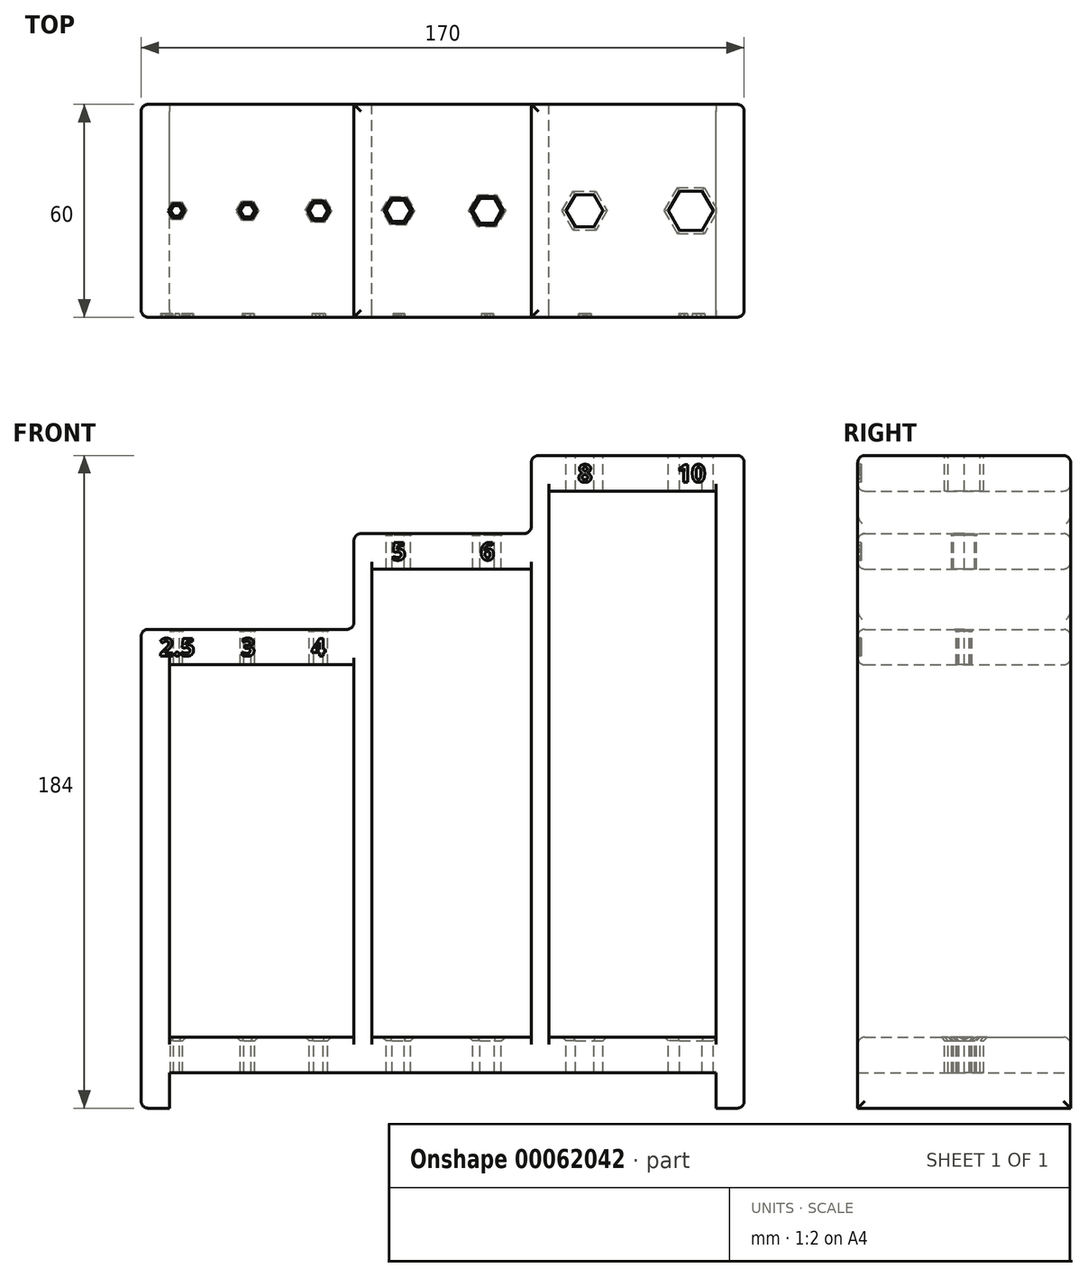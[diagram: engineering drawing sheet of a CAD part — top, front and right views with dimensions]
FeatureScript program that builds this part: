
annotation { "Feature Type Name" : "Feature", "Feature Type Description" : "" }
export const myFeature = defineFeature(function(context is Context, id is Id, definition is map)
    precondition{}
    {
        {
            var Q0;
            Q0=qCreatedBy(makeId("Front.planeOp"),FACE);
            var sketch = newSketch(context, id + "F0", { "sketchPlane" : qUnion([Q0])});
            skLineSegment(sketch, "E0", {"start": v(-75.14, -125) * mm, "end": v(-75.14, 10) * mm});
            skLineSegment(sketch, "E1", {"start": v(-15.14, 10) * mm, "end": v(-15.14, 37) * mm});
            skLineSegment(sketch, "E2", {"start": v(34.86, 37) * mm, "end": v(34.86, 59) * mm});
            skLineSegment(sketch, "E3", {"start": v(94.86, 59) * mm, "end": v(94.86, -125) * mm});
            skLineSegment(sketch, "E4", {"start": v(94.86, -125) * mm, "end": v(86.86, -125) * mm});
            skLineSegment(sketch, "E5", {"start": v(86.86, -125) * mm, "end": v(86.86, -105) * mm});
            skLineSegment(sketch, "E6", {"start": v(86.86, -105) * mm, "end": v(-67.14, -105) * mm});
            skLineSegment(sketch, "E7", {"start": v(-67.14, -105) * mm, "end": v(-67.14, -125) * mm});
            skLineSegment(sketch, "E8", {"start": v(-67.14, -125) * mm, "end": v(-75.14, -125) * mm});
            skLineSegment(sketch, "E9", {"start": v(-67.14, -115) * mm, "end": v(-67.14, 0) * mm});
            skLineSegment(sketch, "E10", {"start": v(-10.14, 0) * mm, "end": v(-10.14, 27) * mm});
            skLineSegment(sketch, "E11", {"start": v(39.86, 27) * mm, "end": v(39.86, 49) * mm});
            skLineSegment(sketch, "E12", {"start": v(86.86, 49) * mm, "end": v(86.86, -115) * mm});
            skLineSegment(sketch, "E13", {"start": v(86.86, -115) * mm, "end": v(-67.14, -115) * mm});
            skLineSegment(sketch, "E14", {"start": v(-15.14, 10) * mm, "end": v(-15.14, 0) * mm, "construction": true});
            skLineSegment(sketch, "E15", {"start": v(34.86, 37) * mm, "end": v(34.86, 27) * mm, "construction": true});
            skLineSegment(sketch, "E16", {"start": v(-67.14, -115) * mm, "end": v(-75.14, -115) * mm, "construction": true});
            skLineSegment(sketch, "E17", {"start": v(86.86, -115) * mm, "end": v(94.86, -115) * mm, "construction": true});
            skLineSegment(sketch, "E18.top", {"start": v(-15.14, -105) * mm, "end": v(-10.14, -105) * mm});
            skLineSegment(sketch, "E18.left", {"start": v(-15.14, 0) * mm, "end": v(-15.14, -105) * mm});
            skLineSegment(sketch, "E18.right", {"start": v(-10.14, 0) * mm, "end": v(-10.14, -105) * mm});
            skLineSegment(sketch, "E19.top", {"start": v(34.86, -105) * mm, "end": v(39.86, -105) * mm});
            skLineSegment(sketch, "E19.left", {"start": v(34.86, 27) * mm, "end": v(34.86, -105) * mm});
            skLineSegment(sketch, "E19.right", {"start": v(39.86, 27) * mm, "end": v(39.86, -105) * mm});
            skLineSegment(sketch, "E20", {"start": v(-75.14, 10) * mm, "end": v(-15.14, 10) * mm});
            skLineSegment(sketch, "E21", {"start": v(-67.14, 0) * mm, "end": v(-15.14, 0) * mm});
            skLineSegment(sketch, "E22", {"start": v(-15.14, 37) * mm, "end": v(34.86, 37) * mm});
            skLineSegment(sketch, "E23", {"start": v(-10.14, 27) * mm, "end": v(34.86, 27) * mm});
            skLineSegment(sketch, "E24", {"start": v(-15.14, 0) * mm, "end": v(-10.14, 0) * mm, "construction": true});
            skLineSegment(sketch, "E25", {"start": v(34.86, 27) * mm, "end": v(39.86, 27) * mm, "construction": true});
            skLineSegment(sketch, "E26", {"start": v(34.86, 59) * mm, "end": v(94.86, 59) * mm});
            skLineSegment(sketch, "E27", {"start": v(39.86, 49) * mm, "end": v(86.86, 49) * mm});
            skLineSegment(sketch, "E28", {"start": v(86.86, 49) * mm, "end": v(86.86, 59) * mm, "construction": true});
            skSolve(sketch);
        }
        {
            var Q0;
            Q0=makeQuery(id+"F0.imprint","IMPRINT",FACE,{"disambiguationData":[TD([[makeQuery(id+"F0.imprint","IMPRINT",EDGE,{"derivedFrom":sQuery(id+"F0.wireOp",EDGE,"E0")}),-1.0]])]});
            var Q1;
            {var subQ0=sQuery(id+"F0.wireOp",EDGE,"E6");Q1=makeQuery(id+"F0.imprint","IMPRINT",FACE,{"disambiguationData":[TD([[makeQuery(id+"F0.imprint","IMPRINT",EDGE,{"derivedFrom":subQ0}),1.0]])]});}
            var Q2;
            Q2=makeQuery(id+"F0.imprint","IMPRINT",FACE,{"disambiguationData":[TD([[makeQuery(id+"F0.imprint","IMPRINT",EDGE,{"derivedFrom":sQuery(id+"F0.wireOp",EDGE,"E18.bottom")}),-1.0]])]});
            var Q3;
            Q3=makeQuery(id+"F0.imprint","IMPRINT",FACE,{"disambiguationData":[TD([[makeQuery(id+"F0.imprint","IMPRINT",EDGE,{"derivedFrom":sQuery(id+"F0.wireOp",EDGE,"E19.bottom")}),-1.0]])]});
            extrude(context, id + "F1", {"entities" : qUnion([Q0, Q1, Q2, Q3]), "depth" : 30 * mm, "hasSecondDirection" : true, "secondDirectionOppositeDirection" : true, "secondDirectionDepth" : 30 * mm});
        }
        {
            var Q0;
            Q0=makeQuery(id+"F1.opExtrude","SWEPT_FACE",FACE,{"disambiguationData":[OSD([sQuery(id+"F0.wireOp",EDGE,"E26")])]});
            var sketch = newSketch(context, id + "F2", { "sketchPlane" : qUnion([Q0])});
            skPoint(sketch, "E29", {"position": v(-65.14, 0) * mm});
            skPoint(sketch, "E30", {"position": v(-45.14, 0) * mm});
            skPoint(sketch, "E31", {"position": v(-25.14, 0) * mm});
            skPoint(sketch, "E32", {"position": v(-2.64, 0) * mm});
            skPoint(sketch, "E33", {"position": v(22.36, 0) * mm});
            skPoint(sketch, "E34", {"position": v(49.86, 0) * mm});
            skPoint(sketch, "E35", {"position": v(79.86, 0) * mm});
            skCircle(sketch, "E36.cCircle", {"center": v(-65.14, 0) * mm, "radius": 1.5 * mm, "construction": true});
            skLineSegment(sketch, "E36.0", {"start": v(-64.27, -1.5) * mm, "end": v(-66, -1.5) * mm});
            skLineSegment(sketch, "E36.1", {"start": v(-66, -1.5) * mm, "end": v(-66.87, 0) * mm});
            skLineSegment(sketch, "E36.2", {"start": v(-66.87, 0) * mm, "end": v(-66, 1.5) * mm});
            skLineSegment(sketch, "E36.3", {"start": v(-66, 1.5) * mm, "end": v(-64.27, 1.5) * mm});
            skLineSegment(sketch, "E36.4", {"start": v(-64.27, 1.5) * mm, "end": v(-63.4, 0) * mm});
            skLineSegment(sketch, "E36.5", {"start": v(-63.4, 0) * mm, "end": v(-64.27, -1.5) * mm});
            skPoint(sketch, "E36.0.midPoint", {"position": v(-65.14, -1.5) * mm});
            skCircle(sketch, "E37.cCircle", {"center": v(-45.14, 0) * mm, "radius": 1.75 * mm, "construction": true});
            skLineSegment(sketch, "E37.0", {"start": v(-44.13, -1.75) * mm, "end": v(-46.15, -1.75) * mm});
            skLineSegment(sketch, "E37.1", {"start": v(-46.15, -1.75) * mm, "end": v(-47.16, 0) * mm});
            skLineSegment(sketch, "E37.2", {"start": v(-47.16, 0) * mm, "end": v(-46.15, 1.75) * mm});
            skLineSegment(sketch, "E37.3", {"start": v(-46.15, 1.75) * mm, "end": v(-44.13, 1.75) * mm});
            skLineSegment(sketch, "E37.4", {"start": v(-44.13, 1.75) * mm, "end": v(-43.12, 0) * mm});
            skLineSegment(sketch, "E37.5", {"start": v(-43.12, 0) * mm, "end": v(-44.13, -1.75) * mm});
            skPoint(sketch, "E37.0.midPoint", {"position": v(-45.14, -1.75) * mm});
            skCircle(sketch, "E38.cCircle", {"center": v(-25.14, 0) * mm, "radius": 2.25 * mm, "construction": true});
            skLineSegment(sketch, "E38.0", {"start": v(-23.84, -2.25) * mm, "end": v(-26.44, -2.25) * mm});
            skLineSegment(sketch, "E38.1", {"start": v(-26.44, -2.25) * mm, "end": v(-27.74, 0) * mm});
            skLineSegment(sketch, "E38.2", {"start": v(-27.74, 0) * mm, "end": v(-26.44, 2.25) * mm});
            skLineSegment(sketch, "E38.3", {"start": v(-26.44, 2.25) * mm, "end": v(-23.84, 2.25) * mm});
            skLineSegment(sketch, "E38.4", {"start": v(-23.84, 2.25) * mm, "end": v(-22.54, 0) * mm});
            skLineSegment(sketch, "E38.5", {"start": v(-22.54, 0) * mm, "end": v(-23.84, -2.25) * mm});
            skPoint(sketch, "E38.0.midPoint", {"position": v(-25.14, -2.25) * mm});
            skCircle(sketch, "E39.cCircle", {"center": v(-2.64, 0) * mm, "radius": 3 * mm, "construction": true});
            skLineSegment(sketch, "E39.0", {"start": v(-0.9, -3) * mm, "end": v(-4.37, -3) * mm});
            skLineSegment(sketch, "E39.1", {"start": v(-4.37, -3) * mm, "end": v(-6.1, 0) * mm});
            skLineSegment(sketch, "E39.2", {"start": v(-6.1, 0) * mm, "end": v(-4.37, 3) * mm});
            skLineSegment(sketch, "E39.3", {"start": v(-4.37, 3) * mm, "end": v(-0.9, 3) * mm});
            skLineSegment(sketch, "E39.4", {"start": v(-0.9, 3) * mm, "end": v(0.82, 0) * mm});
            skLineSegment(sketch, "E39.5", {"start": v(0.82, 0) * mm, "end": v(-0.9, -3) * mm});
            skPoint(sketch, "E39.0.midPoint", {"position": v(-2.64, -3) * mm});
            skCircle(sketch, "E40.cCircle", {"center": v(22.36, 0) * mm, "radius": 3.5 * mm, "construction": true});
            skLineSegment(sketch, "E40.0", {"start": v(24.38, -3.5) * mm, "end": v(20.34, -3.5) * mm});
            skLineSegment(sketch, "E40.1", {"start": v(20.34, -3.5) * mm, "end": v(18.32, 0) * mm});
            skLineSegment(sketch, "E40.2", {"start": v(18.32, 0) * mm, "end": v(20.34, 3.5) * mm});
            skLineSegment(sketch, "E40.3", {"start": v(20.34, 3.5) * mm, "end": v(24.38, 3.5) * mm});
            skLineSegment(sketch, "E40.4", {"start": v(24.38, 3.5) * mm, "end": v(26.4, 0) * mm});
            skLineSegment(sketch, "E40.5", {"start": v(26.4, 0) * mm, "end": v(24.38, -3.5) * mm});
            skPoint(sketch, "E40.0.midPoint", {"position": v(22.36, -3.5) * mm});
            skCircle(sketch, "E41.cCircle", {"center": v(49.86, 0) * mm, "radius": 4.5 * mm, "construction": true});
            skLineSegment(sketch, "E41.0", {"start": v(52.46, -4.5) * mm, "end": v(47.26, -4.5) * mm});
            skLineSegment(sketch, "E41.1", {"start": v(47.26, -4.5) * mm, "end": v(44.66, 0) * mm});
            skLineSegment(sketch, "E41.2", {"start": v(44.66, 0) * mm, "end": v(47.26, 4.5) * mm});
            skLineSegment(sketch, "E41.3", {"start": v(47.26, 4.5) * mm, "end": v(52.46, 4.5) * mm});
            skLineSegment(sketch, "E41.4", {"start": v(52.46, 4.5) * mm, "end": v(55.06, 0) * mm});
            skLineSegment(sketch, "E41.5", {"start": v(55.06, 0) * mm, "end": v(52.46, -4.5) * mm});
            skPoint(sketch, "E41.0.midPoint", {"position": v(49.86, -4.5) * mm});
            skCircle(sketch, "E42.cCircle", {"center": v(79.86, 0) * mm, "radius": 5.5 * mm, "construction": true});
            skLineSegment(sketch, "E42.0", {"start": v(83.04, -5.5) * mm, "end": v(76.68, -5.5) * mm});
            skLineSegment(sketch, "E42.1", {"start": v(76.68, -5.5) * mm, "end": v(73.5, 0) * mm});
            skLineSegment(sketch, "E42.2", {"start": v(73.5, 0) * mm, "end": v(76.68, 5.5) * mm});
            skLineSegment(sketch, "E42.3", {"start": v(76.68, 5.5) * mm, "end": v(83.04, 5.5) * mm});
            skLineSegment(sketch, "E42.4", {"start": v(83.04, 5.5) * mm, "end": v(86.21, 0) * mm});
            skLineSegment(sketch, "E42.5", {"start": v(86.21, 0) * mm, "end": v(83.04, -5.5) * mm});
            skPoint(sketch, "E42.0.midPoint", {"position": v(79.86, -5.5) * mm});
            skSolve(sketch);
        }
        {
            var Q0;
            Q0 = qSketchRegion(id + "F2", true);
            var Q1;
            Q1=makeQuery(id+"F1.opExtrude","SWEPT_FACE",FACE,{"disambiguationData":[OSD([sQuery(id+"F0.wireOp",EDGE,"E13")])]});
            extrude(context, id + "F3", {"entities" : qUnion([Q0]), "operationType" : NewBodyOperationType.REMOVE, "endBound" : BoundingType.UP_TO_SURFACE, "oppositeDirection" : true, "endBoundEntityFace" : qUnion([Q1]), "depth" : 25 * mm});
        }
        {
            var Q0;
            Q0=makeQuery(id+"F1.opExtrude","CAP_FACE",FACE,{"disambiguationData":[OSD([sQuery(id+"F0.wireOp",EDGE,"E0"),sQuery(id+"F0.wireOp",EDGE,"GeTEZKgD-VleB-Pjne-Csjp-ZGMRxHWfVuPL"),sQuery(id+"F0.wireOp",EDGE,"BGaEOWcr-Agjj-6xs9-L2Rh-NUqZqpChWdlD"),sQuery(id+"F0.wireOp",EDGE,"vs9bMPzk-kOSz-00Uc-mebz-TYH7VpvHUvR8"),sQuery(id+"F0.wireOp",EDGE,"E1"),sQuery(id+"F0.wireOp",EDGE,"rwazvfQN-wWWd-rmfp-GgQa-C1WE00IXPOYZ"),sQuery(id+"F0.wireOp",EDGE,"TIjLVdis-FRbo-cTZn-IHn7-8XoxnhnPgcRK"),sQuery(id+"F0.wireOp",EDGE,"E2"),sQuery(id+"F0.wireOp",EDGE,"HWJ4689Y-KtwG-vJfG-xgFW-nUAPGrujgrIx"),sQuery(id+"F0.wireOp",EDGE,"6eoJVVgg-XjGH-Rh0S-0Ck7-eEfTqSEG6dff"),sQuery(id+"F0.wireOp",EDGE,"E3"),sQuery(id+"F0.wireOp",EDGE,"E4"),sQuery(id+"F0.wireOp",EDGE,"E5"),sQuery(id+"F0.wireOp",EDGE,"E6"),sQuery(id+"F0.wireOp",EDGE,"E7"),sQuery(id+"F0.wireOp",EDGE,"E8"),sQuery(id+"F0.wireOp",EDGE,"E9"),sQuery(id+"F0.wireOp",EDGE,"dsDfZTNB-jOaL-EM2F-YRw7-LjKbeeutn0S7"),sQuery(id+"F0.wireOp",EDGE,"riOj0wsW-8ntY-M8XJ-Dudd-JfplwehwjU5x"),sQuery(id+"F0.wireOp",EDGE,"ikqcAXUb-zJlV-DiQM-P86k-rxCfW60V950E"),sQuery(id+"F0.wireOp",EDGE,"E10"),sQuery(id+"F0.wireOp",EDGE,"oe37zDZS-dTc5-Nd6g-8xnc-qUGsxS7KHp88"),sQuery(id+"F0.wireOp",EDGE,"aYTTs3A4-9fB0-4VRp-raIi-XGU3Sh0ihZd7"),sQuery(id+"F0.wireOp",EDGE,"E11"),sQuery(id+"F0.wireOp",EDGE,"6ZUmFo40-9iyz-N38K-DDh6-QmUHhMkESyf1"),sQuery(id+"F0.wireOp",EDGE,"4iT4Aycs-cVef-0BnO-rxrT-2gsYZ1b7QhIN"),sQuery(id+"F0.wireOp",EDGE,"E12"),sQuery(id+"F0.wireOp",EDGE,"E13")])],"isStart":false});
            var sketch = newSketch(context, id + "F4", { "sketchPlane" : qUnion([Q0])});
            skLineSegment(sketch, "E43", {"start": v(-65.14, 10) * mm, "end": v(-65.14, 0) * mm, "construction": true});
            skText(sketch, "E44", { "text": "2.5", "fontName": "OpenSans-Bold.ttf"});
            skPoint(sketch, "E45", {"position": v(-65.14, 5) * mm});
            skLineSegment(sketch, "E46", {"start": v(-45.14, 10) * mm, "end": v(-45.14, 0) * mm, "construction": true});
            skLineSegment(sketch, "E47", {"start": v(-25.14, 10) * mm, "end": v(-25.14, 0) * mm, "construction": true});
            skLineSegment(sketch, "E48", {"start": v(-2.64, 37) * mm, "end": v(-2.64, 27) * mm, "construction": true});
            skLineSegment(sketch, "E49", {"start": v(22.36, 37) * mm, "end": v(22.36, 27) * mm, "construction": true});
            skLineSegment(sketch, "E50", {"start": v(49.86, 59) * mm, "end": v(49.86, 49) * mm, "construction": true});
            skLineSegment(sketch, "E51", {"start": v(79.86, 59) * mm, "end": v(79.86, 49) * mm, "construction": true});
            skText(sketch, "E52", { "text": "3", "fontName": "OpenSans-Bold.ttf"});
            skPoint(sketch, "E53", {"position": v(-45.14, 5) * mm});
            skText(sketch, "E54", { "text": "4", "fontName": "OpenSans-Bold.ttf"});
            skPoint(sketch, "E55", {"position": v(-25.14, 5) * mm});
            skText(sketch, "E56", { "text": "5", "fontName": "OpenSans-Bold.ttf"});
            skPoint(sketch, "E57", {"position": v(-2.64, 32) * mm});
            skText(sketch, "E58", { "text": "6", "fontName": "OpenSans-Bold.ttf"});
            skPoint(sketch, "E59", {"position": v(22.36, 32) * mm});
            skText(sketch, "E60", { "text": "8", "fontName": "OpenSans-Bold.ttf"});
            skText(sketch, "E61", { "text": "10", "fontName": "OpenSans-Bold.ttf"});
            skPoint(sketch, "E62", {"position": v(49.86, 54) * mm});
            skPoint(sketch, "E63", {"position": v(79.86, 54) * mm});
            const initialGuessF4  = {"E44": [-0.06994, 0.0025, 1, 0, 0.005], "E52": [-0.04699, 0.0025, 1, 0, 0.005], "E54": [-0.02707, 0.0025, 1, 0, 0.005], "E56": [-0.00447, 0.0295, 1, 0, 0.005], "E58": [0.02049, 0.0295, 1, 0, 0.005], "E60": [0.048, 0.0515, 1, 0, 0.005], "E61": [0.07602, 0.0515, 1, 0, 0.005]};
            skSetInitialGuess(sketch, initialGuessF4);
            skSolve(sketch);
        }
        {
            var Q0;
            Q0 = qSketchRegion(id + "F4", true);
            extrude(context, id + "F5", {"entities" : qUnion([Q0]), "operationType" : NewBodyOperationType.REMOVE, "oppositeDirection" : true, "depth" : 1 * mm});
        }
        {
            var Q0;
            {var subQ0=sQuery(id+"F0.wireOp",EDGE,"E6");var subQ1=sQuery(id+"F0.wireOp",EDGE,"E18.top");var subQ2=makeQuery(id+"F1.opExtrude","SWEPT_FACE",FACE,{"disambiguationData":[OSD([subQ0]),TDD([makeQuery(id+"F0.imprint","IMPRINT",EDGE,{"disambiguationData":[TD([[makeQuery(id+"F0.imprint","INTERSECT",VERTEX,{"derivedFrom":[subQ0,sQuery(id+"F0.wireOp",EDGE,"E9")]}),1.0]])],"derivedFrom":subQ0})])]});var subQ4=makeQuery(id+"F1.opExtrude","SWEPT_FACE",FACE,{"disambiguationData":[OSD([subQ0]),TDD([makeQuery(id+"F0.imprint","IMPRINT",EDGE,{"disambiguationData":[TD([[makeQuery(id+"F0.imprint","INTERSECT",VERTEX,{"derivedFrom":[subQ0,subQ1,sQuery(id+"F0.wireOp",EDGE,"E18.right")]}),1.0]])],"derivedFrom":subQ0})])]});var subQ5=makeQuery(id+"F1.opExtrude","SWEPT_FACE",FACE,{"disambiguationData":[OSD([subQ0]),TDD([makeQuery(id+"F0.imprint","IMPRINT",EDGE,{"disambiguationData":[TD([[makeQuery(id+"F0.imprint","INTERSECT",VERTEX,{"derivedFrom":[subQ0,sQuery(id+"F0.wireOp",EDGE,"E12")]}),-1.0]])],"derivedFrom":subQ0})])]});Q0=qUnion([makeQuery(id+"F3.boolean.opBoolean","INTERSECT",EDGE,{"derivedFrom":[subQ5,makeQuery(id+"F3.opExtrude","SWEPT_FACE",FACE,{"disambiguationData":[OSD([sQuery(id+"F2.wireOp",EDGE,"E41.0")])]})]}),makeQuery(id+"F3.boolean.opBoolean","INTERSECT",EDGE,{"derivedFrom":[subQ5,makeQuery(id+"F3.opExtrude","SWEPT_FACE",FACE,{"disambiguationData":[OSD([sQuery(id+"F2.wireOp",EDGE,"E41.1")])]})]}),makeQuery(id+"F3.boolean.opBoolean","INTERSECT",EDGE,{"derivedFrom":[subQ5,makeQuery(id+"F3.opExtrude","SWEPT_FACE",FACE,{"disambiguationData":[OSD([sQuery(id+"F2.wireOp",EDGE,"E41.2")])]})]}),makeQuery(id+"F3.boolean.opBoolean","INTERSECT",EDGE,{"derivedFrom":[subQ5,makeQuery(id+"F3.opExtrude","SWEPT_FACE",FACE,{"disambiguationData":[OSD([sQuery(id+"F2.wireOp",EDGE,"E41.3")])]})]}),makeQuery(id+"F3.boolean.opBoolean","INTERSECT",EDGE,{"derivedFrom":[subQ5,makeQuery(id+"F3.opExtrude","SWEPT_FACE",FACE,{"disambiguationData":[OSD([sQuery(id+"F2.wireOp",EDGE,"E41.4")])]})]}),makeQuery(id+"F3.boolean.opBoolean","INTERSECT",EDGE,{"derivedFrom":[subQ5,makeQuery(id+"F3.opExtrude","SWEPT_FACE",FACE,{"disambiguationData":[OSD([sQuery(id+"F2.wireOp",EDGE,"E41.5")])]})]}),makeQuery(id+"F3.boolean.opBoolean","INTERSECT",EDGE,{"derivedFrom":[subQ5,makeQuery(id+"F3.opExtrude","SWEPT_FACE",FACE,{"disambiguationData":[OSD([sQuery(id+"F2.wireOp",EDGE,"E42.0")])]})]}),makeQuery(id+"F3.boolean.opBoolean","INTERSECT",EDGE,{"derivedFrom":[subQ5,makeQuery(id+"F3.opExtrude","SWEPT_FACE",FACE,{"disambiguationData":[OSD([sQuery(id+"F2.wireOp",EDGE,"E42.1")])]})]}),makeQuery(id+"F3.boolean.opBoolean","INTERSECT",EDGE,{"derivedFrom":[subQ5,makeQuery(id+"F3.opExtrude","SWEPT_FACE",FACE,{"disambiguationData":[OSD([sQuery(id+"F2.wireOp",EDGE,"E42.2")])]})]}),makeQuery(id+"F3.boolean.opBoolean","INTERSECT",EDGE,{"derivedFrom":[subQ5,makeQuery(id+"F3.opExtrude","SWEPT_FACE",FACE,{"disambiguationData":[OSD([sQuery(id+"F2.wireOp",EDGE,"E42.3")])]})]}),makeQuery(id+"F3.boolean.opBoolean","INTERSECT",EDGE,{"derivedFrom":[subQ5,makeQuery(id+"F3.opExtrude","SWEPT_FACE",FACE,{"disambiguationData":[OSD([sQuery(id+"F2.wireOp",EDGE,"E42.4")])]})]}),makeQuery(id+"F3.boolean.opBoolean","INTERSECT",EDGE,{"derivedFrom":[subQ5,makeQuery(id+"F3.opExtrude","SWEPT_FACE",FACE,{"disambiguationData":[OSD([sQuery(id+"F2.wireOp",EDGE,"E42.5")])]})]}),makeQuery(id+"F3.boolean.opBoolean","INTERSECT",EDGE,{"derivedFrom":[subQ4,makeQuery(id+"F3.opExtrude","SWEPT_FACE",FACE,{"disambiguationData":[OSD([sQuery(id+"F2.wireOp",EDGE,"E39.0")])]})]}),makeQuery(id+"F3.boolean.opBoolean","INTERSECT",EDGE,{"derivedFrom":[subQ4,makeQuery(id+"F3.opExtrude","SWEPT_FACE",FACE,{"disambiguationData":[OSD([sQuery(id+"F2.wireOp",EDGE,"E39.1")])]})]}),makeQuery(id+"F3.boolean.opBoolean","INTERSECT",EDGE,{"derivedFrom":[subQ4,makeQuery(id+"F3.opExtrude","SWEPT_FACE",FACE,{"disambiguationData":[OSD([sQuery(id+"F2.wireOp",EDGE,"E39.2")])]})]}),makeQuery(id+"F3.boolean.opBoolean","INTERSECT",EDGE,{"derivedFrom":[subQ4,makeQuery(id+"F3.opExtrude","SWEPT_FACE",FACE,{"disambiguationData":[OSD([sQuery(id+"F2.wireOp",EDGE,"E39.3")])]})]}),makeQuery(id+"F3.boolean.opBoolean","INTERSECT",EDGE,{"derivedFrom":[subQ4,makeQuery(id+"F3.opExtrude","SWEPT_FACE",FACE,{"disambiguationData":[OSD([sQuery(id+"F2.wireOp",EDGE,"E39.4")])]})]}),makeQuery(id+"F3.boolean.opBoolean","INTERSECT",EDGE,{"derivedFrom":[subQ4,makeQuery(id+"F3.opExtrude","SWEPT_FACE",FACE,{"disambiguationData":[OSD([sQuery(id+"F2.wireOp",EDGE,"E39.5")])]})]}),makeQuery(id+"F3.boolean.opBoolean","INTERSECT",EDGE,{"derivedFrom":[subQ4,makeQuery(id+"F3.opExtrude","SWEPT_FACE",FACE,{"disambiguationData":[OSD([sQuery(id+"F2.wireOp",EDGE,"E40.0")])]})]}),makeQuery(id+"F3.boolean.opBoolean","INTERSECT",EDGE,{"derivedFrom":[subQ4,makeQuery(id+"F3.opExtrude","SWEPT_FACE",FACE,{"disambiguationData":[OSD([sQuery(id+"F2.wireOp",EDGE,"E40.1")])]})]}),makeQuery(id+"F3.boolean.opBoolean","INTERSECT",EDGE,{"derivedFrom":[subQ4,makeQuery(id+"F3.opExtrude","SWEPT_FACE",FACE,{"disambiguationData":[OSD([sQuery(id+"F2.wireOp",EDGE,"E40.2")])]})]}),makeQuery(id+"F3.boolean.opBoolean","INTERSECT",EDGE,{"derivedFrom":[subQ4,makeQuery(id+"F3.opExtrude","SWEPT_FACE",FACE,{"disambiguationData":[OSD([sQuery(id+"F2.wireOp",EDGE,"E40.3")])]})]}),makeQuery(id+"F3.boolean.opBoolean","INTERSECT",EDGE,{"derivedFrom":[subQ4,makeQuery(id+"F3.opExtrude","SWEPT_FACE",FACE,{"disambiguationData":[OSD([sQuery(id+"F2.wireOp",EDGE,"E40.4")])]})]}),makeQuery(id+"F3.boolean.opBoolean","INTERSECT",EDGE,{"derivedFrom":[subQ4,makeQuery(id+"F3.opExtrude","SWEPT_FACE",FACE,{"disambiguationData":[OSD([sQuery(id+"F2.wireOp",EDGE,"E40.5")])]})]}),makeQuery(id+"F3.boolean.opBoolean","INTERSECT",EDGE,{"derivedFrom":[subQ2,makeQuery(id+"F3.opExtrude","SWEPT_FACE",FACE,{"disambiguationData":[OSD([sQuery(id+"F2.wireOp",EDGE,"E36.0")])]})]}),makeQuery(id+"F3.boolean.opBoolean","INTERSECT",EDGE,{"derivedFrom":[subQ2,makeQuery(id+"F3.opExtrude","SWEPT_FACE",FACE,{"disambiguationData":[OSD([sQuery(id+"F2.wireOp",EDGE,"E36.1")])]})]}),makeQuery(id+"F3.boolean.opBoolean","INTERSECT",EDGE,{"derivedFrom":[subQ2,makeQuery(id+"F3.opExtrude","SWEPT_FACE",FACE,{"disambiguationData":[OSD([sQuery(id+"F2.wireOp",EDGE,"E36.2")])]})]}),makeQuery(id+"F3.boolean.opBoolean","INTERSECT",EDGE,{"derivedFrom":[subQ2,makeQuery(id+"F3.opExtrude","SWEPT_FACE",FACE,{"disambiguationData":[OSD([sQuery(id+"F2.wireOp",EDGE,"E36.3")])]})]}),makeQuery(id+"F3.boolean.opBoolean","INTERSECT",EDGE,{"derivedFrom":[subQ2,makeQuery(id+"F3.opExtrude","SWEPT_FACE",FACE,{"disambiguationData":[OSD([sQuery(id+"F2.wireOp",EDGE,"E36.4")])]})]}),makeQuery(id+"F3.boolean.opBoolean","INTERSECT",EDGE,{"derivedFrom":[subQ2,makeQuery(id+"F3.opExtrude","SWEPT_FACE",FACE,{"disambiguationData":[OSD([sQuery(id+"F2.wireOp",EDGE,"E36.5")])]})]}),makeQuery(id+"F3.boolean.opBoolean","INTERSECT",EDGE,{"derivedFrom":[subQ2,makeQuery(id+"F3.opExtrude","SWEPT_FACE",FACE,{"disambiguationData":[OSD([sQuery(id+"F2.wireOp",EDGE,"E37.0")])]})]}),makeQuery(id+"F3.boolean.opBoolean","INTERSECT",EDGE,{"derivedFrom":[subQ2,makeQuery(id+"F3.opExtrude","SWEPT_FACE",FACE,{"disambiguationData":[OSD([sQuery(id+"F2.wireOp",EDGE,"E37.1")])]})]}),makeQuery(id+"F3.boolean.opBoolean","INTERSECT",EDGE,{"derivedFrom":[subQ2,makeQuery(id+"F3.opExtrude","SWEPT_FACE",FACE,{"disambiguationData":[OSD([sQuery(id+"F2.wireOp",EDGE,"E37.2")])]})]}),makeQuery(id+"F3.boolean.opBoolean","INTERSECT",EDGE,{"derivedFrom":[subQ2,makeQuery(id+"F3.opExtrude","SWEPT_FACE",FACE,{"disambiguationData":[OSD([sQuery(id+"F2.wireOp",EDGE,"E37.3")])]})]}),makeQuery(id+"F3.boolean.opBoolean","INTERSECT",EDGE,{"derivedFrom":[subQ2,makeQuery(id+"F3.opExtrude","SWEPT_FACE",FACE,{"disambiguationData":[OSD([sQuery(id+"F2.wireOp",EDGE,"E37.4")])]})]}),makeQuery(id+"F3.boolean.opBoolean","INTERSECT",EDGE,{"derivedFrom":[subQ2,makeQuery(id+"F3.opExtrude","SWEPT_FACE",FACE,{"disambiguationData":[OSD([sQuery(id+"F2.wireOp",EDGE,"E37.5")])]})]}),makeQuery(id+"F3.boolean.opBoolean","INTERSECT",EDGE,{"derivedFrom":[subQ2,makeQuery(id+"F3.opExtrude","SWEPT_FACE",FACE,{"disambiguationData":[OSD([sQuery(id+"F2.wireOp",EDGE,"E38.0")])]})]}),makeQuery(id+"F3.boolean.opBoolean","INTERSECT",EDGE,{"derivedFrom":[subQ2,makeQuery(id+"F3.opExtrude","SWEPT_FACE",FACE,{"disambiguationData":[OSD([sQuery(id+"F2.wireOp",EDGE,"E38.1")])]})]}),makeQuery(id+"F3.boolean.opBoolean","INTERSECT",EDGE,{"derivedFrom":[subQ2,makeQuery(id+"F3.opExtrude","SWEPT_FACE",FACE,{"disambiguationData":[OSD([sQuery(id+"F2.wireOp",EDGE,"E38.2")])]})]}),makeQuery(id+"F3.boolean.opBoolean","INTERSECT",EDGE,{"derivedFrom":[subQ2,makeQuery(id+"F3.opExtrude","SWEPT_FACE",FACE,{"disambiguationData":[OSD([sQuery(id+"F2.wireOp",EDGE,"E38.3")])]})]}),makeQuery(id+"F3.boolean.opBoolean","INTERSECT",EDGE,{"derivedFrom":[subQ2,makeQuery(id+"F3.opExtrude","SWEPT_FACE",FACE,{"disambiguationData":[OSD([sQuery(id+"F2.wireOp",EDGE,"E38.4")])]})]}),makeQuery(id+"F3.boolean.opBoolean","INTERSECT",EDGE,{"derivedFrom":[subQ2,makeQuery(id+"F3.opExtrude","SWEPT_FACE",FACE,{"disambiguationData":[OSD([sQuery(id+"F2.wireOp",EDGE,"E38.5")])]})]})]);}
            var Q1;
            {var subQ0=sQuery(id+"F0.wireOp",EDGE,"E6");var subQ1=sQuery(id+"F0.wireOp",EDGE,"E18.top");var subQ2=makeQuery(id+"F1.opExtrude","SWEPT_FACE",FACE,{"disambiguationData":[OSD([subQ0]),TDD([makeQuery(id+"F0.imprint","IMPRINT",EDGE,{"disambiguationData":[TD([[makeQuery(id+"F0.imprint","INTERSECT",VERTEX,{"derivedFrom":[subQ0,sQuery(id+"F0.wireOp",EDGE,"E9")]}),1.0]])],"derivedFrom":subQ0})])]});var subQ4=makeQuery(id+"F1.opExtrude","SWEPT_FACE",FACE,{"disambiguationData":[OSD([subQ0]),TDD([makeQuery(id+"F0.imprint","IMPRINT",EDGE,{"disambiguationData":[TD([[makeQuery(id+"F0.imprint","INTERSECT",VERTEX,{"derivedFrom":[subQ0,subQ1,sQuery(id+"F0.wireOp",EDGE,"E18.right")]}),1.0]])],"derivedFrom":subQ0})])]});var subQ5=makeQuery(id+"F1.opExtrude","SWEPT_FACE",FACE,{"disambiguationData":[OSD([subQ0]),TDD([makeQuery(id+"F0.imprint","IMPRINT",EDGE,{"disambiguationData":[TD([[makeQuery(id+"F0.imprint","INTERSECT",VERTEX,{"derivedFrom":[subQ0,sQuery(id+"F0.wireOp",EDGE,"E12")]}),-1.0]])],"derivedFrom":subQ0})])]});Q1=qUnion([makeQuery(id+"F3.boolean.opBoolean","INTERSECT",EDGE,{"derivedFrom":[subQ5,makeQuery(id+"F3.opExtrude","SWEPT_FACE",FACE,{"disambiguationData":[OSD([sQuery(id+"F2.wireOp",EDGE,"E41.0")])]})]}),makeQuery(id+"F3.boolean.opBoolean","INTERSECT",EDGE,{"derivedFrom":[subQ5,makeQuery(id+"F3.opExtrude","SWEPT_FACE",FACE,{"disambiguationData":[OSD([sQuery(id+"F2.wireOp",EDGE,"E41.1")])]})]}),makeQuery(id+"F3.boolean.opBoolean","INTERSECT",EDGE,{"derivedFrom":[subQ5,makeQuery(id+"F3.opExtrude","SWEPT_FACE",FACE,{"disambiguationData":[OSD([sQuery(id+"F2.wireOp",EDGE,"E41.2")])]})]}),makeQuery(id+"F3.boolean.opBoolean","INTERSECT",EDGE,{"derivedFrom":[subQ5,makeQuery(id+"F3.opExtrude","SWEPT_FACE",FACE,{"disambiguationData":[OSD([sQuery(id+"F2.wireOp",EDGE,"E41.3")])]})]}),makeQuery(id+"F3.boolean.opBoolean","INTERSECT",EDGE,{"derivedFrom":[subQ5,makeQuery(id+"F3.opExtrude","SWEPT_FACE",FACE,{"disambiguationData":[OSD([sQuery(id+"F2.wireOp",EDGE,"E41.4")])]})]}),makeQuery(id+"F3.boolean.opBoolean","INTERSECT",EDGE,{"derivedFrom":[subQ5,makeQuery(id+"F3.opExtrude","SWEPT_FACE",FACE,{"disambiguationData":[OSD([sQuery(id+"F2.wireOp",EDGE,"E41.5")])]})]}),makeQuery(id+"F3.boolean.opBoolean","INTERSECT",EDGE,{"derivedFrom":[subQ5,makeQuery(id+"F3.opExtrude","SWEPT_FACE",FACE,{"disambiguationData":[OSD([sQuery(id+"F2.wireOp",EDGE,"E42.0")])]})]}),makeQuery(id+"F3.boolean.opBoolean","INTERSECT",EDGE,{"derivedFrom":[subQ5,makeQuery(id+"F3.opExtrude","SWEPT_FACE",FACE,{"disambiguationData":[OSD([sQuery(id+"F2.wireOp",EDGE,"E42.1")])]})]}),makeQuery(id+"F3.boolean.opBoolean","INTERSECT",EDGE,{"derivedFrom":[subQ5,makeQuery(id+"F3.opExtrude","SWEPT_FACE",FACE,{"disambiguationData":[OSD([sQuery(id+"F2.wireOp",EDGE,"E42.2")])]})]}),makeQuery(id+"F3.boolean.opBoolean","INTERSECT",EDGE,{"derivedFrom":[subQ5,makeQuery(id+"F3.opExtrude","SWEPT_FACE",FACE,{"disambiguationData":[OSD([sQuery(id+"F2.wireOp",EDGE,"E42.3")])]})]}),makeQuery(id+"F3.boolean.opBoolean","INTERSECT",EDGE,{"derivedFrom":[subQ5,makeQuery(id+"F3.opExtrude","SWEPT_FACE",FACE,{"disambiguationData":[OSD([sQuery(id+"F2.wireOp",EDGE,"E42.4")])]})]}),makeQuery(id+"F3.boolean.opBoolean","INTERSECT",EDGE,{"derivedFrom":[subQ5,makeQuery(id+"F3.opExtrude","SWEPT_FACE",FACE,{"disambiguationData":[OSD([sQuery(id+"F2.wireOp",EDGE,"E42.5")])]})]}),makeQuery(id+"F3.boolean.opBoolean","INTERSECT",EDGE,{"derivedFrom":[subQ4,makeQuery(id+"F3.opExtrude","SWEPT_FACE",FACE,{"disambiguationData":[OSD([sQuery(id+"F2.wireOp",EDGE,"E39.0")])]})]}),makeQuery(id+"F3.boolean.opBoolean","INTERSECT",EDGE,{"derivedFrom":[subQ4,makeQuery(id+"F3.opExtrude","SWEPT_FACE",FACE,{"disambiguationData":[OSD([sQuery(id+"F2.wireOp",EDGE,"E39.1")])]})]}),makeQuery(id+"F3.boolean.opBoolean","INTERSECT",EDGE,{"derivedFrom":[subQ4,makeQuery(id+"F3.opExtrude","SWEPT_FACE",FACE,{"disambiguationData":[OSD([sQuery(id+"F2.wireOp",EDGE,"E39.2")])]})]}),makeQuery(id+"F3.boolean.opBoolean","INTERSECT",EDGE,{"derivedFrom":[subQ4,makeQuery(id+"F3.opExtrude","SWEPT_FACE",FACE,{"disambiguationData":[OSD([sQuery(id+"F2.wireOp",EDGE,"E39.3")])]})]}),makeQuery(id+"F3.boolean.opBoolean","INTERSECT",EDGE,{"derivedFrom":[subQ4,makeQuery(id+"F3.opExtrude","SWEPT_FACE",FACE,{"disambiguationData":[OSD([sQuery(id+"F2.wireOp",EDGE,"E39.4")])]})]}),makeQuery(id+"F3.boolean.opBoolean","INTERSECT",EDGE,{"derivedFrom":[subQ4,makeQuery(id+"F3.opExtrude","SWEPT_FACE",FACE,{"disambiguationData":[OSD([sQuery(id+"F2.wireOp",EDGE,"E39.5")])]})]}),makeQuery(id+"F3.boolean.opBoolean","INTERSECT",EDGE,{"derivedFrom":[subQ4,makeQuery(id+"F3.opExtrude","SWEPT_FACE",FACE,{"disambiguationData":[OSD([sQuery(id+"F2.wireOp",EDGE,"E40.0")])]})]}),makeQuery(id+"F3.boolean.opBoolean","INTERSECT",EDGE,{"derivedFrom":[subQ4,makeQuery(id+"F3.opExtrude","SWEPT_FACE",FACE,{"disambiguationData":[OSD([sQuery(id+"F2.wireOp",EDGE,"E40.1")])]})]}),makeQuery(id+"F3.boolean.opBoolean","INTERSECT",EDGE,{"derivedFrom":[subQ4,makeQuery(id+"F3.opExtrude","SWEPT_FACE",FACE,{"disambiguationData":[OSD([sQuery(id+"F2.wireOp",EDGE,"E40.2")])]})]}),makeQuery(id+"F3.boolean.opBoolean","INTERSECT",EDGE,{"derivedFrom":[subQ4,makeQuery(id+"F3.opExtrude","SWEPT_FACE",FACE,{"disambiguationData":[OSD([sQuery(id+"F2.wireOp",EDGE,"E40.3")])]})]}),makeQuery(id+"F3.boolean.opBoolean","INTERSECT",EDGE,{"derivedFrom":[subQ4,makeQuery(id+"F3.opExtrude","SWEPT_FACE",FACE,{"disambiguationData":[OSD([sQuery(id+"F2.wireOp",EDGE,"E40.4")])]})]}),makeQuery(id+"F3.boolean.opBoolean","INTERSECT",EDGE,{"derivedFrom":[subQ4,makeQuery(id+"F3.opExtrude","SWEPT_FACE",FACE,{"disambiguationData":[OSD([sQuery(id+"F2.wireOp",EDGE,"E40.5")])]})]}),makeQuery(id+"F3.boolean.opBoolean","INTERSECT",EDGE,{"derivedFrom":[subQ2,makeQuery(id+"F3.opExtrude","SWEPT_FACE",FACE,{"disambiguationData":[OSD([sQuery(id+"F2.wireOp",EDGE,"E36.0")])]})]}),makeQuery(id+"F3.boolean.opBoolean","INTERSECT",EDGE,{"derivedFrom":[subQ2,makeQuery(id+"F3.opExtrude","SWEPT_FACE",FACE,{"disambiguationData":[OSD([sQuery(id+"F2.wireOp",EDGE,"E36.1")])]})]}),makeQuery(id+"F3.boolean.opBoolean","INTERSECT",EDGE,{"derivedFrom":[subQ2,makeQuery(id+"F3.opExtrude","SWEPT_FACE",FACE,{"disambiguationData":[OSD([sQuery(id+"F2.wireOp",EDGE,"E36.2")])]})]}),makeQuery(id+"F3.boolean.opBoolean","INTERSECT",EDGE,{"derivedFrom":[subQ2,makeQuery(id+"F3.opExtrude","SWEPT_FACE",FACE,{"disambiguationData":[OSD([sQuery(id+"F2.wireOp",EDGE,"E36.3")])]})]}),makeQuery(id+"F3.boolean.opBoolean","INTERSECT",EDGE,{"derivedFrom":[subQ2,makeQuery(id+"F3.opExtrude","SWEPT_FACE",FACE,{"disambiguationData":[OSD([sQuery(id+"F2.wireOp",EDGE,"E36.4")])]})]}),makeQuery(id+"F3.boolean.opBoolean","INTERSECT",EDGE,{"derivedFrom":[subQ2,makeQuery(id+"F3.opExtrude","SWEPT_FACE",FACE,{"disambiguationData":[OSD([sQuery(id+"F2.wireOp",EDGE,"E36.5")])]})]}),makeQuery(id+"F3.boolean.opBoolean","INTERSECT",EDGE,{"derivedFrom":[subQ2,makeQuery(id+"F3.opExtrude","SWEPT_FACE",FACE,{"disambiguationData":[OSD([sQuery(id+"F2.wireOp",EDGE,"E37.0")])]})]}),makeQuery(id+"F3.boolean.opBoolean","INTERSECT",EDGE,{"derivedFrom":[subQ2,makeQuery(id+"F3.opExtrude","SWEPT_FACE",FACE,{"disambiguationData":[OSD([sQuery(id+"F2.wireOp",EDGE,"E37.1")])]})]}),makeQuery(id+"F3.boolean.opBoolean","INTERSECT",EDGE,{"derivedFrom":[subQ2,makeQuery(id+"F3.opExtrude","SWEPT_FACE",FACE,{"disambiguationData":[OSD([sQuery(id+"F2.wireOp",EDGE,"E37.2")])]})]}),makeQuery(id+"F3.boolean.opBoolean","INTERSECT",EDGE,{"derivedFrom":[subQ2,makeQuery(id+"F3.opExtrude","SWEPT_FACE",FACE,{"disambiguationData":[OSD([sQuery(id+"F2.wireOp",EDGE,"E37.3")])]})]}),makeQuery(id+"F3.boolean.opBoolean","INTERSECT",EDGE,{"derivedFrom":[subQ2,makeQuery(id+"F3.opExtrude","SWEPT_FACE",FACE,{"disambiguationData":[OSD([sQuery(id+"F2.wireOp",EDGE,"E37.4")])]})]}),makeQuery(id+"F3.boolean.opBoolean","INTERSECT",EDGE,{"derivedFrom":[subQ2,makeQuery(id+"F3.opExtrude","SWEPT_FACE",FACE,{"disambiguationData":[OSD([sQuery(id+"F2.wireOp",EDGE,"E37.5")])]})]}),makeQuery(id+"F3.boolean.opBoolean","INTERSECT",EDGE,{"derivedFrom":[subQ2,makeQuery(id+"F3.opExtrude","SWEPT_FACE",FACE,{"disambiguationData":[OSD([sQuery(id+"F2.wireOp",EDGE,"E38.0")])]})]}),makeQuery(id+"F3.boolean.opBoolean","INTERSECT",EDGE,{"derivedFrom":[subQ2,makeQuery(id+"F3.opExtrude","SWEPT_FACE",FACE,{"disambiguationData":[OSD([sQuery(id+"F2.wireOp",EDGE,"E38.1")])]})]}),makeQuery(id+"F3.boolean.opBoolean","INTERSECT",EDGE,{"derivedFrom":[subQ2,makeQuery(id+"F3.opExtrude","SWEPT_FACE",FACE,{"disambiguationData":[OSD([sQuery(id+"F2.wireOp",EDGE,"E38.2")])]})]}),makeQuery(id+"F3.boolean.opBoolean","INTERSECT",EDGE,{"derivedFrom":[subQ2,makeQuery(id+"F3.opExtrude","SWEPT_FACE",FACE,{"disambiguationData":[OSD([sQuery(id+"F2.wireOp",EDGE,"E38.3")])]})]}),makeQuery(id+"F3.boolean.opBoolean","INTERSECT",EDGE,{"derivedFrom":[subQ2,makeQuery(id+"F3.opExtrude","SWEPT_FACE",FACE,{"disambiguationData":[OSD([sQuery(id+"F2.wireOp",EDGE,"E38.4")])]})]}),makeQuery(id+"F3.boolean.opBoolean","INTERSECT",EDGE,{"derivedFrom":[subQ2,makeQuery(id+"F3.opExtrude","SWEPT_FACE",FACE,{"disambiguationData":[OSD([sQuery(id+"F2.wireOp",EDGE,"E38.5")])]})]})]);}
            var Q2;
            {var subQ0=sQuery(id+"F0.wireOp",EDGE,"E6");var subQ1=sQuery(id+"F0.wireOp",EDGE,"E18.top");var subQ2=makeQuery(id+"F1.opExtrude","SWEPT_FACE",FACE,{"disambiguationData":[OSD([subQ0]),TDD([makeQuery(id+"F0.imprint","IMPRINT",EDGE,{"disambiguationData":[TD([[makeQuery(id+"F0.imprint","INTERSECT",VERTEX,{"derivedFrom":[subQ0,sQuery(id+"F0.wireOp",EDGE,"E9")]}),1.0]])],"derivedFrom":subQ0})])]});var subQ4=makeQuery(id+"F1.opExtrude","SWEPT_FACE",FACE,{"disambiguationData":[OSD([subQ0]),TDD([makeQuery(id+"F0.imprint","IMPRINT",EDGE,{"disambiguationData":[TD([[makeQuery(id+"F0.imprint","INTERSECT",VERTEX,{"derivedFrom":[subQ0,subQ1,sQuery(id+"F0.wireOp",EDGE,"E18.right")]}),1.0]])],"derivedFrom":subQ0})])]});var subQ5=makeQuery(id+"F1.opExtrude","SWEPT_FACE",FACE,{"disambiguationData":[OSD([subQ0]),TDD([makeQuery(id+"F0.imprint","IMPRINT",EDGE,{"disambiguationData":[TD([[makeQuery(id+"F0.imprint","INTERSECT",VERTEX,{"derivedFrom":[subQ0,sQuery(id+"F0.wireOp",EDGE,"E12")]}),-1.0]])],"derivedFrom":subQ0})])]});Q2=qUnion([makeQuery(id+"F3.boolean.opBoolean","INTERSECT",EDGE,{"derivedFrom":[subQ5,makeQuery(id+"F3.opExtrude","SWEPT_FACE",FACE,{"disambiguationData":[OSD([sQuery(id+"F2.wireOp",EDGE,"E41.0")])]})]}),makeQuery(id+"F3.boolean.opBoolean","INTERSECT",EDGE,{"derivedFrom":[subQ5,makeQuery(id+"F3.opExtrude","SWEPT_FACE",FACE,{"disambiguationData":[OSD([sQuery(id+"F2.wireOp",EDGE,"E41.1")])]})]}),makeQuery(id+"F3.boolean.opBoolean","INTERSECT",EDGE,{"derivedFrom":[subQ5,makeQuery(id+"F3.opExtrude","SWEPT_FACE",FACE,{"disambiguationData":[OSD([sQuery(id+"F2.wireOp",EDGE,"E41.2")])]})]}),makeQuery(id+"F3.boolean.opBoolean","INTERSECT",EDGE,{"derivedFrom":[subQ5,makeQuery(id+"F3.opExtrude","SWEPT_FACE",FACE,{"disambiguationData":[OSD([sQuery(id+"F2.wireOp",EDGE,"E41.3")])]})]}),makeQuery(id+"F3.boolean.opBoolean","INTERSECT",EDGE,{"derivedFrom":[subQ5,makeQuery(id+"F3.opExtrude","SWEPT_FACE",FACE,{"disambiguationData":[OSD([sQuery(id+"F2.wireOp",EDGE,"E41.4")])]})]}),makeQuery(id+"F3.boolean.opBoolean","INTERSECT",EDGE,{"derivedFrom":[subQ5,makeQuery(id+"F3.opExtrude","SWEPT_FACE",FACE,{"disambiguationData":[OSD([sQuery(id+"F2.wireOp",EDGE,"E41.5")])]})]}),makeQuery(id+"F3.boolean.opBoolean","INTERSECT",EDGE,{"derivedFrom":[subQ5,makeQuery(id+"F3.opExtrude","SWEPT_FACE",FACE,{"disambiguationData":[OSD([sQuery(id+"F2.wireOp",EDGE,"E42.0")])]})]}),makeQuery(id+"F3.boolean.opBoolean","INTERSECT",EDGE,{"derivedFrom":[subQ5,makeQuery(id+"F3.opExtrude","SWEPT_FACE",FACE,{"disambiguationData":[OSD([sQuery(id+"F2.wireOp",EDGE,"E42.1")])]})]}),makeQuery(id+"F3.boolean.opBoolean","INTERSECT",EDGE,{"derivedFrom":[subQ5,makeQuery(id+"F3.opExtrude","SWEPT_FACE",FACE,{"disambiguationData":[OSD([sQuery(id+"F2.wireOp",EDGE,"E42.2")])]})]}),makeQuery(id+"F3.boolean.opBoolean","INTERSECT",EDGE,{"derivedFrom":[subQ5,makeQuery(id+"F3.opExtrude","SWEPT_FACE",FACE,{"disambiguationData":[OSD([sQuery(id+"F2.wireOp",EDGE,"E42.3")])]})]}),makeQuery(id+"F3.boolean.opBoolean","INTERSECT",EDGE,{"derivedFrom":[subQ5,makeQuery(id+"F3.opExtrude","SWEPT_FACE",FACE,{"disambiguationData":[OSD([sQuery(id+"F2.wireOp",EDGE,"E42.4")])]})]}),makeQuery(id+"F3.boolean.opBoolean","INTERSECT",EDGE,{"derivedFrom":[subQ5,makeQuery(id+"F3.opExtrude","SWEPT_FACE",FACE,{"disambiguationData":[OSD([sQuery(id+"F2.wireOp",EDGE,"E42.5")])]})]}),makeQuery(id+"F3.boolean.opBoolean","INTERSECT",EDGE,{"derivedFrom":[subQ4,makeQuery(id+"F3.opExtrude","SWEPT_FACE",FACE,{"disambiguationData":[OSD([sQuery(id+"F2.wireOp",EDGE,"E39.0")])]})]}),makeQuery(id+"F3.boolean.opBoolean","INTERSECT",EDGE,{"derivedFrom":[subQ4,makeQuery(id+"F3.opExtrude","SWEPT_FACE",FACE,{"disambiguationData":[OSD([sQuery(id+"F2.wireOp",EDGE,"E39.1")])]})]}),makeQuery(id+"F3.boolean.opBoolean","INTERSECT",EDGE,{"derivedFrom":[subQ4,makeQuery(id+"F3.opExtrude","SWEPT_FACE",FACE,{"disambiguationData":[OSD([sQuery(id+"F2.wireOp",EDGE,"E39.2")])]})]}),makeQuery(id+"F3.boolean.opBoolean","INTERSECT",EDGE,{"derivedFrom":[subQ4,makeQuery(id+"F3.opExtrude","SWEPT_FACE",FACE,{"disambiguationData":[OSD([sQuery(id+"F2.wireOp",EDGE,"E39.3")])]})]}),makeQuery(id+"F3.boolean.opBoolean","INTERSECT",EDGE,{"derivedFrom":[subQ4,makeQuery(id+"F3.opExtrude","SWEPT_FACE",FACE,{"disambiguationData":[OSD([sQuery(id+"F2.wireOp",EDGE,"E39.4")])]})]}),makeQuery(id+"F3.boolean.opBoolean","INTERSECT",EDGE,{"derivedFrom":[subQ4,makeQuery(id+"F3.opExtrude","SWEPT_FACE",FACE,{"disambiguationData":[OSD([sQuery(id+"F2.wireOp",EDGE,"E39.5")])]})]}),makeQuery(id+"F3.boolean.opBoolean","INTERSECT",EDGE,{"derivedFrom":[subQ4,makeQuery(id+"F3.opExtrude","SWEPT_FACE",FACE,{"disambiguationData":[OSD([sQuery(id+"F2.wireOp",EDGE,"E40.0")])]})]}),makeQuery(id+"F3.boolean.opBoolean","INTERSECT",EDGE,{"derivedFrom":[subQ4,makeQuery(id+"F3.opExtrude","SWEPT_FACE",FACE,{"disambiguationData":[OSD([sQuery(id+"F2.wireOp",EDGE,"E40.1")])]})]}),makeQuery(id+"F3.boolean.opBoolean","INTERSECT",EDGE,{"derivedFrom":[subQ4,makeQuery(id+"F3.opExtrude","SWEPT_FACE",FACE,{"disambiguationData":[OSD([sQuery(id+"F2.wireOp",EDGE,"E40.2")])]})]}),makeQuery(id+"F3.boolean.opBoolean","INTERSECT",EDGE,{"derivedFrom":[subQ4,makeQuery(id+"F3.opExtrude","SWEPT_FACE",FACE,{"disambiguationData":[OSD([sQuery(id+"F2.wireOp",EDGE,"E40.3")])]})]}),makeQuery(id+"F3.boolean.opBoolean","INTERSECT",EDGE,{"derivedFrom":[subQ4,makeQuery(id+"F3.opExtrude","SWEPT_FACE",FACE,{"disambiguationData":[OSD([sQuery(id+"F2.wireOp",EDGE,"E40.4")])]})]}),makeQuery(id+"F3.boolean.opBoolean","INTERSECT",EDGE,{"derivedFrom":[subQ4,makeQuery(id+"F3.opExtrude","SWEPT_FACE",FACE,{"disambiguationData":[OSD([sQuery(id+"F2.wireOp",EDGE,"E40.5")])]})]}),makeQuery(id+"F3.boolean.opBoolean","INTERSECT",EDGE,{"derivedFrom":[subQ2,makeQuery(id+"F3.opExtrude","SWEPT_FACE",FACE,{"disambiguationData":[OSD([sQuery(id+"F2.wireOp",EDGE,"E36.0")])]})]}),makeQuery(id+"F3.boolean.opBoolean","INTERSECT",EDGE,{"derivedFrom":[subQ2,makeQuery(id+"F3.opExtrude","SWEPT_FACE",FACE,{"disambiguationData":[OSD([sQuery(id+"F2.wireOp",EDGE,"E36.1")])]})]}),makeQuery(id+"F3.boolean.opBoolean","INTERSECT",EDGE,{"derivedFrom":[subQ2,makeQuery(id+"F3.opExtrude","SWEPT_FACE",FACE,{"disambiguationData":[OSD([sQuery(id+"F2.wireOp",EDGE,"E36.2")])]})]}),makeQuery(id+"F3.boolean.opBoolean","INTERSECT",EDGE,{"derivedFrom":[subQ2,makeQuery(id+"F3.opExtrude","SWEPT_FACE",FACE,{"disambiguationData":[OSD([sQuery(id+"F2.wireOp",EDGE,"E36.3")])]})]}),makeQuery(id+"F3.boolean.opBoolean","INTERSECT",EDGE,{"derivedFrom":[subQ2,makeQuery(id+"F3.opExtrude","SWEPT_FACE",FACE,{"disambiguationData":[OSD([sQuery(id+"F2.wireOp",EDGE,"E36.4")])]})]}),makeQuery(id+"F3.boolean.opBoolean","INTERSECT",EDGE,{"derivedFrom":[subQ2,makeQuery(id+"F3.opExtrude","SWEPT_FACE",FACE,{"disambiguationData":[OSD([sQuery(id+"F2.wireOp",EDGE,"E36.5")])]})]}),makeQuery(id+"F3.boolean.opBoolean","INTERSECT",EDGE,{"derivedFrom":[subQ2,makeQuery(id+"F3.opExtrude","SWEPT_FACE",FACE,{"disambiguationData":[OSD([sQuery(id+"F2.wireOp",EDGE,"E37.0")])]})]}),makeQuery(id+"F3.boolean.opBoolean","INTERSECT",EDGE,{"derivedFrom":[subQ2,makeQuery(id+"F3.opExtrude","SWEPT_FACE",FACE,{"disambiguationData":[OSD([sQuery(id+"F2.wireOp",EDGE,"E37.1")])]})]}),makeQuery(id+"F3.boolean.opBoolean","INTERSECT",EDGE,{"derivedFrom":[subQ2,makeQuery(id+"F3.opExtrude","SWEPT_FACE",FACE,{"disambiguationData":[OSD([sQuery(id+"F2.wireOp",EDGE,"E37.2")])]})]}),makeQuery(id+"F3.boolean.opBoolean","INTERSECT",EDGE,{"derivedFrom":[subQ2,makeQuery(id+"F3.opExtrude","SWEPT_FACE",FACE,{"disambiguationData":[OSD([sQuery(id+"F2.wireOp",EDGE,"E37.3")])]})]}),makeQuery(id+"F3.boolean.opBoolean","INTERSECT",EDGE,{"derivedFrom":[subQ2,makeQuery(id+"F3.opExtrude","SWEPT_FACE",FACE,{"disambiguationData":[OSD([sQuery(id+"F2.wireOp",EDGE,"E37.4")])]})]}),makeQuery(id+"F3.boolean.opBoolean","INTERSECT",EDGE,{"derivedFrom":[subQ2,makeQuery(id+"F3.opExtrude","SWEPT_FACE",FACE,{"disambiguationData":[OSD([sQuery(id+"F2.wireOp",EDGE,"E37.5")])]})]}),makeQuery(id+"F3.boolean.opBoolean","INTERSECT",EDGE,{"derivedFrom":[subQ2,makeQuery(id+"F3.opExtrude","SWEPT_FACE",FACE,{"disambiguationData":[OSD([sQuery(id+"F2.wireOp",EDGE,"E38.0")])]})]}),makeQuery(id+"F3.boolean.opBoolean","INTERSECT",EDGE,{"derivedFrom":[subQ2,makeQuery(id+"F3.opExtrude","SWEPT_FACE",FACE,{"disambiguationData":[OSD([sQuery(id+"F2.wireOp",EDGE,"E38.1")])]})]}),makeQuery(id+"F3.boolean.opBoolean","INTERSECT",EDGE,{"derivedFrom":[subQ2,makeQuery(id+"F3.opExtrude","SWEPT_FACE",FACE,{"disambiguationData":[OSD([sQuery(id+"F2.wireOp",EDGE,"E38.2")])]})]}),makeQuery(id+"F3.boolean.opBoolean","INTERSECT",EDGE,{"derivedFrom":[subQ2,makeQuery(id+"F3.opExtrude","SWEPT_FACE",FACE,{"disambiguationData":[OSD([sQuery(id+"F2.wireOp",EDGE,"E38.3")])]})]}),makeQuery(id+"F3.boolean.opBoolean","INTERSECT",EDGE,{"derivedFrom":[subQ2,makeQuery(id+"F3.opExtrude","SWEPT_FACE",FACE,{"disambiguationData":[OSD([sQuery(id+"F2.wireOp",EDGE,"E38.4")])]})]}),makeQuery(id+"F3.boolean.opBoolean","INTERSECT",EDGE,{"derivedFrom":[subQ2,makeQuery(id+"F3.opExtrude","SWEPT_FACE",FACE,{"disambiguationData":[OSD([sQuery(id+"F2.wireOp",EDGE,"E38.5")])]})]})]);}
            var Q3;
            {var subQ0=sQuery(id+"F0.wireOp",EDGE,"E6");var subQ1=sQuery(id+"F0.wireOp",EDGE,"E18.top");var subQ2=makeQuery(id+"F1.opExtrude","SWEPT_FACE",FACE,{"disambiguationData":[OSD([subQ0]),TDD([makeQuery(id+"F0.imprint","IMPRINT",EDGE,{"disambiguationData":[TD([[makeQuery(id+"F0.imprint","INTERSECT",VERTEX,{"derivedFrom":[subQ0,sQuery(id+"F0.wireOp",EDGE,"E9")]}),1.0]])],"derivedFrom":subQ0})])]});var subQ4=makeQuery(id+"F1.opExtrude","SWEPT_FACE",FACE,{"disambiguationData":[OSD([subQ0]),TDD([makeQuery(id+"F0.imprint","IMPRINT",EDGE,{"disambiguationData":[TD([[makeQuery(id+"F0.imprint","INTERSECT",VERTEX,{"derivedFrom":[subQ0,subQ1,sQuery(id+"F0.wireOp",EDGE,"E18.right")]}),1.0]])],"derivedFrom":subQ0})])]});var subQ5=makeQuery(id+"F1.opExtrude","SWEPT_FACE",FACE,{"disambiguationData":[OSD([subQ0]),TDD([makeQuery(id+"F0.imprint","IMPRINT",EDGE,{"disambiguationData":[TD([[makeQuery(id+"F0.imprint","INTERSECT",VERTEX,{"derivedFrom":[subQ0,sQuery(id+"F0.wireOp",EDGE,"E12")]}),-1.0]])],"derivedFrom":subQ0})])]});Q3=qUnion([makeQuery(id+"F3.boolean.opBoolean","INTERSECT",EDGE,{"derivedFrom":[subQ5,makeQuery(id+"F3.opExtrude","SWEPT_FACE",FACE,{"disambiguationData":[OSD([sQuery(id+"F2.wireOp",EDGE,"E41.0")])]})]}),makeQuery(id+"F3.boolean.opBoolean","INTERSECT",EDGE,{"derivedFrom":[subQ5,makeQuery(id+"F3.opExtrude","SWEPT_FACE",FACE,{"disambiguationData":[OSD([sQuery(id+"F2.wireOp",EDGE,"E41.1")])]})]}),makeQuery(id+"F3.boolean.opBoolean","INTERSECT",EDGE,{"derivedFrom":[subQ5,makeQuery(id+"F3.opExtrude","SWEPT_FACE",FACE,{"disambiguationData":[OSD([sQuery(id+"F2.wireOp",EDGE,"E41.2")])]})]}),makeQuery(id+"F3.boolean.opBoolean","INTERSECT",EDGE,{"derivedFrom":[subQ5,makeQuery(id+"F3.opExtrude","SWEPT_FACE",FACE,{"disambiguationData":[OSD([sQuery(id+"F2.wireOp",EDGE,"E41.3")])]})]}),makeQuery(id+"F3.boolean.opBoolean","INTERSECT",EDGE,{"derivedFrom":[subQ5,makeQuery(id+"F3.opExtrude","SWEPT_FACE",FACE,{"disambiguationData":[OSD([sQuery(id+"F2.wireOp",EDGE,"E41.4")])]})]}),makeQuery(id+"F3.boolean.opBoolean","INTERSECT",EDGE,{"derivedFrom":[subQ5,makeQuery(id+"F3.opExtrude","SWEPT_FACE",FACE,{"disambiguationData":[OSD([sQuery(id+"F2.wireOp",EDGE,"E41.5")])]})]}),makeQuery(id+"F3.boolean.opBoolean","INTERSECT",EDGE,{"derivedFrom":[subQ5,makeQuery(id+"F3.opExtrude","SWEPT_FACE",FACE,{"disambiguationData":[OSD([sQuery(id+"F2.wireOp",EDGE,"E42.0")])]})]}),makeQuery(id+"F3.boolean.opBoolean","INTERSECT",EDGE,{"derivedFrom":[subQ5,makeQuery(id+"F3.opExtrude","SWEPT_FACE",FACE,{"disambiguationData":[OSD([sQuery(id+"F2.wireOp",EDGE,"E42.1")])]})]}),makeQuery(id+"F3.boolean.opBoolean","INTERSECT",EDGE,{"derivedFrom":[subQ5,makeQuery(id+"F3.opExtrude","SWEPT_FACE",FACE,{"disambiguationData":[OSD([sQuery(id+"F2.wireOp",EDGE,"E42.2")])]})]}),makeQuery(id+"F3.boolean.opBoolean","INTERSECT",EDGE,{"derivedFrom":[subQ5,makeQuery(id+"F3.opExtrude","SWEPT_FACE",FACE,{"disambiguationData":[OSD([sQuery(id+"F2.wireOp",EDGE,"E42.3")])]})]}),makeQuery(id+"F3.boolean.opBoolean","INTERSECT",EDGE,{"derivedFrom":[subQ5,makeQuery(id+"F3.opExtrude","SWEPT_FACE",FACE,{"disambiguationData":[OSD([sQuery(id+"F2.wireOp",EDGE,"E42.4")])]})]}),makeQuery(id+"F3.boolean.opBoolean","INTERSECT",EDGE,{"derivedFrom":[subQ5,makeQuery(id+"F3.opExtrude","SWEPT_FACE",FACE,{"disambiguationData":[OSD([sQuery(id+"F2.wireOp",EDGE,"E42.5")])]})]}),makeQuery(id+"F3.boolean.opBoolean","INTERSECT",EDGE,{"derivedFrom":[subQ4,makeQuery(id+"F3.opExtrude","SWEPT_FACE",FACE,{"disambiguationData":[OSD([sQuery(id+"F2.wireOp",EDGE,"E39.0")])]})]}),makeQuery(id+"F3.boolean.opBoolean","INTERSECT",EDGE,{"derivedFrom":[subQ4,makeQuery(id+"F3.opExtrude","SWEPT_FACE",FACE,{"disambiguationData":[OSD([sQuery(id+"F2.wireOp",EDGE,"E39.1")])]})]}),makeQuery(id+"F3.boolean.opBoolean","INTERSECT",EDGE,{"derivedFrom":[subQ4,makeQuery(id+"F3.opExtrude","SWEPT_FACE",FACE,{"disambiguationData":[OSD([sQuery(id+"F2.wireOp",EDGE,"E39.2")])]})]}),makeQuery(id+"F3.boolean.opBoolean","INTERSECT",EDGE,{"derivedFrom":[subQ4,makeQuery(id+"F3.opExtrude","SWEPT_FACE",FACE,{"disambiguationData":[OSD([sQuery(id+"F2.wireOp",EDGE,"E39.3")])]})]}),makeQuery(id+"F3.boolean.opBoolean","INTERSECT",EDGE,{"derivedFrom":[subQ4,makeQuery(id+"F3.opExtrude","SWEPT_FACE",FACE,{"disambiguationData":[OSD([sQuery(id+"F2.wireOp",EDGE,"E39.4")])]})]}),makeQuery(id+"F3.boolean.opBoolean","INTERSECT",EDGE,{"derivedFrom":[subQ4,makeQuery(id+"F3.opExtrude","SWEPT_FACE",FACE,{"disambiguationData":[OSD([sQuery(id+"F2.wireOp",EDGE,"E39.5")])]})]}),makeQuery(id+"F3.boolean.opBoolean","INTERSECT",EDGE,{"derivedFrom":[subQ4,makeQuery(id+"F3.opExtrude","SWEPT_FACE",FACE,{"disambiguationData":[OSD([sQuery(id+"F2.wireOp",EDGE,"E40.0")])]})]}),makeQuery(id+"F3.boolean.opBoolean","INTERSECT",EDGE,{"derivedFrom":[subQ4,makeQuery(id+"F3.opExtrude","SWEPT_FACE",FACE,{"disambiguationData":[OSD([sQuery(id+"F2.wireOp",EDGE,"E40.1")])]})]}),makeQuery(id+"F3.boolean.opBoolean","INTERSECT",EDGE,{"derivedFrom":[subQ4,makeQuery(id+"F3.opExtrude","SWEPT_FACE",FACE,{"disambiguationData":[OSD([sQuery(id+"F2.wireOp",EDGE,"E40.2")])]})]}),makeQuery(id+"F3.boolean.opBoolean","INTERSECT",EDGE,{"derivedFrom":[subQ4,makeQuery(id+"F3.opExtrude","SWEPT_FACE",FACE,{"disambiguationData":[OSD([sQuery(id+"F2.wireOp",EDGE,"E40.3")])]})]}),makeQuery(id+"F3.boolean.opBoolean","INTERSECT",EDGE,{"derivedFrom":[subQ4,makeQuery(id+"F3.opExtrude","SWEPT_FACE",FACE,{"disambiguationData":[OSD([sQuery(id+"F2.wireOp",EDGE,"E40.4")])]})]}),makeQuery(id+"F3.boolean.opBoolean","INTERSECT",EDGE,{"derivedFrom":[subQ4,makeQuery(id+"F3.opExtrude","SWEPT_FACE",FACE,{"disambiguationData":[OSD([sQuery(id+"F2.wireOp",EDGE,"E40.5")])]})]}),makeQuery(id+"F3.boolean.opBoolean","INTERSECT",EDGE,{"derivedFrom":[subQ2,makeQuery(id+"F3.opExtrude","SWEPT_FACE",FACE,{"disambiguationData":[OSD([sQuery(id+"F2.wireOp",EDGE,"E36.0")])]})]}),makeQuery(id+"F3.boolean.opBoolean","INTERSECT",EDGE,{"derivedFrom":[subQ2,makeQuery(id+"F3.opExtrude","SWEPT_FACE",FACE,{"disambiguationData":[OSD([sQuery(id+"F2.wireOp",EDGE,"E36.1")])]})]}),makeQuery(id+"F3.boolean.opBoolean","INTERSECT",EDGE,{"derivedFrom":[subQ2,makeQuery(id+"F3.opExtrude","SWEPT_FACE",FACE,{"disambiguationData":[OSD([sQuery(id+"F2.wireOp",EDGE,"E36.2")])]})]}),makeQuery(id+"F3.boolean.opBoolean","INTERSECT",EDGE,{"derivedFrom":[subQ2,makeQuery(id+"F3.opExtrude","SWEPT_FACE",FACE,{"disambiguationData":[OSD([sQuery(id+"F2.wireOp",EDGE,"E36.3")])]})]}),makeQuery(id+"F3.boolean.opBoolean","INTERSECT",EDGE,{"derivedFrom":[subQ2,makeQuery(id+"F3.opExtrude","SWEPT_FACE",FACE,{"disambiguationData":[OSD([sQuery(id+"F2.wireOp",EDGE,"E36.4")])]})]}),makeQuery(id+"F3.boolean.opBoolean","INTERSECT",EDGE,{"derivedFrom":[subQ2,makeQuery(id+"F3.opExtrude","SWEPT_FACE",FACE,{"disambiguationData":[OSD([sQuery(id+"F2.wireOp",EDGE,"E36.5")])]})]}),makeQuery(id+"F3.boolean.opBoolean","INTERSECT",EDGE,{"derivedFrom":[subQ2,makeQuery(id+"F3.opExtrude","SWEPT_FACE",FACE,{"disambiguationData":[OSD([sQuery(id+"F2.wireOp",EDGE,"E37.0")])]})]}),makeQuery(id+"F3.boolean.opBoolean","INTERSECT",EDGE,{"derivedFrom":[subQ2,makeQuery(id+"F3.opExtrude","SWEPT_FACE",FACE,{"disambiguationData":[OSD([sQuery(id+"F2.wireOp",EDGE,"E37.1")])]})]}),makeQuery(id+"F3.boolean.opBoolean","INTERSECT",EDGE,{"derivedFrom":[subQ2,makeQuery(id+"F3.opExtrude","SWEPT_FACE",FACE,{"disambiguationData":[OSD([sQuery(id+"F2.wireOp",EDGE,"E37.2")])]})]}),makeQuery(id+"F3.boolean.opBoolean","INTERSECT",EDGE,{"derivedFrom":[subQ2,makeQuery(id+"F3.opExtrude","SWEPT_FACE",FACE,{"disambiguationData":[OSD([sQuery(id+"F2.wireOp",EDGE,"E37.3")])]})]}),makeQuery(id+"F3.boolean.opBoolean","INTERSECT",EDGE,{"derivedFrom":[subQ2,makeQuery(id+"F3.opExtrude","SWEPT_FACE",FACE,{"disambiguationData":[OSD([sQuery(id+"F2.wireOp",EDGE,"E37.4")])]})]}),makeQuery(id+"F3.boolean.opBoolean","INTERSECT",EDGE,{"derivedFrom":[subQ2,makeQuery(id+"F3.opExtrude","SWEPT_FACE",FACE,{"disambiguationData":[OSD([sQuery(id+"F2.wireOp",EDGE,"E37.5")])]})]}),makeQuery(id+"F3.boolean.opBoolean","INTERSECT",EDGE,{"derivedFrom":[subQ2,makeQuery(id+"F3.opExtrude","SWEPT_FACE",FACE,{"disambiguationData":[OSD([sQuery(id+"F2.wireOp",EDGE,"E38.0")])]})]}),makeQuery(id+"F3.boolean.opBoolean","INTERSECT",EDGE,{"derivedFrom":[subQ2,makeQuery(id+"F3.opExtrude","SWEPT_FACE",FACE,{"disambiguationData":[OSD([sQuery(id+"F2.wireOp",EDGE,"E38.1")])]})]}),makeQuery(id+"F3.boolean.opBoolean","INTERSECT",EDGE,{"derivedFrom":[subQ2,makeQuery(id+"F3.opExtrude","SWEPT_FACE",FACE,{"disambiguationData":[OSD([sQuery(id+"F2.wireOp",EDGE,"E38.2")])]})]}),makeQuery(id+"F3.boolean.opBoolean","INTERSECT",EDGE,{"derivedFrom":[subQ2,makeQuery(id+"F3.opExtrude","SWEPT_FACE",FACE,{"disambiguationData":[OSD([sQuery(id+"F2.wireOp",EDGE,"E38.3")])]})]}),makeQuery(id+"F3.boolean.opBoolean","INTERSECT",EDGE,{"derivedFrom":[subQ2,makeQuery(id+"F3.opExtrude","SWEPT_FACE",FACE,{"disambiguationData":[OSD([sQuery(id+"F2.wireOp",EDGE,"E38.4")])]})]}),makeQuery(id+"F3.boolean.opBoolean","INTERSECT",EDGE,{"derivedFrom":[subQ2,makeQuery(id+"F3.opExtrude","SWEPT_FACE",FACE,{"disambiguationData":[OSD([sQuery(id+"F2.wireOp",EDGE,"E38.5")])]})]})]);}
            var Q4;
            {var subQ0=sQuery(id+"F0.wireOp",EDGE,"E6");var subQ1=sQuery(id+"F0.wireOp",EDGE,"E18.top");var subQ2=makeQuery(id+"F1.opExtrude","SWEPT_FACE",FACE,{"disambiguationData":[OSD([subQ0]),TDD([makeQuery(id+"F0.imprint","IMPRINT",EDGE,{"disambiguationData":[TD([[makeQuery(id+"F0.imprint","INTERSECT",VERTEX,{"derivedFrom":[subQ0,sQuery(id+"F0.wireOp",EDGE,"E9")]}),1.0]])],"derivedFrom":subQ0})])]});var subQ4=makeQuery(id+"F1.opExtrude","SWEPT_FACE",FACE,{"disambiguationData":[OSD([subQ0]),TDD([makeQuery(id+"F0.imprint","IMPRINT",EDGE,{"disambiguationData":[TD([[makeQuery(id+"F0.imprint","INTERSECT",VERTEX,{"derivedFrom":[subQ0,subQ1,sQuery(id+"F0.wireOp",EDGE,"E18.right")]}),1.0]])],"derivedFrom":subQ0})])]});var subQ5=makeQuery(id+"F1.opExtrude","SWEPT_FACE",FACE,{"disambiguationData":[OSD([subQ0]),TDD([makeQuery(id+"F0.imprint","IMPRINT",EDGE,{"disambiguationData":[TD([[makeQuery(id+"F0.imprint","INTERSECT",VERTEX,{"derivedFrom":[subQ0,sQuery(id+"F0.wireOp",EDGE,"E12")]}),-1.0]])],"derivedFrom":subQ0})])]});Q4=qUnion([makeQuery(id+"F3.boolean.opBoolean","INTERSECT",EDGE,{"derivedFrom":[subQ5,makeQuery(id+"F3.opExtrude","SWEPT_FACE",FACE,{"disambiguationData":[OSD([sQuery(id+"F2.wireOp",EDGE,"E41.0")])]})]}),makeQuery(id+"F3.boolean.opBoolean","INTERSECT",EDGE,{"derivedFrom":[subQ5,makeQuery(id+"F3.opExtrude","SWEPT_FACE",FACE,{"disambiguationData":[OSD([sQuery(id+"F2.wireOp",EDGE,"E41.1")])]})]}),makeQuery(id+"F3.boolean.opBoolean","INTERSECT",EDGE,{"derivedFrom":[subQ5,makeQuery(id+"F3.opExtrude","SWEPT_FACE",FACE,{"disambiguationData":[OSD([sQuery(id+"F2.wireOp",EDGE,"E41.2")])]})]}),makeQuery(id+"F3.boolean.opBoolean","INTERSECT",EDGE,{"derivedFrom":[subQ5,makeQuery(id+"F3.opExtrude","SWEPT_FACE",FACE,{"disambiguationData":[OSD([sQuery(id+"F2.wireOp",EDGE,"E41.3")])]})]}),makeQuery(id+"F3.boolean.opBoolean","INTERSECT",EDGE,{"derivedFrom":[subQ5,makeQuery(id+"F3.opExtrude","SWEPT_FACE",FACE,{"disambiguationData":[OSD([sQuery(id+"F2.wireOp",EDGE,"E41.4")])]})]}),makeQuery(id+"F3.boolean.opBoolean","INTERSECT",EDGE,{"derivedFrom":[subQ5,makeQuery(id+"F3.opExtrude","SWEPT_FACE",FACE,{"disambiguationData":[OSD([sQuery(id+"F2.wireOp",EDGE,"E41.5")])]})]}),makeQuery(id+"F3.boolean.opBoolean","INTERSECT",EDGE,{"derivedFrom":[subQ5,makeQuery(id+"F3.opExtrude","SWEPT_FACE",FACE,{"disambiguationData":[OSD([sQuery(id+"F2.wireOp",EDGE,"E42.0")])]})]}),makeQuery(id+"F3.boolean.opBoolean","INTERSECT",EDGE,{"derivedFrom":[subQ5,makeQuery(id+"F3.opExtrude","SWEPT_FACE",FACE,{"disambiguationData":[OSD([sQuery(id+"F2.wireOp",EDGE,"E42.1")])]})]}),makeQuery(id+"F3.boolean.opBoolean","INTERSECT",EDGE,{"derivedFrom":[subQ5,makeQuery(id+"F3.opExtrude","SWEPT_FACE",FACE,{"disambiguationData":[OSD([sQuery(id+"F2.wireOp",EDGE,"E42.2")])]})]}),makeQuery(id+"F3.boolean.opBoolean","INTERSECT",EDGE,{"derivedFrom":[subQ5,makeQuery(id+"F3.opExtrude","SWEPT_FACE",FACE,{"disambiguationData":[OSD([sQuery(id+"F2.wireOp",EDGE,"E42.3")])]})]}),makeQuery(id+"F3.boolean.opBoolean","INTERSECT",EDGE,{"derivedFrom":[subQ5,makeQuery(id+"F3.opExtrude","SWEPT_FACE",FACE,{"disambiguationData":[OSD([sQuery(id+"F2.wireOp",EDGE,"E42.4")])]})]}),makeQuery(id+"F3.boolean.opBoolean","INTERSECT",EDGE,{"derivedFrom":[subQ5,makeQuery(id+"F3.opExtrude","SWEPT_FACE",FACE,{"disambiguationData":[OSD([sQuery(id+"F2.wireOp",EDGE,"E42.5")])]})]}),makeQuery(id+"F3.boolean.opBoolean","INTERSECT",EDGE,{"derivedFrom":[subQ4,makeQuery(id+"F3.opExtrude","SWEPT_FACE",FACE,{"disambiguationData":[OSD([sQuery(id+"F2.wireOp",EDGE,"E39.0")])]})]}),makeQuery(id+"F3.boolean.opBoolean","INTERSECT",EDGE,{"derivedFrom":[subQ4,makeQuery(id+"F3.opExtrude","SWEPT_FACE",FACE,{"disambiguationData":[OSD([sQuery(id+"F2.wireOp",EDGE,"E39.1")])]})]}),makeQuery(id+"F3.boolean.opBoolean","INTERSECT",EDGE,{"derivedFrom":[subQ4,makeQuery(id+"F3.opExtrude","SWEPT_FACE",FACE,{"disambiguationData":[OSD([sQuery(id+"F2.wireOp",EDGE,"E39.2")])]})]}),makeQuery(id+"F3.boolean.opBoolean","INTERSECT",EDGE,{"derivedFrom":[subQ4,makeQuery(id+"F3.opExtrude","SWEPT_FACE",FACE,{"disambiguationData":[OSD([sQuery(id+"F2.wireOp",EDGE,"E39.3")])]})]}),makeQuery(id+"F3.boolean.opBoolean","INTERSECT",EDGE,{"derivedFrom":[subQ4,makeQuery(id+"F3.opExtrude","SWEPT_FACE",FACE,{"disambiguationData":[OSD([sQuery(id+"F2.wireOp",EDGE,"E39.4")])]})]}),makeQuery(id+"F3.boolean.opBoolean","INTERSECT",EDGE,{"derivedFrom":[subQ4,makeQuery(id+"F3.opExtrude","SWEPT_FACE",FACE,{"disambiguationData":[OSD([sQuery(id+"F2.wireOp",EDGE,"E39.5")])]})]}),makeQuery(id+"F3.boolean.opBoolean","INTERSECT",EDGE,{"derivedFrom":[subQ4,makeQuery(id+"F3.opExtrude","SWEPT_FACE",FACE,{"disambiguationData":[OSD([sQuery(id+"F2.wireOp",EDGE,"E40.0")])]})]}),makeQuery(id+"F3.boolean.opBoolean","INTERSECT",EDGE,{"derivedFrom":[subQ4,makeQuery(id+"F3.opExtrude","SWEPT_FACE",FACE,{"disambiguationData":[OSD([sQuery(id+"F2.wireOp",EDGE,"E40.1")])]})]}),makeQuery(id+"F3.boolean.opBoolean","INTERSECT",EDGE,{"derivedFrom":[subQ4,makeQuery(id+"F3.opExtrude","SWEPT_FACE",FACE,{"disambiguationData":[OSD([sQuery(id+"F2.wireOp",EDGE,"E40.2")])]})]}),makeQuery(id+"F3.boolean.opBoolean","INTERSECT",EDGE,{"derivedFrom":[subQ4,makeQuery(id+"F3.opExtrude","SWEPT_FACE",FACE,{"disambiguationData":[OSD([sQuery(id+"F2.wireOp",EDGE,"E40.3")])]})]}),makeQuery(id+"F3.boolean.opBoolean","INTERSECT",EDGE,{"derivedFrom":[subQ4,makeQuery(id+"F3.opExtrude","SWEPT_FACE",FACE,{"disambiguationData":[OSD([sQuery(id+"F2.wireOp",EDGE,"E40.4")])]})]}),makeQuery(id+"F3.boolean.opBoolean","INTERSECT",EDGE,{"derivedFrom":[subQ4,makeQuery(id+"F3.opExtrude","SWEPT_FACE",FACE,{"disambiguationData":[OSD([sQuery(id+"F2.wireOp",EDGE,"E40.5")])]})]}),makeQuery(id+"F3.boolean.opBoolean","INTERSECT",EDGE,{"derivedFrom":[subQ2,makeQuery(id+"F3.opExtrude","SWEPT_FACE",FACE,{"disambiguationData":[OSD([sQuery(id+"F2.wireOp",EDGE,"E36.0")])]})]}),makeQuery(id+"F3.boolean.opBoolean","INTERSECT",EDGE,{"derivedFrom":[subQ2,makeQuery(id+"F3.opExtrude","SWEPT_FACE",FACE,{"disambiguationData":[OSD([sQuery(id+"F2.wireOp",EDGE,"E36.1")])]})]}),makeQuery(id+"F3.boolean.opBoolean","INTERSECT",EDGE,{"derivedFrom":[subQ2,makeQuery(id+"F3.opExtrude","SWEPT_FACE",FACE,{"disambiguationData":[OSD([sQuery(id+"F2.wireOp",EDGE,"E36.2")])]})]}),makeQuery(id+"F3.boolean.opBoolean","INTERSECT",EDGE,{"derivedFrom":[subQ2,makeQuery(id+"F3.opExtrude","SWEPT_FACE",FACE,{"disambiguationData":[OSD([sQuery(id+"F2.wireOp",EDGE,"E36.3")])]})]}),makeQuery(id+"F3.boolean.opBoolean","INTERSECT",EDGE,{"derivedFrom":[subQ2,makeQuery(id+"F3.opExtrude","SWEPT_FACE",FACE,{"disambiguationData":[OSD([sQuery(id+"F2.wireOp",EDGE,"E36.4")])]})]}),makeQuery(id+"F3.boolean.opBoolean","INTERSECT",EDGE,{"derivedFrom":[subQ2,makeQuery(id+"F3.opExtrude","SWEPT_FACE",FACE,{"disambiguationData":[OSD([sQuery(id+"F2.wireOp",EDGE,"E36.5")])]})]}),makeQuery(id+"F3.boolean.opBoolean","INTERSECT",EDGE,{"derivedFrom":[subQ2,makeQuery(id+"F3.opExtrude","SWEPT_FACE",FACE,{"disambiguationData":[OSD([sQuery(id+"F2.wireOp",EDGE,"E37.0")])]})]}),makeQuery(id+"F3.boolean.opBoolean","INTERSECT",EDGE,{"derivedFrom":[subQ2,makeQuery(id+"F3.opExtrude","SWEPT_FACE",FACE,{"disambiguationData":[OSD([sQuery(id+"F2.wireOp",EDGE,"E37.1")])]})]}),makeQuery(id+"F3.boolean.opBoolean","INTERSECT",EDGE,{"derivedFrom":[subQ2,makeQuery(id+"F3.opExtrude","SWEPT_FACE",FACE,{"disambiguationData":[OSD([sQuery(id+"F2.wireOp",EDGE,"E37.2")])]})]}),makeQuery(id+"F3.boolean.opBoolean","INTERSECT",EDGE,{"derivedFrom":[subQ2,makeQuery(id+"F3.opExtrude","SWEPT_FACE",FACE,{"disambiguationData":[OSD([sQuery(id+"F2.wireOp",EDGE,"E37.3")])]})]}),makeQuery(id+"F3.boolean.opBoolean","INTERSECT",EDGE,{"derivedFrom":[subQ2,makeQuery(id+"F3.opExtrude","SWEPT_FACE",FACE,{"disambiguationData":[OSD([sQuery(id+"F2.wireOp",EDGE,"E37.4")])]})]}),makeQuery(id+"F3.boolean.opBoolean","INTERSECT",EDGE,{"derivedFrom":[subQ2,makeQuery(id+"F3.opExtrude","SWEPT_FACE",FACE,{"disambiguationData":[OSD([sQuery(id+"F2.wireOp",EDGE,"E37.5")])]})]}),makeQuery(id+"F3.boolean.opBoolean","INTERSECT",EDGE,{"derivedFrom":[subQ2,makeQuery(id+"F3.opExtrude","SWEPT_FACE",FACE,{"disambiguationData":[OSD([sQuery(id+"F2.wireOp",EDGE,"E38.0")])]})]}),makeQuery(id+"F3.boolean.opBoolean","INTERSECT",EDGE,{"derivedFrom":[subQ2,makeQuery(id+"F3.opExtrude","SWEPT_FACE",FACE,{"disambiguationData":[OSD([sQuery(id+"F2.wireOp",EDGE,"E38.1")])]})]}),makeQuery(id+"F3.boolean.opBoolean","INTERSECT",EDGE,{"derivedFrom":[subQ2,makeQuery(id+"F3.opExtrude","SWEPT_FACE",FACE,{"disambiguationData":[OSD([sQuery(id+"F2.wireOp",EDGE,"E38.2")])]})]}),makeQuery(id+"F3.boolean.opBoolean","INTERSECT",EDGE,{"derivedFrom":[subQ2,makeQuery(id+"F3.opExtrude","SWEPT_FACE",FACE,{"disambiguationData":[OSD([sQuery(id+"F2.wireOp",EDGE,"E38.3")])]})]}),makeQuery(id+"F3.boolean.opBoolean","INTERSECT",EDGE,{"derivedFrom":[subQ2,makeQuery(id+"F3.opExtrude","SWEPT_FACE",FACE,{"disambiguationData":[OSD([sQuery(id+"F2.wireOp",EDGE,"E38.4")])]})]}),makeQuery(id+"F3.boolean.opBoolean","INTERSECT",EDGE,{"derivedFrom":[subQ2,makeQuery(id+"F3.opExtrude","SWEPT_FACE",FACE,{"disambiguationData":[OSD([sQuery(id+"F2.wireOp",EDGE,"E38.5")])]})]})]);}
            var Q5;
            {var subQ0=sQuery(id+"F0.wireOp",EDGE,"E6");var subQ1=sQuery(id+"F0.wireOp",EDGE,"E18.top");var subQ2=makeQuery(id+"F1.opExtrude","SWEPT_FACE",FACE,{"disambiguationData":[OSD([subQ0]),TDD([makeQuery(id+"F0.imprint","IMPRINT",EDGE,{"disambiguationData":[TD([[makeQuery(id+"F0.imprint","INTERSECT",VERTEX,{"derivedFrom":[subQ0,sQuery(id+"F0.wireOp",EDGE,"E9")]}),1.0]])],"derivedFrom":subQ0})])]});var subQ4=makeQuery(id+"F1.opExtrude","SWEPT_FACE",FACE,{"disambiguationData":[OSD([subQ0]),TDD([makeQuery(id+"F0.imprint","IMPRINT",EDGE,{"disambiguationData":[TD([[makeQuery(id+"F0.imprint","INTERSECT",VERTEX,{"derivedFrom":[subQ0,subQ1,sQuery(id+"F0.wireOp",EDGE,"E18.right")]}),1.0]])],"derivedFrom":subQ0})])]});var subQ5=makeQuery(id+"F1.opExtrude","SWEPT_FACE",FACE,{"disambiguationData":[OSD([subQ0]),TDD([makeQuery(id+"F0.imprint","IMPRINT",EDGE,{"disambiguationData":[TD([[makeQuery(id+"F0.imprint","INTERSECT",VERTEX,{"derivedFrom":[subQ0,sQuery(id+"F0.wireOp",EDGE,"E12")]}),-1.0]])],"derivedFrom":subQ0})])]});Q5=qUnion([makeQuery(id+"F3.boolean.opBoolean","INTERSECT",EDGE,{"derivedFrom":[subQ5,makeQuery(id+"F3.opExtrude","SWEPT_FACE",FACE,{"disambiguationData":[OSD([sQuery(id+"F2.wireOp",EDGE,"E41.0")])]})]}),makeQuery(id+"F3.boolean.opBoolean","INTERSECT",EDGE,{"derivedFrom":[subQ5,makeQuery(id+"F3.opExtrude","SWEPT_FACE",FACE,{"disambiguationData":[OSD([sQuery(id+"F2.wireOp",EDGE,"E41.1")])]})]}),makeQuery(id+"F3.boolean.opBoolean","INTERSECT",EDGE,{"derivedFrom":[subQ5,makeQuery(id+"F3.opExtrude","SWEPT_FACE",FACE,{"disambiguationData":[OSD([sQuery(id+"F2.wireOp",EDGE,"E41.2")])]})]}),makeQuery(id+"F3.boolean.opBoolean","INTERSECT",EDGE,{"derivedFrom":[subQ5,makeQuery(id+"F3.opExtrude","SWEPT_FACE",FACE,{"disambiguationData":[OSD([sQuery(id+"F2.wireOp",EDGE,"E41.3")])]})]}),makeQuery(id+"F3.boolean.opBoolean","INTERSECT",EDGE,{"derivedFrom":[subQ5,makeQuery(id+"F3.opExtrude","SWEPT_FACE",FACE,{"disambiguationData":[OSD([sQuery(id+"F2.wireOp",EDGE,"E41.4")])]})]}),makeQuery(id+"F3.boolean.opBoolean","INTERSECT",EDGE,{"derivedFrom":[subQ5,makeQuery(id+"F3.opExtrude","SWEPT_FACE",FACE,{"disambiguationData":[OSD([sQuery(id+"F2.wireOp",EDGE,"E41.5")])]})]}),makeQuery(id+"F3.boolean.opBoolean","INTERSECT",EDGE,{"derivedFrom":[subQ5,makeQuery(id+"F3.opExtrude","SWEPT_FACE",FACE,{"disambiguationData":[OSD([sQuery(id+"F2.wireOp",EDGE,"E42.0")])]})]}),makeQuery(id+"F3.boolean.opBoolean","INTERSECT",EDGE,{"derivedFrom":[subQ5,makeQuery(id+"F3.opExtrude","SWEPT_FACE",FACE,{"disambiguationData":[OSD([sQuery(id+"F2.wireOp",EDGE,"E42.1")])]})]}),makeQuery(id+"F3.boolean.opBoolean","INTERSECT",EDGE,{"derivedFrom":[subQ5,makeQuery(id+"F3.opExtrude","SWEPT_FACE",FACE,{"disambiguationData":[OSD([sQuery(id+"F2.wireOp",EDGE,"E42.2")])]})]}),makeQuery(id+"F3.boolean.opBoolean","INTERSECT",EDGE,{"derivedFrom":[subQ5,makeQuery(id+"F3.opExtrude","SWEPT_FACE",FACE,{"disambiguationData":[OSD([sQuery(id+"F2.wireOp",EDGE,"E42.3")])]})]}),makeQuery(id+"F3.boolean.opBoolean","INTERSECT",EDGE,{"derivedFrom":[subQ5,makeQuery(id+"F3.opExtrude","SWEPT_FACE",FACE,{"disambiguationData":[OSD([sQuery(id+"F2.wireOp",EDGE,"E42.4")])]})]}),makeQuery(id+"F3.boolean.opBoolean","INTERSECT",EDGE,{"derivedFrom":[subQ5,makeQuery(id+"F3.opExtrude","SWEPT_FACE",FACE,{"disambiguationData":[OSD([sQuery(id+"F2.wireOp",EDGE,"E42.5")])]})]}),makeQuery(id+"F3.boolean.opBoolean","INTERSECT",EDGE,{"derivedFrom":[subQ4,makeQuery(id+"F3.opExtrude","SWEPT_FACE",FACE,{"disambiguationData":[OSD([sQuery(id+"F2.wireOp",EDGE,"E39.0")])]})]}),makeQuery(id+"F3.boolean.opBoolean","INTERSECT",EDGE,{"derivedFrom":[subQ4,makeQuery(id+"F3.opExtrude","SWEPT_FACE",FACE,{"disambiguationData":[OSD([sQuery(id+"F2.wireOp",EDGE,"E39.1")])]})]}),makeQuery(id+"F3.boolean.opBoolean","INTERSECT",EDGE,{"derivedFrom":[subQ4,makeQuery(id+"F3.opExtrude","SWEPT_FACE",FACE,{"disambiguationData":[OSD([sQuery(id+"F2.wireOp",EDGE,"E39.2")])]})]}),makeQuery(id+"F3.boolean.opBoolean","INTERSECT",EDGE,{"derivedFrom":[subQ4,makeQuery(id+"F3.opExtrude","SWEPT_FACE",FACE,{"disambiguationData":[OSD([sQuery(id+"F2.wireOp",EDGE,"E39.3")])]})]}),makeQuery(id+"F3.boolean.opBoolean","INTERSECT",EDGE,{"derivedFrom":[subQ4,makeQuery(id+"F3.opExtrude","SWEPT_FACE",FACE,{"disambiguationData":[OSD([sQuery(id+"F2.wireOp",EDGE,"E39.4")])]})]}),makeQuery(id+"F3.boolean.opBoolean","INTERSECT",EDGE,{"derivedFrom":[subQ4,makeQuery(id+"F3.opExtrude","SWEPT_FACE",FACE,{"disambiguationData":[OSD([sQuery(id+"F2.wireOp",EDGE,"E39.5")])]})]}),makeQuery(id+"F3.boolean.opBoolean","INTERSECT",EDGE,{"derivedFrom":[subQ4,makeQuery(id+"F3.opExtrude","SWEPT_FACE",FACE,{"disambiguationData":[OSD([sQuery(id+"F2.wireOp",EDGE,"E40.0")])]})]}),makeQuery(id+"F3.boolean.opBoolean","INTERSECT",EDGE,{"derivedFrom":[subQ4,makeQuery(id+"F3.opExtrude","SWEPT_FACE",FACE,{"disambiguationData":[OSD([sQuery(id+"F2.wireOp",EDGE,"E40.1")])]})]}),makeQuery(id+"F3.boolean.opBoolean","INTERSECT",EDGE,{"derivedFrom":[subQ4,makeQuery(id+"F3.opExtrude","SWEPT_FACE",FACE,{"disambiguationData":[OSD([sQuery(id+"F2.wireOp",EDGE,"E40.2")])]})]}),makeQuery(id+"F3.boolean.opBoolean","INTERSECT",EDGE,{"derivedFrom":[subQ4,makeQuery(id+"F3.opExtrude","SWEPT_FACE",FACE,{"disambiguationData":[OSD([sQuery(id+"F2.wireOp",EDGE,"E40.3")])]})]}),makeQuery(id+"F3.boolean.opBoolean","INTERSECT",EDGE,{"derivedFrom":[subQ4,makeQuery(id+"F3.opExtrude","SWEPT_FACE",FACE,{"disambiguationData":[OSD([sQuery(id+"F2.wireOp",EDGE,"E40.4")])]})]}),makeQuery(id+"F3.boolean.opBoolean","INTERSECT",EDGE,{"derivedFrom":[subQ4,makeQuery(id+"F3.opExtrude","SWEPT_FACE",FACE,{"disambiguationData":[OSD([sQuery(id+"F2.wireOp",EDGE,"E40.5")])]})]}),makeQuery(id+"F3.boolean.opBoolean","INTERSECT",EDGE,{"derivedFrom":[subQ2,makeQuery(id+"F3.opExtrude","SWEPT_FACE",FACE,{"disambiguationData":[OSD([sQuery(id+"F2.wireOp",EDGE,"E36.0")])]})]}),makeQuery(id+"F3.boolean.opBoolean","INTERSECT",EDGE,{"derivedFrom":[subQ2,makeQuery(id+"F3.opExtrude","SWEPT_FACE",FACE,{"disambiguationData":[OSD([sQuery(id+"F2.wireOp",EDGE,"E36.1")])]})]}),makeQuery(id+"F3.boolean.opBoolean","INTERSECT",EDGE,{"derivedFrom":[subQ2,makeQuery(id+"F3.opExtrude","SWEPT_FACE",FACE,{"disambiguationData":[OSD([sQuery(id+"F2.wireOp",EDGE,"E36.2")])]})]}),makeQuery(id+"F3.boolean.opBoolean","INTERSECT",EDGE,{"derivedFrom":[subQ2,makeQuery(id+"F3.opExtrude","SWEPT_FACE",FACE,{"disambiguationData":[OSD([sQuery(id+"F2.wireOp",EDGE,"E36.3")])]})]}),makeQuery(id+"F3.boolean.opBoolean","INTERSECT",EDGE,{"derivedFrom":[subQ2,makeQuery(id+"F3.opExtrude","SWEPT_FACE",FACE,{"disambiguationData":[OSD([sQuery(id+"F2.wireOp",EDGE,"E36.4")])]})]}),makeQuery(id+"F3.boolean.opBoolean","INTERSECT",EDGE,{"derivedFrom":[subQ2,makeQuery(id+"F3.opExtrude","SWEPT_FACE",FACE,{"disambiguationData":[OSD([sQuery(id+"F2.wireOp",EDGE,"E36.5")])]})]}),makeQuery(id+"F3.boolean.opBoolean","INTERSECT",EDGE,{"derivedFrom":[subQ2,makeQuery(id+"F3.opExtrude","SWEPT_FACE",FACE,{"disambiguationData":[OSD([sQuery(id+"F2.wireOp",EDGE,"E37.0")])]})]}),makeQuery(id+"F3.boolean.opBoolean","INTERSECT",EDGE,{"derivedFrom":[subQ2,makeQuery(id+"F3.opExtrude","SWEPT_FACE",FACE,{"disambiguationData":[OSD([sQuery(id+"F2.wireOp",EDGE,"E37.1")])]})]}),makeQuery(id+"F3.boolean.opBoolean","INTERSECT",EDGE,{"derivedFrom":[subQ2,makeQuery(id+"F3.opExtrude","SWEPT_FACE",FACE,{"disambiguationData":[OSD([sQuery(id+"F2.wireOp",EDGE,"E37.2")])]})]}),makeQuery(id+"F3.boolean.opBoolean","INTERSECT",EDGE,{"derivedFrom":[subQ2,makeQuery(id+"F3.opExtrude","SWEPT_FACE",FACE,{"disambiguationData":[OSD([sQuery(id+"F2.wireOp",EDGE,"E37.3")])]})]}),makeQuery(id+"F3.boolean.opBoolean","INTERSECT",EDGE,{"derivedFrom":[subQ2,makeQuery(id+"F3.opExtrude","SWEPT_FACE",FACE,{"disambiguationData":[OSD([sQuery(id+"F2.wireOp",EDGE,"E37.4")])]})]}),makeQuery(id+"F3.boolean.opBoolean","INTERSECT",EDGE,{"derivedFrom":[subQ2,makeQuery(id+"F3.opExtrude","SWEPT_FACE",FACE,{"disambiguationData":[OSD([sQuery(id+"F2.wireOp",EDGE,"E37.5")])]})]}),makeQuery(id+"F3.boolean.opBoolean","INTERSECT",EDGE,{"derivedFrom":[subQ2,makeQuery(id+"F3.opExtrude","SWEPT_FACE",FACE,{"disambiguationData":[OSD([sQuery(id+"F2.wireOp",EDGE,"E38.0")])]})]}),makeQuery(id+"F3.boolean.opBoolean","INTERSECT",EDGE,{"derivedFrom":[subQ2,makeQuery(id+"F3.opExtrude","SWEPT_FACE",FACE,{"disambiguationData":[OSD([sQuery(id+"F2.wireOp",EDGE,"E38.1")])]})]}),makeQuery(id+"F3.boolean.opBoolean","INTERSECT",EDGE,{"derivedFrom":[subQ2,makeQuery(id+"F3.opExtrude","SWEPT_FACE",FACE,{"disambiguationData":[OSD([sQuery(id+"F2.wireOp",EDGE,"E38.2")])]})]}),makeQuery(id+"F3.boolean.opBoolean","INTERSECT",EDGE,{"derivedFrom":[subQ2,makeQuery(id+"F3.opExtrude","SWEPT_FACE",FACE,{"disambiguationData":[OSD([sQuery(id+"F2.wireOp",EDGE,"E38.3")])]})]}),makeQuery(id+"F3.boolean.opBoolean","INTERSECT",EDGE,{"derivedFrom":[subQ2,makeQuery(id+"F3.opExtrude","SWEPT_FACE",FACE,{"disambiguationData":[OSD([sQuery(id+"F2.wireOp",EDGE,"E38.4")])]})]}),makeQuery(id+"F3.boolean.opBoolean","INTERSECT",EDGE,{"derivedFrom":[subQ2,makeQuery(id+"F3.opExtrude","SWEPT_FACE",FACE,{"disambiguationData":[OSD([sQuery(id+"F2.wireOp",EDGE,"E38.5")])]})]})]);}
            var Q6;
            {var subQ0=sQuery(id+"F0.wireOp",EDGE,"E6");var subQ1=sQuery(id+"F0.wireOp",EDGE,"E18.top");var subQ2=makeQuery(id+"F1.opExtrude","SWEPT_FACE",FACE,{"disambiguationData":[OSD([subQ0]),TDD([makeQuery(id+"F0.imprint","IMPRINT",EDGE,{"disambiguationData":[TD([[makeQuery(id+"F0.imprint","INTERSECT",VERTEX,{"derivedFrom":[subQ0,sQuery(id+"F0.wireOp",EDGE,"E9")]}),1.0]])],"derivedFrom":subQ0})])]});var subQ4=makeQuery(id+"F1.opExtrude","SWEPT_FACE",FACE,{"disambiguationData":[OSD([subQ0]),TDD([makeQuery(id+"F0.imprint","IMPRINT",EDGE,{"disambiguationData":[TD([[makeQuery(id+"F0.imprint","INTERSECT",VERTEX,{"derivedFrom":[subQ0,subQ1,sQuery(id+"F0.wireOp",EDGE,"E18.right")]}),1.0]])],"derivedFrom":subQ0})])]});var subQ5=makeQuery(id+"F1.opExtrude","SWEPT_FACE",FACE,{"disambiguationData":[OSD([subQ0]),TDD([makeQuery(id+"F0.imprint","IMPRINT",EDGE,{"disambiguationData":[TD([[makeQuery(id+"F0.imprint","INTERSECT",VERTEX,{"derivedFrom":[subQ0,sQuery(id+"F0.wireOp",EDGE,"E12")]}),-1.0]])],"derivedFrom":subQ0})])]});Q6=qUnion([makeQuery(id+"F3.boolean.opBoolean","INTERSECT",EDGE,{"derivedFrom":[subQ5,makeQuery(id+"F3.opExtrude","SWEPT_FACE",FACE,{"disambiguationData":[OSD([sQuery(id+"F2.wireOp",EDGE,"E41.0")])]})]}),makeQuery(id+"F3.boolean.opBoolean","INTERSECT",EDGE,{"derivedFrom":[subQ5,makeQuery(id+"F3.opExtrude","SWEPT_FACE",FACE,{"disambiguationData":[OSD([sQuery(id+"F2.wireOp",EDGE,"E41.1")])]})]}),makeQuery(id+"F3.boolean.opBoolean","INTERSECT",EDGE,{"derivedFrom":[subQ5,makeQuery(id+"F3.opExtrude","SWEPT_FACE",FACE,{"disambiguationData":[OSD([sQuery(id+"F2.wireOp",EDGE,"E41.2")])]})]}),makeQuery(id+"F3.boolean.opBoolean","INTERSECT",EDGE,{"derivedFrom":[subQ5,makeQuery(id+"F3.opExtrude","SWEPT_FACE",FACE,{"disambiguationData":[OSD([sQuery(id+"F2.wireOp",EDGE,"E41.3")])]})]}),makeQuery(id+"F3.boolean.opBoolean","INTERSECT",EDGE,{"derivedFrom":[subQ5,makeQuery(id+"F3.opExtrude","SWEPT_FACE",FACE,{"disambiguationData":[OSD([sQuery(id+"F2.wireOp",EDGE,"E41.4")])]})]}),makeQuery(id+"F3.boolean.opBoolean","INTERSECT",EDGE,{"derivedFrom":[subQ5,makeQuery(id+"F3.opExtrude","SWEPT_FACE",FACE,{"disambiguationData":[OSD([sQuery(id+"F2.wireOp",EDGE,"E41.5")])]})]}),makeQuery(id+"F3.boolean.opBoolean","INTERSECT",EDGE,{"derivedFrom":[subQ5,makeQuery(id+"F3.opExtrude","SWEPT_FACE",FACE,{"disambiguationData":[OSD([sQuery(id+"F2.wireOp",EDGE,"E42.0")])]})]}),makeQuery(id+"F3.boolean.opBoolean","INTERSECT",EDGE,{"derivedFrom":[subQ5,makeQuery(id+"F3.opExtrude","SWEPT_FACE",FACE,{"disambiguationData":[OSD([sQuery(id+"F2.wireOp",EDGE,"E42.1")])]})]}),makeQuery(id+"F3.boolean.opBoolean","INTERSECT",EDGE,{"derivedFrom":[subQ5,makeQuery(id+"F3.opExtrude","SWEPT_FACE",FACE,{"disambiguationData":[OSD([sQuery(id+"F2.wireOp",EDGE,"E42.2")])]})]}),makeQuery(id+"F3.boolean.opBoolean","INTERSECT",EDGE,{"derivedFrom":[subQ5,makeQuery(id+"F3.opExtrude","SWEPT_FACE",FACE,{"disambiguationData":[OSD([sQuery(id+"F2.wireOp",EDGE,"E42.3")])]})]}),makeQuery(id+"F3.boolean.opBoolean","INTERSECT",EDGE,{"derivedFrom":[subQ5,makeQuery(id+"F3.opExtrude","SWEPT_FACE",FACE,{"disambiguationData":[OSD([sQuery(id+"F2.wireOp",EDGE,"E42.4")])]})]}),makeQuery(id+"F3.boolean.opBoolean","INTERSECT",EDGE,{"derivedFrom":[subQ5,makeQuery(id+"F3.opExtrude","SWEPT_FACE",FACE,{"disambiguationData":[OSD([sQuery(id+"F2.wireOp",EDGE,"E42.5")])]})]}),makeQuery(id+"F3.boolean.opBoolean","INTERSECT",EDGE,{"derivedFrom":[subQ4,makeQuery(id+"F3.opExtrude","SWEPT_FACE",FACE,{"disambiguationData":[OSD([sQuery(id+"F2.wireOp",EDGE,"E39.0")])]})]}),makeQuery(id+"F3.boolean.opBoolean","INTERSECT",EDGE,{"derivedFrom":[subQ4,makeQuery(id+"F3.opExtrude","SWEPT_FACE",FACE,{"disambiguationData":[OSD([sQuery(id+"F2.wireOp",EDGE,"E39.1")])]})]}),makeQuery(id+"F3.boolean.opBoolean","INTERSECT",EDGE,{"derivedFrom":[subQ4,makeQuery(id+"F3.opExtrude","SWEPT_FACE",FACE,{"disambiguationData":[OSD([sQuery(id+"F2.wireOp",EDGE,"E39.2")])]})]}),makeQuery(id+"F3.boolean.opBoolean","INTERSECT",EDGE,{"derivedFrom":[subQ4,makeQuery(id+"F3.opExtrude","SWEPT_FACE",FACE,{"disambiguationData":[OSD([sQuery(id+"F2.wireOp",EDGE,"E39.3")])]})]}),makeQuery(id+"F3.boolean.opBoolean","INTERSECT",EDGE,{"derivedFrom":[subQ4,makeQuery(id+"F3.opExtrude","SWEPT_FACE",FACE,{"disambiguationData":[OSD([sQuery(id+"F2.wireOp",EDGE,"E39.4")])]})]}),makeQuery(id+"F3.boolean.opBoolean","INTERSECT",EDGE,{"derivedFrom":[subQ4,makeQuery(id+"F3.opExtrude","SWEPT_FACE",FACE,{"disambiguationData":[OSD([sQuery(id+"F2.wireOp",EDGE,"E39.5")])]})]}),makeQuery(id+"F3.boolean.opBoolean","INTERSECT",EDGE,{"derivedFrom":[subQ4,makeQuery(id+"F3.opExtrude","SWEPT_FACE",FACE,{"disambiguationData":[OSD([sQuery(id+"F2.wireOp",EDGE,"E40.0")])]})]}),makeQuery(id+"F3.boolean.opBoolean","INTERSECT",EDGE,{"derivedFrom":[subQ4,makeQuery(id+"F3.opExtrude","SWEPT_FACE",FACE,{"disambiguationData":[OSD([sQuery(id+"F2.wireOp",EDGE,"E40.1")])]})]}),makeQuery(id+"F3.boolean.opBoolean","INTERSECT",EDGE,{"derivedFrom":[subQ4,makeQuery(id+"F3.opExtrude","SWEPT_FACE",FACE,{"disambiguationData":[OSD([sQuery(id+"F2.wireOp",EDGE,"E40.2")])]})]}),makeQuery(id+"F3.boolean.opBoolean","INTERSECT",EDGE,{"derivedFrom":[subQ4,makeQuery(id+"F3.opExtrude","SWEPT_FACE",FACE,{"disambiguationData":[OSD([sQuery(id+"F2.wireOp",EDGE,"E40.3")])]})]}),makeQuery(id+"F3.boolean.opBoolean","INTERSECT",EDGE,{"derivedFrom":[subQ4,makeQuery(id+"F3.opExtrude","SWEPT_FACE",FACE,{"disambiguationData":[OSD([sQuery(id+"F2.wireOp",EDGE,"E40.4")])]})]}),makeQuery(id+"F3.boolean.opBoolean","INTERSECT",EDGE,{"derivedFrom":[subQ4,makeQuery(id+"F3.opExtrude","SWEPT_FACE",FACE,{"disambiguationData":[OSD([sQuery(id+"F2.wireOp",EDGE,"E40.5")])]})]}),makeQuery(id+"F3.boolean.opBoolean","INTERSECT",EDGE,{"derivedFrom":[subQ2,makeQuery(id+"F3.opExtrude","SWEPT_FACE",FACE,{"disambiguationData":[OSD([sQuery(id+"F2.wireOp",EDGE,"E36.0")])]})]}),makeQuery(id+"F3.boolean.opBoolean","INTERSECT",EDGE,{"derivedFrom":[subQ2,makeQuery(id+"F3.opExtrude","SWEPT_FACE",FACE,{"disambiguationData":[OSD([sQuery(id+"F2.wireOp",EDGE,"E36.1")])]})]}),makeQuery(id+"F3.boolean.opBoolean","INTERSECT",EDGE,{"derivedFrom":[subQ2,makeQuery(id+"F3.opExtrude","SWEPT_FACE",FACE,{"disambiguationData":[OSD([sQuery(id+"F2.wireOp",EDGE,"E36.2")])]})]}),makeQuery(id+"F3.boolean.opBoolean","INTERSECT",EDGE,{"derivedFrom":[subQ2,makeQuery(id+"F3.opExtrude","SWEPT_FACE",FACE,{"disambiguationData":[OSD([sQuery(id+"F2.wireOp",EDGE,"E36.3")])]})]}),makeQuery(id+"F3.boolean.opBoolean","INTERSECT",EDGE,{"derivedFrom":[subQ2,makeQuery(id+"F3.opExtrude","SWEPT_FACE",FACE,{"disambiguationData":[OSD([sQuery(id+"F2.wireOp",EDGE,"E36.4")])]})]}),makeQuery(id+"F3.boolean.opBoolean","INTERSECT",EDGE,{"derivedFrom":[subQ2,makeQuery(id+"F3.opExtrude","SWEPT_FACE",FACE,{"disambiguationData":[OSD([sQuery(id+"F2.wireOp",EDGE,"E36.5")])]})]}),makeQuery(id+"F3.boolean.opBoolean","INTERSECT",EDGE,{"derivedFrom":[subQ2,makeQuery(id+"F3.opExtrude","SWEPT_FACE",FACE,{"disambiguationData":[OSD([sQuery(id+"F2.wireOp",EDGE,"E37.0")])]})]}),makeQuery(id+"F3.boolean.opBoolean","INTERSECT",EDGE,{"derivedFrom":[subQ2,makeQuery(id+"F3.opExtrude","SWEPT_FACE",FACE,{"disambiguationData":[OSD([sQuery(id+"F2.wireOp",EDGE,"E37.1")])]})]}),makeQuery(id+"F3.boolean.opBoolean","INTERSECT",EDGE,{"derivedFrom":[subQ2,makeQuery(id+"F3.opExtrude","SWEPT_FACE",FACE,{"disambiguationData":[OSD([sQuery(id+"F2.wireOp",EDGE,"E37.2")])]})]}),makeQuery(id+"F3.boolean.opBoolean","INTERSECT",EDGE,{"derivedFrom":[subQ2,makeQuery(id+"F3.opExtrude","SWEPT_FACE",FACE,{"disambiguationData":[OSD([sQuery(id+"F2.wireOp",EDGE,"E37.3")])]})]}),makeQuery(id+"F3.boolean.opBoolean","INTERSECT",EDGE,{"derivedFrom":[subQ2,makeQuery(id+"F3.opExtrude","SWEPT_FACE",FACE,{"disambiguationData":[OSD([sQuery(id+"F2.wireOp",EDGE,"E37.4")])]})]}),makeQuery(id+"F3.boolean.opBoolean","INTERSECT",EDGE,{"derivedFrom":[subQ2,makeQuery(id+"F3.opExtrude","SWEPT_FACE",FACE,{"disambiguationData":[OSD([sQuery(id+"F2.wireOp",EDGE,"E37.5")])]})]}),makeQuery(id+"F3.boolean.opBoolean","INTERSECT",EDGE,{"derivedFrom":[subQ2,makeQuery(id+"F3.opExtrude","SWEPT_FACE",FACE,{"disambiguationData":[OSD([sQuery(id+"F2.wireOp",EDGE,"E38.0")])]})]}),makeQuery(id+"F3.boolean.opBoolean","INTERSECT",EDGE,{"derivedFrom":[subQ2,makeQuery(id+"F3.opExtrude","SWEPT_FACE",FACE,{"disambiguationData":[OSD([sQuery(id+"F2.wireOp",EDGE,"E38.1")])]})]}),makeQuery(id+"F3.boolean.opBoolean","INTERSECT",EDGE,{"derivedFrom":[subQ2,makeQuery(id+"F3.opExtrude","SWEPT_FACE",FACE,{"disambiguationData":[OSD([sQuery(id+"F2.wireOp",EDGE,"E38.2")])]})]}),makeQuery(id+"F3.boolean.opBoolean","INTERSECT",EDGE,{"derivedFrom":[subQ2,makeQuery(id+"F3.opExtrude","SWEPT_FACE",FACE,{"disambiguationData":[OSD([sQuery(id+"F2.wireOp",EDGE,"E38.3")])]})]}),makeQuery(id+"F3.boolean.opBoolean","INTERSECT",EDGE,{"derivedFrom":[subQ2,makeQuery(id+"F3.opExtrude","SWEPT_FACE",FACE,{"disambiguationData":[OSD([sQuery(id+"F2.wireOp",EDGE,"E38.4")])]})]}),makeQuery(id+"F3.boolean.opBoolean","INTERSECT",EDGE,{"derivedFrom":[subQ2,makeQuery(id+"F3.opExtrude","SWEPT_FACE",FACE,{"disambiguationData":[OSD([sQuery(id+"F2.wireOp",EDGE,"E38.5")])]})]})]);}
            var Q7;
            {var subQ0=sQuery(id+"F0.wireOp",EDGE,"E6");var subQ1=sQuery(id+"F0.wireOp",EDGE,"E18.top");var subQ2=makeQuery(id+"F1.opExtrude","SWEPT_FACE",FACE,{"disambiguationData":[OSD([subQ0]),TDD([makeQuery(id+"F0.imprint","IMPRINT",EDGE,{"disambiguationData":[TD([[makeQuery(id+"F0.imprint","INTERSECT",VERTEX,{"derivedFrom":[subQ0,sQuery(id+"F0.wireOp",EDGE,"E9")]}),1.0]])],"derivedFrom":subQ0})])]});var subQ4=makeQuery(id+"F1.opExtrude","SWEPT_FACE",FACE,{"disambiguationData":[OSD([subQ0]),TDD([makeQuery(id+"F0.imprint","IMPRINT",EDGE,{"disambiguationData":[TD([[makeQuery(id+"F0.imprint","INTERSECT",VERTEX,{"derivedFrom":[subQ0,subQ1,sQuery(id+"F0.wireOp",EDGE,"E18.right")]}),1.0]])],"derivedFrom":subQ0})])]});var subQ5=makeQuery(id+"F1.opExtrude","SWEPT_FACE",FACE,{"disambiguationData":[OSD([subQ0]),TDD([makeQuery(id+"F0.imprint","IMPRINT",EDGE,{"disambiguationData":[TD([[makeQuery(id+"F0.imprint","INTERSECT",VERTEX,{"derivedFrom":[subQ0,sQuery(id+"F0.wireOp",EDGE,"E12")]}),-1.0]])],"derivedFrom":subQ0})])]});Q7=qUnion([makeQuery(id+"F3.boolean.opBoolean","INTERSECT",EDGE,{"derivedFrom":[subQ5,makeQuery(id+"F3.opExtrude","SWEPT_FACE",FACE,{"disambiguationData":[OSD([sQuery(id+"F2.wireOp",EDGE,"E41.0")])]})]}),makeQuery(id+"F3.boolean.opBoolean","INTERSECT",EDGE,{"derivedFrom":[subQ5,makeQuery(id+"F3.opExtrude","SWEPT_FACE",FACE,{"disambiguationData":[OSD([sQuery(id+"F2.wireOp",EDGE,"E41.1")])]})]}),makeQuery(id+"F3.boolean.opBoolean","INTERSECT",EDGE,{"derivedFrom":[subQ5,makeQuery(id+"F3.opExtrude","SWEPT_FACE",FACE,{"disambiguationData":[OSD([sQuery(id+"F2.wireOp",EDGE,"E41.2")])]})]}),makeQuery(id+"F3.boolean.opBoolean","INTERSECT",EDGE,{"derivedFrom":[subQ5,makeQuery(id+"F3.opExtrude","SWEPT_FACE",FACE,{"disambiguationData":[OSD([sQuery(id+"F2.wireOp",EDGE,"E41.3")])]})]}),makeQuery(id+"F3.boolean.opBoolean","INTERSECT",EDGE,{"derivedFrom":[subQ5,makeQuery(id+"F3.opExtrude","SWEPT_FACE",FACE,{"disambiguationData":[OSD([sQuery(id+"F2.wireOp",EDGE,"E41.4")])]})]}),makeQuery(id+"F3.boolean.opBoolean","INTERSECT",EDGE,{"derivedFrom":[subQ5,makeQuery(id+"F3.opExtrude","SWEPT_FACE",FACE,{"disambiguationData":[OSD([sQuery(id+"F2.wireOp",EDGE,"E41.5")])]})]}),makeQuery(id+"F3.boolean.opBoolean","INTERSECT",EDGE,{"derivedFrom":[subQ5,makeQuery(id+"F3.opExtrude","SWEPT_FACE",FACE,{"disambiguationData":[OSD([sQuery(id+"F2.wireOp",EDGE,"E42.0")])]})]}),makeQuery(id+"F3.boolean.opBoolean","INTERSECT",EDGE,{"derivedFrom":[subQ5,makeQuery(id+"F3.opExtrude","SWEPT_FACE",FACE,{"disambiguationData":[OSD([sQuery(id+"F2.wireOp",EDGE,"E42.1")])]})]}),makeQuery(id+"F3.boolean.opBoolean","INTERSECT",EDGE,{"derivedFrom":[subQ5,makeQuery(id+"F3.opExtrude","SWEPT_FACE",FACE,{"disambiguationData":[OSD([sQuery(id+"F2.wireOp",EDGE,"E42.2")])]})]}),makeQuery(id+"F3.boolean.opBoolean","INTERSECT",EDGE,{"derivedFrom":[subQ5,makeQuery(id+"F3.opExtrude","SWEPT_FACE",FACE,{"disambiguationData":[OSD([sQuery(id+"F2.wireOp",EDGE,"E42.3")])]})]}),makeQuery(id+"F3.boolean.opBoolean","INTERSECT",EDGE,{"derivedFrom":[subQ5,makeQuery(id+"F3.opExtrude","SWEPT_FACE",FACE,{"disambiguationData":[OSD([sQuery(id+"F2.wireOp",EDGE,"E42.4")])]})]}),makeQuery(id+"F3.boolean.opBoolean","INTERSECT",EDGE,{"derivedFrom":[subQ5,makeQuery(id+"F3.opExtrude","SWEPT_FACE",FACE,{"disambiguationData":[OSD([sQuery(id+"F2.wireOp",EDGE,"E42.5")])]})]}),makeQuery(id+"F3.boolean.opBoolean","INTERSECT",EDGE,{"derivedFrom":[subQ4,makeQuery(id+"F3.opExtrude","SWEPT_FACE",FACE,{"disambiguationData":[OSD([sQuery(id+"F2.wireOp",EDGE,"E39.0")])]})]}),makeQuery(id+"F3.boolean.opBoolean","INTERSECT",EDGE,{"derivedFrom":[subQ4,makeQuery(id+"F3.opExtrude","SWEPT_FACE",FACE,{"disambiguationData":[OSD([sQuery(id+"F2.wireOp",EDGE,"E39.1")])]})]}),makeQuery(id+"F3.boolean.opBoolean","INTERSECT",EDGE,{"derivedFrom":[subQ4,makeQuery(id+"F3.opExtrude","SWEPT_FACE",FACE,{"disambiguationData":[OSD([sQuery(id+"F2.wireOp",EDGE,"E39.2")])]})]}),makeQuery(id+"F3.boolean.opBoolean","INTERSECT",EDGE,{"derivedFrom":[subQ4,makeQuery(id+"F3.opExtrude","SWEPT_FACE",FACE,{"disambiguationData":[OSD([sQuery(id+"F2.wireOp",EDGE,"E39.3")])]})]}),makeQuery(id+"F3.boolean.opBoolean","INTERSECT",EDGE,{"derivedFrom":[subQ4,makeQuery(id+"F3.opExtrude","SWEPT_FACE",FACE,{"disambiguationData":[OSD([sQuery(id+"F2.wireOp",EDGE,"E39.4")])]})]}),makeQuery(id+"F3.boolean.opBoolean","INTERSECT",EDGE,{"derivedFrom":[subQ4,makeQuery(id+"F3.opExtrude","SWEPT_FACE",FACE,{"disambiguationData":[OSD([sQuery(id+"F2.wireOp",EDGE,"E39.5")])]})]}),makeQuery(id+"F3.boolean.opBoolean","INTERSECT",EDGE,{"derivedFrom":[subQ4,makeQuery(id+"F3.opExtrude","SWEPT_FACE",FACE,{"disambiguationData":[OSD([sQuery(id+"F2.wireOp",EDGE,"E40.0")])]})]}),makeQuery(id+"F3.boolean.opBoolean","INTERSECT",EDGE,{"derivedFrom":[subQ4,makeQuery(id+"F3.opExtrude","SWEPT_FACE",FACE,{"disambiguationData":[OSD([sQuery(id+"F2.wireOp",EDGE,"E40.1")])]})]}),makeQuery(id+"F3.boolean.opBoolean","INTERSECT",EDGE,{"derivedFrom":[subQ4,makeQuery(id+"F3.opExtrude","SWEPT_FACE",FACE,{"disambiguationData":[OSD([sQuery(id+"F2.wireOp",EDGE,"E40.2")])]})]}),makeQuery(id+"F3.boolean.opBoolean","INTERSECT",EDGE,{"derivedFrom":[subQ4,makeQuery(id+"F3.opExtrude","SWEPT_FACE",FACE,{"disambiguationData":[OSD([sQuery(id+"F2.wireOp",EDGE,"E40.3")])]})]}),makeQuery(id+"F3.boolean.opBoolean","INTERSECT",EDGE,{"derivedFrom":[subQ4,makeQuery(id+"F3.opExtrude","SWEPT_FACE",FACE,{"disambiguationData":[OSD([sQuery(id+"F2.wireOp",EDGE,"E40.4")])]})]}),makeQuery(id+"F3.boolean.opBoolean","INTERSECT",EDGE,{"derivedFrom":[subQ4,makeQuery(id+"F3.opExtrude","SWEPT_FACE",FACE,{"disambiguationData":[OSD([sQuery(id+"F2.wireOp",EDGE,"E40.5")])]})]}),makeQuery(id+"F3.boolean.opBoolean","INTERSECT",EDGE,{"derivedFrom":[subQ2,makeQuery(id+"F3.opExtrude","SWEPT_FACE",FACE,{"disambiguationData":[OSD([sQuery(id+"F2.wireOp",EDGE,"E36.0")])]})]}),makeQuery(id+"F3.boolean.opBoolean","INTERSECT",EDGE,{"derivedFrom":[subQ2,makeQuery(id+"F3.opExtrude","SWEPT_FACE",FACE,{"disambiguationData":[OSD([sQuery(id+"F2.wireOp",EDGE,"E36.1")])]})]}),makeQuery(id+"F3.boolean.opBoolean","INTERSECT",EDGE,{"derivedFrom":[subQ2,makeQuery(id+"F3.opExtrude","SWEPT_FACE",FACE,{"disambiguationData":[OSD([sQuery(id+"F2.wireOp",EDGE,"E36.2")])]})]}),makeQuery(id+"F3.boolean.opBoolean","INTERSECT",EDGE,{"derivedFrom":[subQ2,makeQuery(id+"F3.opExtrude","SWEPT_FACE",FACE,{"disambiguationData":[OSD([sQuery(id+"F2.wireOp",EDGE,"E36.3")])]})]}),makeQuery(id+"F3.boolean.opBoolean","INTERSECT",EDGE,{"derivedFrom":[subQ2,makeQuery(id+"F3.opExtrude","SWEPT_FACE",FACE,{"disambiguationData":[OSD([sQuery(id+"F2.wireOp",EDGE,"E36.4")])]})]}),makeQuery(id+"F3.boolean.opBoolean","INTERSECT",EDGE,{"derivedFrom":[subQ2,makeQuery(id+"F3.opExtrude","SWEPT_FACE",FACE,{"disambiguationData":[OSD([sQuery(id+"F2.wireOp",EDGE,"E36.5")])]})]}),makeQuery(id+"F3.boolean.opBoolean","INTERSECT",EDGE,{"derivedFrom":[subQ2,makeQuery(id+"F3.opExtrude","SWEPT_FACE",FACE,{"disambiguationData":[OSD([sQuery(id+"F2.wireOp",EDGE,"E37.0")])]})]}),makeQuery(id+"F3.boolean.opBoolean","INTERSECT",EDGE,{"derivedFrom":[subQ2,makeQuery(id+"F3.opExtrude","SWEPT_FACE",FACE,{"disambiguationData":[OSD([sQuery(id+"F2.wireOp",EDGE,"E37.1")])]})]}),makeQuery(id+"F3.boolean.opBoolean","INTERSECT",EDGE,{"derivedFrom":[subQ2,makeQuery(id+"F3.opExtrude","SWEPT_FACE",FACE,{"disambiguationData":[OSD([sQuery(id+"F2.wireOp",EDGE,"E37.2")])]})]}),makeQuery(id+"F3.boolean.opBoolean","INTERSECT",EDGE,{"derivedFrom":[subQ2,makeQuery(id+"F3.opExtrude","SWEPT_FACE",FACE,{"disambiguationData":[OSD([sQuery(id+"F2.wireOp",EDGE,"E37.3")])]})]}),makeQuery(id+"F3.boolean.opBoolean","INTERSECT",EDGE,{"derivedFrom":[subQ2,makeQuery(id+"F3.opExtrude","SWEPT_FACE",FACE,{"disambiguationData":[OSD([sQuery(id+"F2.wireOp",EDGE,"E37.4")])]})]}),makeQuery(id+"F3.boolean.opBoolean","INTERSECT",EDGE,{"derivedFrom":[subQ2,makeQuery(id+"F3.opExtrude","SWEPT_FACE",FACE,{"disambiguationData":[OSD([sQuery(id+"F2.wireOp",EDGE,"E37.5")])]})]}),makeQuery(id+"F3.boolean.opBoolean","INTERSECT",EDGE,{"derivedFrom":[subQ2,makeQuery(id+"F3.opExtrude","SWEPT_FACE",FACE,{"disambiguationData":[OSD([sQuery(id+"F2.wireOp",EDGE,"E38.0")])]})]}),makeQuery(id+"F3.boolean.opBoolean","INTERSECT",EDGE,{"derivedFrom":[subQ2,makeQuery(id+"F3.opExtrude","SWEPT_FACE",FACE,{"disambiguationData":[OSD([sQuery(id+"F2.wireOp",EDGE,"E38.1")])]})]}),makeQuery(id+"F3.boolean.opBoolean","INTERSECT",EDGE,{"derivedFrom":[subQ2,makeQuery(id+"F3.opExtrude","SWEPT_FACE",FACE,{"disambiguationData":[OSD([sQuery(id+"F2.wireOp",EDGE,"E38.2")])]})]}),makeQuery(id+"F3.boolean.opBoolean","INTERSECT",EDGE,{"derivedFrom":[subQ2,makeQuery(id+"F3.opExtrude","SWEPT_FACE",FACE,{"disambiguationData":[OSD([sQuery(id+"F2.wireOp",EDGE,"E38.3")])]})]}),makeQuery(id+"F3.boolean.opBoolean","INTERSECT",EDGE,{"derivedFrom":[subQ2,makeQuery(id+"F3.opExtrude","SWEPT_FACE",FACE,{"disambiguationData":[OSD([sQuery(id+"F2.wireOp",EDGE,"E38.4")])]})]}),makeQuery(id+"F3.boolean.opBoolean","INTERSECT",EDGE,{"derivedFrom":[subQ2,makeQuery(id+"F3.opExtrude","SWEPT_FACE",FACE,{"disambiguationData":[OSD([sQuery(id+"F2.wireOp",EDGE,"E38.5")])]})]})]);}
            var Q8;
            {var subQ0=sQuery(id+"F0.wireOp",EDGE,"E6");var subQ1=sQuery(id+"F0.wireOp",EDGE,"E18.top");var subQ2=makeQuery(id+"F1.opExtrude","SWEPT_FACE",FACE,{"disambiguationData":[OSD([subQ0]),TDD([makeQuery(id+"F0.imprint","IMPRINT",EDGE,{"disambiguationData":[TD([[makeQuery(id+"F0.imprint","INTERSECT",VERTEX,{"derivedFrom":[subQ0,sQuery(id+"F0.wireOp",EDGE,"E9")]}),1.0]])],"derivedFrom":subQ0})])]});var subQ4=makeQuery(id+"F1.opExtrude","SWEPT_FACE",FACE,{"disambiguationData":[OSD([subQ0]),TDD([makeQuery(id+"F0.imprint","IMPRINT",EDGE,{"disambiguationData":[TD([[makeQuery(id+"F0.imprint","INTERSECT",VERTEX,{"derivedFrom":[subQ0,subQ1,sQuery(id+"F0.wireOp",EDGE,"E18.right")]}),1.0]])],"derivedFrom":subQ0})])]});var subQ5=makeQuery(id+"F1.opExtrude","SWEPT_FACE",FACE,{"disambiguationData":[OSD([subQ0]),TDD([makeQuery(id+"F0.imprint","IMPRINT",EDGE,{"disambiguationData":[TD([[makeQuery(id+"F0.imprint","INTERSECT",VERTEX,{"derivedFrom":[subQ0,sQuery(id+"F0.wireOp",EDGE,"E12")]}),-1.0]])],"derivedFrom":subQ0})])]});Q8=qUnion([makeQuery(id+"F3.boolean.opBoolean","INTERSECT",EDGE,{"derivedFrom":[subQ5,makeQuery(id+"F3.opExtrude","SWEPT_FACE",FACE,{"disambiguationData":[OSD([sQuery(id+"F2.wireOp",EDGE,"E41.0")])]})]}),makeQuery(id+"F3.boolean.opBoolean","INTERSECT",EDGE,{"derivedFrom":[subQ5,makeQuery(id+"F3.opExtrude","SWEPT_FACE",FACE,{"disambiguationData":[OSD([sQuery(id+"F2.wireOp",EDGE,"E41.1")])]})]}),makeQuery(id+"F3.boolean.opBoolean","INTERSECT",EDGE,{"derivedFrom":[subQ5,makeQuery(id+"F3.opExtrude","SWEPT_FACE",FACE,{"disambiguationData":[OSD([sQuery(id+"F2.wireOp",EDGE,"E41.2")])]})]}),makeQuery(id+"F3.boolean.opBoolean","INTERSECT",EDGE,{"derivedFrom":[subQ5,makeQuery(id+"F3.opExtrude","SWEPT_FACE",FACE,{"disambiguationData":[OSD([sQuery(id+"F2.wireOp",EDGE,"E41.3")])]})]}),makeQuery(id+"F3.boolean.opBoolean","INTERSECT",EDGE,{"derivedFrom":[subQ5,makeQuery(id+"F3.opExtrude","SWEPT_FACE",FACE,{"disambiguationData":[OSD([sQuery(id+"F2.wireOp",EDGE,"E41.4")])]})]}),makeQuery(id+"F3.boolean.opBoolean","INTERSECT",EDGE,{"derivedFrom":[subQ5,makeQuery(id+"F3.opExtrude","SWEPT_FACE",FACE,{"disambiguationData":[OSD([sQuery(id+"F2.wireOp",EDGE,"E41.5")])]})]}),makeQuery(id+"F3.boolean.opBoolean","INTERSECT",EDGE,{"derivedFrom":[subQ5,makeQuery(id+"F3.opExtrude","SWEPT_FACE",FACE,{"disambiguationData":[OSD([sQuery(id+"F2.wireOp",EDGE,"E42.0")])]})]}),makeQuery(id+"F3.boolean.opBoolean","INTERSECT",EDGE,{"derivedFrom":[subQ5,makeQuery(id+"F3.opExtrude","SWEPT_FACE",FACE,{"disambiguationData":[OSD([sQuery(id+"F2.wireOp",EDGE,"E42.1")])]})]}),makeQuery(id+"F3.boolean.opBoolean","INTERSECT",EDGE,{"derivedFrom":[subQ5,makeQuery(id+"F3.opExtrude","SWEPT_FACE",FACE,{"disambiguationData":[OSD([sQuery(id+"F2.wireOp",EDGE,"E42.2")])]})]}),makeQuery(id+"F3.boolean.opBoolean","INTERSECT",EDGE,{"derivedFrom":[subQ5,makeQuery(id+"F3.opExtrude","SWEPT_FACE",FACE,{"disambiguationData":[OSD([sQuery(id+"F2.wireOp",EDGE,"E42.3")])]})]}),makeQuery(id+"F3.boolean.opBoolean","INTERSECT",EDGE,{"derivedFrom":[subQ5,makeQuery(id+"F3.opExtrude","SWEPT_FACE",FACE,{"disambiguationData":[OSD([sQuery(id+"F2.wireOp",EDGE,"E42.4")])]})]}),makeQuery(id+"F3.boolean.opBoolean","INTERSECT",EDGE,{"derivedFrom":[subQ5,makeQuery(id+"F3.opExtrude","SWEPT_FACE",FACE,{"disambiguationData":[OSD([sQuery(id+"F2.wireOp",EDGE,"E42.5")])]})]}),makeQuery(id+"F3.boolean.opBoolean","INTERSECT",EDGE,{"derivedFrom":[subQ4,makeQuery(id+"F3.opExtrude","SWEPT_FACE",FACE,{"disambiguationData":[OSD([sQuery(id+"F2.wireOp",EDGE,"E39.0")])]})]}),makeQuery(id+"F3.boolean.opBoolean","INTERSECT",EDGE,{"derivedFrom":[subQ4,makeQuery(id+"F3.opExtrude","SWEPT_FACE",FACE,{"disambiguationData":[OSD([sQuery(id+"F2.wireOp",EDGE,"E39.1")])]})]}),makeQuery(id+"F3.boolean.opBoolean","INTERSECT",EDGE,{"derivedFrom":[subQ4,makeQuery(id+"F3.opExtrude","SWEPT_FACE",FACE,{"disambiguationData":[OSD([sQuery(id+"F2.wireOp",EDGE,"E39.2")])]})]}),makeQuery(id+"F3.boolean.opBoolean","INTERSECT",EDGE,{"derivedFrom":[subQ4,makeQuery(id+"F3.opExtrude","SWEPT_FACE",FACE,{"disambiguationData":[OSD([sQuery(id+"F2.wireOp",EDGE,"E39.3")])]})]}),makeQuery(id+"F3.boolean.opBoolean","INTERSECT",EDGE,{"derivedFrom":[subQ4,makeQuery(id+"F3.opExtrude","SWEPT_FACE",FACE,{"disambiguationData":[OSD([sQuery(id+"F2.wireOp",EDGE,"E39.4")])]})]}),makeQuery(id+"F3.boolean.opBoolean","INTERSECT",EDGE,{"derivedFrom":[subQ4,makeQuery(id+"F3.opExtrude","SWEPT_FACE",FACE,{"disambiguationData":[OSD([sQuery(id+"F2.wireOp",EDGE,"E39.5")])]})]}),makeQuery(id+"F3.boolean.opBoolean","INTERSECT",EDGE,{"derivedFrom":[subQ4,makeQuery(id+"F3.opExtrude","SWEPT_FACE",FACE,{"disambiguationData":[OSD([sQuery(id+"F2.wireOp",EDGE,"E40.0")])]})]}),makeQuery(id+"F3.boolean.opBoolean","INTERSECT",EDGE,{"derivedFrom":[subQ4,makeQuery(id+"F3.opExtrude","SWEPT_FACE",FACE,{"disambiguationData":[OSD([sQuery(id+"F2.wireOp",EDGE,"E40.1")])]})]}),makeQuery(id+"F3.boolean.opBoolean","INTERSECT",EDGE,{"derivedFrom":[subQ4,makeQuery(id+"F3.opExtrude","SWEPT_FACE",FACE,{"disambiguationData":[OSD([sQuery(id+"F2.wireOp",EDGE,"E40.2")])]})]}),makeQuery(id+"F3.boolean.opBoolean","INTERSECT",EDGE,{"derivedFrom":[subQ4,makeQuery(id+"F3.opExtrude","SWEPT_FACE",FACE,{"disambiguationData":[OSD([sQuery(id+"F2.wireOp",EDGE,"E40.3")])]})]}),makeQuery(id+"F3.boolean.opBoolean","INTERSECT",EDGE,{"derivedFrom":[subQ4,makeQuery(id+"F3.opExtrude","SWEPT_FACE",FACE,{"disambiguationData":[OSD([sQuery(id+"F2.wireOp",EDGE,"E40.4")])]})]}),makeQuery(id+"F3.boolean.opBoolean","INTERSECT",EDGE,{"derivedFrom":[subQ4,makeQuery(id+"F3.opExtrude","SWEPT_FACE",FACE,{"disambiguationData":[OSD([sQuery(id+"F2.wireOp",EDGE,"E40.5")])]})]}),makeQuery(id+"F3.boolean.opBoolean","INTERSECT",EDGE,{"derivedFrom":[subQ2,makeQuery(id+"F3.opExtrude","SWEPT_FACE",FACE,{"disambiguationData":[OSD([sQuery(id+"F2.wireOp",EDGE,"E36.0")])]})]}),makeQuery(id+"F3.boolean.opBoolean","INTERSECT",EDGE,{"derivedFrom":[subQ2,makeQuery(id+"F3.opExtrude","SWEPT_FACE",FACE,{"disambiguationData":[OSD([sQuery(id+"F2.wireOp",EDGE,"E36.1")])]})]}),makeQuery(id+"F3.boolean.opBoolean","INTERSECT",EDGE,{"derivedFrom":[subQ2,makeQuery(id+"F3.opExtrude","SWEPT_FACE",FACE,{"disambiguationData":[OSD([sQuery(id+"F2.wireOp",EDGE,"E36.2")])]})]}),makeQuery(id+"F3.boolean.opBoolean","INTERSECT",EDGE,{"derivedFrom":[subQ2,makeQuery(id+"F3.opExtrude","SWEPT_FACE",FACE,{"disambiguationData":[OSD([sQuery(id+"F2.wireOp",EDGE,"E36.3")])]})]}),makeQuery(id+"F3.boolean.opBoolean","INTERSECT",EDGE,{"derivedFrom":[subQ2,makeQuery(id+"F3.opExtrude","SWEPT_FACE",FACE,{"disambiguationData":[OSD([sQuery(id+"F2.wireOp",EDGE,"E36.4")])]})]}),makeQuery(id+"F3.boolean.opBoolean","INTERSECT",EDGE,{"derivedFrom":[subQ2,makeQuery(id+"F3.opExtrude","SWEPT_FACE",FACE,{"disambiguationData":[OSD([sQuery(id+"F2.wireOp",EDGE,"E36.5")])]})]}),makeQuery(id+"F3.boolean.opBoolean","INTERSECT",EDGE,{"derivedFrom":[subQ2,makeQuery(id+"F3.opExtrude","SWEPT_FACE",FACE,{"disambiguationData":[OSD([sQuery(id+"F2.wireOp",EDGE,"E37.0")])]})]}),makeQuery(id+"F3.boolean.opBoolean","INTERSECT",EDGE,{"derivedFrom":[subQ2,makeQuery(id+"F3.opExtrude","SWEPT_FACE",FACE,{"disambiguationData":[OSD([sQuery(id+"F2.wireOp",EDGE,"E37.1")])]})]}),makeQuery(id+"F3.boolean.opBoolean","INTERSECT",EDGE,{"derivedFrom":[subQ2,makeQuery(id+"F3.opExtrude","SWEPT_FACE",FACE,{"disambiguationData":[OSD([sQuery(id+"F2.wireOp",EDGE,"E37.2")])]})]}),makeQuery(id+"F3.boolean.opBoolean","INTERSECT",EDGE,{"derivedFrom":[subQ2,makeQuery(id+"F3.opExtrude","SWEPT_FACE",FACE,{"disambiguationData":[OSD([sQuery(id+"F2.wireOp",EDGE,"E37.3")])]})]}),makeQuery(id+"F3.boolean.opBoolean","INTERSECT",EDGE,{"derivedFrom":[subQ2,makeQuery(id+"F3.opExtrude","SWEPT_FACE",FACE,{"disambiguationData":[OSD([sQuery(id+"F2.wireOp",EDGE,"E37.4")])]})]}),makeQuery(id+"F3.boolean.opBoolean","INTERSECT",EDGE,{"derivedFrom":[subQ2,makeQuery(id+"F3.opExtrude","SWEPT_FACE",FACE,{"disambiguationData":[OSD([sQuery(id+"F2.wireOp",EDGE,"E37.5")])]})]}),makeQuery(id+"F3.boolean.opBoolean","INTERSECT",EDGE,{"derivedFrom":[subQ2,makeQuery(id+"F3.opExtrude","SWEPT_FACE",FACE,{"disambiguationData":[OSD([sQuery(id+"F2.wireOp",EDGE,"E38.0")])]})]}),makeQuery(id+"F3.boolean.opBoolean","INTERSECT",EDGE,{"derivedFrom":[subQ2,makeQuery(id+"F3.opExtrude","SWEPT_FACE",FACE,{"disambiguationData":[OSD([sQuery(id+"F2.wireOp",EDGE,"E38.1")])]})]}),makeQuery(id+"F3.boolean.opBoolean","INTERSECT",EDGE,{"derivedFrom":[subQ2,makeQuery(id+"F3.opExtrude","SWEPT_FACE",FACE,{"disambiguationData":[OSD([sQuery(id+"F2.wireOp",EDGE,"E38.2")])]})]}),makeQuery(id+"F3.boolean.opBoolean","INTERSECT",EDGE,{"derivedFrom":[subQ2,makeQuery(id+"F3.opExtrude","SWEPT_FACE",FACE,{"disambiguationData":[OSD([sQuery(id+"F2.wireOp",EDGE,"E38.3")])]})]}),makeQuery(id+"F3.boolean.opBoolean","INTERSECT",EDGE,{"derivedFrom":[subQ2,makeQuery(id+"F3.opExtrude","SWEPT_FACE",FACE,{"disambiguationData":[OSD([sQuery(id+"F2.wireOp",EDGE,"E38.4")])]})]}),makeQuery(id+"F3.boolean.opBoolean","INTERSECT",EDGE,{"derivedFrom":[subQ2,makeQuery(id+"F3.opExtrude","SWEPT_FACE",FACE,{"disambiguationData":[OSD([sQuery(id+"F2.wireOp",EDGE,"E38.5")])]})]})]);}
            var Q9;
            {var subQ0=sQuery(id+"F0.wireOp",EDGE,"E6");var subQ1=sQuery(id+"F0.wireOp",EDGE,"E18.top");var subQ2=makeQuery(id+"F1.opExtrude","SWEPT_FACE",FACE,{"disambiguationData":[OSD([subQ0]),TDD([makeQuery(id+"F0.imprint","IMPRINT",EDGE,{"disambiguationData":[TD([[makeQuery(id+"F0.imprint","INTERSECT",VERTEX,{"derivedFrom":[subQ0,sQuery(id+"F0.wireOp",EDGE,"E9")]}),1.0]])],"derivedFrom":subQ0})])]});var subQ4=makeQuery(id+"F1.opExtrude","SWEPT_FACE",FACE,{"disambiguationData":[OSD([subQ0]),TDD([makeQuery(id+"F0.imprint","IMPRINT",EDGE,{"disambiguationData":[TD([[makeQuery(id+"F0.imprint","INTERSECT",VERTEX,{"derivedFrom":[subQ0,subQ1,sQuery(id+"F0.wireOp",EDGE,"E18.right")]}),1.0]])],"derivedFrom":subQ0})])]});var subQ5=makeQuery(id+"F1.opExtrude","SWEPT_FACE",FACE,{"disambiguationData":[OSD([subQ0]),TDD([makeQuery(id+"F0.imprint","IMPRINT",EDGE,{"disambiguationData":[TD([[makeQuery(id+"F0.imprint","INTERSECT",VERTEX,{"derivedFrom":[subQ0,sQuery(id+"F0.wireOp",EDGE,"E12")]}),-1.0]])],"derivedFrom":subQ0})])]});Q9=qUnion([makeQuery(id+"F3.boolean.opBoolean","INTERSECT",EDGE,{"derivedFrom":[subQ5,makeQuery(id+"F3.opExtrude","SWEPT_FACE",FACE,{"disambiguationData":[OSD([sQuery(id+"F2.wireOp",EDGE,"E41.0")])]})]}),makeQuery(id+"F3.boolean.opBoolean","INTERSECT",EDGE,{"derivedFrom":[subQ5,makeQuery(id+"F3.opExtrude","SWEPT_FACE",FACE,{"disambiguationData":[OSD([sQuery(id+"F2.wireOp",EDGE,"E41.1")])]})]}),makeQuery(id+"F3.boolean.opBoolean","INTERSECT",EDGE,{"derivedFrom":[subQ5,makeQuery(id+"F3.opExtrude","SWEPT_FACE",FACE,{"disambiguationData":[OSD([sQuery(id+"F2.wireOp",EDGE,"E41.2")])]})]}),makeQuery(id+"F3.boolean.opBoolean","INTERSECT",EDGE,{"derivedFrom":[subQ5,makeQuery(id+"F3.opExtrude","SWEPT_FACE",FACE,{"disambiguationData":[OSD([sQuery(id+"F2.wireOp",EDGE,"E41.3")])]})]}),makeQuery(id+"F3.boolean.opBoolean","INTERSECT",EDGE,{"derivedFrom":[subQ5,makeQuery(id+"F3.opExtrude","SWEPT_FACE",FACE,{"disambiguationData":[OSD([sQuery(id+"F2.wireOp",EDGE,"E41.4")])]})]}),makeQuery(id+"F3.boolean.opBoolean","INTERSECT",EDGE,{"derivedFrom":[subQ5,makeQuery(id+"F3.opExtrude","SWEPT_FACE",FACE,{"disambiguationData":[OSD([sQuery(id+"F2.wireOp",EDGE,"E41.5")])]})]}),makeQuery(id+"F3.boolean.opBoolean","INTERSECT",EDGE,{"derivedFrom":[subQ5,makeQuery(id+"F3.opExtrude","SWEPT_FACE",FACE,{"disambiguationData":[OSD([sQuery(id+"F2.wireOp",EDGE,"E42.0")])]})]}),makeQuery(id+"F3.boolean.opBoolean","INTERSECT",EDGE,{"derivedFrom":[subQ5,makeQuery(id+"F3.opExtrude","SWEPT_FACE",FACE,{"disambiguationData":[OSD([sQuery(id+"F2.wireOp",EDGE,"E42.1")])]})]}),makeQuery(id+"F3.boolean.opBoolean","INTERSECT",EDGE,{"derivedFrom":[subQ5,makeQuery(id+"F3.opExtrude","SWEPT_FACE",FACE,{"disambiguationData":[OSD([sQuery(id+"F2.wireOp",EDGE,"E42.2")])]})]}),makeQuery(id+"F3.boolean.opBoolean","INTERSECT",EDGE,{"derivedFrom":[subQ5,makeQuery(id+"F3.opExtrude","SWEPT_FACE",FACE,{"disambiguationData":[OSD([sQuery(id+"F2.wireOp",EDGE,"E42.3")])]})]}),makeQuery(id+"F3.boolean.opBoolean","INTERSECT",EDGE,{"derivedFrom":[subQ5,makeQuery(id+"F3.opExtrude","SWEPT_FACE",FACE,{"disambiguationData":[OSD([sQuery(id+"F2.wireOp",EDGE,"E42.4")])]})]}),makeQuery(id+"F3.boolean.opBoolean","INTERSECT",EDGE,{"derivedFrom":[subQ5,makeQuery(id+"F3.opExtrude","SWEPT_FACE",FACE,{"disambiguationData":[OSD([sQuery(id+"F2.wireOp",EDGE,"E42.5")])]})]}),makeQuery(id+"F3.boolean.opBoolean","INTERSECT",EDGE,{"derivedFrom":[subQ4,makeQuery(id+"F3.opExtrude","SWEPT_FACE",FACE,{"disambiguationData":[OSD([sQuery(id+"F2.wireOp",EDGE,"E39.0")])]})]}),makeQuery(id+"F3.boolean.opBoolean","INTERSECT",EDGE,{"derivedFrom":[subQ4,makeQuery(id+"F3.opExtrude","SWEPT_FACE",FACE,{"disambiguationData":[OSD([sQuery(id+"F2.wireOp",EDGE,"E39.1")])]})]}),makeQuery(id+"F3.boolean.opBoolean","INTERSECT",EDGE,{"derivedFrom":[subQ4,makeQuery(id+"F3.opExtrude","SWEPT_FACE",FACE,{"disambiguationData":[OSD([sQuery(id+"F2.wireOp",EDGE,"E39.2")])]})]}),makeQuery(id+"F3.boolean.opBoolean","INTERSECT",EDGE,{"derivedFrom":[subQ4,makeQuery(id+"F3.opExtrude","SWEPT_FACE",FACE,{"disambiguationData":[OSD([sQuery(id+"F2.wireOp",EDGE,"E39.3")])]})]}),makeQuery(id+"F3.boolean.opBoolean","INTERSECT",EDGE,{"derivedFrom":[subQ4,makeQuery(id+"F3.opExtrude","SWEPT_FACE",FACE,{"disambiguationData":[OSD([sQuery(id+"F2.wireOp",EDGE,"E39.4")])]})]}),makeQuery(id+"F3.boolean.opBoolean","INTERSECT",EDGE,{"derivedFrom":[subQ4,makeQuery(id+"F3.opExtrude","SWEPT_FACE",FACE,{"disambiguationData":[OSD([sQuery(id+"F2.wireOp",EDGE,"E39.5")])]})]}),makeQuery(id+"F3.boolean.opBoolean","INTERSECT",EDGE,{"derivedFrom":[subQ4,makeQuery(id+"F3.opExtrude","SWEPT_FACE",FACE,{"disambiguationData":[OSD([sQuery(id+"F2.wireOp",EDGE,"E40.0")])]})]}),makeQuery(id+"F3.boolean.opBoolean","INTERSECT",EDGE,{"derivedFrom":[subQ4,makeQuery(id+"F3.opExtrude","SWEPT_FACE",FACE,{"disambiguationData":[OSD([sQuery(id+"F2.wireOp",EDGE,"E40.1")])]})]}),makeQuery(id+"F3.boolean.opBoolean","INTERSECT",EDGE,{"derivedFrom":[subQ4,makeQuery(id+"F3.opExtrude","SWEPT_FACE",FACE,{"disambiguationData":[OSD([sQuery(id+"F2.wireOp",EDGE,"E40.2")])]})]}),makeQuery(id+"F3.boolean.opBoolean","INTERSECT",EDGE,{"derivedFrom":[subQ4,makeQuery(id+"F3.opExtrude","SWEPT_FACE",FACE,{"disambiguationData":[OSD([sQuery(id+"F2.wireOp",EDGE,"E40.3")])]})]}),makeQuery(id+"F3.boolean.opBoolean","INTERSECT",EDGE,{"derivedFrom":[subQ4,makeQuery(id+"F3.opExtrude","SWEPT_FACE",FACE,{"disambiguationData":[OSD([sQuery(id+"F2.wireOp",EDGE,"E40.4")])]})]}),makeQuery(id+"F3.boolean.opBoolean","INTERSECT",EDGE,{"derivedFrom":[subQ4,makeQuery(id+"F3.opExtrude","SWEPT_FACE",FACE,{"disambiguationData":[OSD([sQuery(id+"F2.wireOp",EDGE,"E40.5")])]})]}),makeQuery(id+"F3.boolean.opBoolean","INTERSECT",EDGE,{"derivedFrom":[subQ2,makeQuery(id+"F3.opExtrude","SWEPT_FACE",FACE,{"disambiguationData":[OSD([sQuery(id+"F2.wireOp",EDGE,"E36.0")])]})]}),makeQuery(id+"F3.boolean.opBoolean","INTERSECT",EDGE,{"derivedFrom":[subQ2,makeQuery(id+"F3.opExtrude","SWEPT_FACE",FACE,{"disambiguationData":[OSD([sQuery(id+"F2.wireOp",EDGE,"E36.1")])]})]}),makeQuery(id+"F3.boolean.opBoolean","INTERSECT",EDGE,{"derivedFrom":[subQ2,makeQuery(id+"F3.opExtrude","SWEPT_FACE",FACE,{"disambiguationData":[OSD([sQuery(id+"F2.wireOp",EDGE,"E36.2")])]})]}),makeQuery(id+"F3.boolean.opBoolean","INTERSECT",EDGE,{"derivedFrom":[subQ2,makeQuery(id+"F3.opExtrude","SWEPT_FACE",FACE,{"disambiguationData":[OSD([sQuery(id+"F2.wireOp",EDGE,"E36.3")])]})]}),makeQuery(id+"F3.boolean.opBoolean","INTERSECT",EDGE,{"derivedFrom":[subQ2,makeQuery(id+"F3.opExtrude","SWEPT_FACE",FACE,{"disambiguationData":[OSD([sQuery(id+"F2.wireOp",EDGE,"E36.4")])]})]}),makeQuery(id+"F3.boolean.opBoolean","INTERSECT",EDGE,{"derivedFrom":[subQ2,makeQuery(id+"F3.opExtrude","SWEPT_FACE",FACE,{"disambiguationData":[OSD([sQuery(id+"F2.wireOp",EDGE,"E36.5")])]})]}),makeQuery(id+"F3.boolean.opBoolean","INTERSECT",EDGE,{"derivedFrom":[subQ2,makeQuery(id+"F3.opExtrude","SWEPT_FACE",FACE,{"disambiguationData":[OSD([sQuery(id+"F2.wireOp",EDGE,"E37.0")])]})]}),makeQuery(id+"F3.boolean.opBoolean","INTERSECT",EDGE,{"derivedFrom":[subQ2,makeQuery(id+"F3.opExtrude","SWEPT_FACE",FACE,{"disambiguationData":[OSD([sQuery(id+"F2.wireOp",EDGE,"E37.1")])]})]}),makeQuery(id+"F3.boolean.opBoolean","INTERSECT",EDGE,{"derivedFrom":[subQ2,makeQuery(id+"F3.opExtrude","SWEPT_FACE",FACE,{"disambiguationData":[OSD([sQuery(id+"F2.wireOp",EDGE,"E37.2")])]})]}),makeQuery(id+"F3.boolean.opBoolean","INTERSECT",EDGE,{"derivedFrom":[subQ2,makeQuery(id+"F3.opExtrude","SWEPT_FACE",FACE,{"disambiguationData":[OSD([sQuery(id+"F2.wireOp",EDGE,"E37.3")])]})]}),makeQuery(id+"F3.boolean.opBoolean","INTERSECT",EDGE,{"derivedFrom":[subQ2,makeQuery(id+"F3.opExtrude","SWEPT_FACE",FACE,{"disambiguationData":[OSD([sQuery(id+"F2.wireOp",EDGE,"E37.4")])]})]}),makeQuery(id+"F3.boolean.opBoolean","INTERSECT",EDGE,{"derivedFrom":[subQ2,makeQuery(id+"F3.opExtrude","SWEPT_FACE",FACE,{"disambiguationData":[OSD([sQuery(id+"F2.wireOp",EDGE,"E37.5")])]})]}),makeQuery(id+"F3.boolean.opBoolean","INTERSECT",EDGE,{"derivedFrom":[subQ2,makeQuery(id+"F3.opExtrude","SWEPT_FACE",FACE,{"disambiguationData":[OSD([sQuery(id+"F2.wireOp",EDGE,"E38.0")])]})]}),makeQuery(id+"F3.boolean.opBoolean","INTERSECT",EDGE,{"derivedFrom":[subQ2,makeQuery(id+"F3.opExtrude","SWEPT_FACE",FACE,{"disambiguationData":[OSD([sQuery(id+"F2.wireOp",EDGE,"E38.1")])]})]}),makeQuery(id+"F3.boolean.opBoolean","INTERSECT",EDGE,{"derivedFrom":[subQ2,makeQuery(id+"F3.opExtrude","SWEPT_FACE",FACE,{"disambiguationData":[OSD([sQuery(id+"F2.wireOp",EDGE,"E38.2")])]})]}),makeQuery(id+"F3.boolean.opBoolean","INTERSECT",EDGE,{"derivedFrom":[subQ2,makeQuery(id+"F3.opExtrude","SWEPT_FACE",FACE,{"disambiguationData":[OSD([sQuery(id+"F2.wireOp",EDGE,"E38.3")])]})]}),makeQuery(id+"F3.boolean.opBoolean","INTERSECT",EDGE,{"derivedFrom":[subQ2,makeQuery(id+"F3.opExtrude","SWEPT_FACE",FACE,{"disambiguationData":[OSD([sQuery(id+"F2.wireOp",EDGE,"E38.4")])]})]}),makeQuery(id+"F3.boolean.opBoolean","INTERSECT",EDGE,{"derivedFrom":[subQ2,makeQuery(id+"F3.opExtrude","SWEPT_FACE",FACE,{"disambiguationData":[OSD([sQuery(id+"F2.wireOp",EDGE,"E38.5")])]})]})]);}
            var Q10;
            {var subQ0=sQuery(id+"F0.wireOp",EDGE,"E6");var subQ1=sQuery(id+"F0.wireOp",EDGE,"E18.top");var subQ2=makeQuery(id+"F1.opExtrude","SWEPT_FACE",FACE,{"disambiguationData":[OSD([subQ0]),TDD([makeQuery(id+"F0.imprint","IMPRINT",EDGE,{"disambiguationData":[TD([[makeQuery(id+"F0.imprint","INTERSECT",VERTEX,{"derivedFrom":[subQ0,sQuery(id+"F0.wireOp",EDGE,"E9")]}),1.0]])],"derivedFrom":subQ0})])]});var subQ4=makeQuery(id+"F1.opExtrude","SWEPT_FACE",FACE,{"disambiguationData":[OSD([subQ0]),TDD([makeQuery(id+"F0.imprint","IMPRINT",EDGE,{"disambiguationData":[TD([[makeQuery(id+"F0.imprint","INTERSECT",VERTEX,{"derivedFrom":[subQ0,subQ1,sQuery(id+"F0.wireOp",EDGE,"E18.right")]}),1.0]])],"derivedFrom":subQ0})])]});var subQ5=makeQuery(id+"F1.opExtrude","SWEPT_FACE",FACE,{"disambiguationData":[OSD([subQ0]),TDD([makeQuery(id+"F0.imprint","IMPRINT",EDGE,{"disambiguationData":[TD([[makeQuery(id+"F0.imprint","INTERSECT",VERTEX,{"derivedFrom":[subQ0,sQuery(id+"F0.wireOp",EDGE,"E12")]}),-1.0]])],"derivedFrom":subQ0})])]});Q10=qUnion([makeQuery(id+"F3.boolean.opBoolean","INTERSECT",EDGE,{"derivedFrom":[subQ5,makeQuery(id+"F3.opExtrude","SWEPT_FACE",FACE,{"disambiguationData":[OSD([sQuery(id+"F2.wireOp",EDGE,"E41.0")])]})]}),makeQuery(id+"F3.boolean.opBoolean","INTERSECT",EDGE,{"derivedFrom":[subQ5,makeQuery(id+"F3.opExtrude","SWEPT_FACE",FACE,{"disambiguationData":[OSD([sQuery(id+"F2.wireOp",EDGE,"E41.1")])]})]}),makeQuery(id+"F3.boolean.opBoolean","INTERSECT",EDGE,{"derivedFrom":[subQ5,makeQuery(id+"F3.opExtrude","SWEPT_FACE",FACE,{"disambiguationData":[OSD([sQuery(id+"F2.wireOp",EDGE,"E41.2")])]})]}),makeQuery(id+"F3.boolean.opBoolean","INTERSECT",EDGE,{"derivedFrom":[subQ5,makeQuery(id+"F3.opExtrude","SWEPT_FACE",FACE,{"disambiguationData":[OSD([sQuery(id+"F2.wireOp",EDGE,"E41.3")])]})]}),makeQuery(id+"F3.boolean.opBoolean","INTERSECT",EDGE,{"derivedFrom":[subQ5,makeQuery(id+"F3.opExtrude","SWEPT_FACE",FACE,{"disambiguationData":[OSD([sQuery(id+"F2.wireOp",EDGE,"E41.4")])]})]}),makeQuery(id+"F3.boolean.opBoolean","INTERSECT",EDGE,{"derivedFrom":[subQ5,makeQuery(id+"F3.opExtrude","SWEPT_FACE",FACE,{"disambiguationData":[OSD([sQuery(id+"F2.wireOp",EDGE,"E41.5")])]})]}),makeQuery(id+"F3.boolean.opBoolean","INTERSECT",EDGE,{"derivedFrom":[subQ5,makeQuery(id+"F3.opExtrude","SWEPT_FACE",FACE,{"disambiguationData":[OSD([sQuery(id+"F2.wireOp",EDGE,"E42.0")])]})]}),makeQuery(id+"F3.boolean.opBoolean","INTERSECT",EDGE,{"derivedFrom":[subQ5,makeQuery(id+"F3.opExtrude","SWEPT_FACE",FACE,{"disambiguationData":[OSD([sQuery(id+"F2.wireOp",EDGE,"E42.1")])]})]}),makeQuery(id+"F3.boolean.opBoolean","INTERSECT",EDGE,{"derivedFrom":[subQ5,makeQuery(id+"F3.opExtrude","SWEPT_FACE",FACE,{"disambiguationData":[OSD([sQuery(id+"F2.wireOp",EDGE,"E42.2")])]})]}),makeQuery(id+"F3.boolean.opBoolean","INTERSECT",EDGE,{"derivedFrom":[subQ5,makeQuery(id+"F3.opExtrude","SWEPT_FACE",FACE,{"disambiguationData":[OSD([sQuery(id+"F2.wireOp",EDGE,"E42.3")])]})]}),makeQuery(id+"F3.boolean.opBoolean","INTERSECT",EDGE,{"derivedFrom":[subQ5,makeQuery(id+"F3.opExtrude","SWEPT_FACE",FACE,{"disambiguationData":[OSD([sQuery(id+"F2.wireOp",EDGE,"E42.4")])]})]}),makeQuery(id+"F3.boolean.opBoolean","INTERSECT",EDGE,{"derivedFrom":[subQ5,makeQuery(id+"F3.opExtrude","SWEPT_FACE",FACE,{"disambiguationData":[OSD([sQuery(id+"F2.wireOp",EDGE,"E42.5")])]})]}),makeQuery(id+"F3.boolean.opBoolean","INTERSECT",EDGE,{"derivedFrom":[subQ4,makeQuery(id+"F3.opExtrude","SWEPT_FACE",FACE,{"disambiguationData":[OSD([sQuery(id+"F2.wireOp",EDGE,"E39.0")])]})]}),makeQuery(id+"F3.boolean.opBoolean","INTERSECT",EDGE,{"derivedFrom":[subQ4,makeQuery(id+"F3.opExtrude","SWEPT_FACE",FACE,{"disambiguationData":[OSD([sQuery(id+"F2.wireOp",EDGE,"E39.1")])]})]}),makeQuery(id+"F3.boolean.opBoolean","INTERSECT",EDGE,{"derivedFrom":[subQ4,makeQuery(id+"F3.opExtrude","SWEPT_FACE",FACE,{"disambiguationData":[OSD([sQuery(id+"F2.wireOp",EDGE,"E39.2")])]})]}),makeQuery(id+"F3.boolean.opBoolean","INTERSECT",EDGE,{"derivedFrom":[subQ4,makeQuery(id+"F3.opExtrude","SWEPT_FACE",FACE,{"disambiguationData":[OSD([sQuery(id+"F2.wireOp",EDGE,"E39.3")])]})]}),makeQuery(id+"F3.boolean.opBoolean","INTERSECT",EDGE,{"derivedFrom":[subQ4,makeQuery(id+"F3.opExtrude","SWEPT_FACE",FACE,{"disambiguationData":[OSD([sQuery(id+"F2.wireOp",EDGE,"E39.4")])]})]}),makeQuery(id+"F3.boolean.opBoolean","INTERSECT",EDGE,{"derivedFrom":[subQ4,makeQuery(id+"F3.opExtrude","SWEPT_FACE",FACE,{"disambiguationData":[OSD([sQuery(id+"F2.wireOp",EDGE,"E39.5")])]})]}),makeQuery(id+"F3.boolean.opBoolean","INTERSECT",EDGE,{"derivedFrom":[subQ4,makeQuery(id+"F3.opExtrude","SWEPT_FACE",FACE,{"disambiguationData":[OSD([sQuery(id+"F2.wireOp",EDGE,"E40.0")])]})]}),makeQuery(id+"F3.boolean.opBoolean","INTERSECT",EDGE,{"derivedFrom":[subQ4,makeQuery(id+"F3.opExtrude","SWEPT_FACE",FACE,{"disambiguationData":[OSD([sQuery(id+"F2.wireOp",EDGE,"E40.1")])]})]}),makeQuery(id+"F3.boolean.opBoolean","INTERSECT",EDGE,{"derivedFrom":[subQ4,makeQuery(id+"F3.opExtrude","SWEPT_FACE",FACE,{"disambiguationData":[OSD([sQuery(id+"F2.wireOp",EDGE,"E40.2")])]})]}),makeQuery(id+"F3.boolean.opBoolean","INTERSECT",EDGE,{"derivedFrom":[subQ4,makeQuery(id+"F3.opExtrude","SWEPT_FACE",FACE,{"disambiguationData":[OSD([sQuery(id+"F2.wireOp",EDGE,"E40.3")])]})]}),makeQuery(id+"F3.boolean.opBoolean","INTERSECT",EDGE,{"derivedFrom":[subQ4,makeQuery(id+"F3.opExtrude","SWEPT_FACE",FACE,{"disambiguationData":[OSD([sQuery(id+"F2.wireOp",EDGE,"E40.4")])]})]}),makeQuery(id+"F3.boolean.opBoolean","INTERSECT",EDGE,{"derivedFrom":[subQ4,makeQuery(id+"F3.opExtrude","SWEPT_FACE",FACE,{"disambiguationData":[OSD([sQuery(id+"F2.wireOp",EDGE,"E40.5")])]})]}),makeQuery(id+"F3.boolean.opBoolean","INTERSECT",EDGE,{"derivedFrom":[subQ2,makeQuery(id+"F3.opExtrude","SWEPT_FACE",FACE,{"disambiguationData":[OSD([sQuery(id+"F2.wireOp",EDGE,"E36.0")])]})]}),makeQuery(id+"F3.boolean.opBoolean","INTERSECT",EDGE,{"derivedFrom":[subQ2,makeQuery(id+"F3.opExtrude","SWEPT_FACE",FACE,{"disambiguationData":[OSD([sQuery(id+"F2.wireOp",EDGE,"E36.1")])]})]}),makeQuery(id+"F3.boolean.opBoolean","INTERSECT",EDGE,{"derivedFrom":[subQ2,makeQuery(id+"F3.opExtrude","SWEPT_FACE",FACE,{"disambiguationData":[OSD([sQuery(id+"F2.wireOp",EDGE,"E36.2")])]})]}),makeQuery(id+"F3.boolean.opBoolean","INTERSECT",EDGE,{"derivedFrom":[subQ2,makeQuery(id+"F3.opExtrude","SWEPT_FACE",FACE,{"disambiguationData":[OSD([sQuery(id+"F2.wireOp",EDGE,"E36.3")])]})]}),makeQuery(id+"F3.boolean.opBoolean","INTERSECT",EDGE,{"derivedFrom":[subQ2,makeQuery(id+"F3.opExtrude","SWEPT_FACE",FACE,{"disambiguationData":[OSD([sQuery(id+"F2.wireOp",EDGE,"E36.4")])]})]}),makeQuery(id+"F3.boolean.opBoolean","INTERSECT",EDGE,{"derivedFrom":[subQ2,makeQuery(id+"F3.opExtrude","SWEPT_FACE",FACE,{"disambiguationData":[OSD([sQuery(id+"F2.wireOp",EDGE,"E36.5")])]})]}),makeQuery(id+"F3.boolean.opBoolean","INTERSECT",EDGE,{"derivedFrom":[subQ2,makeQuery(id+"F3.opExtrude","SWEPT_FACE",FACE,{"disambiguationData":[OSD([sQuery(id+"F2.wireOp",EDGE,"E37.0")])]})]}),makeQuery(id+"F3.boolean.opBoolean","INTERSECT",EDGE,{"derivedFrom":[subQ2,makeQuery(id+"F3.opExtrude","SWEPT_FACE",FACE,{"disambiguationData":[OSD([sQuery(id+"F2.wireOp",EDGE,"E37.1")])]})]}),makeQuery(id+"F3.boolean.opBoolean","INTERSECT",EDGE,{"derivedFrom":[subQ2,makeQuery(id+"F3.opExtrude","SWEPT_FACE",FACE,{"disambiguationData":[OSD([sQuery(id+"F2.wireOp",EDGE,"E37.2")])]})]}),makeQuery(id+"F3.boolean.opBoolean","INTERSECT",EDGE,{"derivedFrom":[subQ2,makeQuery(id+"F3.opExtrude","SWEPT_FACE",FACE,{"disambiguationData":[OSD([sQuery(id+"F2.wireOp",EDGE,"E37.3")])]})]}),makeQuery(id+"F3.boolean.opBoolean","INTERSECT",EDGE,{"derivedFrom":[subQ2,makeQuery(id+"F3.opExtrude","SWEPT_FACE",FACE,{"disambiguationData":[OSD([sQuery(id+"F2.wireOp",EDGE,"E37.4")])]})]}),makeQuery(id+"F3.boolean.opBoolean","INTERSECT",EDGE,{"derivedFrom":[subQ2,makeQuery(id+"F3.opExtrude","SWEPT_FACE",FACE,{"disambiguationData":[OSD([sQuery(id+"F2.wireOp",EDGE,"E37.5")])]})]}),makeQuery(id+"F3.boolean.opBoolean","INTERSECT",EDGE,{"derivedFrom":[subQ2,makeQuery(id+"F3.opExtrude","SWEPT_FACE",FACE,{"disambiguationData":[OSD([sQuery(id+"F2.wireOp",EDGE,"E38.0")])]})]}),makeQuery(id+"F3.boolean.opBoolean","INTERSECT",EDGE,{"derivedFrom":[subQ2,makeQuery(id+"F3.opExtrude","SWEPT_FACE",FACE,{"disambiguationData":[OSD([sQuery(id+"F2.wireOp",EDGE,"E38.1")])]})]}),makeQuery(id+"F3.boolean.opBoolean","INTERSECT",EDGE,{"derivedFrom":[subQ2,makeQuery(id+"F3.opExtrude","SWEPT_FACE",FACE,{"disambiguationData":[OSD([sQuery(id+"F2.wireOp",EDGE,"E38.2")])]})]}),makeQuery(id+"F3.boolean.opBoolean","INTERSECT",EDGE,{"derivedFrom":[subQ2,makeQuery(id+"F3.opExtrude","SWEPT_FACE",FACE,{"disambiguationData":[OSD([sQuery(id+"F2.wireOp",EDGE,"E38.3")])]})]}),makeQuery(id+"F3.boolean.opBoolean","INTERSECT",EDGE,{"derivedFrom":[subQ2,makeQuery(id+"F3.opExtrude","SWEPT_FACE",FACE,{"disambiguationData":[OSD([sQuery(id+"F2.wireOp",EDGE,"E38.4")])]})]}),makeQuery(id+"F3.boolean.opBoolean","INTERSECT",EDGE,{"derivedFrom":[subQ2,makeQuery(id+"F3.opExtrude","SWEPT_FACE",FACE,{"disambiguationData":[OSD([sQuery(id+"F2.wireOp",EDGE,"E38.5")])]})]})]);}
            var Q11;
            {var subQ0=sQuery(id+"F0.wireOp",EDGE,"E6");var subQ1=sQuery(id+"F0.wireOp",EDGE,"E18.top");var subQ2=makeQuery(id+"F1.opExtrude","SWEPT_FACE",FACE,{"disambiguationData":[OSD([subQ0]),TDD([makeQuery(id+"F0.imprint","IMPRINT",EDGE,{"disambiguationData":[TD([[makeQuery(id+"F0.imprint","INTERSECT",VERTEX,{"derivedFrom":[subQ0,sQuery(id+"F0.wireOp",EDGE,"E9")]}),1.0]])],"derivedFrom":subQ0})])]});var subQ4=makeQuery(id+"F1.opExtrude","SWEPT_FACE",FACE,{"disambiguationData":[OSD([subQ0]),TDD([makeQuery(id+"F0.imprint","IMPRINT",EDGE,{"disambiguationData":[TD([[makeQuery(id+"F0.imprint","INTERSECT",VERTEX,{"derivedFrom":[subQ0,subQ1,sQuery(id+"F0.wireOp",EDGE,"E18.right")]}),1.0]])],"derivedFrom":subQ0})])]});var subQ5=makeQuery(id+"F1.opExtrude","SWEPT_FACE",FACE,{"disambiguationData":[OSD([subQ0]),TDD([makeQuery(id+"F0.imprint","IMPRINT",EDGE,{"disambiguationData":[TD([[makeQuery(id+"F0.imprint","INTERSECT",VERTEX,{"derivedFrom":[subQ0,sQuery(id+"F0.wireOp",EDGE,"E12")]}),-1.0]])],"derivedFrom":subQ0})])]});Q11=qUnion([makeQuery(id+"F3.boolean.opBoolean","INTERSECT",EDGE,{"derivedFrom":[subQ5,makeQuery(id+"F3.opExtrude","SWEPT_FACE",FACE,{"disambiguationData":[OSD([sQuery(id+"F2.wireOp",EDGE,"E41.0")])]})]}),makeQuery(id+"F3.boolean.opBoolean","INTERSECT",EDGE,{"derivedFrom":[subQ5,makeQuery(id+"F3.opExtrude","SWEPT_FACE",FACE,{"disambiguationData":[OSD([sQuery(id+"F2.wireOp",EDGE,"E41.1")])]})]}),makeQuery(id+"F3.boolean.opBoolean","INTERSECT",EDGE,{"derivedFrom":[subQ5,makeQuery(id+"F3.opExtrude","SWEPT_FACE",FACE,{"disambiguationData":[OSD([sQuery(id+"F2.wireOp",EDGE,"E41.2")])]})]}),makeQuery(id+"F3.boolean.opBoolean","INTERSECT",EDGE,{"derivedFrom":[subQ5,makeQuery(id+"F3.opExtrude","SWEPT_FACE",FACE,{"disambiguationData":[OSD([sQuery(id+"F2.wireOp",EDGE,"E41.3")])]})]}),makeQuery(id+"F3.boolean.opBoolean","INTERSECT",EDGE,{"derivedFrom":[subQ5,makeQuery(id+"F3.opExtrude","SWEPT_FACE",FACE,{"disambiguationData":[OSD([sQuery(id+"F2.wireOp",EDGE,"E41.4")])]})]}),makeQuery(id+"F3.boolean.opBoolean","INTERSECT",EDGE,{"derivedFrom":[subQ5,makeQuery(id+"F3.opExtrude","SWEPT_FACE",FACE,{"disambiguationData":[OSD([sQuery(id+"F2.wireOp",EDGE,"E41.5")])]})]}),makeQuery(id+"F3.boolean.opBoolean","INTERSECT",EDGE,{"derivedFrom":[subQ5,makeQuery(id+"F3.opExtrude","SWEPT_FACE",FACE,{"disambiguationData":[OSD([sQuery(id+"F2.wireOp",EDGE,"E42.0")])]})]}),makeQuery(id+"F3.boolean.opBoolean","INTERSECT",EDGE,{"derivedFrom":[subQ5,makeQuery(id+"F3.opExtrude","SWEPT_FACE",FACE,{"disambiguationData":[OSD([sQuery(id+"F2.wireOp",EDGE,"E42.1")])]})]}),makeQuery(id+"F3.boolean.opBoolean","INTERSECT",EDGE,{"derivedFrom":[subQ5,makeQuery(id+"F3.opExtrude","SWEPT_FACE",FACE,{"disambiguationData":[OSD([sQuery(id+"F2.wireOp",EDGE,"E42.2")])]})]}),makeQuery(id+"F3.boolean.opBoolean","INTERSECT",EDGE,{"derivedFrom":[subQ5,makeQuery(id+"F3.opExtrude","SWEPT_FACE",FACE,{"disambiguationData":[OSD([sQuery(id+"F2.wireOp",EDGE,"E42.3")])]})]}),makeQuery(id+"F3.boolean.opBoolean","INTERSECT",EDGE,{"derivedFrom":[subQ5,makeQuery(id+"F3.opExtrude","SWEPT_FACE",FACE,{"disambiguationData":[OSD([sQuery(id+"F2.wireOp",EDGE,"E42.4")])]})]}),makeQuery(id+"F3.boolean.opBoolean","INTERSECT",EDGE,{"derivedFrom":[subQ5,makeQuery(id+"F3.opExtrude","SWEPT_FACE",FACE,{"disambiguationData":[OSD([sQuery(id+"F2.wireOp",EDGE,"E42.5")])]})]}),makeQuery(id+"F3.boolean.opBoolean","INTERSECT",EDGE,{"derivedFrom":[subQ4,makeQuery(id+"F3.opExtrude","SWEPT_FACE",FACE,{"disambiguationData":[OSD([sQuery(id+"F2.wireOp",EDGE,"E39.0")])]})]}),makeQuery(id+"F3.boolean.opBoolean","INTERSECT",EDGE,{"derivedFrom":[subQ4,makeQuery(id+"F3.opExtrude","SWEPT_FACE",FACE,{"disambiguationData":[OSD([sQuery(id+"F2.wireOp",EDGE,"E39.1")])]})]}),makeQuery(id+"F3.boolean.opBoolean","INTERSECT",EDGE,{"derivedFrom":[subQ4,makeQuery(id+"F3.opExtrude","SWEPT_FACE",FACE,{"disambiguationData":[OSD([sQuery(id+"F2.wireOp",EDGE,"E39.2")])]})]}),makeQuery(id+"F3.boolean.opBoolean","INTERSECT",EDGE,{"derivedFrom":[subQ4,makeQuery(id+"F3.opExtrude","SWEPT_FACE",FACE,{"disambiguationData":[OSD([sQuery(id+"F2.wireOp",EDGE,"E39.3")])]})]}),makeQuery(id+"F3.boolean.opBoolean","INTERSECT",EDGE,{"derivedFrom":[subQ4,makeQuery(id+"F3.opExtrude","SWEPT_FACE",FACE,{"disambiguationData":[OSD([sQuery(id+"F2.wireOp",EDGE,"E39.4")])]})]}),makeQuery(id+"F3.boolean.opBoolean","INTERSECT",EDGE,{"derivedFrom":[subQ4,makeQuery(id+"F3.opExtrude","SWEPT_FACE",FACE,{"disambiguationData":[OSD([sQuery(id+"F2.wireOp",EDGE,"E39.5")])]})]}),makeQuery(id+"F3.boolean.opBoolean","INTERSECT",EDGE,{"derivedFrom":[subQ4,makeQuery(id+"F3.opExtrude","SWEPT_FACE",FACE,{"disambiguationData":[OSD([sQuery(id+"F2.wireOp",EDGE,"E40.0")])]})]}),makeQuery(id+"F3.boolean.opBoolean","INTERSECT",EDGE,{"derivedFrom":[subQ4,makeQuery(id+"F3.opExtrude","SWEPT_FACE",FACE,{"disambiguationData":[OSD([sQuery(id+"F2.wireOp",EDGE,"E40.1")])]})]}),makeQuery(id+"F3.boolean.opBoolean","INTERSECT",EDGE,{"derivedFrom":[subQ4,makeQuery(id+"F3.opExtrude","SWEPT_FACE",FACE,{"disambiguationData":[OSD([sQuery(id+"F2.wireOp",EDGE,"E40.2")])]})]}),makeQuery(id+"F3.boolean.opBoolean","INTERSECT",EDGE,{"derivedFrom":[subQ4,makeQuery(id+"F3.opExtrude","SWEPT_FACE",FACE,{"disambiguationData":[OSD([sQuery(id+"F2.wireOp",EDGE,"E40.3")])]})]}),makeQuery(id+"F3.boolean.opBoolean","INTERSECT",EDGE,{"derivedFrom":[subQ4,makeQuery(id+"F3.opExtrude","SWEPT_FACE",FACE,{"disambiguationData":[OSD([sQuery(id+"F2.wireOp",EDGE,"E40.4")])]})]}),makeQuery(id+"F3.boolean.opBoolean","INTERSECT",EDGE,{"derivedFrom":[subQ4,makeQuery(id+"F3.opExtrude","SWEPT_FACE",FACE,{"disambiguationData":[OSD([sQuery(id+"F2.wireOp",EDGE,"E40.5")])]})]}),makeQuery(id+"F3.boolean.opBoolean","INTERSECT",EDGE,{"derivedFrom":[subQ2,makeQuery(id+"F3.opExtrude","SWEPT_FACE",FACE,{"disambiguationData":[OSD([sQuery(id+"F2.wireOp",EDGE,"E36.0")])]})]}),makeQuery(id+"F3.boolean.opBoolean","INTERSECT",EDGE,{"derivedFrom":[subQ2,makeQuery(id+"F3.opExtrude","SWEPT_FACE",FACE,{"disambiguationData":[OSD([sQuery(id+"F2.wireOp",EDGE,"E36.1")])]})]}),makeQuery(id+"F3.boolean.opBoolean","INTERSECT",EDGE,{"derivedFrom":[subQ2,makeQuery(id+"F3.opExtrude","SWEPT_FACE",FACE,{"disambiguationData":[OSD([sQuery(id+"F2.wireOp",EDGE,"E36.2")])]})]}),makeQuery(id+"F3.boolean.opBoolean","INTERSECT",EDGE,{"derivedFrom":[subQ2,makeQuery(id+"F3.opExtrude","SWEPT_FACE",FACE,{"disambiguationData":[OSD([sQuery(id+"F2.wireOp",EDGE,"E36.3")])]})]}),makeQuery(id+"F3.boolean.opBoolean","INTERSECT",EDGE,{"derivedFrom":[subQ2,makeQuery(id+"F3.opExtrude","SWEPT_FACE",FACE,{"disambiguationData":[OSD([sQuery(id+"F2.wireOp",EDGE,"E36.4")])]})]}),makeQuery(id+"F3.boolean.opBoolean","INTERSECT",EDGE,{"derivedFrom":[subQ2,makeQuery(id+"F3.opExtrude","SWEPT_FACE",FACE,{"disambiguationData":[OSD([sQuery(id+"F2.wireOp",EDGE,"E36.5")])]})]}),makeQuery(id+"F3.boolean.opBoolean","INTERSECT",EDGE,{"derivedFrom":[subQ2,makeQuery(id+"F3.opExtrude","SWEPT_FACE",FACE,{"disambiguationData":[OSD([sQuery(id+"F2.wireOp",EDGE,"E37.0")])]})]}),makeQuery(id+"F3.boolean.opBoolean","INTERSECT",EDGE,{"derivedFrom":[subQ2,makeQuery(id+"F3.opExtrude","SWEPT_FACE",FACE,{"disambiguationData":[OSD([sQuery(id+"F2.wireOp",EDGE,"E37.1")])]})]}),makeQuery(id+"F3.boolean.opBoolean","INTERSECT",EDGE,{"derivedFrom":[subQ2,makeQuery(id+"F3.opExtrude","SWEPT_FACE",FACE,{"disambiguationData":[OSD([sQuery(id+"F2.wireOp",EDGE,"E37.2")])]})]}),makeQuery(id+"F3.boolean.opBoolean","INTERSECT",EDGE,{"derivedFrom":[subQ2,makeQuery(id+"F3.opExtrude","SWEPT_FACE",FACE,{"disambiguationData":[OSD([sQuery(id+"F2.wireOp",EDGE,"E37.3")])]})]}),makeQuery(id+"F3.boolean.opBoolean","INTERSECT",EDGE,{"derivedFrom":[subQ2,makeQuery(id+"F3.opExtrude","SWEPT_FACE",FACE,{"disambiguationData":[OSD([sQuery(id+"F2.wireOp",EDGE,"E37.4")])]})]}),makeQuery(id+"F3.boolean.opBoolean","INTERSECT",EDGE,{"derivedFrom":[subQ2,makeQuery(id+"F3.opExtrude","SWEPT_FACE",FACE,{"disambiguationData":[OSD([sQuery(id+"F2.wireOp",EDGE,"E37.5")])]})]}),makeQuery(id+"F3.boolean.opBoolean","INTERSECT",EDGE,{"derivedFrom":[subQ2,makeQuery(id+"F3.opExtrude","SWEPT_FACE",FACE,{"disambiguationData":[OSD([sQuery(id+"F2.wireOp",EDGE,"E38.0")])]})]}),makeQuery(id+"F3.boolean.opBoolean","INTERSECT",EDGE,{"derivedFrom":[subQ2,makeQuery(id+"F3.opExtrude","SWEPT_FACE",FACE,{"disambiguationData":[OSD([sQuery(id+"F2.wireOp",EDGE,"E38.1")])]})]}),makeQuery(id+"F3.boolean.opBoolean","INTERSECT",EDGE,{"derivedFrom":[subQ2,makeQuery(id+"F3.opExtrude","SWEPT_FACE",FACE,{"disambiguationData":[OSD([sQuery(id+"F2.wireOp",EDGE,"E38.2")])]})]}),makeQuery(id+"F3.boolean.opBoolean","INTERSECT",EDGE,{"derivedFrom":[subQ2,makeQuery(id+"F3.opExtrude","SWEPT_FACE",FACE,{"disambiguationData":[OSD([sQuery(id+"F2.wireOp",EDGE,"E38.3")])]})]}),makeQuery(id+"F3.boolean.opBoolean","INTERSECT",EDGE,{"derivedFrom":[subQ2,makeQuery(id+"F3.opExtrude","SWEPT_FACE",FACE,{"disambiguationData":[OSD([sQuery(id+"F2.wireOp",EDGE,"E38.4")])]})]}),makeQuery(id+"F3.boolean.opBoolean","INTERSECT",EDGE,{"derivedFrom":[subQ2,makeQuery(id+"F3.opExtrude","SWEPT_FACE",FACE,{"disambiguationData":[OSD([sQuery(id+"F2.wireOp",EDGE,"E38.5")])]})]})]);}
            var Q12;
            {var subQ0=sQuery(id+"F0.wireOp",EDGE,"E6");var subQ1=sQuery(id+"F0.wireOp",EDGE,"E18.top");var subQ2=makeQuery(id+"F1.opExtrude","SWEPT_FACE",FACE,{"disambiguationData":[OSD([subQ0]),TDD([makeQuery(id+"F0.imprint","IMPRINT",EDGE,{"disambiguationData":[TD([[makeQuery(id+"F0.imprint","INTERSECT",VERTEX,{"derivedFrom":[subQ0,sQuery(id+"F0.wireOp",EDGE,"E9")]}),1.0]])],"derivedFrom":subQ0})])]});var subQ4=makeQuery(id+"F1.opExtrude","SWEPT_FACE",FACE,{"disambiguationData":[OSD([subQ0]),TDD([makeQuery(id+"F0.imprint","IMPRINT",EDGE,{"disambiguationData":[TD([[makeQuery(id+"F0.imprint","INTERSECT",VERTEX,{"derivedFrom":[subQ0,subQ1,sQuery(id+"F0.wireOp",EDGE,"E18.right")]}),1.0]])],"derivedFrom":subQ0})])]});var subQ5=makeQuery(id+"F1.opExtrude","SWEPT_FACE",FACE,{"disambiguationData":[OSD([subQ0]),TDD([makeQuery(id+"F0.imprint","IMPRINT",EDGE,{"disambiguationData":[TD([[makeQuery(id+"F0.imprint","INTERSECT",VERTEX,{"derivedFrom":[subQ0,sQuery(id+"F0.wireOp",EDGE,"E12")]}),-1.0]])],"derivedFrom":subQ0})])]});Q12=qUnion([makeQuery(id+"F3.boolean.opBoolean","INTERSECT",EDGE,{"derivedFrom":[subQ5,makeQuery(id+"F3.opExtrude","SWEPT_FACE",FACE,{"disambiguationData":[OSD([sQuery(id+"F2.wireOp",EDGE,"E41.0")])]})]}),makeQuery(id+"F3.boolean.opBoolean","INTERSECT",EDGE,{"derivedFrom":[subQ5,makeQuery(id+"F3.opExtrude","SWEPT_FACE",FACE,{"disambiguationData":[OSD([sQuery(id+"F2.wireOp",EDGE,"E41.1")])]})]}),makeQuery(id+"F3.boolean.opBoolean","INTERSECT",EDGE,{"derivedFrom":[subQ5,makeQuery(id+"F3.opExtrude","SWEPT_FACE",FACE,{"disambiguationData":[OSD([sQuery(id+"F2.wireOp",EDGE,"E41.2")])]})]}),makeQuery(id+"F3.boolean.opBoolean","INTERSECT",EDGE,{"derivedFrom":[subQ5,makeQuery(id+"F3.opExtrude","SWEPT_FACE",FACE,{"disambiguationData":[OSD([sQuery(id+"F2.wireOp",EDGE,"E41.3")])]})]}),makeQuery(id+"F3.boolean.opBoolean","INTERSECT",EDGE,{"derivedFrom":[subQ5,makeQuery(id+"F3.opExtrude","SWEPT_FACE",FACE,{"disambiguationData":[OSD([sQuery(id+"F2.wireOp",EDGE,"E41.4")])]})]}),makeQuery(id+"F3.boolean.opBoolean","INTERSECT",EDGE,{"derivedFrom":[subQ5,makeQuery(id+"F3.opExtrude","SWEPT_FACE",FACE,{"disambiguationData":[OSD([sQuery(id+"F2.wireOp",EDGE,"E41.5")])]})]}),makeQuery(id+"F3.boolean.opBoolean","INTERSECT",EDGE,{"derivedFrom":[subQ5,makeQuery(id+"F3.opExtrude","SWEPT_FACE",FACE,{"disambiguationData":[OSD([sQuery(id+"F2.wireOp",EDGE,"E42.0")])]})]}),makeQuery(id+"F3.boolean.opBoolean","INTERSECT",EDGE,{"derivedFrom":[subQ5,makeQuery(id+"F3.opExtrude","SWEPT_FACE",FACE,{"disambiguationData":[OSD([sQuery(id+"F2.wireOp",EDGE,"E42.1")])]})]}),makeQuery(id+"F3.boolean.opBoolean","INTERSECT",EDGE,{"derivedFrom":[subQ5,makeQuery(id+"F3.opExtrude","SWEPT_FACE",FACE,{"disambiguationData":[OSD([sQuery(id+"F2.wireOp",EDGE,"E42.2")])]})]}),makeQuery(id+"F3.boolean.opBoolean","INTERSECT",EDGE,{"derivedFrom":[subQ5,makeQuery(id+"F3.opExtrude","SWEPT_FACE",FACE,{"disambiguationData":[OSD([sQuery(id+"F2.wireOp",EDGE,"E42.3")])]})]}),makeQuery(id+"F3.boolean.opBoolean","INTERSECT",EDGE,{"derivedFrom":[subQ5,makeQuery(id+"F3.opExtrude","SWEPT_FACE",FACE,{"disambiguationData":[OSD([sQuery(id+"F2.wireOp",EDGE,"E42.4")])]})]}),makeQuery(id+"F3.boolean.opBoolean","INTERSECT",EDGE,{"derivedFrom":[subQ5,makeQuery(id+"F3.opExtrude","SWEPT_FACE",FACE,{"disambiguationData":[OSD([sQuery(id+"F2.wireOp",EDGE,"E42.5")])]})]}),makeQuery(id+"F3.boolean.opBoolean","INTERSECT",EDGE,{"derivedFrom":[subQ4,makeQuery(id+"F3.opExtrude","SWEPT_FACE",FACE,{"disambiguationData":[OSD([sQuery(id+"F2.wireOp",EDGE,"E39.0")])]})]}),makeQuery(id+"F3.boolean.opBoolean","INTERSECT",EDGE,{"derivedFrom":[subQ4,makeQuery(id+"F3.opExtrude","SWEPT_FACE",FACE,{"disambiguationData":[OSD([sQuery(id+"F2.wireOp",EDGE,"E39.1")])]})]}),makeQuery(id+"F3.boolean.opBoolean","INTERSECT",EDGE,{"derivedFrom":[subQ4,makeQuery(id+"F3.opExtrude","SWEPT_FACE",FACE,{"disambiguationData":[OSD([sQuery(id+"F2.wireOp",EDGE,"E39.2")])]})]}),makeQuery(id+"F3.boolean.opBoolean","INTERSECT",EDGE,{"derivedFrom":[subQ4,makeQuery(id+"F3.opExtrude","SWEPT_FACE",FACE,{"disambiguationData":[OSD([sQuery(id+"F2.wireOp",EDGE,"E39.3")])]})]}),makeQuery(id+"F3.boolean.opBoolean","INTERSECT",EDGE,{"derivedFrom":[subQ4,makeQuery(id+"F3.opExtrude","SWEPT_FACE",FACE,{"disambiguationData":[OSD([sQuery(id+"F2.wireOp",EDGE,"E39.4")])]})]}),makeQuery(id+"F3.boolean.opBoolean","INTERSECT",EDGE,{"derivedFrom":[subQ4,makeQuery(id+"F3.opExtrude","SWEPT_FACE",FACE,{"disambiguationData":[OSD([sQuery(id+"F2.wireOp",EDGE,"E39.5")])]})]}),makeQuery(id+"F3.boolean.opBoolean","INTERSECT",EDGE,{"derivedFrom":[subQ4,makeQuery(id+"F3.opExtrude","SWEPT_FACE",FACE,{"disambiguationData":[OSD([sQuery(id+"F2.wireOp",EDGE,"E40.0")])]})]}),makeQuery(id+"F3.boolean.opBoolean","INTERSECT",EDGE,{"derivedFrom":[subQ4,makeQuery(id+"F3.opExtrude","SWEPT_FACE",FACE,{"disambiguationData":[OSD([sQuery(id+"F2.wireOp",EDGE,"E40.1")])]})]}),makeQuery(id+"F3.boolean.opBoolean","INTERSECT",EDGE,{"derivedFrom":[subQ4,makeQuery(id+"F3.opExtrude","SWEPT_FACE",FACE,{"disambiguationData":[OSD([sQuery(id+"F2.wireOp",EDGE,"E40.2")])]})]}),makeQuery(id+"F3.boolean.opBoolean","INTERSECT",EDGE,{"derivedFrom":[subQ4,makeQuery(id+"F3.opExtrude","SWEPT_FACE",FACE,{"disambiguationData":[OSD([sQuery(id+"F2.wireOp",EDGE,"E40.3")])]})]}),makeQuery(id+"F3.boolean.opBoolean","INTERSECT",EDGE,{"derivedFrom":[subQ4,makeQuery(id+"F3.opExtrude","SWEPT_FACE",FACE,{"disambiguationData":[OSD([sQuery(id+"F2.wireOp",EDGE,"E40.4")])]})]}),makeQuery(id+"F3.boolean.opBoolean","INTERSECT",EDGE,{"derivedFrom":[subQ4,makeQuery(id+"F3.opExtrude","SWEPT_FACE",FACE,{"disambiguationData":[OSD([sQuery(id+"F2.wireOp",EDGE,"E40.5")])]})]}),makeQuery(id+"F3.boolean.opBoolean","INTERSECT",EDGE,{"derivedFrom":[subQ2,makeQuery(id+"F3.opExtrude","SWEPT_FACE",FACE,{"disambiguationData":[OSD([sQuery(id+"F2.wireOp",EDGE,"E36.0")])]})]}),makeQuery(id+"F3.boolean.opBoolean","INTERSECT",EDGE,{"derivedFrom":[subQ2,makeQuery(id+"F3.opExtrude","SWEPT_FACE",FACE,{"disambiguationData":[OSD([sQuery(id+"F2.wireOp",EDGE,"E36.1")])]})]}),makeQuery(id+"F3.boolean.opBoolean","INTERSECT",EDGE,{"derivedFrom":[subQ2,makeQuery(id+"F3.opExtrude","SWEPT_FACE",FACE,{"disambiguationData":[OSD([sQuery(id+"F2.wireOp",EDGE,"E36.2")])]})]}),makeQuery(id+"F3.boolean.opBoolean","INTERSECT",EDGE,{"derivedFrom":[subQ2,makeQuery(id+"F3.opExtrude","SWEPT_FACE",FACE,{"disambiguationData":[OSD([sQuery(id+"F2.wireOp",EDGE,"E36.3")])]})]}),makeQuery(id+"F3.boolean.opBoolean","INTERSECT",EDGE,{"derivedFrom":[subQ2,makeQuery(id+"F3.opExtrude","SWEPT_FACE",FACE,{"disambiguationData":[OSD([sQuery(id+"F2.wireOp",EDGE,"E36.4")])]})]}),makeQuery(id+"F3.boolean.opBoolean","INTERSECT",EDGE,{"derivedFrom":[subQ2,makeQuery(id+"F3.opExtrude","SWEPT_FACE",FACE,{"disambiguationData":[OSD([sQuery(id+"F2.wireOp",EDGE,"E36.5")])]})]}),makeQuery(id+"F3.boolean.opBoolean","INTERSECT",EDGE,{"derivedFrom":[subQ2,makeQuery(id+"F3.opExtrude","SWEPT_FACE",FACE,{"disambiguationData":[OSD([sQuery(id+"F2.wireOp",EDGE,"E37.0")])]})]}),makeQuery(id+"F3.boolean.opBoolean","INTERSECT",EDGE,{"derivedFrom":[subQ2,makeQuery(id+"F3.opExtrude","SWEPT_FACE",FACE,{"disambiguationData":[OSD([sQuery(id+"F2.wireOp",EDGE,"E37.1")])]})]}),makeQuery(id+"F3.boolean.opBoolean","INTERSECT",EDGE,{"derivedFrom":[subQ2,makeQuery(id+"F3.opExtrude","SWEPT_FACE",FACE,{"disambiguationData":[OSD([sQuery(id+"F2.wireOp",EDGE,"E37.2")])]})]}),makeQuery(id+"F3.boolean.opBoolean","INTERSECT",EDGE,{"derivedFrom":[subQ2,makeQuery(id+"F3.opExtrude","SWEPT_FACE",FACE,{"disambiguationData":[OSD([sQuery(id+"F2.wireOp",EDGE,"E37.3")])]})]}),makeQuery(id+"F3.boolean.opBoolean","INTERSECT",EDGE,{"derivedFrom":[subQ2,makeQuery(id+"F3.opExtrude","SWEPT_FACE",FACE,{"disambiguationData":[OSD([sQuery(id+"F2.wireOp",EDGE,"E37.4")])]})]}),makeQuery(id+"F3.boolean.opBoolean","INTERSECT",EDGE,{"derivedFrom":[subQ2,makeQuery(id+"F3.opExtrude","SWEPT_FACE",FACE,{"disambiguationData":[OSD([sQuery(id+"F2.wireOp",EDGE,"E37.5")])]})]}),makeQuery(id+"F3.boolean.opBoolean","INTERSECT",EDGE,{"derivedFrom":[subQ2,makeQuery(id+"F3.opExtrude","SWEPT_FACE",FACE,{"disambiguationData":[OSD([sQuery(id+"F2.wireOp",EDGE,"E38.0")])]})]}),makeQuery(id+"F3.boolean.opBoolean","INTERSECT",EDGE,{"derivedFrom":[subQ2,makeQuery(id+"F3.opExtrude","SWEPT_FACE",FACE,{"disambiguationData":[OSD([sQuery(id+"F2.wireOp",EDGE,"E38.1")])]})]}),makeQuery(id+"F3.boolean.opBoolean","INTERSECT",EDGE,{"derivedFrom":[subQ2,makeQuery(id+"F3.opExtrude","SWEPT_FACE",FACE,{"disambiguationData":[OSD([sQuery(id+"F2.wireOp",EDGE,"E38.2")])]})]}),makeQuery(id+"F3.boolean.opBoolean","INTERSECT",EDGE,{"derivedFrom":[subQ2,makeQuery(id+"F3.opExtrude","SWEPT_FACE",FACE,{"disambiguationData":[OSD([sQuery(id+"F2.wireOp",EDGE,"E38.3")])]})]}),makeQuery(id+"F3.boolean.opBoolean","INTERSECT",EDGE,{"derivedFrom":[subQ2,makeQuery(id+"F3.opExtrude","SWEPT_FACE",FACE,{"disambiguationData":[OSD([sQuery(id+"F2.wireOp",EDGE,"E38.4")])]})]}),makeQuery(id+"F3.boolean.opBoolean","INTERSECT",EDGE,{"derivedFrom":[subQ2,makeQuery(id+"F3.opExtrude","SWEPT_FACE",FACE,{"disambiguationData":[OSD([sQuery(id+"F2.wireOp",EDGE,"E38.5")])]})]})]);}
            var Q13;
            {var subQ0=sQuery(id+"F0.wireOp",EDGE,"E6");var subQ1=sQuery(id+"F0.wireOp",EDGE,"E18.top");var subQ2=makeQuery(id+"F1.opExtrude","SWEPT_FACE",FACE,{"disambiguationData":[OSD([subQ0]),TDD([makeQuery(id+"F0.imprint","IMPRINT",EDGE,{"disambiguationData":[TD([[makeQuery(id+"F0.imprint","INTERSECT",VERTEX,{"derivedFrom":[subQ0,sQuery(id+"F0.wireOp",EDGE,"E9")]}),1.0]])],"derivedFrom":subQ0})])]});var subQ4=makeQuery(id+"F1.opExtrude","SWEPT_FACE",FACE,{"disambiguationData":[OSD([subQ0]),TDD([makeQuery(id+"F0.imprint","IMPRINT",EDGE,{"disambiguationData":[TD([[makeQuery(id+"F0.imprint","INTERSECT",VERTEX,{"derivedFrom":[subQ0,subQ1,sQuery(id+"F0.wireOp",EDGE,"E18.right")]}),1.0]])],"derivedFrom":subQ0})])]});var subQ5=makeQuery(id+"F1.opExtrude","SWEPT_FACE",FACE,{"disambiguationData":[OSD([subQ0]),TDD([makeQuery(id+"F0.imprint","IMPRINT",EDGE,{"disambiguationData":[TD([[makeQuery(id+"F0.imprint","INTERSECT",VERTEX,{"derivedFrom":[subQ0,sQuery(id+"F0.wireOp",EDGE,"E12")]}),-1.0]])],"derivedFrom":subQ0})])]});Q13=qUnion([makeQuery(id+"F3.boolean.opBoolean","INTERSECT",EDGE,{"derivedFrom":[subQ5,makeQuery(id+"F3.opExtrude","SWEPT_FACE",FACE,{"disambiguationData":[OSD([sQuery(id+"F2.wireOp",EDGE,"E41.0")])]})]}),makeQuery(id+"F3.boolean.opBoolean","INTERSECT",EDGE,{"derivedFrom":[subQ5,makeQuery(id+"F3.opExtrude","SWEPT_FACE",FACE,{"disambiguationData":[OSD([sQuery(id+"F2.wireOp",EDGE,"E41.1")])]})]}),makeQuery(id+"F3.boolean.opBoolean","INTERSECT",EDGE,{"derivedFrom":[subQ5,makeQuery(id+"F3.opExtrude","SWEPT_FACE",FACE,{"disambiguationData":[OSD([sQuery(id+"F2.wireOp",EDGE,"E41.2")])]})]}),makeQuery(id+"F3.boolean.opBoolean","INTERSECT",EDGE,{"derivedFrom":[subQ5,makeQuery(id+"F3.opExtrude","SWEPT_FACE",FACE,{"disambiguationData":[OSD([sQuery(id+"F2.wireOp",EDGE,"E41.3")])]})]}),makeQuery(id+"F3.boolean.opBoolean","INTERSECT",EDGE,{"derivedFrom":[subQ5,makeQuery(id+"F3.opExtrude","SWEPT_FACE",FACE,{"disambiguationData":[OSD([sQuery(id+"F2.wireOp",EDGE,"E41.4")])]})]}),makeQuery(id+"F3.boolean.opBoolean","INTERSECT",EDGE,{"derivedFrom":[subQ5,makeQuery(id+"F3.opExtrude","SWEPT_FACE",FACE,{"disambiguationData":[OSD([sQuery(id+"F2.wireOp",EDGE,"E41.5")])]})]}),makeQuery(id+"F3.boolean.opBoolean","INTERSECT",EDGE,{"derivedFrom":[subQ5,makeQuery(id+"F3.opExtrude","SWEPT_FACE",FACE,{"disambiguationData":[OSD([sQuery(id+"F2.wireOp",EDGE,"E42.0")])]})]}),makeQuery(id+"F3.boolean.opBoolean","INTERSECT",EDGE,{"derivedFrom":[subQ5,makeQuery(id+"F3.opExtrude","SWEPT_FACE",FACE,{"disambiguationData":[OSD([sQuery(id+"F2.wireOp",EDGE,"E42.1")])]})]}),makeQuery(id+"F3.boolean.opBoolean","INTERSECT",EDGE,{"derivedFrom":[subQ5,makeQuery(id+"F3.opExtrude","SWEPT_FACE",FACE,{"disambiguationData":[OSD([sQuery(id+"F2.wireOp",EDGE,"E42.2")])]})]}),makeQuery(id+"F3.boolean.opBoolean","INTERSECT",EDGE,{"derivedFrom":[subQ5,makeQuery(id+"F3.opExtrude","SWEPT_FACE",FACE,{"disambiguationData":[OSD([sQuery(id+"F2.wireOp",EDGE,"E42.3")])]})]}),makeQuery(id+"F3.boolean.opBoolean","INTERSECT",EDGE,{"derivedFrom":[subQ5,makeQuery(id+"F3.opExtrude","SWEPT_FACE",FACE,{"disambiguationData":[OSD([sQuery(id+"F2.wireOp",EDGE,"E42.4")])]})]}),makeQuery(id+"F3.boolean.opBoolean","INTERSECT",EDGE,{"derivedFrom":[subQ5,makeQuery(id+"F3.opExtrude","SWEPT_FACE",FACE,{"disambiguationData":[OSD([sQuery(id+"F2.wireOp",EDGE,"E42.5")])]})]}),makeQuery(id+"F3.boolean.opBoolean","INTERSECT",EDGE,{"derivedFrom":[subQ4,makeQuery(id+"F3.opExtrude","SWEPT_FACE",FACE,{"disambiguationData":[OSD([sQuery(id+"F2.wireOp",EDGE,"E39.0")])]})]}),makeQuery(id+"F3.boolean.opBoolean","INTERSECT",EDGE,{"derivedFrom":[subQ4,makeQuery(id+"F3.opExtrude","SWEPT_FACE",FACE,{"disambiguationData":[OSD([sQuery(id+"F2.wireOp",EDGE,"E39.1")])]})]}),makeQuery(id+"F3.boolean.opBoolean","INTERSECT",EDGE,{"derivedFrom":[subQ4,makeQuery(id+"F3.opExtrude","SWEPT_FACE",FACE,{"disambiguationData":[OSD([sQuery(id+"F2.wireOp",EDGE,"E39.2")])]})]}),makeQuery(id+"F3.boolean.opBoolean","INTERSECT",EDGE,{"derivedFrom":[subQ4,makeQuery(id+"F3.opExtrude","SWEPT_FACE",FACE,{"disambiguationData":[OSD([sQuery(id+"F2.wireOp",EDGE,"E39.3")])]})]}),makeQuery(id+"F3.boolean.opBoolean","INTERSECT",EDGE,{"derivedFrom":[subQ4,makeQuery(id+"F3.opExtrude","SWEPT_FACE",FACE,{"disambiguationData":[OSD([sQuery(id+"F2.wireOp",EDGE,"E39.4")])]})]}),makeQuery(id+"F3.boolean.opBoolean","INTERSECT",EDGE,{"derivedFrom":[subQ4,makeQuery(id+"F3.opExtrude","SWEPT_FACE",FACE,{"disambiguationData":[OSD([sQuery(id+"F2.wireOp",EDGE,"E39.5")])]})]}),makeQuery(id+"F3.boolean.opBoolean","INTERSECT",EDGE,{"derivedFrom":[subQ4,makeQuery(id+"F3.opExtrude","SWEPT_FACE",FACE,{"disambiguationData":[OSD([sQuery(id+"F2.wireOp",EDGE,"E40.0")])]})]}),makeQuery(id+"F3.boolean.opBoolean","INTERSECT",EDGE,{"derivedFrom":[subQ4,makeQuery(id+"F3.opExtrude","SWEPT_FACE",FACE,{"disambiguationData":[OSD([sQuery(id+"F2.wireOp",EDGE,"E40.1")])]})]}),makeQuery(id+"F3.boolean.opBoolean","INTERSECT",EDGE,{"derivedFrom":[subQ4,makeQuery(id+"F3.opExtrude","SWEPT_FACE",FACE,{"disambiguationData":[OSD([sQuery(id+"F2.wireOp",EDGE,"E40.2")])]})]}),makeQuery(id+"F3.boolean.opBoolean","INTERSECT",EDGE,{"derivedFrom":[subQ4,makeQuery(id+"F3.opExtrude","SWEPT_FACE",FACE,{"disambiguationData":[OSD([sQuery(id+"F2.wireOp",EDGE,"E40.3")])]})]}),makeQuery(id+"F3.boolean.opBoolean","INTERSECT",EDGE,{"derivedFrom":[subQ4,makeQuery(id+"F3.opExtrude","SWEPT_FACE",FACE,{"disambiguationData":[OSD([sQuery(id+"F2.wireOp",EDGE,"E40.4")])]})]}),makeQuery(id+"F3.boolean.opBoolean","INTERSECT",EDGE,{"derivedFrom":[subQ4,makeQuery(id+"F3.opExtrude","SWEPT_FACE",FACE,{"disambiguationData":[OSD([sQuery(id+"F2.wireOp",EDGE,"E40.5")])]})]}),makeQuery(id+"F3.boolean.opBoolean","INTERSECT",EDGE,{"derivedFrom":[subQ2,makeQuery(id+"F3.opExtrude","SWEPT_FACE",FACE,{"disambiguationData":[OSD([sQuery(id+"F2.wireOp",EDGE,"E36.0")])]})]}),makeQuery(id+"F3.boolean.opBoolean","INTERSECT",EDGE,{"derivedFrom":[subQ2,makeQuery(id+"F3.opExtrude","SWEPT_FACE",FACE,{"disambiguationData":[OSD([sQuery(id+"F2.wireOp",EDGE,"E36.1")])]})]}),makeQuery(id+"F3.boolean.opBoolean","INTERSECT",EDGE,{"derivedFrom":[subQ2,makeQuery(id+"F3.opExtrude","SWEPT_FACE",FACE,{"disambiguationData":[OSD([sQuery(id+"F2.wireOp",EDGE,"E36.2")])]})]}),makeQuery(id+"F3.boolean.opBoolean","INTERSECT",EDGE,{"derivedFrom":[subQ2,makeQuery(id+"F3.opExtrude","SWEPT_FACE",FACE,{"disambiguationData":[OSD([sQuery(id+"F2.wireOp",EDGE,"E36.3")])]})]}),makeQuery(id+"F3.boolean.opBoolean","INTERSECT",EDGE,{"derivedFrom":[subQ2,makeQuery(id+"F3.opExtrude","SWEPT_FACE",FACE,{"disambiguationData":[OSD([sQuery(id+"F2.wireOp",EDGE,"E36.4")])]})]}),makeQuery(id+"F3.boolean.opBoolean","INTERSECT",EDGE,{"derivedFrom":[subQ2,makeQuery(id+"F3.opExtrude","SWEPT_FACE",FACE,{"disambiguationData":[OSD([sQuery(id+"F2.wireOp",EDGE,"E36.5")])]})]}),makeQuery(id+"F3.boolean.opBoolean","INTERSECT",EDGE,{"derivedFrom":[subQ2,makeQuery(id+"F3.opExtrude","SWEPT_FACE",FACE,{"disambiguationData":[OSD([sQuery(id+"F2.wireOp",EDGE,"E37.0")])]})]}),makeQuery(id+"F3.boolean.opBoolean","INTERSECT",EDGE,{"derivedFrom":[subQ2,makeQuery(id+"F3.opExtrude","SWEPT_FACE",FACE,{"disambiguationData":[OSD([sQuery(id+"F2.wireOp",EDGE,"E37.1")])]})]}),makeQuery(id+"F3.boolean.opBoolean","INTERSECT",EDGE,{"derivedFrom":[subQ2,makeQuery(id+"F3.opExtrude","SWEPT_FACE",FACE,{"disambiguationData":[OSD([sQuery(id+"F2.wireOp",EDGE,"E37.2")])]})]}),makeQuery(id+"F3.boolean.opBoolean","INTERSECT",EDGE,{"derivedFrom":[subQ2,makeQuery(id+"F3.opExtrude","SWEPT_FACE",FACE,{"disambiguationData":[OSD([sQuery(id+"F2.wireOp",EDGE,"E37.3")])]})]}),makeQuery(id+"F3.boolean.opBoolean","INTERSECT",EDGE,{"derivedFrom":[subQ2,makeQuery(id+"F3.opExtrude","SWEPT_FACE",FACE,{"disambiguationData":[OSD([sQuery(id+"F2.wireOp",EDGE,"E37.4")])]})]}),makeQuery(id+"F3.boolean.opBoolean","INTERSECT",EDGE,{"derivedFrom":[subQ2,makeQuery(id+"F3.opExtrude","SWEPT_FACE",FACE,{"disambiguationData":[OSD([sQuery(id+"F2.wireOp",EDGE,"E37.5")])]})]}),makeQuery(id+"F3.boolean.opBoolean","INTERSECT",EDGE,{"derivedFrom":[subQ2,makeQuery(id+"F3.opExtrude","SWEPT_FACE",FACE,{"disambiguationData":[OSD([sQuery(id+"F2.wireOp",EDGE,"E38.0")])]})]}),makeQuery(id+"F3.boolean.opBoolean","INTERSECT",EDGE,{"derivedFrom":[subQ2,makeQuery(id+"F3.opExtrude","SWEPT_FACE",FACE,{"disambiguationData":[OSD([sQuery(id+"F2.wireOp",EDGE,"E38.1")])]})]}),makeQuery(id+"F3.boolean.opBoolean","INTERSECT",EDGE,{"derivedFrom":[subQ2,makeQuery(id+"F3.opExtrude","SWEPT_FACE",FACE,{"disambiguationData":[OSD([sQuery(id+"F2.wireOp",EDGE,"E38.2")])]})]}),makeQuery(id+"F3.boolean.opBoolean","INTERSECT",EDGE,{"derivedFrom":[subQ2,makeQuery(id+"F3.opExtrude","SWEPT_FACE",FACE,{"disambiguationData":[OSD([sQuery(id+"F2.wireOp",EDGE,"E38.3")])]})]}),makeQuery(id+"F3.boolean.opBoolean","INTERSECT",EDGE,{"derivedFrom":[subQ2,makeQuery(id+"F3.opExtrude","SWEPT_FACE",FACE,{"disambiguationData":[OSD([sQuery(id+"F2.wireOp",EDGE,"E38.4")])]})]}),makeQuery(id+"F3.boolean.opBoolean","INTERSECT",EDGE,{"derivedFrom":[subQ2,makeQuery(id+"F3.opExtrude","SWEPT_FACE",FACE,{"disambiguationData":[OSD([sQuery(id+"F2.wireOp",EDGE,"E38.5")])]})]})]);}
            var Q14;
            {var subQ0=sQuery(id+"F0.wireOp",EDGE,"E6");var subQ1=sQuery(id+"F0.wireOp",EDGE,"E18.top");var subQ2=makeQuery(id+"F1.opExtrude","SWEPT_FACE",FACE,{"disambiguationData":[OSD([subQ0]),TDD([makeQuery(id+"F0.imprint","IMPRINT",EDGE,{"disambiguationData":[TD([[makeQuery(id+"F0.imprint","INTERSECT",VERTEX,{"derivedFrom":[subQ0,sQuery(id+"F0.wireOp",EDGE,"E9")]}),1.0]])],"derivedFrom":subQ0})])]});var subQ4=makeQuery(id+"F1.opExtrude","SWEPT_FACE",FACE,{"disambiguationData":[OSD([subQ0]),TDD([makeQuery(id+"F0.imprint","IMPRINT",EDGE,{"disambiguationData":[TD([[makeQuery(id+"F0.imprint","INTERSECT",VERTEX,{"derivedFrom":[subQ0,subQ1,sQuery(id+"F0.wireOp",EDGE,"E18.right")]}),1.0]])],"derivedFrom":subQ0})])]});var subQ5=makeQuery(id+"F1.opExtrude","SWEPT_FACE",FACE,{"disambiguationData":[OSD([subQ0]),TDD([makeQuery(id+"F0.imprint","IMPRINT",EDGE,{"disambiguationData":[TD([[makeQuery(id+"F0.imprint","INTERSECT",VERTEX,{"derivedFrom":[subQ0,sQuery(id+"F0.wireOp",EDGE,"E12")]}),-1.0]])],"derivedFrom":subQ0})])]});Q14=qUnion([makeQuery(id+"F3.boolean.opBoolean","INTERSECT",EDGE,{"derivedFrom":[subQ5,makeQuery(id+"F3.opExtrude","SWEPT_FACE",FACE,{"disambiguationData":[OSD([sQuery(id+"F2.wireOp",EDGE,"E41.0")])]})]}),makeQuery(id+"F3.boolean.opBoolean","INTERSECT",EDGE,{"derivedFrom":[subQ5,makeQuery(id+"F3.opExtrude","SWEPT_FACE",FACE,{"disambiguationData":[OSD([sQuery(id+"F2.wireOp",EDGE,"E41.1")])]})]}),makeQuery(id+"F3.boolean.opBoolean","INTERSECT",EDGE,{"derivedFrom":[subQ5,makeQuery(id+"F3.opExtrude","SWEPT_FACE",FACE,{"disambiguationData":[OSD([sQuery(id+"F2.wireOp",EDGE,"E41.2")])]})]}),makeQuery(id+"F3.boolean.opBoolean","INTERSECT",EDGE,{"derivedFrom":[subQ5,makeQuery(id+"F3.opExtrude","SWEPT_FACE",FACE,{"disambiguationData":[OSD([sQuery(id+"F2.wireOp",EDGE,"E41.3")])]})]}),makeQuery(id+"F3.boolean.opBoolean","INTERSECT",EDGE,{"derivedFrom":[subQ5,makeQuery(id+"F3.opExtrude","SWEPT_FACE",FACE,{"disambiguationData":[OSD([sQuery(id+"F2.wireOp",EDGE,"E41.4")])]})]}),makeQuery(id+"F3.boolean.opBoolean","INTERSECT",EDGE,{"derivedFrom":[subQ5,makeQuery(id+"F3.opExtrude","SWEPT_FACE",FACE,{"disambiguationData":[OSD([sQuery(id+"F2.wireOp",EDGE,"E41.5")])]})]}),makeQuery(id+"F3.boolean.opBoolean","INTERSECT",EDGE,{"derivedFrom":[subQ5,makeQuery(id+"F3.opExtrude","SWEPT_FACE",FACE,{"disambiguationData":[OSD([sQuery(id+"F2.wireOp",EDGE,"E42.0")])]})]}),makeQuery(id+"F3.boolean.opBoolean","INTERSECT",EDGE,{"derivedFrom":[subQ5,makeQuery(id+"F3.opExtrude","SWEPT_FACE",FACE,{"disambiguationData":[OSD([sQuery(id+"F2.wireOp",EDGE,"E42.1")])]})]}),makeQuery(id+"F3.boolean.opBoolean","INTERSECT",EDGE,{"derivedFrom":[subQ5,makeQuery(id+"F3.opExtrude","SWEPT_FACE",FACE,{"disambiguationData":[OSD([sQuery(id+"F2.wireOp",EDGE,"E42.2")])]})]}),makeQuery(id+"F3.boolean.opBoolean","INTERSECT",EDGE,{"derivedFrom":[subQ5,makeQuery(id+"F3.opExtrude","SWEPT_FACE",FACE,{"disambiguationData":[OSD([sQuery(id+"F2.wireOp",EDGE,"E42.3")])]})]}),makeQuery(id+"F3.boolean.opBoolean","INTERSECT",EDGE,{"derivedFrom":[subQ5,makeQuery(id+"F3.opExtrude","SWEPT_FACE",FACE,{"disambiguationData":[OSD([sQuery(id+"F2.wireOp",EDGE,"E42.4")])]})]}),makeQuery(id+"F3.boolean.opBoolean","INTERSECT",EDGE,{"derivedFrom":[subQ5,makeQuery(id+"F3.opExtrude","SWEPT_FACE",FACE,{"disambiguationData":[OSD([sQuery(id+"F2.wireOp",EDGE,"E42.5")])]})]}),makeQuery(id+"F3.boolean.opBoolean","INTERSECT",EDGE,{"derivedFrom":[subQ4,makeQuery(id+"F3.opExtrude","SWEPT_FACE",FACE,{"disambiguationData":[OSD([sQuery(id+"F2.wireOp",EDGE,"E39.0")])]})]}),makeQuery(id+"F3.boolean.opBoolean","INTERSECT",EDGE,{"derivedFrom":[subQ4,makeQuery(id+"F3.opExtrude","SWEPT_FACE",FACE,{"disambiguationData":[OSD([sQuery(id+"F2.wireOp",EDGE,"E39.1")])]})]}),makeQuery(id+"F3.boolean.opBoolean","INTERSECT",EDGE,{"derivedFrom":[subQ4,makeQuery(id+"F3.opExtrude","SWEPT_FACE",FACE,{"disambiguationData":[OSD([sQuery(id+"F2.wireOp",EDGE,"E39.2")])]})]}),makeQuery(id+"F3.boolean.opBoolean","INTERSECT",EDGE,{"derivedFrom":[subQ4,makeQuery(id+"F3.opExtrude","SWEPT_FACE",FACE,{"disambiguationData":[OSD([sQuery(id+"F2.wireOp",EDGE,"E39.3")])]})]}),makeQuery(id+"F3.boolean.opBoolean","INTERSECT",EDGE,{"derivedFrom":[subQ4,makeQuery(id+"F3.opExtrude","SWEPT_FACE",FACE,{"disambiguationData":[OSD([sQuery(id+"F2.wireOp",EDGE,"E39.4")])]})]}),makeQuery(id+"F3.boolean.opBoolean","INTERSECT",EDGE,{"derivedFrom":[subQ4,makeQuery(id+"F3.opExtrude","SWEPT_FACE",FACE,{"disambiguationData":[OSD([sQuery(id+"F2.wireOp",EDGE,"E39.5")])]})]}),makeQuery(id+"F3.boolean.opBoolean","INTERSECT",EDGE,{"derivedFrom":[subQ4,makeQuery(id+"F3.opExtrude","SWEPT_FACE",FACE,{"disambiguationData":[OSD([sQuery(id+"F2.wireOp",EDGE,"E40.0")])]})]}),makeQuery(id+"F3.boolean.opBoolean","INTERSECT",EDGE,{"derivedFrom":[subQ4,makeQuery(id+"F3.opExtrude","SWEPT_FACE",FACE,{"disambiguationData":[OSD([sQuery(id+"F2.wireOp",EDGE,"E40.1")])]})]}),makeQuery(id+"F3.boolean.opBoolean","INTERSECT",EDGE,{"derivedFrom":[subQ4,makeQuery(id+"F3.opExtrude","SWEPT_FACE",FACE,{"disambiguationData":[OSD([sQuery(id+"F2.wireOp",EDGE,"E40.2")])]})]}),makeQuery(id+"F3.boolean.opBoolean","INTERSECT",EDGE,{"derivedFrom":[subQ4,makeQuery(id+"F3.opExtrude","SWEPT_FACE",FACE,{"disambiguationData":[OSD([sQuery(id+"F2.wireOp",EDGE,"E40.3")])]})]}),makeQuery(id+"F3.boolean.opBoolean","INTERSECT",EDGE,{"derivedFrom":[subQ4,makeQuery(id+"F3.opExtrude","SWEPT_FACE",FACE,{"disambiguationData":[OSD([sQuery(id+"F2.wireOp",EDGE,"E40.4")])]})]}),makeQuery(id+"F3.boolean.opBoolean","INTERSECT",EDGE,{"derivedFrom":[subQ4,makeQuery(id+"F3.opExtrude","SWEPT_FACE",FACE,{"disambiguationData":[OSD([sQuery(id+"F2.wireOp",EDGE,"E40.5")])]})]}),makeQuery(id+"F3.boolean.opBoolean","INTERSECT",EDGE,{"derivedFrom":[subQ2,makeQuery(id+"F3.opExtrude","SWEPT_FACE",FACE,{"disambiguationData":[OSD([sQuery(id+"F2.wireOp",EDGE,"E36.0")])]})]}),makeQuery(id+"F3.boolean.opBoolean","INTERSECT",EDGE,{"derivedFrom":[subQ2,makeQuery(id+"F3.opExtrude","SWEPT_FACE",FACE,{"disambiguationData":[OSD([sQuery(id+"F2.wireOp",EDGE,"E36.1")])]})]}),makeQuery(id+"F3.boolean.opBoolean","INTERSECT",EDGE,{"derivedFrom":[subQ2,makeQuery(id+"F3.opExtrude","SWEPT_FACE",FACE,{"disambiguationData":[OSD([sQuery(id+"F2.wireOp",EDGE,"E36.2")])]})]}),makeQuery(id+"F3.boolean.opBoolean","INTERSECT",EDGE,{"derivedFrom":[subQ2,makeQuery(id+"F3.opExtrude","SWEPT_FACE",FACE,{"disambiguationData":[OSD([sQuery(id+"F2.wireOp",EDGE,"E36.3")])]})]}),makeQuery(id+"F3.boolean.opBoolean","INTERSECT",EDGE,{"derivedFrom":[subQ2,makeQuery(id+"F3.opExtrude","SWEPT_FACE",FACE,{"disambiguationData":[OSD([sQuery(id+"F2.wireOp",EDGE,"E36.4")])]})]}),makeQuery(id+"F3.boolean.opBoolean","INTERSECT",EDGE,{"derivedFrom":[subQ2,makeQuery(id+"F3.opExtrude","SWEPT_FACE",FACE,{"disambiguationData":[OSD([sQuery(id+"F2.wireOp",EDGE,"E36.5")])]})]}),makeQuery(id+"F3.boolean.opBoolean","INTERSECT",EDGE,{"derivedFrom":[subQ2,makeQuery(id+"F3.opExtrude","SWEPT_FACE",FACE,{"disambiguationData":[OSD([sQuery(id+"F2.wireOp",EDGE,"E37.0")])]})]}),makeQuery(id+"F3.boolean.opBoolean","INTERSECT",EDGE,{"derivedFrom":[subQ2,makeQuery(id+"F3.opExtrude","SWEPT_FACE",FACE,{"disambiguationData":[OSD([sQuery(id+"F2.wireOp",EDGE,"E37.1")])]})]}),makeQuery(id+"F3.boolean.opBoolean","INTERSECT",EDGE,{"derivedFrom":[subQ2,makeQuery(id+"F3.opExtrude","SWEPT_FACE",FACE,{"disambiguationData":[OSD([sQuery(id+"F2.wireOp",EDGE,"E37.2")])]})]}),makeQuery(id+"F3.boolean.opBoolean","INTERSECT",EDGE,{"derivedFrom":[subQ2,makeQuery(id+"F3.opExtrude","SWEPT_FACE",FACE,{"disambiguationData":[OSD([sQuery(id+"F2.wireOp",EDGE,"E37.3")])]})]}),makeQuery(id+"F3.boolean.opBoolean","INTERSECT",EDGE,{"derivedFrom":[subQ2,makeQuery(id+"F3.opExtrude","SWEPT_FACE",FACE,{"disambiguationData":[OSD([sQuery(id+"F2.wireOp",EDGE,"E37.4")])]})]}),makeQuery(id+"F3.boolean.opBoolean","INTERSECT",EDGE,{"derivedFrom":[subQ2,makeQuery(id+"F3.opExtrude","SWEPT_FACE",FACE,{"disambiguationData":[OSD([sQuery(id+"F2.wireOp",EDGE,"E37.5")])]})]}),makeQuery(id+"F3.boolean.opBoolean","INTERSECT",EDGE,{"derivedFrom":[subQ2,makeQuery(id+"F3.opExtrude","SWEPT_FACE",FACE,{"disambiguationData":[OSD([sQuery(id+"F2.wireOp",EDGE,"E38.0")])]})]}),makeQuery(id+"F3.boolean.opBoolean","INTERSECT",EDGE,{"derivedFrom":[subQ2,makeQuery(id+"F3.opExtrude","SWEPT_FACE",FACE,{"disambiguationData":[OSD([sQuery(id+"F2.wireOp",EDGE,"E38.1")])]})]}),makeQuery(id+"F3.boolean.opBoolean","INTERSECT",EDGE,{"derivedFrom":[subQ2,makeQuery(id+"F3.opExtrude","SWEPT_FACE",FACE,{"disambiguationData":[OSD([sQuery(id+"F2.wireOp",EDGE,"E38.2")])]})]}),makeQuery(id+"F3.boolean.opBoolean","INTERSECT",EDGE,{"derivedFrom":[subQ2,makeQuery(id+"F3.opExtrude","SWEPT_FACE",FACE,{"disambiguationData":[OSD([sQuery(id+"F2.wireOp",EDGE,"E38.3")])]})]}),makeQuery(id+"F3.boolean.opBoolean","INTERSECT",EDGE,{"derivedFrom":[subQ2,makeQuery(id+"F3.opExtrude","SWEPT_FACE",FACE,{"disambiguationData":[OSD([sQuery(id+"F2.wireOp",EDGE,"E38.4")])]})]}),makeQuery(id+"F3.boolean.opBoolean","INTERSECT",EDGE,{"derivedFrom":[subQ2,makeQuery(id+"F3.opExtrude","SWEPT_FACE",FACE,{"disambiguationData":[OSD([sQuery(id+"F2.wireOp",EDGE,"E38.5")])]})]})]);}
            var Q15;
            {var subQ0=sQuery(id+"F0.wireOp",EDGE,"E6");var subQ1=sQuery(id+"F0.wireOp",EDGE,"E18.top");var subQ2=makeQuery(id+"F1.opExtrude","SWEPT_FACE",FACE,{"disambiguationData":[OSD([subQ0]),TDD([makeQuery(id+"F0.imprint","IMPRINT",EDGE,{"disambiguationData":[TD([[makeQuery(id+"F0.imprint","INTERSECT",VERTEX,{"derivedFrom":[subQ0,sQuery(id+"F0.wireOp",EDGE,"E9")]}),1.0]])],"derivedFrom":subQ0})])]});var subQ4=makeQuery(id+"F1.opExtrude","SWEPT_FACE",FACE,{"disambiguationData":[OSD([subQ0]),TDD([makeQuery(id+"F0.imprint","IMPRINT",EDGE,{"disambiguationData":[TD([[makeQuery(id+"F0.imprint","INTERSECT",VERTEX,{"derivedFrom":[subQ0,subQ1,sQuery(id+"F0.wireOp",EDGE,"E18.right")]}),1.0]])],"derivedFrom":subQ0})])]});var subQ5=makeQuery(id+"F1.opExtrude","SWEPT_FACE",FACE,{"disambiguationData":[OSD([subQ0]),TDD([makeQuery(id+"F0.imprint","IMPRINT",EDGE,{"disambiguationData":[TD([[makeQuery(id+"F0.imprint","INTERSECT",VERTEX,{"derivedFrom":[subQ0,sQuery(id+"F0.wireOp",EDGE,"E12")]}),-1.0]])],"derivedFrom":subQ0})])]});Q15=qUnion([makeQuery(id+"F3.boolean.opBoolean","INTERSECT",EDGE,{"derivedFrom":[subQ5,makeQuery(id+"F3.opExtrude","SWEPT_FACE",FACE,{"disambiguationData":[OSD([sQuery(id+"F2.wireOp",EDGE,"E41.0")])]})]}),makeQuery(id+"F3.boolean.opBoolean","INTERSECT",EDGE,{"derivedFrom":[subQ5,makeQuery(id+"F3.opExtrude","SWEPT_FACE",FACE,{"disambiguationData":[OSD([sQuery(id+"F2.wireOp",EDGE,"E41.1")])]})]}),makeQuery(id+"F3.boolean.opBoolean","INTERSECT",EDGE,{"derivedFrom":[subQ5,makeQuery(id+"F3.opExtrude","SWEPT_FACE",FACE,{"disambiguationData":[OSD([sQuery(id+"F2.wireOp",EDGE,"E41.2")])]})]}),makeQuery(id+"F3.boolean.opBoolean","INTERSECT",EDGE,{"derivedFrom":[subQ5,makeQuery(id+"F3.opExtrude","SWEPT_FACE",FACE,{"disambiguationData":[OSD([sQuery(id+"F2.wireOp",EDGE,"E41.3")])]})]}),makeQuery(id+"F3.boolean.opBoolean","INTERSECT",EDGE,{"derivedFrom":[subQ5,makeQuery(id+"F3.opExtrude","SWEPT_FACE",FACE,{"disambiguationData":[OSD([sQuery(id+"F2.wireOp",EDGE,"E41.4")])]})]}),makeQuery(id+"F3.boolean.opBoolean","INTERSECT",EDGE,{"derivedFrom":[subQ5,makeQuery(id+"F3.opExtrude","SWEPT_FACE",FACE,{"disambiguationData":[OSD([sQuery(id+"F2.wireOp",EDGE,"E41.5")])]})]}),makeQuery(id+"F3.boolean.opBoolean","INTERSECT",EDGE,{"derivedFrom":[subQ5,makeQuery(id+"F3.opExtrude","SWEPT_FACE",FACE,{"disambiguationData":[OSD([sQuery(id+"F2.wireOp",EDGE,"E42.0")])]})]}),makeQuery(id+"F3.boolean.opBoolean","INTERSECT",EDGE,{"derivedFrom":[subQ5,makeQuery(id+"F3.opExtrude","SWEPT_FACE",FACE,{"disambiguationData":[OSD([sQuery(id+"F2.wireOp",EDGE,"E42.1")])]})]}),makeQuery(id+"F3.boolean.opBoolean","INTERSECT",EDGE,{"derivedFrom":[subQ5,makeQuery(id+"F3.opExtrude","SWEPT_FACE",FACE,{"disambiguationData":[OSD([sQuery(id+"F2.wireOp",EDGE,"E42.2")])]})]}),makeQuery(id+"F3.boolean.opBoolean","INTERSECT",EDGE,{"derivedFrom":[subQ5,makeQuery(id+"F3.opExtrude","SWEPT_FACE",FACE,{"disambiguationData":[OSD([sQuery(id+"F2.wireOp",EDGE,"E42.3")])]})]}),makeQuery(id+"F3.boolean.opBoolean","INTERSECT",EDGE,{"derivedFrom":[subQ5,makeQuery(id+"F3.opExtrude","SWEPT_FACE",FACE,{"disambiguationData":[OSD([sQuery(id+"F2.wireOp",EDGE,"E42.4")])]})]}),makeQuery(id+"F3.boolean.opBoolean","INTERSECT",EDGE,{"derivedFrom":[subQ5,makeQuery(id+"F3.opExtrude","SWEPT_FACE",FACE,{"disambiguationData":[OSD([sQuery(id+"F2.wireOp",EDGE,"E42.5")])]})]}),makeQuery(id+"F3.boolean.opBoolean","INTERSECT",EDGE,{"derivedFrom":[subQ4,makeQuery(id+"F3.opExtrude","SWEPT_FACE",FACE,{"disambiguationData":[OSD([sQuery(id+"F2.wireOp",EDGE,"E39.0")])]})]}),makeQuery(id+"F3.boolean.opBoolean","INTERSECT",EDGE,{"derivedFrom":[subQ4,makeQuery(id+"F3.opExtrude","SWEPT_FACE",FACE,{"disambiguationData":[OSD([sQuery(id+"F2.wireOp",EDGE,"E39.1")])]})]}),makeQuery(id+"F3.boolean.opBoolean","INTERSECT",EDGE,{"derivedFrom":[subQ4,makeQuery(id+"F3.opExtrude","SWEPT_FACE",FACE,{"disambiguationData":[OSD([sQuery(id+"F2.wireOp",EDGE,"E39.2")])]})]}),makeQuery(id+"F3.boolean.opBoolean","INTERSECT",EDGE,{"derivedFrom":[subQ4,makeQuery(id+"F3.opExtrude","SWEPT_FACE",FACE,{"disambiguationData":[OSD([sQuery(id+"F2.wireOp",EDGE,"E39.3")])]})]}),makeQuery(id+"F3.boolean.opBoolean","INTERSECT",EDGE,{"derivedFrom":[subQ4,makeQuery(id+"F3.opExtrude","SWEPT_FACE",FACE,{"disambiguationData":[OSD([sQuery(id+"F2.wireOp",EDGE,"E39.4")])]})]}),makeQuery(id+"F3.boolean.opBoolean","INTERSECT",EDGE,{"derivedFrom":[subQ4,makeQuery(id+"F3.opExtrude","SWEPT_FACE",FACE,{"disambiguationData":[OSD([sQuery(id+"F2.wireOp",EDGE,"E39.5")])]})]}),makeQuery(id+"F3.boolean.opBoolean","INTERSECT",EDGE,{"derivedFrom":[subQ4,makeQuery(id+"F3.opExtrude","SWEPT_FACE",FACE,{"disambiguationData":[OSD([sQuery(id+"F2.wireOp",EDGE,"E40.0")])]})]}),makeQuery(id+"F3.boolean.opBoolean","INTERSECT",EDGE,{"derivedFrom":[subQ4,makeQuery(id+"F3.opExtrude","SWEPT_FACE",FACE,{"disambiguationData":[OSD([sQuery(id+"F2.wireOp",EDGE,"E40.1")])]})]}),makeQuery(id+"F3.boolean.opBoolean","INTERSECT",EDGE,{"derivedFrom":[subQ4,makeQuery(id+"F3.opExtrude","SWEPT_FACE",FACE,{"disambiguationData":[OSD([sQuery(id+"F2.wireOp",EDGE,"E40.2")])]})]}),makeQuery(id+"F3.boolean.opBoolean","INTERSECT",EDGE,{"derivedFrom":[subQ4,makeQuery(id+"F3.opExtrude","SWEPT_FACE",FACE,{"disambiguationData":[OSD([sQuery(id+"F2.wireOp",EDGE,"E40.3")])]})]}),makeQuery(id+"F3.boolean.opBoolean","INTERSECT",EDGE,{"derivedFrom":[subQ4,makeQuery(id+"F3.opExtrude","SWEPT_FACE",FACE,{"disambiguationData":[OSD([sQuery(id+"F2.wireOp",EDGE,"E40.4")])]})]}),makeQuery(id+"F3.boolean.opBoolean","INTERSECT",EDGE,{"derivedFrom":[subQ4,makeQuery(id+"F3.opExtrude","SWEPT_FACE",FACE,{"disambiguationData":[OSD([sQuery(id+"F2.wireOp",EDGE,"E40.5")])]})]}),makeQuery(id+"F3.boolean.opBoolean","INTERSECT",EDGE,{"derivedFrom":[subQ2,makeQuery(id+"F3.opExtrude","SWEPT_FACE",FACE,{"disambiguationData":[OSD([sQuery(id+"F2.wireOp",EDGE,"E36.0")])]})]}),makeQuery(id+"F3.boolean.opBoolean","INTERSECT",EDGE,{"derivedFrom":[subQ2,makeQuery(id+"F3.opExtrude","SWEPT_FACE",FACE,{"disambiguationData":[OSD([sQuery(id+"F2.wireOp",EDGE,"E36.1")])]})]}),makeQuery(id+"F3.boolean.opBoolean","INTERSECT",EDGE,{"derivedFrom":[subQ2,makeQuery(id+"F3.opExtrude","SWEPT_FACE",FACE,{"disambiguationData":[OSD([sQuery(id+"F2.wireOp",EDGE,"E36.2")])]})]}),makeQuery(id+"F3.boolean.opBoolean","INTERSECT",EDGE,{"derivedFrom":[subQ2,makeQuery(id+"F3.opExtrude","SWEPT_FACE",FACE,{"disambiguationData":[OSD([sQuery(id+"F2.wireOp",EDGE,"E36.3")])]})]}),makeQuery(id+"F3.boolean.opBoolean","INTERSECT",EDGE,{"derivedFrom":[subQ2,makeQuery(id+"F3.opExtrude","SWEPT_FACE",FACE,{"disambiguationData":[OSD([sQuery(id+"F2.wireOp",EDGE,"E36.4")])]})]}),makeQuery(id+"F3.boolean.opBoolean","INTERSECT",EDGE,{"derivedFrom":[subQ2,makeQuery(id+"F3.opExtrude","SWEPT_FACE",FACE,{"disambiguationData":[OSD([sQuery(id+"F2.wireOp",EDGE,"E36.5")])]})]}),makeQuery(id+"F3.boolean.opBoolean","INTERSECT",EDGE,{"derivedFrom":[subQ2,makeQuery(id+"F3.opExtrude","SWEPT_FACE",FACE,{"disambiguationData":[OSD([sQuery(id+"F2.wireOp",EDGE,"E37.0")])]})]}),makeQuery(id+"F3.boolean.opBoolean","INTERSECT",EDGE,{"derivedFrom":[subQ2,makeQuery(id+"F3.opExtrude","SWEPT_FACE",FACE,{"disambiguationData":[OSD([sQuery(id+"F2.wireOp",EDGE,"E37.1")])]})]}),makeQuery(id+"F3.boolean.opBoolean","INTERSECT",EDGE,{"derivedFrom":[subQ2,makeQuery(id+"F3.opExtrude","SWEPT_FACE",FACE,{"disambiguationData":[OSD([sQuery(id+"F2.wireOp",EDGE,"E37.2")])]})]}),makeQuery(id+"F3.boolean.opBoolean","INTERSECT",EDGE,{"derivedFrom":[subQ2,makeQuery(id+"F3.opExtrude","SWEPT_FACE",FACE,{"disambiguationData":[OSD([sQuery(id+"F2.wireOp",EDGE,"E37.3")])]})]}),makeQuery(id+"F3.boolean.opBoolean","INTERSECT",EDGE,{"derivedFrom":[subQ2,makeQuery(id+"F3.opExtrude","SWEPT_FACE",FACE,{"disambiguationData":[OSD([sQuery(id+"F2.wireOp",EDGE,"E37.4")])]})]}),makeQuery(id+"F3.boolean.opBoolean","INTERSECT",EDGE,{"derivedFrom":[subQ2,makeQuery(id+"F3.opExtrude","SWEPT_FACE",FACE,{"disambiguationData":[OSD([sQuery(id+"F2.wireOp",EDGE,"E37.5")])]})]}),makeQuery(id+"F3.boolean.opBoolean","INTERSECT",EDGE,{"derivedFrom":[subQ2,makeQuery(id+"F3.opExtrude","SWEPT_FACE",FACE,{"disambiguationData":[OSD([sQuery(id+"F2.wireOp",EDGE,"E38.0")])]})]}),makeQuery(id+"F3.boolean.opBoolean","INTERSECT",EDGE,{"derivedFrom":[subQ2,makeQuery(id+"F3.opExtrude","SWEPT_FACE",FACE,{"disambiguationData":[OSD([sQuery(id+"F2.wireOp",EDGE,"E38.1")])]})]}),makeQuery(id+"F3.boolean.opBoolean","INTERSECT",EDGE,{"derivedFrom":[subQ2,makeQuery(id+"F3.opExtrude","SWEPT_FACE",FACE,{"disambiguationData":[OSD([sQuery(id+"F2.wireOp",EDGE,"E38.2")])]})]}),makeQuery(id+"F3.boolean.opBoolean","INTERSECT",EDGE,{"derivedFrom":[subQ2,makeQuery(id+"F3.opExtrude","SWEPT_FACE",FACE,{"disambiguationData":[OSD([sQuery(id+"F2.wireOp",EDGE,"E38.3")])]})]}),makeQuery(id+"F3.boolean.opBoolean","INTERSECT",EDGE,{"derivedFrom":[subQ2,makeQuery(id+"F3.opExtrude","SWEPT_FACE",FACE,{"disambiguationData":[OSD([sQuery(id+"F2.wireOp",EDGE,"E38.4")])]})]}),makeQuery(id+"F3.boolean.opBoolean","INTERSECT",EDGE,{"derivedFrom":[subQ2,makeQuery(id+"F3.opExtrude","SWEPT_FACE",FACE,{"disambiguationData":[OSD([sQuery(id+"F2.wireOp",EDGE,"E38.5")])]})]})]);}
            var Q16;
            {var subQ0=sQuery(id+"F0.wireOp",EDGE,"E6");var subQ1=sQuery(id+"F0.wireOp",EDGE,"E18.top");var subQ2=makeQuery(id+"F1.opExtrude","SWEPT_FACE",FACE,{"disambiguationData":[OSD([subQ0]),TDD([makeQuery(id+"F0.imprint","IMPRINT",EDGE,{"disambiguationData":[TD([[makeQuery(id+"F0.imprint","INTERSECT",VERTEX,{"derivedFrom":[subQ0,sQuery(id+"F0.wireOp",EDGE,"E9")]}),1.0]])],"derivedFrom":subQ0})])]});var subQ4=makeQuery(id+"F1.opExtrude","SWEPT_FACE",FACE,{"disambiguationData":[OSD([subQ0]),TDD([makeQuery(id+"F0.imprint","IMPRINT",EDGE,{"disambiguationData":[TD([[makeQuery(id+"F0.imprint","INTERSECT",VERTEX,{"derivedFrom":[subQ0,subQ1,sQuery(id+"F0.wireOp",EDGE,"E18.right")]}),1.0]])],"derivedFrom":subQ0})])]});var subQ5=makeQuery(id+"F1.opExtrude","SWEPT_FACE",FACE,{"disambiguationData":[OSD([subQ0]),TDD([makeQuery(id+"F0.imprint","IMPRINT",EDGE,{"disambiguationData":[TD([[makeQuery(id+"F0.imprint","INTERSECT",VERTEX,{"derivedFrom":[subQ0,sQuery(id+"F0.wireOp",EDGE,"E12")]}),-1.0]])],"derivedFrom":subQ0})])]});Q16=qUnion([makeQuery(id+"F3.boolean.opBoolean","INTERSECT",EDGE,{"derivedFrom":[subQ5,makeQuery(id+"F3.opExtrude","SWEPT_FACE",FACE,{"disambiguationData":[OSD([sQuery(id+"F2.wireOp",EDGE,"E41.0")])]})]}),makeQuery(id+"F3.boolean.opBoolean","INTERSECT",EDGE,{"derivedFrom":[subQ5,makeQuery(id+"F3.opExtrude","SWEPT_FACE",FACE,{"disambiguationData":[OSD([sQuery(id+"F2.wireOp",EDGE,"E41.1")])]})]}),makeQuery(id+"F3.boolean.opBoolean","INTERSECT",EDGE,{"derivedFrom":[subQ5,makeQuery(id+"F3.opExtrude","SWEPT_FACE",FACE,{"disambiguationData":[OSD([sQuery(id+"F2.wireOp",EDGE,"E41.2")])]})]}),makeQuery(id+"F3.boolean.opBoolean","INTERSECT",EDGE,{"derivedFrom":[subQ5,makeQuery(id+"F3.opExtrude","SWEPT_FACE",FACE,{"disambiguationData":[OSD([sQuery(id+"F2.wireOp",EDGE,"E41.3")])]})]}),makeQuery(id+"F3.boolean.opBoolean","INTERSECT",EDGE,{"derivedFrom":[subQ5,makeQuery(id+"F3.opExtrude","SWEPT_FACE",FACE,{"disambiguationData":[OSD([sQuery(id+"F2.wireOp",EDGE,"E41.4")])]})]}),makeQuery(id+"F3.boolean.opBoolean","INTERSECT",EDGE,{"derivedFrom":[subQ5,makeQuery(id+"F3.opExtrude","SWEPT_FACE",FACE,{"disambiguationData":[OSD([sQuery(id+"F2.wireOp",EDGE,"E41.5")])]})]}),makeQuery(id+"F3.boolean.opBoolean","INTERSECT",EDGE,{"derivedFrom":[subQ5,makeQuery(id+"F3.opExtrude","SWEPT_FACE",FACE,{"disambiguationData":[OSD([sQuery(id+"F2.wireOp",EDGE,"E42.0")])]})]}),makeQuery(id+"F3.boolean.opBoolean","INTERSECT",EDGE,{"derivedFrom":[subQ5,makeQuery(id+"F3.opExtrude","SWEPT_FACE",FACE,{"disambiguationData":[OSD([sQuery(id+"F2.wireOp",EDGE,"E42.1")])]})]}),makeQuery(id+"F3.boolean.opBoolean","INTERSECT",EDGE,{"derivedFrom":[subQ5,makeQuery(id+"F3.opExtrude","SWEPT_FACE",FACE,{"disambiguationData":[OSD([sQuery(id+"F2.wireOp",EDGE,"E42.2")])]})]}),makeQuery(id+"F3.boolean.opBoolean","INTERSECT",EDGE,{"derivedFrom":[subQ5,makeQuery(id+"F3.opExtrude","SWEPT_FACE",FACE,{"disambiguationData":[OSD([sQuery(id+"F2.wireOp",EDGE,"E42.3")])]})]}),makeQuery(id+"F3.boolean.opBoolean","INTERSECT",EDGE,{"derivedFrom":[subQ5,makeQuery(id+"F3.opExtrude","SWEPT_FACE",FACE,{"disambiguationData":[OSD([sQuery(id+"F2.wireOp",EDGE,"E42.4")])]})]}),makeQuery(id+"F3.boolean.opBoolean","INTERSECT",EDGE,{"derivedFrom":[subQ5,makeQuery(id+"F3.opExtrude","SWEPT_FACE",FACE,{"disambiguationData":[OSD([sQuery(id+"F2.wireOp",EDGE,"E42.5")])]})]}),makeQuery(id+"F3.boolean.opBoolean","INTERSECT",EDGE,{"derivedFrom":[subQ4,makeQuery(id+"F3.opExtrude","SWEPT_FACE",FACE,{"disambiguationData":[OSD([sQuery(id+"F2.wireOp",EDGE,"E39.0")])]})]}),makeQuery(id+"F3.boolean.opBoolean","INTERSECT",EDGE,{"derivedFrom":[subQ4,makeQuery(id+"F3.opExtrude","SWEPT_FACE",FACE,{"disambiguationData":[OSD([sQuery(id+"F2.wireOp",EDGE,"E39.1")])]})]}),makeQuery(id+"F3.boolean.opBoolean","INTERSECT",EDGE,{"derivedFrom":[subQ4,makeQuery(id+"F3.opExtrude","SWEPT_FACE",FACE,{"disambiguationData":[OSD([sQuery(id+"F2.wireOp",EDGE,"E39.2")])]})]}),makeQuery(id+"F3.boolean.opBoolean","INTERSECT",EDGE,{"derivedFrom":[subQ4,makeQuery(id+"F3.opExtrude","SWEPT_FACE",FACE,{"disambiguationData":[OSD([sQuery(id+"F2.wireOp",EDGE,"E39.3")])]})]}),makeQuery(id+"F3.boolean.opBoolean","INTERSECT",EDGE,{"derivedFrom":[subQ4,makeQuery(id+"F3.opExtrude","SWEPT_FACE",FACE,{"disambiguationData":[OSD([sQuery(id+"F2.wireOp",EDGE,"E39.4")])]})]}),makeQuery(id+"F3.boolean.opBoolean","INTERSECT",EDGE,{"derivedFrom":[subQ4,makeQuery(id+"F3.opExtrude","SWEPT_FACE",FACE,{"disambiguationData":[OSD([sQuery(id+"F2.wireOp",EDGE,"E39.5")])]})]}),makeQuery(id+"F3.boolean.opBoolean","INTERSECT",EDGE,{"derivedFrom":[subQ4,makeQuery(id+"F3.opExtrude","SWEPT_FACE",FACE,{"disambiguationData":[OSD([sQuery(id+"F2.wireOp",EDGE,"E40.0")])]})]}),makeQuery(id+"F3.boolean.opBoolean","INTERSECT",EDGE,{"derivedFrom":[subQ4,makeQuery(id+"F3.opExtrude","SWEPT_FACE",FACE,{"disambiguationData":[OSD([sQuery(id+"F2.wireOp",EDGE,"E40.1")])]})]}),makeQuery(id+"F3.boolean.opBoolean","INTERSECT",EDGE,{"derivedFrom":[subQ4,makeQuery(id+"F3.opExtrude","SWEPT_FACE",FACE,{"disambiguationData":[OSD([sQuery(id+"F2.wireOp",EDGE,"E40.2")])]})]}),makeQuery(id+"F3.boolean.opBoolean","INTERSECT",EDGE,{"derivedFrom":[subQ4,makeQuery(id+"F3.opExtrude","SWEPT_FACE",FACE,{"disambiguationData":[OSD([sQuery(id+"F2.wireOp",EDGE,"E40.3")])]})]}),makeQuery(id+"F3.boolean.opBoolean","INTERSECT",EDGE,{"derivedFrom":[subQ4,makeQuery(id+"F3.opExtrude","SWEPT_FACE",FACE,{"disambiguationData":[OSD([sQuery(id+"F2.wireOp",EDGE,"E40.4")])]})]}),makeQuery(id+"F3.boolean.opBoolean","INTERSECT",EDGE,{"derivedFrom":[subQ4,makeQuery(id+"F3.opExtrude","SWEPT_FACE",FACE,{"disambiguationData":[OSD([sQuery(id+"F2.wireOp",EDGE,"E40.5")])]})]}),makeQuery(id+"F3.boolean.opBoolean","INTERSECT",EDGE,{"derivedFrom":[subQ2,makeQuery(id+"F3.opExtrude","SWEPT_FACE",FACE,{"disambiguationData":[OSD([sQuery(id+"F2.wireOp",EDGE,"E36.0")])]})]}),makeQuery(id+"F3.boolean.opBoolean","INTERSECT",EDGE,{"derivedFrom":[subQ2,makeQuery(id+"F3.opExtrude","SWEPT_FACE",FACE,{"disambiguationData":[OSD([sQuery(id+"F2.wireOp",EDGE,"E36.1")])]})]}),makeQuery(id+"F3.boolean.opBoolean","INTERSECT",EDGE,{"derivedFrom":[subQ2,makeQuery(id+"F3.opExtrude","SWEPT_FACE",FACE,{"disambiguationData":[OSD([sQuery(id+"F2.wireOp",EDGE,"E36.2")])]})]}),makeQuery(id+"F3.boolean.opBoolean","INTERSECT",EDGE,{"derivedFrom":[subQ2,makeQuery(id+"F3.opExtrude","SWEPT_FACE",FACE,{"disambiguationData":[OSD([sQuery(id+"F2.wireOp",EDGE,"E36.3")])]})]}),makeQuery(id+"F3.boolean.opBoolean","INTERSECT",EDGE,{"derivedFrom":[subQ2,makeQuery(id+"F3.opExtrude","SWEPT_FACE",FACE,{"disambiguationData":[OSD([sQuery(id+"F2.wireOp",EDGE,"E36.4")])]})]}),makeQuery(id+"F3.boolean.opBoolean","INTERSECT",EDGE,{"derivedFrom":[subQ2,makeQuery(id+"F3.opExtrude","SWEPT_FACE",FACE,{"disambiguationData":[OSD([sQuery(id+"F2.wireOp",EDGE,"E36.5")])]})]}),makeQuery(id+"F3.boolean.opBoolean","INTERSECT",EDGE,{"derivedFrom":[subQ2,makeQuery(id+"F3.opExtrude","SWEPT_FACE",FACE,{"disambiguationData":[OSD([sQuery(id+"F2.wireOp",EDGE,"E37.0")])]})]}),makeQuery(id+"F3.boolean.opBoolean","INTERSECT",EDGE,{"derivedFrom":[subQ2,makeQuery(id+"F3.opExtrude","SWEPT_FACE",FACE,{"disambiguationData":[OSD([sQuery(id+"F2.wireOp",EDGE,"E37.1")])]})]}),makeQuery(id+"F3.boolean.opBoolean","INTERSECT",EDGE,{"derivedFrom":[subQ2,makeQuery(id+"F3.opExtrude","SWEPT_FACE",FACE,{"disambiguationData":[OSD([sQuery(id+"F2.wireOp",EDGE,"E37.2")])]})]}),makeQuery(id+"F3.boolean.opBoolean","INTERSECT",EDGE,{"derivedFrom":[subQ2,makeQuery(id+"F3.opExtrude","SWEPT_FACE",FACE,{"disambiguationData":[OSD([sQuery(id+"F2.wireOp",EDGE,"E37.3")])]})]}),makeQuery(id+"F3.boolean.opBoolean","INTERSECT",EDGE,{"derivedFrom":[subQ2,makeQuery(id+"F3.opExtrude","SWEPT_FACE",FACE,{"disambiguationData":[OSD([sQuery(id+"F2.wireOp",EDGE,"E37.4")])]})]}),makeQuery(id+"F3.boolean.opBoolean","INTERSECT",EDGE,{"derivedFrom":[subQ2,makeQuery(id+"F3.opExtrude","SWEPT_FACE",FACE,{"disambiguationData":[OSD([sQuery(id+"F2.wireOp",EDGE,"E37.5")])]})]}),makeQuery(id+"F3.boolean.opBoolean","INTERSECT",EDGE,{"derivedFrom":[subQ2,makeQuery(id+"F3.opExtrude","SWEPT_FACE",FACE,{"disambiguationData":[OSD([sQuery(id+"F2.wireOp",EDGE,"E38.0")])]})]}),makeQuery(id+"F3.boolean.opBoolean","INTERSECT",EDGE,{"derivedFrom":[subQ2,makeQuery(id+"F3.opExtrude","SWEPT_FACE",FACE,{"disambiguationData":[OSD([sQuery(id+"F2.wireOp",EDGE,"E38.1")])]})]}),makeQuery(id+"F3.boolean.opBoolean","INTERSECT",EDGE,{"derivedFrom":[subQ2,makeQuery(id+"F3.opExtrude","SWEPT_FACE",FACE,{"disambiguationData":[OSD([sQuery(id+"F2.wireOp",EDGE,"E38.2")])]})]}),makeQuery(id+"F3.boolean.opBoolean","INTERSECT",EDGE,{"derivedFrom":[subQ2,makeQuery(id+"F3.opExtrude","SWEPT_FACE",FACE,{"disambiguationData":[OSD([sQuery(id+"F2.wireOp",EDGE,"E38.3")])]})]}),makeQuery(id+"F3.boolean.opBoolean","INTERSECT",EDGE,{"derivedFrom":[subQ2,makeQuery(id+"F3.opExtrude","SWEPT_FACE",FACE,{"disambiguationData":[OSD([sQuery(id+"F2.wireOp",EDGE,"E38.4")])]})]}),makeQuery(id+"F3.boolean.opBoolean","INTERSECT",EDGE,{"derivedFrom":[subQ2,makeQuery(id+"F3.opExtrude","SWEPT_FACE",FACE,{"disambiguationData":[OSD([sQuery(id+"F2.wireOp",EDGE,"E38.5")])]})]})]);}
            var Q17;
            {var subQ0=sQuery(id+"F0.wireOp",EDGE,"E6");var subQ1=sQuery(id+"F0.wireOp",EDGE,"E18.top");var subQ2=makeQuery(id+"F1.opExtrude","SWEPT_FACE",FACE,{"disambiguationData":[OSD([subQ0]),TDD([makeQuery(id+"F0.imprint","IMPRINT",EDGE,{"disambiguationData":[TD([[makeQuery(id+"F0.imprint","INTERSECT",VERTEX,{"derivedFrom":[subQ0,sQuery(id+"F0.wireOp",EDGE,"E9")]}),1.0]])],"derivedFrom":subQ0})])]});var subQ4=makeQuery(id+"F1.opExtrude","SWEPT_FACE",FACE,{"disambiguationData":[OSD([subQ0]),TDD([makeQuery(id+"F0.imprint","IMPRINT",EDGE,{"disambiguationData":[TD([[makeQuery(id+"F0.imprint","INTERSECT",VERTEX,{"derivedFrom":[subQ0,subQ1,sQuery(id+"F0.wireOp",EDGE,"E18.right")]}),1.0]])],"derivedFrom":subQ0})])]});var subQ5=makeQuery(id+"F1.opExtrude","SWEPT_FACE",FACE,{"disambiguationData":[OSD([subQ0]),TDD([makeQuery(id+"F0.imprint","IMPRINT",EDGE,{"disambiguationData":[TD([[makeQuery(id+"F0.imprint","INTERSECT",VERTEX,{"derivedFrom":[subQ0,sQuery(id+"F0.wireOp",EDGE,"E12")]}),-1.0]])],"derivedFrom":subQ0})])]});Q17=qUnion([makeQuery(id+"F3.boolean.opBoolean","INTERSECT",EDGE,{"derivedFrom":[subQ5,makeQuery(id+"F3.opExtrude","SWEPT_FACE",FACE,{"disambiguationData":[OSD([sQuery(id+"F2.wireOp",EDGE,"E41.0")])]})]}),makeQuery(id+"F3.boolean.opBoolean","INTERSECT",EDGE,{"derivedFrom":[subQ5,makeQuery(id+"F3.opExtrude","SWEPT_FACE",FACE,{"disambiguationData":[OSD([sQuery(id+"F2.wireOp",EDGE,"E41.1")])]})]}),makeQuery(id+"F3.boolean.opBoolean","INTERSECT",EDGE,{"derivedFrom":[subQ5,makeQuery(id+"F3.opExtrude","SWEPT_FACE",FACE,{"disambiguationData":[OSD([sQuery(id+"F2.wireOp",EDGE,"E41.2")])]})]}),makeQuery(id+"F3.boolean.opBoolean","INTERSECT",EDGE,{"derivedFrom":[subQ5,makeQuery(id+"F3.opExtrude","SWEPT_FACE",FACE,{"disambiguationData":[OSD([sQuery(id+"F2.wireOp",EDGE,"E41.3")])]})]}),makeQuery(id+"F3.boolean.opBoolean","INTERSECT",EDGE,{"derivedFrom":[subQ5,makeQuery(id+"F3.opExtrude","SWEPT_FACE",FACE,{"disambiguationData":[OSD([sQuery(id+"F2.wireOp",EDGE,"E41.4")])]})]}),makeQuery(id+"F3.boolean.opBoolean","INTERSECT",EDGE,{"derivedFrom":[subQ5,makeQuery(id+"F3.opExtrude","SWEPT_FACE",FACE,{"disambiguationData":[OSD([sQuery(id+"F2.wireOp",EDGE,"E41.5")])]})]}),makeQuery(id+"F3.boolean.opBoolean","INTERSECT",EDGE,{"derivedFrom":[subQ5,makeQuery(id+"F3.opExtrude","SWEPT_FACE",FACE,{"disambiguationData":[OSD([sQuery(id+"F2.wireOp",EDGE,"E42.0")])]})]}),makeQuery(id+"F3.boolean.opBoolean","INTERSECT",EDGE,{"derivedFrom":[subQ5,makeQuery(id+"F3.opExtrude","SWEPT_FACE",FACE,{"disambiguationData":[OSD([sQuery(id+"F2.wireOp",EDGE,"E42.1")])]})]}),makeQuery(id+"F3.boolean.opBoolean","INTERSECT",EDGE,{"derivedFrom":[subQ5,makeQuery(id+"F3.opExtrude","SWEPT_FACE",FACE,{"disambiguationData":[OSD([sQuery(id+"F2.wireOp",EDGE,"E42.2")])]})]}),makeQuery(id+"F3.boolean.opBoolean","INTERSECT",EDGE,{"derivedFrom":[subQ5,makeQuery(id+"F3.opExtrude","SWEPT_FACE",FACE,{"disambiguationData":[OSD([sQuery(id+"F2.wireOp",EDGE,"E42.3")])]})]}),makeQuery(id+"F3.boolean.opBoolean","INTERSECT",EDGE,{"derivedFrom":[subQ5,makeQuery(id+"F3.opExtrude","SWEPT_FACE",FACE,{"disambiguationData":[OSD([sQuery(id+"F2.wireOp",EDGE,"E42.4")])]})]}),makeQuery(id+"F3.boolean.opBoolean","INTERSECT",EDGE,{"derivedFrom":[subQ5,makeQuery(id+"F3.opExtrude","SWEPT_FACE",FACE,{"disambiguationData":[OSD([sQuery(id+"F2.wireOp",EDGE,"E42.5")])]})]}),makeQuery(id+"F3.boolean.opBoolean","INTERSECT",EDGE,{"derivedFrom":[subQ4,makeQuery(id+"F3.opExtrude","SWEPT_FACE",FACE,{"disambiguationData":[OSD([sQuery(id+"F2.wireOp",EDGE,"E39.0")])]})]}),makeQuery(id+"F3.boolean.opBoolean","INTERSECT",EDGE,{"derivedFrom":[subQ4,makeQuery(id+"F3.opExtrude","SWEPT_FACE",FACE,{"disambiguationData":[OSD([sQuery(id+"F2.wireOp",EDGE,"E39.1")])]})]}),makeQuery(id+"F3.boolean.opBoolean","INTERSECT",EDGE,{"derivedFrom":[subQ4,makeQuery(id+"F3.opExtrude","SWEPT_FACE",FACE,{"disambiguationData":[OSD([sQuery(id+"F2.wireOp",EDGE,"E39.2")])]})]}),makeQuery(id+"F3.boolean.opBoolean","INTERSECT",EDGE,{"derivedFrom":[subQ4,makeQuery(id+"F3.opExtrude","SWEPT_FACE",FACE,{"disambiguationData":[OSD([sQuery(id+"F2.wireOp",EDGE,"E39.3")])]})]}),makeQuery(id+"F3.boolean.opBoolean","INTERSECT",EDGE,{"derivedFrom":[subQ4,makeQuery(id+"F3.opExtrude","SWEPT_FACE",FACE,{"disambiguationData":[OSD([sQuery(id+"F2.wireOp",EDGE,"E39.4")])]})]}),makeQuery(id+"F3.boolean.opBoolean","INTERSECT",EDGE,{"derivedFrom":[subQ4,makeQuery(id+"F3.opExtrude","SWEPT_FACE",FACE,{"disambiguationData":[OSD([sQuery(id+"F2.wireOp",EDGE,"E39.5")])]})]}),makeQuery(id+"F3.boolean.opBoolean","INTERSECT",EDGE,{"derivedFrom":[subQ4,makeQuery(id+"F3.opExtrude","SWEPT_FACE",FACE,{"disambiguationData":[OSD([sQuery(id+"F2.wireOp",EDGE,"E40.0")])]})]}),makeQuery(id+"F3.boolean.opBoolean","INTERSECT",EDGE,{"derivedFrom":[subQ4,makeQuery(id+"F3.opExtrude","SWEPT_FACE",FACE,{"disambiguationData":[OSD([sQuery(id+"F2.wireOp",EDGE,"E40.1")])]})]}),makeQuery(id+"F3.boolean.opBoolean","INTERSECT",EDGE,{"derivedFrom":[subQ4,makeQuery(id+"F3.opExtrude","SWEPT_FACE",FACE,{"disambiguationData":[OSD([sQuery(id+"F2.wireOp",EDGE,"E40.2")])]})]}),makeQuery(id+"F3.boolean.opBoolean","INTERSECT",EDGE,{"derivedFrom":[subQ4,makeQuery(id+"F3.opExtrude","SWEPT_FACE",FACE,{"disambiguationData":[OSD([sQuery(id+"F2.wireOp",EDGE,"E40.3")])]})]}),makeQuery(id+"F3.boolean.opBoolean","INTERSECT",EDGE,{"derivedFrom":[subQ4,makeQuery(id+"F3.opExtrude","SWEPT_FACE",FACE,{"disambiguationData":[OSD([sQuery(id+"F2.wireOp",EDGE,"E40.4")])]})]}),makeQuery(id+"F3.boolean.opBoolean","INTERSECT",EDGE,{"derivedFrom":[subQ4,makeQuery(id+"F3.opExtrude","SWEPT_FACE",FACE,{"disambiguationData":[OSD([sQuery(id+"F2.wireOp",EDGE,"E40.5")])]})]}),makeQuery(id+"F3.boolean.opBoolean","INTERSECT",EDGE,{"derivedFrom":[subQ2,makeQuery(id+"F3.opExtrude","SWEPT_FACE",FACE,{"disambiguationData":[OSD([sQuery(id+"F2.wireOp",EDGE,"E36.0")])]})]}),makeQuery(id+"F3.boolean.opBoolean","INTERSECT",EDGE,{"derivedFrom":[subQ2,makeQuery(id+"F3.opExtrude","SWEPT_FACE",FACE,{"disambiguationData":[OSD([sQuery(id+"F2.wireOp",EDGE,"E36.1")])]})]}),makeQuery(id+"F3.boolean.opBoolean","INTERSECT",EDGE,{"derivedFrom":[subQ2,makeQuery(id+"F3.opExtrude","SWEPT_FACE",FACE,{"disambiguationData":[OSD([sQuery(id+"F2.wireOp",EDGE,"E36.2")])]})]}),makeQuery(id+"F3.boolean.opBoolean","INTERSECT",EDGE,{"derivedFrom":[subQ2,makeQuery(id+"F3.opExtrude","SWEPT_FACE",FACE,{"disambiguationData":[OSD([sQuery(id+"F2.wireOp",EDGE,"E36.3")])]})]}),makeQuery(id+"F3.boolean.opBoolean","INTERSECT",EDGE,{"derivedFrom":[subQ2,makeQuery(id+"F3.opExtrude","SWEPT_FACE",FACE,{"disambiguationData":[OSD([sQuery(id+"F2.wireOp",EDGE,"E36.4")])]})]}),makeQuery(id+"F3.boolean.opBoolean","INTERSECT",EDGE,{"derivedFrom":[subQ2,makeQuery(id+"F3.opExtrude","SWEPT_FACE",FACE,{"disambiguationData":[OSD([sQuery(id+"F2.wireOp",EDGE,"E36.5")])]})]}),makeQuery(id+"F3.boolean.opBoolean","INTERSECT",EDGE,{"derivedFrom":[subQ2,makeQuery(id+"F3.opExtrude","SWEPT_FACE",FACE,{"disambiguationData":[OSD([sQuery(id+"F2.wireOp",EDGE,"E37.0")])]})]}),makeQuery(id+"F3.boolean.opBoolean","INTERSECT",EDGE,{"derivedFrom":[subQ2,makeQuery(id+"F3.opExtrude","SWEPT_FACE",FACE,{"disambiguationData":[OSD([sQuery(id+"F2.wireOp",EDGE,"E37.1")])]})]}),makeQuery(id+"F3.boolean.opBoolean","INTERSECT",EDGE,{"derivedFrom":[subQ2,makeQuery(id+"F3.opExtrude","SWEPT_FACE",FACE,{"disambiguationData":[OSD([sQuery(id+"F2.wireOp",EDGE,"E37.2")])]})]}),makeQuery(id+"F3.boolean.opBoolean","INTERSECT",EDGE,{"derivedFrom":[subQ2,makeQuery(id+"F3.opExtrude","SWEPT_FACE",FACE,{"disambiguationData":[OSD([sQuery(id+"F2.wireOp",EDGE,"E37.3")])]})]}),makeQuery(id+"F3.boolean.opBoolean","INTERSECT",EDGE,{"derivedFrom":[subQ2,makeQuery(id+"F3.opExtrude","SWEPT_FACE",FACE,{"disambiguationData":[OSD([sQuery(id+"F2.wireOp",EDGE,"E37.4")])]})]}),makeQuery(id+"F3.boolean.opBoolean","INTERSECT",EDGE,{"derivedFrom":[subQ2,makeQuery(id+"F3.opExtrude","SWEPT_FACE",FACE,{"disambiguationData":[OSD([sQuery(id+"F2.wireOp",EDGE,"E37.5")])]})]}),makeQuery(id+"F3.boolean.opBoolean","INTERSECT",EDGE,{"derivedFrom":[subQ2,makeQuery(id+"F3.opExtrude","SWEPT_FACE",FACE,{"disambiguationData":[OSD([sQuery(id+"F2.wireOp",EDGE,"E38.0")])]})]}),makeQuery(id+"F3.boolean.opBoolean","INTERSECT",EDGE,{"derivedFrom":[subQ2,makeQuery(id+"F3.opExtrude","SWEPT_FACE",FACE,{"disambiguationData":[OSD([sQuery(id+"F2.wireOp",EDGE,"E38.1")])]})]}),makeQuery(id+"F3.boolean.opBoolean","INTERSECT",EDGE,{"derivedFrom":[subQ2,makeQuery(id+"F3.opExtrude","SWEPT_FACE",FACE,{"disambiguationData":[OSD([sQuery(id+"F2.wireOp",EDGE,"E38.2")])]})]}),makeQuery(id+"F3.boolean.opBoolean","INTERSECT",EDGE,{"derivedFrom":[subQ2,makeQuery(id+"F3.opExtrude","SWEPT_FACE",FACE,{"disambiguationData":[OSD([sQuery(id+"F2.wireOp",EDGE,"E38.3")])]})]}),makeQuery(id+"F3.boolean.opBoolean","INTERSECT",EDGE,{"derivedFrom":[subQ2,makeQuery(id+"F3.opExtrude","SWEPT_FACE",FACE,{"disambiguationData":[OSD([sQuery(id+"F2.wireOp",EDGE,"E38.4")])]})]}),makeQuery(id+"F3.boolean.opBoolean","INTERSECT",EDGE,{"derivedFrom":[subQ2,makeQuery(id+"F3.opExtrude","SWEPT_FACE",FACE,{"disambiguationData":[OSD([sQuery(id+"F2.wireOp",EDGE,"E38.5")])]})]})]);}
            var Q18;
            {var subQ0=sQuery(id+"F0.wireOp",EDGE,"E6");var subQ1=sQuery(id+"F0.wireOp",EDGE,"E18.top");var subQ2=makeQuery(id+"F1.opExtrude","SWEPT_FACE",FACE,{"disambiguationData":[OSD([subQ0]),TDD([makeQuery(id+"F0.imprint","IMPRINT",EDGE,{"disambiguationData":[TD([[makeQuery(id+"F0.imprint","INTERSECT",VERTEX,{"derivedFrom":[subQ0,sQuery(id+"F0.wireOp",EDGE,"E9")]}),1.0]])],"derivedFrom":subQ0})])]});var subQ4=makeQuery(id+"F1.opExtrude","SWEPT_FACE",FACE,{"disambiguationData":[OSD([subQ0]),TDD([makeQuery(id+"F0.imprint","IMPRINT",EDGE,{"disambiguationData":[TD([[makeQuery(id+"F0.imprint","INTERSECT",VERTEX,{"derivedFrom":[subQ0,subQ1,sQuery(id+"F0.wireOp",EDGE,"E18.right")]}),1.0]])],"derivedFrom":subQ0})])]});var subQ5=makeQuery(id+"F1.opExtrude","SWEPT_FACE",FACE,{"disambiguationData":[OSD([subQ0]),TDD([makeQuery(id+"F0.imprint","IMPRINT",EDGE,{"disambiguationData":[TD([[makeQuery(id+"F0.imprint","INTERSECT",VERTEX,{"derivedFrom":[subQ0,sQuery(id+"F0.wireOp",EDGE,"E12")]}),-1.0]])],"derivedFrom":subQ0})])]});Q18=qUnion([makeQuery(id+"F3.boolean.opBoolean","INTERSECT",EDGE,{"derivedFrom":[subQ5,makeQuery(id+"F3.opExtrude","SWEPT_FACE",FACE,{"disambiguationData":[OSD([sQuery(id+"F2.wireOp",EDGE,"E41.0")])]})]}),makeQuery(id+"F3.boolean.opBoolean","INTERSECT",EDGE,{"derivedFrom":[subQ5,makeQuery(id+"F3.opExtrude","SWEPT_FACE",FACE,{"disambiguationData":[OSD([sQuery(id+"F2.wireOp",EDGE,"E41.1")])]})]}),makeQuery(id+"F3.boolean.opBoolean","INTERSECT",EDGE,{"derivedFrom":[subQ5,makeQuery(id+"F3.opExtrude","SWEPT_FACE",FACE,{"disambiguationData":[OSD([sQuery(id+"F2.wireOp",EDGE,"E41.2")])]})]}),makeQuery(id+"F3.boolean.opBoolean","INTERSECT",EDGE,{"derivedFrom":[subQ5,makeQuery(id+"F3.opExtrude","SWEPT_FACE",FACE,{"disambiguationData":[OSD([sQuery(id+"F2.wireOp",EDGE,"E41.3")])]})]}),makeQuery(id+"F3.boolean.opBoolean","INTERSECT",EDGE,{"derivedFrom":[subQ5,makeQuery(id+"F3.opExtrude","SWEPT_FACE",FACE,{"disambiguationData":[OSD([sQuery(id+"F2.wireOp",EDGE,"E41.4")])]})]}),makeQuery(id+"F3.boolean.opBoolean","INTERSECT",EDGE,{"derivedFrom":[subQ5,makeQuery(id+"F3.opExtrude","SWEPT_FACE",FACE,{"disambiguationData":[OSD([sQuery(id+"F2.wireOp",EDGE,"E41.5")])]})]}),makeQuery(id+"F3.boolean.opBoolean","INTERSECT",EDGE,{"derivedFrom":[subQ5,makeQuery(id+"F3.opExtrude","SWEPT_FACE",FACE,{"disambiguationData":[OSD([sQuery(id+"F2.wireOp",EDGE,"E42.0")])]})]}),makeQuery(id+"F3.boolean.opBoolean","INTERSECT",EDGE,{"derivedFrom":[subQ5,makeQuery(id+"F3.opExtrude","SWEPT_FACE",FACE,{"disambiguationData":[OSD([sQuery(id+"F2.wireOp",EDGE,"E42.1")])]})]}),makeQuery(id+"F3.boolean.opBoolean","INTERSECT",EDGE,{"derivedFrom":[subQ5,makeQuery(id+"F3.opExtrude","SWEPT_FACE",FACE,{"disambiguationData":[OSD([sQuery(id+"F2.wireOp",EDGE,"E42.2")])]})]}),makeQuery(id+"F3.boolean.opBoolean","INTERSECT",EDGE,{"derivedFrom":[subQ5,makeQuery(id+"F3.opExtrude","SWEPT_FACE",FACE,{"disambiguationData":[OSD([sQuery(id+"F2.wireOp",EDGE,"E42.3")])]})]}),makeQuery(id+"F3.boolean.opBoolean","INTERSECT",EDGE,{"derivedFrom":[subQ5,makeQuery(id+"F3.opExtrude","SWEPT_FACE",FACE,{"disambiguationData":[OSD([sQuery(id+"F2.wireOp",EDGE,"E42.4")])]})]}),makeQuery(id+"F3.boolean.opBoolean","INTERSECT",EDGE,{"derivedFrom":[subQ5,makeQuery(id+"F3.opExtrude","SWEPT_FACE",FACE,{"disambiguationData":[OSD([sQuery(id+"F2.wireOp",EDGE,"E42.5")])]})]}),makeQuery(id+"F3.boolean.opBoolean","INTERSECT",EDGE,{"derivedFrom":[subQ4,makeQuery(id+"F3.opExtrude","SWEPT_FACE",FACE,{"disambiguationData":[OSD([sQuery(id+"F2.wireOp",EDGE,"E39.0")])]})]}),makeQuery(id+"F3.boolean.opBoolean","INTERSECT",EDGE,{"derivedFrom":[subQ4,makeQuery(id+"F3.opExtrude","SWEPT_FACE",FACE,{"disambiguationData":[OSD([sQuery(id+"F2.wireOp",EDGE,"E39.1")])]})]}),makeQuery(id+"F3.boolean.opBoolean","INTERSECT",EDGE,{"derivedFrom":[subQ4,makeQuery(id+"F3.opExtrude","SWEPT_FACE",FACE,{"disambiguationData":[OSD([sQuery(id+"F2.wireOp",EDGE,"E39.2")])]})]}),makeQuery(id+"F3.boolean.opBoolean","INTERSECT",EDGE,{"derivedFrom":[subQ4,makeQuery(id+"F3.opExtrude","SWEPT_FACE",FACE,{"disambiguationData":[OSD([sQuery(id+"F2.wireOp",EDGE,"E39.3")])]})]}),makeQuery(id+"F3.boolean.opBoolean","INTERSECT",EDGE,{"derivedFrom":[subQ4,makeQuery(id+"F3.opExtrude","SWEPT_FACE",FACE,{"disambiguationData":[OSD([sQuery(id+"F2.wireOp",EDGE,"E39.4")])]})]}),makeQuery(id+"F3.boolean.opBoolean","INTERSECT",EDGE,{"derivedFrom":[subQ4,makeQuery(id+"F3.opExtrude","SWEPT_FACE",FACE,{"disambiguationData":[OSD([sQuery(id+"F2.wireOp",EDGE,"E39.5")])]})]}),makeQuery(id+"F3.boolean.opBoolean","INTERSECT",EDGE,{"derivedFrom":[subQ4,makeQuery(id+"F3.opExtrude","SWEPT_FACE",FACE,{"disambiguationData":[OSD([sQuery(id+"F2.wireOp",EDGE,"E40.0")])]})]}),makeQuery(id+"F3.boolean.opBoolean","INTERSECT",EDGE,{"derivedFrom":[subQ4,makeQuery(id+"F3.opExtrude","SWEPT_FACE",FACE,{"disambiguationData":[OSD([sQuery(id+"F2.wireOp",EDGE,"E40.1")])]})]}),makeQuery(id+"F3.boolean.opBoolean","INTERSECT",EDGE,{"derivedFrom":[subQ4,makeQuery(id+"F3.opExtrude","SWEPT_FACE",FACE,{"disambiguationData":[OSD([sQuery(id+"F2.wireOp",EDGE,"E40.2")])]})]}),makeQuery(id+"F3.boolean.opBoolean","INTERSECT",EDGE,{"derivedFrom":[subQ4,makeQuery(id+"F3.opExtrude","SWEPT_FACE",FACE,{"disambiguationData":[OSD([sQuery(id+"F2.wireOp",EDGE,"E40.3")])]})]}),makeQuery(id+"F3.boolean.opBoolean","INTERSECT",EDGE,{"derivedFrom":[subQ4,makeQuery(id+"F3.opExtrude","SWEPT_FACE",FACE,{"disambiguationData":[OSD([sQuery(id+"F2.wireOp",EDGE,"E40.4")])]})]}),makeQuery(id+"F3.boolean.opBoolean","INTERSECT",EDGE,{"derivedFrom":[subQ4,makeQuery(id+"F3.opExtrude","SWEPT_FACE",FACE,{"disambiguationData":[OSD([sQuery(id+"F2.wireOp",EDGE,"E40.5")])]})]}),makeQuery(id+"F3.boolean.opBoolean","INTERSECT",EDGE,{"derivedFrom":[subQ2,makeQuery(id+"F3.opExtrude","SWEPT_FACE",FACE,{"disambiguationData":[OSD([sQuery(id+"F2.wireOp",EDGE,"E36.0")])]})]}),makeQuery(id+"F3.boolean.opBoolean","INTERSECT",EDGE,{"derivedFrom":[subQ2,makeQuery(id+"F3.opExtrude","SWEPT_FACE",FACE,{"disambiguationData":[OSD([sQuery(id+"F2.wireOp",EDGE,"E36.1")])]})]}),makeQuery(id+"F3.boolean.opBoolean","INTERSECT",EDGE,{"derivedFrom":[subQ2,makeQuery(id+"F3.opExtrude","SWEPT_FACE",FACE,{"disambiguationData":[OSD([sQuery(id+"F2.wireOp",EDGE,"E36.2")])]})]}),makeQuery(id+"F3.boolean.opBoolean","INTERSECT",EDGE,{"derivedFrom":[subQ2,makeQuery(id+"F3.opExtrude","SWEPT_FACE",FACE,{"disambiguationData":[OSD([sQuery(id+"F2.wireOp",EDGE,"E36.3")])]})]}),makeQuery(id+"F3.boolean.opBoolean","INTERSECT",EDGE,{"derivedFrom":[subQ2,makeQuery(id+"F3.opExtrude","SWEPT_FACE",FACE,{"disambiguationData":[OSD([sQuery(id+"F2.wireOp",EDGE,"E36.4")])]})]}),makeQuery(id+"F3.boolean.opBoolean","INTERSECT",EDGE,{"derivedFrom":[subQ2,makeQuery(id+"F3.opExtrude","SWEPT_FACE",FACE,{"disambiguationData":[OSD([sQuery(id+"F2.wireOp",EDGE,"E36.5")])]})]}),makeQuery(id+"F3.boolean.opBoolean","INTERSECT",EDGE,{"derivedFrom":[subQ2,makeQuery(id+"F3.opExtrude","SWEPT_FACE",FACE,{"disambiguationData":[OSD([sQuery(id+"F2.wireOp",EDGE,"E37.0")])]})]}),makeQuery(id+"F3.boolean.opBoolean","INTERSECT",EDGE,{"derivedFrom":[subQ2,makeQuery(id+"F3.opExtrude","SWEPT_FACE",FACE,{"disambiguationData":[OSD([sQuery(id+"F2.wireOp",EDGE,"E37.1")])]})]}),makeQuery(id+"F3.boolean.opBoolean","INTERSECT",EDGE,{"derivedFrom":[subQ2,makeQuery(id+"F3.opExtrude","SWEPT_FACE",FACE,{"disambiguationData":[OSD([sQuery(id+"F2.wireOp",EDGE,"E37.2")])]})]}),makeQuery(id+"F3.boolean.opBoolean","INTERSECT",EDGE,{"derivedFrom":[subQ2,makeQuery(id+"F3.opExtrude","SWEPT_FACE",FACE,{"disambiguationData":[OSD([sQuery(id+"F2.wireOp",EDGE,"E37.3")])]})]}),makeQuery(id+"F3.boolean.opBoolean","INTERSECT",EDGE,{"derivedFrom":[subQ2,makeQuery(id+"F3.opExtrude","SWEPT_FACE",FACE,{"disambiguationData":[OSD([sQuery(id+"F2.wireOp",EDGE,"E37.4")])]})]}),makeQuery(id+"F3.boolean.opBoolean","INTERSECT",EDGE,{"derivedFrom":[subQ2,makeQuery(id+"F3.opExtrude","SWEPT_FACE",FACE,{"disambiguationData":[OSD([sQuery(id+"F2.wireOp",EDGE,"E37.5")])]})]}),makeQuery(id+"F3.boolean.opBoolean","INTERSECT",EDGE,{"derivedFrom":[subQ2,makeQuery(id+"F3.opExtrude","SWEPT_FACE",FACE,{"disambiguationData":[OSD([sQuery(id+"F2.wireOp",EDGE,"E38.0")])]})]}),makeQuery(id+"F3.boolean.opBoolean","INTERSECT",EDGE,{"derivedFrom":[subQ2,makeQuery(id+"F3.opExtrude","SWEPT_FACE",FACE,{"disambiguationData":[OSD([sQuery(id+"F2.wireOp",EDGE,"E38.1")])]})]}),makeQuery(id+"F3.boolean.opBoolean","INTERSECT",EDGE,{"derivedFrom":[subQ2,makeQuery(id+"F3.opExtrude","SWEPT_FACE",FACE,{"disambiguationData":[OSD([sQuery(id+"F2.wireOp",EDGE,"E38.2")])]})]}),makeQuery(id+"F3.boolean.opBoolean","INTERSECT",EDGE,{"derivedFrom":[subQ2,makeQuery(id+"F3.opExtrude","SWEPT_FACE",FACE,{"disambiguationData":[OSD([sQuery(id+"F2.wireOp",EDGE,"E38.3")])]})]}),makeQuery(id+"F3.boolean.opBoolean","INTERSECT",EDGE,{"derivedFrom":[subQ2,makeQuery(id+"F3.opExtrude","SWEPT_FACE",FACE,{"disambiguationData":[OSD([sQuery(id+"F2.wireOp",EDGE,"E38.4")])]})]}),makeQuery(id+"F3.boolean.opBoolean","INTERSECT",EDGE,{"derivedFrom":[subQ2,makeQuery(id+"F3.opExtrude","SWEPT_FACE",FACE,{"disambiguationData":[OSD([sQuery(id+"F2.wireOp",EDGE,"E38.5")])]})]})]);}
            var Q19;
            {var subQ0=sQuery(id+"F0.wireOp",EDGE,"E6");var subQ1=sQuery(id+"F0.wireOp",EDGE,"E18.top");var subQ2=makeQuery(id+"F1.opExtrude","SWEPT_FACE",FACE,{"disambiguationData":[OSD([subQ0]),TDD([makeQuery(id+"F0.imprint","IMPRINT",EDGE,{"disambiguationData":[TD([[makeQuery(id+"F0.imprint","INTERSECT",VERTEX,{"derivedFrom":[subQ0,sQuery(id+"F0.wireOp",EDGE,"E9")]}),1.0]])],"derivedFrom":subQ0})])]});var subQ4=makeQuery(id+"F1.opExtrude","SWEPT_FACE",FACE,{"disambiguationData":[OSD([subQ0]),TDD([makeQuery(id+"F0.imprint","IMPRINT",EDGE,{"disambiguationData":[TD([[makeQuery(id+"F0.imprint","INTERSECT",VERTEX,{"derivedFrom":[subQ0,subQ1,sQuery(id+"F0.wireOp",EDGE,"E18.right")]}),1.0]])],"derivedFrom":subQ0})])]});var subQ5=makeQuery(id+"F1.opExtrude","SWEPT_FACE",FACE,{"disambiguationData":[OSD([subQ0]),TDD([makeQuery(id+"F0.imprint","IMPRINT",EDGE,{"disambiguationData":[TD([[makeQuery(id+"F0.imprint","INTERSECT",VERTEX,{"derivedFrom":[subQ0,sQuery(id+"F0.wireOp",EDGE,"E12")]}),-1.0]])],"derivedFrom":subQ0})])]});Q19=qUnion([makeQuery(id+"F3.boolean.opBoolean","INTERSECT",EDGE,{"derivedFrom":[subQ5,makeQuery(id+"F3.opExtrude","SWEPT_FACE",FACE,{"disambiguationData":[OSD([sQuery(id+"F2.wireOp",EDGE,"E41.0")])]})]}),makeQuery(id+"F3.boolean.opBoolean","INTERSECT",EDGE,{"derivedFrom":[subQ5,makeQuery(id+"F3.opExtrude","SWEPT_FACE",FACE,{"disambiguationData":[OSD([sQuery(id+"F2.wireOp",EDGE,"E41.1")])]})]}),makeQuery(id+"F3.boolean.opBoolean","INTERSECT",EDGE,{"derivedFrom":[subQ5,makeQuery(id+"F3.opExtrude","SWEPT_FACE",FACE,{"disambiguationData":[OSD([sQuery(id+"F2.wireOp",EDGE,"E41.2")])]})]}),makeQuery(id+"F3.boolean.opBoolean","INTERSECT",EDGE,{"derivedFrom":[subQ5,makeQuery(id+"F3.opExtrude","SWEPT_FACE",FACE,{"disambiguationData":[OSD([sQuery(id+"F2.wireOp",EDGE,"E41.3")])]})]}),makeQuery(id+"F3.boolean.opBoolean","INTERSECT",EDGE,{"derivedFrom":[subQ5,makeQuery(id+"F3.opExtrude","SWEPT_FACE",FACE,{"disambiguationData":[OSD([sQuery(id+"F2.wireOp",EDGE,"E41.4")])]})]}),makeQuery(id+"F3.boolean.opBoolean","INTERSECT",EDGE,{"derivedFrom":[subQ5,makeQuery(id+"F3.opExtrude","SWEPT_FACE",FACE,{"disambiguationData":[OSD([sQuery(id+"F2.wireOp",EDGE,"E41.5")])]})]}),makeQuery(id+"F3.boolean.opBoolean","INTERSECT",EDGE,{"derivedFrom":[subQ5,makeQuery(id+"F3.opExtrude","SWEPT_FACE",FACE,{"disambiguationData":[OSD([sQuery(id+"F2.wireOp",EDGE,"E42.0")])]})]}),makeQuery(id+"F3.boolean.opBoolean","INTERSECT",EDGE,{"derivedFrom":[subQ5,makeQuery(id+"F3.opExtrude","SWEPT_FACE",FACE,{"disambiguationData":[OSD([sQuery(id+"F2.wireOp",EDGE,"E42.1")])]})]}),makeQuery(id+"F3.boolean.opBoolean","INTERSECT",EDGE,{"derivedFrom":[subQ5,makeQuery(id+"F3.opExtrude","SWEPT_FACE",FACE,{"disambiguationData":[OSD([sQuery(id+"F2.wireOp",EDGE,"E42.2")])]})]}),makeQuery(id+"F3.boolean.opBoolean","INTERSECT",EDGE,{"derivedFrom":[subQ5,makeQuery(id+"F3.opExtrude","SWEPT_FACE",FACE,{"disambiguationData":[OSD([sQuery(id+"F2.wireOp",EDGE,"E42.3")])]})]}),makeQuery(id+"F3.boolean.opBoolean","INTERSECT",EDGE,{"derivedFrom":[subQ5,makeQuery(id+"F3.opExtrude","SWEPT_FACE",FACE,{"disambiguationData":[OSD([sQuery(id+"F2.wireOp",EDGE,"E42.4")])]})]}),makeQuery(id+"F3.boolean.opBoolean","INTERSECT",EDGE,{"derivedFrom":[subQ5,makeQuery(id+"F3.opExtrude","SWEPT_FACE",FACE,{"disambiguationData":[OSD([sQuery(id+"F2.wireOp",EDGE,"E42.5")])]})]}),makeQuery(id+"F3.boolean.opBoolean","INTERSECT",EDGE,{"derivedFrom":[subQ4,makeQuery(id+"F3.opExtrude","SWEPT_FACE",FACE,{"disambiguationData":[OSD([sQuery(id+"F2.wireOp",EDGE,"E39.0")])]})]}),makeQuery(id+"F3.boolean.opBoolean","INTERSECT",EDGE,{"derivedFrom":[subQ4,makeQuery(id+"F3.opExtrude","SWEPT_FACE",FACE,{"disambiguationData":[OSD([sQuery(id+"F2.wireOp",EDGE,"E39.1")])]})]}),makeQuery(id+"F3.boolean.opBoolean","INTERSECT",EDGE,{"derivedFrom":[subQ4,makeQuery(id+"F3.opExtrude","SWEPT_FACE",FACE,{"disambiguationData":[OSD([sQuery(id+"F2.wireOp",EDGE,"E39.2")])]})]}),makeQuery(id+"F3.boolean.opBoolean","INTERSECT",EDGE,{"derivedFrom":[subQ4,makeQuery(id+"F3.opExtrude","SWEPT_FACE",FACE,{"disambiguationData":[OSD([sQuery(id+"F2.wireOp",EDGE,"E39.3")])]})]}),makeQuery(id+"F3.boolean.opBoolean","INTERSECT",EDGE,{"derivedFrom":[subQ4,makeQuery(id+"F3.opExtrude","SWEPT_FACE",FACE,{"disambiguationData":[OSD([sQuery(id+"F2.wireOp",EDGE,"E39.4")])]})]}),makeQuery(id+"F3.boolean.opBoolean","INTERSECT",EDGE,{"derivedFrom":[subQ4,makeQuery(id+"F3.opExtrude","SWEPT_FACE",FACE,{"disambiguationData":[OSD([sQuery(id+"F2.wireOp",EDGE,"E39.5")])]})]}),makeQuery(id+"F3.boolean.opBoolean","INTERSECT",EDGE,{"derivedFrom":[subQ4,makeQuery(id+"F3.opExtrude","SWEPT_FACE",FACE,{"disambiguationData":[OSD([sQuery(id+"F2.wireOp",EDGE,"E40.0")])]})]}),makeQuery(id+"F3.boolean.opBoolean","INTERSECT",EDGE,{"derivedFrom":[subQ4,makeQuery(id+"F3.opExtrude","SWEPT_FACE",FACE,{"disambiguationData":[OSD([sQuery(id+"F2.wireOp",EDGE,"E40.1")])]})]}),makeQuery(id+"F3.boolean.opBoolean","INTERSECT",EDGE,{"derivedFrom":[subQ4,makeQuery(id+"F3.opExtrude","SWEPT_FACE",FACE,{"disambiguationData":[OSD([sQuery(id+"F2.wireOp",EDGE,"E40.2")])]})]}),makeQuery(id+"F3.boolean.opBoolean","INTERSECT",EDGE,{"derivedFrom":[subQ4,makeQuery(id+"F3.opExtrude","SWEPT_FACE",FACE,{"disambiguationData":[OSD([sQuery(id+"F2.wireOp",EDGE,"E40.3")])]})]}),makeQuery(id+"F3.boolean.opBoolean","INTERSECT",EDGE,{"derivedFrom":[subQ4,makeQuery(id+"F3.opExtrude","SWEPT_FACE",FACE,{"disambiguationData":[OSD([sQuery(id+"F2.wireOp",EDGE,"E40.4")])]})]}),makeQuery(id+"F3.boolean.opBoolean","INTERSECT",EDGE,{"derivedFrom":[subQ4,makeQuery(id+"F3.opExtrude","SWEPT_FACE",FACE,{"disambiguationData":[OSD([sQuery(id+"F2.wireOp",EDGE,"E40.5")])]})]}),makeQuery(id+"F3.boolean.opBoolean","INTERSECT",EDGE,{"derivedFrom":[subQ2,makeQuery(id+"F3.opExtrude","SWEPT_FACE",FACE,{"disambiguationData":[OSD([sQuery(id+"F2.wireOp",EDGE,"E36.0")])]})]}),makeQuery(id+"F3.boolean.opBoolean","INTERSECT",EDGE,{"derivedFrom":[subQ2,makeQuery(id+"F3.opExtrude","SWEPT_FACE",FACE,{"disambiguationData":[OSD([sQuery(id+"F2.wireOp",EDGE,"E36.1")])]})]}),makeQuery(id+"F3.boolean.opBoolean","INTERSECT",EDGE,{"derivedFrom":[subQ2,makeQuery(id+"F3.opExtrude","SWEPT_FACE",FACE,{"disambiguationData":[OSD([sQuery(id+"F2.wireOp",EDGE,"E36.2")])]})]}),makeQuery(id+"F3.boolean.opBoolean","INTERSECT",EDGE,{"derivedFrom":[subQ2,makeQuery(id+"F3.opExtrude","SWEPT_FACE",FACE,{"disambiguationData":[OSD([sQuery(id+"F2.wireOp",EDGE,"E36.3")])]})]}),makeQuery(id+"F3.boolean.opBoolean","INTERSECT",EDGE,{"derivedFrom":[subQ2,makeQuery(id+"F3.opExtrude","SWEPT_FACE",FACE,{"disambiguationData":[OSD([sQuery(id+"F2.wireOp",EDGE,"E36.4")])]})]}),makeQuery(id+"F3.boolean.opBoolean","INTERSECT",EDGE,{"derivedFrom":[subQ2,makeQuery(id+"F3.opExtrude","SWEPT_FACE",FACE,{"disambiguationData":[OSD([sQuery(id+"F2.wireOp",EDGE,"E36.5")])]})]}),makeQuery(id+"F3.boolean.opBoolean","INTERSECT",EDGE,{"derivedFrom":[subQ2,makeQuery(id+"F3.opExtrude","SWEPT_FACE",FACE,{"disambiguationData":[OSD([sQuery(id+"F2.wireOp",EDGE,"E37.0")])]})]}),makeQuery(id+"F3.boolean.opBoolean","INTERSECT",EDGE,{"derivedFrom":[subQ2,makeQuery(id+"F3.opExtrude","SWEPT_FACE",FACE,{"disambiguationData":[OSD([sQuery(id+"F2.wireOp",EDGE,"E37.1")])]})]}),makeQuery(id+"F3.boolean.opBoolean","INTERSECT",EDGE,{"derivedFrom":[subQ2,makeQuery(id+"F3.opExtrude","SWEPT_FACE",FACE,{"disambiguationData":[OSD([sQuery(id+"F2.wireOp",EDGE,"E37.2")])]})]}),makeQuery(id+"F3.boolean.opBoolean","INTERSECT",EDGE,{"derivedFrom":[subQ2,makeQuery(id+"F3.opExtrude","SWEPT_FACE",FACE,{"disambiguationData":[OSD([sQuery(id+"F2.wireOp",EDGE,"E37.3")])]})]}),makeQuery(id+"F3.boolean.opBoolean","INTERSECT",EDGE,{"derivedFrom":[subQ2,makeQuery(id+"F3.opExtrude","SWEPT_FACE",FACE,{"disambiguationData":[OSD([sQuery(id+"F2.wireOp",EDGE,"E37.4")])]})]}),makeQuery(id+"F3.boolean.opBoolean","INTERSECT",EDGE,{"derivedFrom":[subQ2,makeQuery(id+"F3.opExtrude","SWEPT_FACE",FACE,{"disambiguationData":[OSD([sQuery(id+"F2.wireOp",EDGE,"E37.5")])]})]}),makeQuery(id+"F3.boolean.opBoolean","INTERSECT",EDGE,{"derivedFrom":[subQ2,makeQuery(id+"F3.opExtrude","SWEPT_FACE",FACE,{"disambiguationData":[OSD([sQuery(id+"F2.wireOp",EDGE,"E38.0")])]})]}),makeQuery(id+"F3.boolean.opBoolean","INTERSECT",EDGE,{"derivedFrom":[subQ2,makeQuery(id+"F3.opExtrude","SWEPT_FACE",FACE,{"disambiguationData":[OSD([sQuery(id+"F2.wireOp",EDGE,"E38.1")])]})]}),makeQuery(id+"F3.boolean.opBoolean","INTERSECT",EDGE,{"derivedFrom":[subQ2,makeQuery(id+"F3.opExtrude","SWEPT_FACE",FACE,{"disambiguationData":[OSD([sQuery(id+"F2.wireOp",EDGE,"E38.2")])]})]}),makeQuery(id+"F3.boolean.opBoolean","INTERSECT",EDGE,{"derivedFrom":[subQ2,makeQuery(id+"F3.opExtrude","SWEPT_FACE",FACE,{"disambiguationData":[OSD([sQuery(id+"F2.wireOp",EDGE,"E38.3")])]})]}),makeQuery(id+"F3.boolean.opBoolean","INTERSECT",EDGE,{"derivedFrom":[subQ2,makeQuery(id+"F3.opExtrude","SWEPT_FACE",FACE,{"disambiguationData":[OSD([sQuery(id+"F2.wireOp",EDGE,"E38.4")])]})]}),makeQuery(id+"F3.boolean.opBoolean","INTERSECT",EDGE,{"derivedFrom":[subQ2,makeQuery(id+"F3.opExtrude","SWEPT_FACE",FACE,{"disambiguationData":[OSD([sQuery(id+"F2.wireOp",EDGE,"E38.5")])]})]})]);}
            var Q20;
            {var subQ0=sQuery(id+"F0.wireOp",EDGE,"E6");var subQ1=sQuery(id+"F0.wireOp",EDGE,"E18.top");var subQ2=makeQuery(id+"F1.opExtrude","SWEPT_FACE",FACE,{"disambiguationData":[OSD([subQ0]),TDD([makeQuery(id+"F0.imprint","IMPRINT",EDGE,{"disambiguationData":[TD([[makeQuery(id+"F0.imprint","INTERSECT",VERTEX,{"derivedFrom":[subQ0,sQuery(id+"F0.wireOp",EDGE,"E9")]}),1.0]])],"derivedFrom":subQ0})])]});var subQ4=makeQuery(id+"F1.opExtrude","SWEPT_FACE",FACE,{"disambiguationData":[OSD([subQ0]),TDD([makeQuery(id+"F0.imprint","IMPRINT",EDGE,{"disambiguationData":[TD([[makeQuery(id+"F0.imprint","INTERSECT",VERTEX,{"derivedFrom":[subQ0,subQ1,sQuery(id+"F0.wireOp",EDGE,"E18.right")]}),1.0]])],"derivedFrom":subQ0})])]});var subQ5=makeQuery(id+"F1.opExtrude","SWEPT_FACE",FACE,{"disambiguationData":[OSD([subQ0]),TDD([makeQuery(id+"F0.imprint","IMPRINT",EDGE,{"disambiguationData":[TD([[makeQuery(id+"F0.imprint","INTERSECT",VERTEX,{"derivedFrom":[subQ0,sQuery(id+"F0.wireOp",EDGE,"E12")]}),-1.0]])],"derivedFrom":subQ0})])]});Q20=qUnion([makeQuery(id+"F3.boolean.opBoolean","INTERSECT",EDGE,{"derivedFrom":[subQ5,makeQuery(id+"F3.opExtrude","SWEPT_FACE",FACE,{"disambiguationData":[OSD([sQuery(id+"F2.wireOp",EDGE,"E41.0")])]})]}),makeQuery(id+"F3.boolean.opBoolean","INTERSECT",EDGE,{"derivedFrom":[subQ5,makeQuery(id+"F3.opExtrude","SWEPT_FACE",FACE,{"disambiguationData":[OSD([sQuery(id+"F2.wireOp",EDGE,"E41.1")])]})]}),makeQuery(id+"F3.boolean.opBoolean","INTERSECT",EDGE,{"derivedFrom":[subQ5,makeQuery(id+"F3.opExtrude","SWEPT_FACE",FACE,{"disambiguationData":[OSD([sQuery(id+"F2.wireOp",EDGE,"E41.2")])]})]}),makeQuery(id+"F3.boolean.opBoolean","INTERSECT",EDGE,{"derivedFrom":[subQ5,makeQuery(id+"F3.opExtrude","SWEPT_FACE",FACE,{"disambiguationData":[OSD([sQuery(id+"F2.wireOp",EDGE,"E41.3")])]})]}),makeQuery(id+"F3.boolean.opBoolean","INTERSECT",EDGE,{"derivedFrom":[subQ5,makeQuery(id+"F3.opExtrude","SWEPT_FACE",FACE,{"disambiguationData":[OSD([sQuery(id+"F2.wireOp",EDGE,"E41.4")])]})]}),makeQuery(id+"F3.boolean.opBoolean","INTERSECT",EDGE,{"derivedFrom":[subQ5,makeQuery(id+"F3.opExtrude","SWEPT_FACE",FACE,{"disambiguationData":[OSD([sQuery(id+"F2.wireOp",EDGE,"E41.5")])]})]}),makeQuery(id+"F3.boolean.opBoolean","INTERSECT",EDGE,{"derivedFrom":[subQ5,makeQuery(id+"F3.opExtrude","SWEPT_FACE",FACE,{"disambiguationData":[OSD([sQuery(id+"F2.wireOp",EDGE,"E42.0")])]})]}),makeQuery(id+"F3.boolean.opBoolean","INTERSECT",EDGE,{"derivedFrom":[subQ5,makeQuery(id+"F3.opExtrude","SWEPT_FACE",FACE,{"disambiguationData":[OSD([sQuery(id+"F2.wireOp",EDGE,"E42.1")])]})]}),makeQuery(id+"F3.boolean.opBoolean","INTERSECT",EDGE,{"derivedFrom":[subQ5,makeQuery(id+"F3.opExtrude","SWEPT_FACE",FACE,{"disambiguationData":[OSD([sQuery(id+"F2.wireOp",EDGE,"E42.2")])]})]}),makeQuery(id+"F3.boolean.opBoolean","INTERSECT",EDGE,{"derivedFrom":[subQ5,makeQuery(id+"F3.opExtrude","SWEPT_FACE",FACE,{"disambiguationData":[OSD([sQuery(id+"F2.wireOp",EDGE,"E42.3")])]})]}),makeQuery(id+"F3.boolean.opBoolean","INTERSECT",EDGE,{"derivedFrom":[subQ5,makeQuery(id+"F3.opExtrude","SWEPT_FACE",FACE,{"disambiguationData":[OSD([sQuery(id+"F2.wireOp",EDGE,"E42.4")])]})]}),makeQuery(id+"F3.boolean.opBoolean","INTERSECT",EDGE,{"derivedFrom":[subQ5,makeQuery(id+"F3.opExtrude","SWEPT_FACE",FACE,{"disambiguationData":[OSD([sQuery(id+"F2.wireOp",EDGE,"E42.5")])]})]}),makeQuery(id+"F3.boolean.opBoolean","INTERSECT",EDGE,{"derivedFrom":[subQ4,makeQuery(id+"F3.opExtrude","SWEPT_FACE",FACE,{"disambiguationData":[OSD([sQuery(id+"F2.wireOp",EDGE,"E39.0")])]})]}),makeQuery(id+"F3.boolean.opBoolean","INTERSECT",EDGE,{"derivedFrom":[subQ4,makeQuery(id+"F3.opExtrude","SWEPT_FACE",FACE,{"disambiguationData":[OSD([sQuery(id+"F2.wireOp",EDGE,"E39.1")])]})]}),makeQuery(id+"F3.boolean.opBoolean","INTERSECT",EDGE,{"derivedFrom":[subQ4,makeQuery(id+"F3.opExtrude","SWEPT_FACE",FACE,{"disambiguationData":[OSD([sQuery(id+"F2.wireOp",EDGE,"E39.2")])]})]}),makeQuery(id+"F3.boolean.opBoolean","INTERSECT",EDGE,{"derivedFrom":[subQ4,makeQuery(id+"F3.opExtrude","SWEPT_FACE",FACE,{"disambiguationData":[OSD([sQuery(id+"F2.wireOp",EDGE,"E39.3")])]})]}),makeQuery(id+"F3.boolean.opBoolean","INTERSECT",EDGE,{"derivedFrom":[subQ4,makeQuery(id+"F3.opExtrude","SWEPT_FACE",FACE,{"disambiguationData":[OSD([sQuery(id+"F2.wireOp",EDGE,"E39.4")])]})]}),makeQuery(id+"F3.boolean.opBoolean","INTERSECT",EDGE,{"derivedFrom":[subQ4,makeQuery(id+"F3.opExtrude","SWEPT_FACE",FACE,{"disambiguationData":[OSD([sQuery(id+"F2.wireOp",EDGE,"E39.5")])]})]}),makeQuery(id+"F3.boolean.opBoolean","INTERSECT",EDGE,{"derivedFrom":[subQ4,makeQuery(id+"F3.opExtrude","SWEPT_FACE",FACE,{"disambiguationData":[OSD([sQuery(id+"F2.wireOp",EDGE,"E40.0")])]})]}),makeQuery(id+"F3.boolean.opBoolean","INTERSECT",EDGE,{"derivedFrom":[subQ4,makeQuery(id+"F3.opExtrude","SWEPT_FACE",FACE,{"disambiguationData":[OSD([sQuery(id+"F2.wireOp",EDGE,"E40.1")])]})]}),makeQuery(id+"F3.boolean.opBoolean","INTERSECT",EDGE,{"derivedFrom":[subQ4,makeQuery(id+"F3.opExtrude","SWEPT_FACE",FACE,{"disambiguationData":[OSD([sQuery(id+"F2.wireOp",EDGE,"E40.2")])]})]}),makeQuery(id+"F3.boolean.opBoolean","INTERSECT",EDGE,{"derivedFrom":[subQ4,makeQuery(id+"F3.opExtrude","SWEPT_FACE",FACE,{"disambiguationData":[OSD([sQuery(id+"F2.wireOp",EDGE,"E40.3")])]})]}),makeQuery(id+"F3.boolean.opBoolean","INTERSECT",EDGE,{"derivedFrom":[subQ4,makeQuery(id+"F3.opExtrude","SWEPT_FACE",FACE,{"disambiguationData":[OSD([sQuery(id+"F2.wireOp",EDGE,"E40.4")])]})]}),makeQuery(id+"F3.boolean.opBoolean","INTERSECT",EDGE,{"derivedFrom":[subQ4,makeQuery(id+"F3.opExtrude","SWEPT_FACE",FACE,{"disambiguationData":[OSD([sQuery(id+"F2.wireOp",EDGE,"E40.5")])]})]}),makeQuery(id+"F3.boolean.opBoolean","INTERSECT",EDGE,{"derivedFrom":[subQ2,makeQuery(id+"F3.opExtrude","SWEPT_FACE",FACE,{"disambiguationData":[OSD([sQuery(id+"F2.wireOp",EDGE,"E36.0")])]})]}),makeQuery(id+"F3.boolean.opBoolean","INTERSECT",EDGE,{"derivedFrom":[subQ2,makeQuery(id+"F3.opExtrude","SWEPT_FACE",FACE,{"disambiguationData":[OSD([sQuery(id+"F2.wireOp",EDGE,"E36.1")])]})]}),makeQuery(id+"F3.boolean.opBoolean","INTERSECT",EDGE,{"derivedFrom":[subQ2,makeQuery(id+"F3.opExtrude","SWEPT_FACE",FACE,{"disambiguationData":[OSD([sQuery(id+"F2.wireOp",EDGE,"E36.2")])]})]}),makeQuery(id+"F3.boolean.opBoolean","INTERSECT",EDGE,{"derivedFrom":[subQ2,makeQuery(id+"F3.opExtrude","SWEPT_FACE",FACE,{"disambiguationData":[OSD([sQuery(id+"F2.wireOp",EDGE,"E36.3")])]})]}),makeQuery(id+"F3.boolean.opBoolean","INTERSECT",EDGE,{"derivedFrom":[subQ2,makeQuery(id+"F3.opExtrude","SWEPT_FACE",FACE,{"disambiguationData":[OSD([sQuery(id+"F2.wireOp",EDGE,"E36.4")])]})]}),makeQuery(id+"F3.boolean.opBoolean","INTERSECT",EDGE,{"derivedFrom":[subQ2,makeQuery(id+"F3.opExtrude","SWEPT_FACE",FACE,{"disambiguationData":[OSD([sQuery(id+"F2.wireOp",EDGE,"E36.5")])]})]}),makeQuery(id+"F3.boolean.opBoolean","INTERSECT",EDGE,{"derivedFrom":[subQ2,makeQuery(id+"F3.opExtrude","SWEPT_FACE",FACE,{"disambiguationData":[OSD([sQuery(id+"F2.wireOp",EDGE,"E37.0")])]})]}),makeQuery(id+"F3.boolean.opBoolean","INTERSECT",EDGE,{"derivedFrom":[subQ2,makeQuery(id+"F3.opExtrude","SWEPT_FACE",FACE,{"disambiguationData":[OSD([sQuery(id+"F2.wireOp",EDGE,"E37.1")])]})]}),makeQuery(id+"F3.boolean.opBoolean","INTERSECT",EDGE,{"derivedFrom":[subQ2,makeQuery(id+"F3.opExtrude","SWEPT_FACE",FACE,{"disambiguationData":[OSD([sQuery(id+"F2.wireOp",EDGE,"E37.2")])]})]}),makeQuery(id+"F3.boolean.opBoolean","INTERSECT",EDGE,{"derivedFrom":[subQ2,makeQuery(id+"F3.opExtrude","SWEPT_FACE",FACE,{"disambiguationData":[OSD([sQuery(id+"F2.wireOp",EDGE,"E37.3")])]})]}),makeQuery(id+"F3.boolean.opBoolean","INTERSECT",EDGE,{"derivedFrom":[subQ2,makeQuery(id+"F3.opExtrude","SWEPT_FACE",FACE,{"disambiguationData":[OSD([sQuery(id+"F2.wireOp",EDGE,"E37.4")])]})]}),makeQuery(id+"F3.boolean.opBoolean","INTERSECT",EDGE,{"derivedFrom":[subQ2,makeQuery(id+"F3.opExtrude","SWEPT_FACE",FACE,{"disambiguationData":[OSD([sQuery(id+"F2.wireOp",EDGE,"E37.5")])]})]}),makeQuery(id+"F3.boolean.opBoolean","INTERSECT",EDGE,{"derivedFrom":[subQ2,makeQuery(id+"F3.opExtrude","SWEPT_FACE",FACE,{"disambiguationData":[OSD([sQuery(id+"F2.wireOp",EDGE,"E38.0")])]})]}),makeQuery(id+"F3.boolean.opBoolean","INTERSECT",EDGE,{"derivedFrom":[subQ2,makeQuery(id+"F3.opExtrude","SWEPT_FACE",FACE,{"disambiguationData":[OSD([sQuery(id+"F2.wireOp",EDGE,"E38.1")])]})]}),makeQuery(id+"F3.boolean.opBoolean","INTERSECT",EDGE,{"derivedFrom":[subQ2,makeQuery(id+"F3.opExtrude","SWEPT_FACE",FACE,{"disambiguationData":[OSD([sQuery(id+"F2.wireOp",EDGE,"E38.2")])]})]}),makeQuery(id+"F3.boolean.opBoolean","INTERSECT",EDGE,{"derivedFrom":[subQ2,makeQuery(id+"F3.opExtrude","SWEPT_FACE",FACE,{"disambiguationData":[OSD([sQuery(id+"F2.wireOp",EDGE,"E38.3")])]})]}),makeQuery(id+"F3.boolean.opBoolean","INTERSECT",EDGE,{"derivedFrom":[subQ2,makeQuery(id+"F3.opExtrude","SWEPT_FACE",FACE,{"disambiguationData":[OSD([sQuery(id+"F2.wireOp",EDGE,"E38.4")])]})]}),makeQuery(id+"F3.boolean.opBoolean","INTERSECT",EDGE,{"derivedFrom":[subQ2,makeQuery(id+"F3.opExtrude","SWEPT_FACE",FACE,{"disambiguationData":[OSD([sQuery(id+"F2.wireOp",EDGE,"E38.5")])]})]})]);}
            var Q21;
            {var subQ0=sQuery(id+"F0.wireOp",EDGE,"E6");var subQ1=sQuery(id+"F0.wireOp",EDGE,"E18.top");var subQ2=makeQuery(id+"F1.opExtrude","SWEPT_FACE",FACE,{"disambiguationData":[OSD([subQ0]),TDD([makeQuery(id+"F0.imprint","IMPRINT",EDGE,{"disambiguationData":[TD([[makeQuery(id+"F0.imprint","INTERSECT",VERTEX,{"derivedFrom":[subQ0,sQuery(id+"F0.wireOp",EDGE,"E9")]}),1.0]])],"derivedFrom":subQ0})])]});var subQ4=makeQuery(id+"F1.opExtrude","SWEPT_FACE",FACE,{"disambiguationData":[OSD([subQ0]),TDD([makeQuery(id+"F0.imprint","IMPRINT",EDGE,{"disambiguationData":[TD([[makeQuery(id+"F0.imprint","INTERSECT",VERTEX,{"derivedFrom":[subQ0,subQ1,sQuery(id+"F0.wireOp",EDGE,"E18.right")]}),1.0]])],"derivedFrom":subQ0})])]});var subQ5=makeQuery(id+"F1.opExtrude","SWEPT_FACE",FACE,{"disambiguationData":[OSD([subQ0]),TDD([makeQuery(id+"F0.imprint","IMPRINT",EDGE,{"disambiguationData":[TD([[makeQuery(id+"F0.imprint","INTERSECT",VERTEX,{"derivedFrom":[subQ0,sQuery(id+"F0.wireOp",EDGE,"E12")]}),-1.0]])],"derivedFrom":subQ0})])]});Q21=qUnion([makeQuery(id+"F3.boolean.opBoolean","INTERSECT",EDGE,{"derivedFrom":[subQ5,makeQuery(id+"F3.opExtrude","SWEPT_FACE",FACE,{"disambiguationData":[OSD([sQuery(id+"F2.wireOp",EDGE,"E41.0")])]})]}),makeQuery(id+"F3.boolean.opBoolean","INTERSECT",EDGE,{"derivedFrom":[subQ5,makeQuery(id+"F3.opExtrude","SWEPT_FACE",FACE,{"disambiguationData":[OSD([sQuery(id+"F2.wireOp",EDGE,"E41.1")])]})]}),makeQuery(id+"F3.boolean.opBoolean","INTERSECT",EDGE,{"derivedFrom":[subQ5,makeQuery(id+"F3.opExtrude","SWEPT_FACE",FACE,{"disambiguationData":[OSD([sQuery(id+"F2.wireOp",EDGE,"E41.2")])]})]}),makeQuery(id+"F3.boolean.opBoolean","INTERSECT",EDGE,{"derivedFrom":[subQ5,makeQuery(id+"F3.opExtrude","SWEPT_FACE",FACE,{"disambiguationData":[OSD([sQuery(id+"F2.wireOp",EDGE,"E41.3")])]})]}),makeQuery(id+"F3.boolean.opBoolean","INTERSECT",EDGE,{"derivedFrom":[subQ5,makeQuery(id+"F3.opExtrude","SWEPT_FACE",FACE,{"disambiguationData":[OSD([sQuery(id+"F2.wireOp",EDGE,"E41.4")])]})]}),makeQuery(id+"F3.boolean.opBoolean","INTERSECT",EDGE,{"derivedFrom":[subQ5,makeQuery(id+"F3.opExtrude","SWEPT_FACE",FACE,{"disambiguationData":[OSD([sQuery(id+"F2.wireOp",EDGE,"E41.5")])]})]}),makeQuery(id+"F3.boolean.opBoolean","INTERSECT",EDGE,{"derivedFrom":[subQ5,makeQuery(id+"F3.opExtrude","SWEPT_FACE",FACE,{"disambiguationData":[OSD([sQuery(id+"F2.wireOp",EDGE,"E42.0")])]})]}),makeQuery(id+"F3.boolean.opBoolean","INTERSECT",EDGE,{"derivedFrom":[subQ5,makeQuery(id+"F3.opExtrude","SWEPT_FACE",FACE,{"disambiguationData":[OSD([sQuery(id+"F2.wireOp",EDGE,"E42.1")])]})]}),makeQuery(id+"F3.boolean.opBoolean","INTERSECT",EDGE,{"derivedFrom":[subQ5,makeQuery(id+"F3.opExtrude","SWEPT_FACE",FACE,{"disambiguationData":[OSD([sQuery(id+"F2.wireOp",EDGE,"E42.2")])]})]}),makeQuery(id+"F3.boolean.opBoolean","INTERSECT",EDGE,{"derivedFrom":[subQ5,makeQuery(id+"F3.opExtrude","SWEPT_FACE",FACE,{"disambiguationData":[OSD([sQuery(id+"F2.wireOp",EDGE,"E42.3")])]})]}),makeQuery(id+"F3.boolean.opBoolean","INTERSECT",EDGE,{"derivedFrom":[subQ5,makeQuery(id+"F3.opExtrude","SWEPT_FACE",FACE,{"disambiguationData":[OSD([sQuery(id+"F2.wireOp",EDGE,"E42.4")])]})]}),makeQuery(id+"F3.boolean.opBoolean","INTERSECT",EDGE,{"derivedFrom":[subQ5,makeQuery(id+"F3.opExtrude","SWEPT_FACE",FACE,{"disambiguationData":[OSD([sQuery(id+"F2.wireOp",EDGE,"E42.5")])]})]}),makeQuery(id+"F3.boolean.opBoolean","INTERSECT",EDGE,{"derivedFrom":[subQ4,makeQuery(id+"F3.opExtrude","SWEPT_FACE",FACE,{"disambiguationData":[OSD([sQuery(id+"F2.wireOp",EDGE,"E39.0")])]})]}),makeQuery(id+"F3.boolean.opBoolean","INTERSECT",EDGE,{"derivedFrom":[subQ4,makeQuery(id+"F3.opExtrude","SWEPT_FACE",FACE,{"disambiguationData":[OSD([sQuery(id+"F2.wireOp",EDGE,"E39.1")])]})]}),makeQuery(id+"F3.boolean.opBoolean","INTERSECT",EDGE,{"derivedFrom":[subQ4,makeQuery(id+"F3.opExtrude","SWEPT_FACE",FACE,{"disambiguationData":[OSD([sQuery(id+"F2.wireOp",EDGE,"E39.2")])]})]}),makeQuery(id+"F3.boolean.opBoolean","INTERSECT",EDGE,{"derivedFrom":[subQ4,makeQuery(id+"F3.opExtrude","SWEPT_FACE",FACE,{"disambiguationData":[OSD([sQuery(id+"F2.wireOp",EDGE,"E39.3")])]})]}),makeQuery(id+"F3.boolean.opBoolean","INTERSECT",EDGE,{"derivedFrom":[subQ4,makeQuery(id+"F3.opExtrude","SWEPT_FACE",FACE,{"disambiguationData":[OSD([sQuery(id+"F2.wireOp",EDGE,"E39.4")])]})]}),makeQuery(id+"F3.boolean.opBoolean","INTERSECT",EDGE,{"derivedFrom":[subQ4,makeQuery(id+"F3.opExtrude","SWEPT_FACE",FACE,{"disambiguationData":[OSD([sQuery(id+"F2.wireOp",EDGE,"E39.5")])]})]}),makeQuery(id+"F3.boolean.opBoolean","INTERSECT",EDGE,{"derivedFrom":[subQ4,makeQuery(id+"F3.opExtrude","SWEPT_FACE",FACE,{"disambiguationData":[OSD([sQuery(id+"F2.wireOp",EDGE,"E40.0")])]})]}),makeQuery(id+"F3.boolean.opBoolean","INTERSECT",EDGE,{"derivedFrom":[subQ4,makeQuery(id+"F3.opExtrude","SWEPT_FACE",FACE,{"disambiguationData":[OSD([sQuery(id+"F2.wireOp",EDGE,"E40.1")])]})]}),makeQuery(id+"F3.boolean.opBoolean","INTERSECT",EDGE,{"derivedFrom":[subQ4,makeQuery(id+"F3.opExtrude","SWEPT_FACE",FACE,{"disambiguationData":[OSD([sQuery(id+"F2.wireOp",EDGE,"E40.2")])]})]}),makeQuery(id+"F3.boolean.opBoolean","INTERSECT",EDGE,{"derivedFrom":[subQ4,makeQuery(id+"F3.opExtrude","SWEPT_FACE",FACE,{"disambiguationData":[OSD([sQuery(id+"F2.wireOp",EDGE,"E40.3")])]})]}),makeQuery(id+"F3.boolean.opBoolean","INTERSECT",EDGE,{"derivedFrom":[subQ4,makeQuery(id+"F3.opExtrude","SWEPT_FACE",FACE,{"disambiguationData":[OSD([sQuery(id+"F2.wireOp",EDGE,"E40.4")])]})]}),makeQuery(id+"F3.boolean.opBoolean","INTERSECT",EDGE,{"derivedFrom":[subQ4,makeQuery(id+"F3.opExtrude","SWEPT_FACE",FACE,{"disambiguationData":[OSD([sQuery(id+"F2.wireOp",EDGE,"E40.5")])]})]}),makeQuery(id+"F3.boolean.opBoolean","INTERSECT",EDGE,{"derivedFrom":[subQ2,makeQuery(id+"F3.opExtrude","SWEPT_FACE",FACE,{"disambiguationData":[OSD([sQuery(id+"F2.wireOp",EDGE,"E36.0")])]})]}),makeQuery(id+"F3.boolean.opBoolean","INTERSECT",EDGE,{"derivedFrom":[subQ2,makeQuery(id+"F3.opExtrude","SWEPT_FACE",FACE,{"disambiguationData":[OSD([sQuery(id+"F2.wireOp",EDGE,"E36.1")])]})]}),makeQuery(id+"F3.boolean.opBoolean","INTERSECT",EDGE,{"derivedFrom":[subQ2,makeQuery(id+"F3.opExtrude","SWEPT_FACE",FACE,{"disambiguationData":[OSD([sQuery(id+"F2.wireOp",EDGE,"E36.2")])]})]}),makeQuery(id+"F3.boolean.opBoolean","INTERSECT",EDGE,{"derivedFrom":[subQ2,makeQuery(id+"F3.opExtrude","SWEPT_FACE",FACE,{"disambiguationData":[OSD([sQuery(id+"F2.wireOp",EDGE,"E36.3")])]})]}),makeQuery(id+"F3.boolean.opBoolean","INTERSECT",EDGE,{"derivedFrom":[subQ2,makeQuery(id+"F3.opExtrude","SWEPT_FACE",FACE,{"disambiguationData":[OSD([sQuery(id+"F2.wireOp",EDGE,"E36.4")])]})]}),makeQuery(id+"F3.boolean.opBoolean","INTERSECT",EDGE,{"derivedFrom":[subQ2,makeQuery(id+"F3.opExtrude","SWEPT_FACE",FACE,{"disambiguationData":[OSD([sQuery(id+"F2.wireOp",EDGE,"E36.5")])]})]}),makeQuery(id+"F3.boolean.opBoolean","INTERSECT",EDGE,{"derivedFrom":[subQ2,makeQuery(id+"F3.opExtrude","SWEPT_FACE",FACE,{"disambiguationData":[OSD([sQuery(id+"F2.wireOp",EDGE,"E37.0")])]})]}),makeQuery(id+"F3.boolean.opBoolean","INTERSECT",EDGE,{"derivedFrom":[subQ2,makeQuery(id+"F3.opExtrude","SWEPT_FACE",FACE,{"disambiguationData":[OSD([sQuery(id+"F2.wireOp",EDGE,"E37.1")])]})]}),makeQuery(id+"F3.boolean.opBoolean","INTERSECT",EDGE,{"derivedFrom":[subQ2,makeQuery(id+"F3.opExtrude","SWEPT_FACE",FACE,{"disambiguationData":[OSD([sQuery(id+"F2.wireOp",EDGE,"E37.2")])]})]}),makeQuery(id+"F3.boolean.opBoolean","INTERSECT",EDGE,{"derivedFrom":[subQ2,makeQuery(id+"F3.opExtrude","SWEPT_FACE",FACE,{"disambiguationData":[OSD([sQuery(id+"F2.wireOp",EDGE,"E37.3")])]})]}),makeQuery(id+"F3.boolean.opBoolean","INTERSECT",EDGE,{"derivedFrom":[subQ2,makeQuery(id+"F3.opExtrude","SWEPT_FACE",FACE,{"disambiguationData":[OSD([sQuery(id+"F2.wireOp",EDGE,"E37.4")])]})]}),makeQuery(id+"F3.boolean.opBoolean","INTERSECT",EDGE,{"derivedFrom":[subQ2,makeQuery(id+"F3.opExtrude","SWEPT_FACE",FACE,{"disambiguationData":[OSD([sQuery(id+"F2.wireOp",EDGE,"E37.5")])]})]}),makeQuery(id+"F3.boolean.opBoolean","INTERSECT",EDGE,{"derivedFrom":[subQ2,makeQuery(id+"F3.opExtrude","SWEPT_FACE",FACE,{"disambiguationData":[OSD([sQuery(id+"F2.wireOp",EDGE,"E38.0")])]})]}),makeQuery(id+"F3.boolean.opBoolean","INTERSECT",EDGE,{"derivedFrom":[subQ2,makeQuery(id+"F3.opExtrude","SWEPT_FACE",FACE,{"disambiguationData":[OSD([sQuery(id+"F2.wireOp",EDGE,"E38.1")])]})]}),makeQuery(id+"F3.boolean.opBoolean","INTERSECT",EDGE,{"derivedFrom":[subQ2,makeQuery(id+"F3.opExtrude","SWEPT_FACE",FACE,{"disambiguationData":[OSD([sQuery(id+"F2.wireOp",EDGE,"E38.2")])]})]}),makeQuery(id+"F3.boolean.opBoolean","INTERSECT",EDGE,{"derivedFrom":[subQ2,makeQuery(id+"F3.opExtrude","SWEPT_FACE",FACE,{"disambiguationData":[OSD([sQuery(id+"F2.wireOp",EDGE,"E38.3")])]})]}),makeQuery(id+"F3.boolean.opBoolean","INTERSECT",EDGE,{"derivedFrom":[subQ2,makeQuery(id+"F3.opExtrude","SWEPT_FACE",FACE,{"disambiguationData":[OSD([sQuery(id+"F2.wireOp",EDGE,"E38.4")])]})]}),makeQuery(id+"F3.boolean.opBoolean","INTERSECT",EDGE,{"derivedFrom":[subQ2,makeQuery(id+"F3.opExtrude","SWEPT_FACE",FACE,{"disambiguationData":[OSD([sQuery(id+"F2.wireOp",EDGE,"E38.5")])]})]})]);}
            var Q22;
            {var subQ0=sQuery(id+"F0.wireOp",EDGE,"E6");var subQ1=sQuery(id+"F0.wireOp",EDGE,"E18.top");var subQ2=makeQuery(id+"F1.opExtrude","SWEPT_FACE",FACE,{"disambiguationData":[OSD([subQ0]),TDD([makeQuery(id+"F0.imprint","IMPRINT",EDGE,{"disambiguationData":[TD([[makeQuery(id+"F0.imprint","INTERSECT",VERTEX,{"derivedFrom":[subQ0,sQuery(id+"F0.wireOp",EDGE,"E9")]}),1.0]])],"derivedFrom":subQ0})])]});var subQ4=makeQuery(id+"F1.opExtrude","SWEPT_FACE",FACE,{"disambiguationData":[OSD([subQ0]),TDD([makeQuery(id+"F0.imprint","IMPRINT",EDGE,{"disambiguationData":[TD([[makeQuery(id+"F0.imprint","INTERSECT",VERTEX,{"derivedFrom":[subQ0,subQ1,sQuery(id+"F0.wireOp",EDGE,"E18.right")]}),1.0]])],"derivedFrom":subQ0})])]});var subQ5=makeQuery(id+"F1.opExtrude","SWEPT_FACE",FACE,{"disambiguationData":[OSD([subQ0]),TDD([makeQuery(id+"F0.imprint","IMPRINT",EDGE,{"disambiguationData":[TD([[makeQuery(id+"F0.imprint","INTERSECT",VERTEX,{"derivedFrom":[subQ0,sQuery(id+"F0.wireOp",EDGE,"E12")]}),-1.0]])],"derivedFrom":subQ0})])]});Q22=qUnion([makeQuery(id+"F3.boolean.opBoolean","INTERSECT",EDGE,{"derivedFrom":[subQ5,makeQuery(id+"F3.opExtrude","SWEPT_FACE",FACE,{"disambiguationData":[OSD([sQuery(id+"F2.wireOp",EDGE,"E41.0")])]})]}),makeQuery(id+"F3.boolean.opBoolean","INTERSECT",EDGE,{"derivedFrom":[subQ5,makeQuery(id+"F3.opExtrude","SWEPT_FACE",FACE,{"disambiguationData":[OSD([sQuery(id+"F2.wireOp",EDGE,"E41.1")])]})]}),makeQuery(id+"F3.boolean.opBoolean","INTERSECT",EDGE,{"derivedFrom":[subQ5,makeQuery(id+"F3.opExtrude","SWEPT_FACE",FACE,{"disambiguationData":[OSD([sQuery(id+"F2.wireOp",EDGE,"E41.2")])]})]}),makeQuery(id+"F3.boolean.opBoolean","INTERSECT",EDGE,{"derivedFrom":[subQ5,makeQuery(id+"F3.opExtrude","SWEPT_FACE",FACE,{"disambiguationData":[OSD([sQuery(id+"F2.wireOp",EDGE,"E41.3")])]})]}),makeQuery(id+"F3.boolean.opBoolean","INTERSECT",EDGE,{"derivedFrom":[subQ5,makeQuery(id+"F3.opExtrude","SWEPT_FACE",FACE,{"disambiguationData":[OSD([sQuery(id+"F2.wireOp",EDGE,"E41.4")])]})]}),makeQuery(id+"F3.boolean.opBoolean","INTERSECT",EDGE,{"derivedFrom":[subQ5,makeQuery(id+"F3.opExtrude","SWEPT_FACE",FACE,{"disambiguationData":[OSD([sQuery(id+"F2.wireOp",EDGE,"E41.5")])]})]}),makeQuery(id+"F3.boolean.opBoolean","INTERSECT",EDGE,{"derivedFrom":[subQ5,makeQuery(id+"F3.opExtrude","SWEPT_FACE",FACE,{"disambiguationData":[OSD([sQuery(id+"F2.wireOp",EDGE,"E42.0")])]})]}),makeQuery(id+"F3.boolean.opBoolean","INTERSECT",EDGE,{"derivedFrom":[subQ5,makeQuery(id+"F3.opExtrude","SWEPT_FACE",FACE,{"disambiguationData":[OSD([sQuery(id+"F2.wireOp",EDGE,"E42.1")])]})]}),makeQuery(id+"F3.boolean.opBoolean","INTERSECT",EDGE,{"derivedFrom":[subQ5,makeQuery(id+"F3.opExtrude","SWEPT_FACE",FACE,{"disambiguationData":[OSD([sQuery(id+"F2.wireOp",EDGE,"E42.2")])]})]}),makeQuery(id+"F3.boolean.opBoolean","INTERSECT",EDGE,{"derivedFrom":[subQ5,makeQuery(id+"F3.opExtrude","SWEPT_FACE",FACE,{"disambiguationData":[OSD([sQuery(id+"F2.wireOp",EDGE,"E42.3")])]})]}),makeQuery(id+"F3.boolean.opBoolean","INTERSECT",EDGE,{"derivedFrom":[subQ5,makeQuery(id+"F3.opExtrude","SWEPT_FACE",FACE,{"disambiguationData":[OSD([sQuery(id+"F2.wireOp",EDGE,"E42.4")])]})]}),makeQuery(id+"F3.boolean.opBoolean","INTERSECT",EDGE,{"derivedFrom":[subQ5,makeQuery(id+"F3.opExtrude","SWEPT_FACE",FACE,{"disambiguationData":[OSD([sQuery(id+"F2.wireOp",EDGE,"E42.5")])]})]}),makeQuery(id+"F3.boolean.opBoolean","INTERSECT",EDGE,{"derivedFrom":[subQ4,makeQuery(id+"F3.opExtrude","SWEPT_FACE",FACE,{"disambiguationData":[OSD([sQuery(id+"F2.wireOp",EDGE,"E39.0")])]})]}),makeQuery(id+"F3.boolean.opBoolean","INTERSECT",EDGE,{"derivedFrom":[subQ4,makeQuery(id+"F3.opExtrude","SWEPT_FACE",FACE,{"disambiguationData":[OSD([sQuery(id+"F2.wireOp",EDGE,"E39.1")])]})]}),makeQuery(id+"F3.boolean.opBoolean","INTERSECT",EDGE,{"derivedFrom":[subQ4,makeQuery(id+"F3.opExtrude","SWEPT_FACE",FACE,{"disambiguationData":[OSD([sQuery(id+"F2.wireOp",EDGE,"E39.2")])]})]}),makeQuery(id+"F3.boolean.opBoolean","INTERSECT",EDGE,{"derivedFrom":[subQ4,makeQuery(id+"F3.opExtrude","SWEPT_FACE",FACE,{"disambiguationData":[OSD([sQuery(id+"F2.wireOp",EDGE,"E39.3")])]})]}),makeQuery(id+"F3.boolean.opBoolean","INTERSECT",EDGE,{"derivedFrom":[subQ4,makeQuery(id+"F3.opExtrude","SWEPT_FACE",FACE,{"disambiguationData":[OSD([sQuery(id+"F2.wireOp",EDGE,"E39.4")])]})]}),makeQuery(id+"F3.boolean.opBoolean","INTERSECT",EDGE,{"derivedFrom":[subQ4,makeQuery(id+"F3.opExtrude","SWEPT_FACE",FACE,{"disambiguationData":[OSD([sQuery(id+"F2.wireOp",EDGE,"E39.5")])]})]}),makeQuery(id+"F3.boolean.opBoolean","INTERSECT",EDGE,{"derivedFrom":[subQ4,makeQuery(id+"F3.opExtrude","SWEPT_FACE",FACE,{"disambiguationData":[OSD([sQuery(id+"F2.wireOp",EDGE,"E40.0")])]})]}),makeQuery(id+"F3.boolean.opBoolean","INTERSECT",EDGE,{"derivedFrom":[subQ4,makeQuery(id+"F3.opExtrude","SWEPT_FACE",FACE,{"disambiguationData":[OSD([sQuery(id+"F2.wireOp",EDGE,"E40.1")])]})]}),makeQuery(id+"F3.boolean.opBoolean","INTERSECT",EDGE,{"derivedFrom":[subQ4,makeQuery(id+"F3.opExtrude","SWEPT_FACE",FACE,{"disambiguationData":[OSD([sQuery(id+"F2.wireOp",EDGE,"E40.2")])]})]}),makeQuery(id+"F3.boolean.opBoolean","INTERSECT",EDGE,{"derivedFrom":[subQ4,makeQuery(id+"F3.opExtrude","SWEPT_FACE",FACE,{"disambiguationData":[OSD([sQuery(id+"F2.wireOp",EDGE,"E40.3")])]})]}),makeQuery(id+"F3.boolean.opBoolean","INTERSECT",EDGE,{"derivedFrom":[subQ4,makeQuery(id+"F3.opExtrude","SWEPT_FACE",FACE,{"disambiguationData":[OSD([sQuery(id+"F2.wireOp",EDGE,"E40.4")])]})]}),makeQuery(id+"F3.boolean.opBoolean","INTERSECT",EDGE,{"derivedFrom":[subQ4,makeQuery(id+"F3.opExtrude","SWEPT_FACE",FACE,{"disambiguationData":[OSD([sQuery(id+"F2.wireOp",EDGE,"E40.5")])]})]}),makeQuery(id+"F3.boolean.opBoolean","INTERSECT",EDGE,{"derivedFrom":[subQ2,makeQuery(id+"F3.opExtrude","SWEPT_FACE",FACE,{"disambiguationData":[OSD([sQuery(id+"F2.wireOp",EDGE,"E36.0")])]})]}),makeQuery(id+"F3.boolean.opBoolean","INTERSECT",EDGE,{"derivedFrom":[subQ2,makeQuery(id+"F3.opExtrude","SWEPT_FACE",FACE,{"disambiguationData":[OSD([sQuery(id+"F2.wireOp",EDGE,"E36.1")])]})]}),makeQuery(id+"F3.boolean.opBoolean","INTERSECT",EDGE,{"derivedFrom":[subQ2,makeQuery(id+"F3.opExtrude","SWEPT_FACE",FACE,{"disambiguationData":[OSD([sQuery(id+"F2.wireOp",EDGE,"E36.2")])]})]}),makeQuery(id+"F3.boolean.opBoolean","INTERSECT",EDGE,{"derivedFrom":[subQ2,makeQuery(id+"F3.opExtrude","SWEPT_FACE",FACE,{"disambiguationData":[OSD([sQuery(id+"F2.wireOp",EDGE,"E36.3")])]})]}),makeQuery(id+"F3.boolean.opBoolean","INTERSECT",EDGE,{"derivedFrom":[subQ2,makeQuery(id+"F3.opExtrude","SWEPT_FACE",FACE,{"disambiguationData":[OSD([sQuery(id+"F2.wireOp",EDGE,"E36.4")])]})]}),makeQuery(id+"F3.boolean.opBoolean","INTERSECT",EDGE,{"derivedFrom":[subQ2,makeQuery(id+"F3.opExtrude","SWEPT_FACE",FACE,{"disambiguationData":[OSD([sQuery(id+"F2.wireOp",EDGE,"E36.5")])]})]}),makeQuery(id+"F3.boolean.opBoolean","INTERSECT",EDGE,{"derivedFrom":[subQ2,makeQuery(id+"F3.opExtrude","SWEPT_FACE",FACE,{"disambiguationData":[OSD([sQuery(id+"F2.wireOp",EDGE,"E37.0")])]})]}),makeQuery(id+"F3.boolean.opBoolean","INTERSECT",EDGE,{"derivedFrom":[subQ2,makeQuery(id+"F3.opExtrude","SWEPT_FACE",FACE,{"disambiguationData":[OSD([sQuery(id+"F2.wireOp",EDGE,"E37.1")])]})]}),makeQuery(id+"F3.boolean.opBoolean","INTERSECT",EDGE,{"derivedFrom":[subQ2,makeQuery(id+"F3.opExtrude","SWEPT_FACE",FACE,{"disambiguationData":[OSD([sQuery(id+"F2.wireOp",EDGE,"E37.2")])]})]}),makeQuery(id+"F3.boolean.opBoolean","INTERSECT",EDGE,{"derivedFrom":[subQ2,makeQuery(id+"F3.opExtrude","SWEPT_FACE",FACE,{"disambiguationData":[OSD([sQuery(id+"F2.wireOp",EDGE,"E37.3")])]})]}),makeQuery(id+"F3.boolean.opBoolean","INTERSECT",EDGE,{"derivedFrom":[subQ2,makeQuery(id+"F3.opExtrude","SWEPT_FACE",FACE,{"disambiguationData":[OSD([sQuery(id+"F2.wireOp",EDGE,"E37.4")])]})]}),makeQuery(id+"F3.boolean.opBoolean","INTERSECT",EDGE,{"derivedFrom":[subQ2,makeQuery(id+"F3.opExtrude","SWEPT_FACE",FACE,{"disambiguationData":[OSD([sQuery(id+"F2.wireOp",EDGE,"E37.5")])]})]}),makeQuery(id+"F3.boolean.opBoolean","INTERSECT",EDGE,{"derivedFrom":[subQ2,makeQuery(id+"F3.opExtrude","SWEPT_FACE",FACE,{"disambiguationData":[OSD([sQuery(id+"F2.wireOp",EDGE,"E38.0")])]})]}),makeQuery(id+"F3.boolean.opBoolean","INTERSECT",EDGE,{"derivedFrom":[subQ2,makeQuery(id+"F3.opExtrude","SWEPT_FACE",FACE,{"disambiguationData":[OSD([sQuery(id+"F2.wireOp",EDGE,"E38.1")])]})]}),makeQuery(id+"F3.boolean.opBoolean","INTERSECT",EDGE,{"derivedFrom":[subQ2,makeQuery(id+"F3.opExtrude","SWEPT_FACE",FACE,{"disambiguationData":[OSD([sQuery(id+"F2.wireOp",EDGE,"E38.2")])]})]}),makeQuery(id+"F3.boolean.opBoolean","INTERSECT",EDGE,{"derivedFrom":[subQ2,makeQuery(id+"F3.opExtrude","SWEPT_FACE",FACE,{"disambiguationData":[OSD([sQuery(id+"F2.wireOp",EDGE,"E38.3")])]})]}),makeQuery(id+"F3.boolean.opBoolean","INTERSECT",EDGE,{"derivedFrom":[subQ2,makeQuery(id+"F3.opExtrude","SWEPT_FACE",FACE,{"disambiguationData":[OSD([sQuery(id+"F2.wireOp",EDGE,"E38.4")])]})]}),makeQuery(id+"F3.boolean.opBoolean","INTERSECT",EDGE,{"derivedFrom":[subQ2,makeQuery(id+"F3.opExtrude","SWEPT_FACE",FACE,{"disambiguationData":[OSD([sQuery(id+"F2.wireOp",EDGE,"E38.5")])]})]})]);}
            var Q23;
            {var subQ0=sQuery(id+"F0.wireOp",EDGE,"E6");var subQ1=sQuery(id+"F0.wireOp",EDGE,"E18.top");var subQ2=makeQuery(id+"F1.opExtrude","SWEPT_FACE",FACE,{"disambiguationData":[OSD([subQ0]),TDD([makeQuery(id+"F0.imprint","IMPRINT",EDGE,{"disambiguationData":[TD([[makeQuery(id+"F0.imprint","INTERSECT",VERTEX,{"derivedFrom":[subQ0,sQuery(id+"F0.wireOp",EDGE,"E9")]}),1.0]])],"derivedFrom":subQ0})])]});var subQ4=makeQuery(id+"F1.opExtrude","SWEPT_FACE",FACE,{"disambiguationData":[OSD([subQ0]),TDD([makeQuery(id+"F0.imprint","IMPRINT",EDGE,{"disambiguationData":[TD([[makeQuery(id+"F0.imprint","INTERSECT",VERTEX,{"derivedFrom":[subQ0,subQ1,sQuery(id+"F0.wireOp",EDGE,"E18.right")]}),1.0]])],"derivedFrom":subQ0})])]});var subQ5=makeQuery(id+"F1.opExtrude","SWEPT_FACE",FACE,{"disambiguationData":[OSD([subQ0]),TDD([makeQuery(id+"F0.imprint","IMPRINT",EDGE,{"disambiguationData":[TD([[makeQuery(id+"F0.imprint","INTERSECT",VERTEX,{"derivedFrom":[subQ0,sQuery(id+"F0.wireOp",EDGE,"E12")]}),-1.0]])],"derivedFrom":subQ0})])]});Q23=qUnion([makeQuery(id+"F3.boolean.opBoolean","INTERSECT",EDGE,{"derivedFrom":[subQ5,makeQuery(id+"F3.opExtrude","SWEPT_FACE",FACE,{"disambiguationData":[OSD([sQuery(id+"F2.wireOp",EDGE,"E41.0")])]})]}),makeQuery(id+"F3.boolean.opBoolean","INTERSECT",EDGE,{"derivedFrom":[subQ5,makeQuery(id+"F3.opExtrude","SWEPT_FACE",FACE,{"disambiguationData":[OSD([sQuery(id+"F2.wireOp",EDGE,"E41.1")])]})]}),makeQuery(id+"F3.boolean.opBoolean","INTERSECT",EDGE,{"derivedFrom":[subQ5,makeQuery(id+"F3.opExtrude","SWEPT_FACE",FACE,{"disambiguationData":[OSD([sQuery(id+"F2.wireOp",EDGE,"E41.2")])]})]}),makeQuery(id+"F3.boolean.opBoolean","INTERSECT",EDGE,{"derivedFrom":[subQ5,makeQuery(id+"F3.opExtrude","SWEPT_FACE",FACE,{"disambiguationData":[OSD([sQuery(id+"F2.wireOp",EDGE,"E41.3")])]})]}),makeQuery(id+"F3.boolean.opBoolean","INTERSECT",EDGE,{"derivedFrom":[subQ5,makeQuery(id+"F3.opExtrude","SWEPT_FACE",FACE,{"disambiguationData":[OSD([sQuery(id+"F2.wireOp",EDGE,"E41.4")])]})]}),makeQuery(id+"F3.boolean.opBoolean","INTERSECT",EDGE,{"derivedFrom":[subQ5,makeQuery(id+"F3.opExtrude","SWEPT_FACE",FACE,{"disambiguationData":[OSD([sQuery(id+"F2.wireOp",EDGE,"E41.5")])]})]}),makeQuery(id+"F3.boolean.opBoolean","INTERSECT",EDGE,{"derivedFrom":[subQ5,makeQuery(id+"F3.opExtrude","SWEPT_FACE",FACE,{"disambiguationData":[OSD([sQuery(id+"F2.wireOp",EDGE,"E42.0")])]})]}),makeQuery(id+"F3.boolean.opBoolean","INTERSECT",EDGE,{"derivedFrom":[subQ5,makeQuery(id+"F3.opExtrude","SWEPT_FACE",FACE,{"disambiguationData":[OSD([sQuery(id+"F2.wireOp",EDGE,"E42.1")])]})]}),makeQuery(id+"F3.boolean.opBoolean","INTERSECT",EDGE,{"derivedFrom":[subQ5,makeQuery(id+"F3.opExtrude","SWEPT_FACE",FACE,{"disambiguationData":[OSD([sQuery(id+"F2.wireOp",EDGE,"E42.2")])]})]}),makeQuery(id+"F3.boolean.opBoolean","INTERSECT",EDGE,{"derivedFrom":[subQ5,makeQuery(id+"F3.opExtrude","SWEPT_FACE",FACE,{"disambiguationData":[OSD([sQuery(id+"F2.wireOp",EDGE,"E42.3")])]})]}),makeQuery(id+"F3.boolean.opBoolean","INTERSECT",EDGE,{"derivedFrom":[subQ5,makeQuery(id+"F3.opExtrude","SWEPT_FACE",FACE,{"disambiguationData":[OSD([sQuery(id+"F2.wireOp",EDGE,"E42.4")])]})]}),makeQuery(id+"F3.boolean.opBoolean","INTERSECT",EDGE,{"derivedFrom":[subQ5,makeQuery(id+"F3.opExtrude","SWEPT_FACE",FACE,{"disambiguationData":[OSD([sQuery(id+"F2.wireOp",EDGE,"E42.5")])]})]}),makeQuery(id+"F3.boolean.opBoolean","INTERSECT",EDGE,{"derivedFrom":[subQ4,makeQuery(id+"F3.opExtrude","SWEPT_FACE",FACE,{"disambiguationData":[OSD([sQuery(id+"F2.wireOp",EDGE,"E39.0")])]})]}),makeQuery(id+"F3.boolean.opBoolean","INTERSECT",EDGE,{"derivedFrom":[subQ4,makeQuery(id+"F3.opExtrude","SWEPT_FACE",FACE,{"disambiguationData":[OSD([sQuery(id+"F2.wireOp",EDGE,"E39.1")])]})]}),makeQuery(id+"F3.boolean.opBoolean","INTERSECT",EDGE,{"derivedFrom":[subQ4,makeQuery(id+"F3.opExtrude","SWEPT_FACE",FACE,{"disambiguationData":[OSD([sQuery(id+"F2.wireOp",EDGE,"E39.2")])]})]}),makeQuery(id+"F3.boolean.opBoolean","INTERSECT",EDGE,{"derivedFrom":[subQ4,makeQuery(id+"F3.opExtrude","SWEPT_FACE",FACE,{"disambiguationData":[OSD([sQuery(id+"F2.wireOp",EDGE,"E39.3")])]})]}),makeQuery(id+"F3.boolean.opBoolean","INTERSECT",EDGE,{"derivedFrom":[subQ4,makeQuery(id+"F3.opExtrude","SWEPT_FACE",FACE,{"disambiguationData":[OSD([sQuery(id+"F2.wireOp",EDGE,"E39.4")])]})]}),makeQuery(id+"F3.boolean.opBoolean","INTERSECT",EDGE,{"derivedFrom":[subQ4,makeQuery(id+"F3.opExtrude","SWEPT_FACE",FACE,{"disambiguationData":[OSD([sQuery(id+"F2.wireOp",EDGE,"E39.5")])]})]}),makeQuery(id+"F3.boolean.opBoolean","INTERSECT",EDGE,{"derivedFrom":[subQ4,makeQuery(id+"F3.opExtrude","SWEPT_FACE",FACE,{"disambiguationData":[OSD([sQuery(id+"F2.wireOp",EDGE,"E40.0")])]})]}),makeQuery(id+"F3.boolean.opBoolean","INTERSECT",EDGE,{"derivedFrom":[subQ4,makeQuery(id+"F3.opExtrude","SWEPT_FACE",FACE,{"disambiguationData":[OSD([sQuery(id+"F2.wireOp",EDGE,"E40.1")])]})]}),makeQuery(id+"F3.boolean.opBoolean","INTERSECT",EDGE,{"derivedFrom":[subQ4,makeQuery(id+"F3.opExtrude","SWEPT_FACE",FACE,{"disambiguationData":[OSD([sQuery(id+"F2.wireOp",EDGE,"E40.2")])]})]}),makeQuery(id+"F3.boolean.opBoolean","INTERSECT",EDGE,{"derivedFrom":[subQ4,makeQuery(id+"F3.opExtrude","SWEPT_FACE",FACE,{"disambiguationData":[OSD([sQuery(id+"F2.wireOp",EDGE,"E40.3")])]})]}),makeQuery(id+"F3.boolean.opBoolean","INTERSECT",EDGE,{"derivedFrom":[subQ4,makeQuery(id+"F3.opExtrude","SWEPT_FACE",FACE,{"disambiguationData":[OSD([sQuery(id+"F2.wireOp",EDGE,"E40.4")])]})]}),makeQuery(id+"F3.boolean.opBoolean","INTERSECT",EDGE,{"derivedFrom":[subQ4,makeQuery(id+"F3.opExtrude","SWEPT_FACE",FACE,{"disambiguationData":[OSD([sQuery(id+"F2.wireOp",EDGE,"E40.5")])]})]}),makeQuery(id+"F3.boolean.opBoolean","INTERSECT",EDGE,{"derivedFrom":[subQ2,makeQuery(id+"F3.opExtrude","SWEPT_FACE",FACE,{"disambiguationData":[OSD([sQuery(id+"F2.wireOp",EDGE,"E36.0")])]})]}),makeQuery(id+"F3.boolean.opBoolean","INTERSECT",EDGE,{"derivedFrom":[subQ2,makeQuery(id+"F3.opExtrude","SWEPT_FACE",FACE,{"disambiguationData":[OSD([sQuery(id+"F2.wireOp",EDGE,"E36.1")])]})]}),makeQuery(id+"F3.boolean.opBoolean","INTERSECT",EDGE,{"derivedFrom":[subQ2,makeQuery(id+"F3.opExtrude","SWEPT_FACE",FACE,{"disambiguationData":[OSD([sQuery(id+"F2.wireOp",EDGE,"E36.2")])]})]}),makeQuery(id+"F3.boolean.opBoolean","INTERSECT",EDGE,{"derivedFrom":[subQ2,makeQuery(id+"F3.opExtrude","SWEPT_FACE",FACE,{"disambiguationData":[OSD([sQuery(id+"F2.wireOp",EDGE,"E36.3")])]})]}),makeQuery(id+"F3.boolean.opBoolean","INTERSECT",EDGE,{"derivedFrom":[subQ2,makeQuery(id+"F3.opExtrude","SWEPT_FACE",FACE,{"disambiguationData":[OSD([sQuery(id+"F2.wireOp",EDGE,"E36.4")])]})]}),makeQuery(id+"F3.boolean.opBoolean","INTERSECT",EDGE,{"derivedFrom":[subQ2,makeQuery(id+"F3.opExtrude","SWEPT_FACE",FACE,{"disambiguationData":[OSD([sQuery(id+"F2.wireOp",EDGE,"E36.5")])]})]}),makeQuery(id+"F3.boolean.opBoolean","INTERSECT",EDGE,{"derivedFrom":[subQ2,makeQuery(id+"F3.opExtrude","SWEPT_FACE",FACE,{"disambiguationData":[OSD([sQuery(id+"F2.wireOp",EDGE,"E37.0")])]})]}),makeQuery(id+"F3.boolean.opBoolean","INTERSECT",EDGE,{"derivedFrom":[subQ2,makeQuery(id+"F3.opExtrude","SWEPT_FACE",FACE,{"disambiguationData":[OSD([sQuery(id+"F2.wireOp",EDGE,"E37.1")])]})]}),makeQuery(id+"F3.boolean.opBoolean","INTERSECT",EDGE,{"derivedFrom":[subQ2,makeQuery(id+"F3.opExtrude","SWEPT_FACE",FACE,{"disambiguationData":[OSD([sQuery(id+"F2.wireOp",EDGE,"E37.2")])]})]}),makeQuery(id+"F3.boolean.opBoolean","INTERSECT",EDGE,{"derivedFrom":[subQ2,makeQuery(id+"F3.opExtrude","SWEPT_FACE",FACE,{"disambiguationData":[OSD([sQuery(id+"F2.wireOp",EDGE,"E37.3")])]})]}),makeQuery(id+"F3.boolean.opBoolean","INTERSECT",EDGE,{"derivedFrom":[subQ2,makeQuery(id+"F3.opExtrude","SWEPT_FACE",FACE,{"disambiguationData":[OSD([sQuery(id+"F2.wireOp",EDGE,"E37.4")])]})]}),makeQuery(id+"F3.boolean.opBoolean","INTERSECT",EDGE,{"derivedFrom":[subQ2,makeQuery(id+"F3.opExtrude","SWEPT_FACE",FACE,{"disambiguationData":[OSD([sQuery(id+"F2.wireOp",EDGE,"E37.5")])]})]}),makeQuery(id+"F3.boolean.opBoolean","INTERSECT",EDGE,{"derivedFrom":[subQ2,makeQuery(id+"F3.opExtrude","SWEPT_FACE",FACE,{"disambiguationData":[OSD([sQuery(id+"F2.wireOp",EDGE,"E38.0")])]})]}),makeQuery(id+"F3.boolean.opBoolean","INTERSECT",EDGE,{"derivedFrom":[subQ2,makeQuery(id+"F3.opExtrude","SWEPT_FACE",FACE,{"disambiguationData":[OSD([sQuery(id+"F2.wireOp",EDGE,"E38.1")])]})]}),makeQuery(id+"F3.boolean.opBoolean","INTERSECT",EDGE,{"derivedFrom":[subQ2,makeQuery(id+"F3.opExtrude","SWEPT_FACE",FACE,{"disambiguationData":[OSD([sQuery(id+"F2.wireOp",EDGE,"E38.2")])]})]}),makeQuery(id+"F3.boolean.opBoolean","INTERSECT",EDGE,{"derivedFrom":[subQ2,makeQuery(id+"F3.opExtrude","SWEPT_FACE",FACE,{"disambiguationData":[OSD([sQuery(id+"F2.wireOp",EDGE,"E38.3")])]})]}),makeQuery(id+"F3.boolean.opBoolean","INTERSECT",EDGE,{"derivedFrom":[subQ2,makeQuery(id+"F3.opExtrude","SWEPT_FACE",FACE,{"disambiguationData":[OSD([sQuery(id+"F2.wireOp",EDGE,"E38.4")])]})]}),makeQuery(id+"F3.boolean.opBoolean","INTERSECT",EDGE,{"derivedFrom":[subQ2,makeQuery(id+"F3.opExtrude","SWEPT_FACE",FACE,{"disambiguationData":[OSD([sQuery(id+"F2.wireOp",EDGE,"E38.5")])]})]})]);}
            var Q24;
            {var subQ0=sQuery(id+"F0.wireOp",EDGE,"E6");var subQ1=sQuery(id+"F0.wireOp",EDGE,"E18.top");var subQ2=makeQuery(id+"F1.opExtrude","SWEPT_FACE",FACE,{"disambiguationData":[OSD([subQ0]),TDD([makeQuery(id+"F0.imprint","IMPRINT",EDGE,{"disambiguationData":[TD([[makeQuery(id+"F0.imprint","INTERSECT",VERTEX,{"derivedFrom":[subQ0,sQuery(id+"F0.wireOp",EDGE,"E9")]}),1.0]])],"derivedFrom":subQ0})])]});var subQ4=makeQuery(id+"F1.opExtrude","SWEPT_FACE",FACE,{"disambiguationData":[OSD([subQ0]),TDD([makeQuery(id+"F0.imprint","IMPRINT",EDGE,{"disambiguationData":[TD([[makeQuery(id+"F0.imprint","INTERSECT",VERTEX,{"derivedFrom":[subQ0,subQ1,sQuery(id+"F0.wireOp",EDGE,"E18.right")]}),1.0]])],"derivedFrom":subQ0})])]});var subQ5=makeQuery(id+"F1.opExtrude","SWEPT_FACE",FACE,{"disambiguationData":[OSD([subQ0]),TDD([makeQuery(id+"F0.imprint","IMPRINT",EDGE,{"disambiguationData":[TD([[makeQuery(id+"F0.imprint","INTERSECT",VERTEX,{"derivedFrom":[subQ0,sQuery(id+"F0.wireOp",EDGE,"E12")]}),-1.0]])],"derivedFrom":subQ0})])]});Q24=qUnion([makeQuery(id+"F3.boolean.opBoolean","INTERSECT",EDGE,{"derivedFrom":[subQ5,makeQuery(id+"F3.opExtrude","SWEPT_FACE",FACE,{"disambiguationData":[OSD([sQuery(id+"F2.wireOp",EDGE,"E41.0")])]})]}),makeQuery(id+"F3.boolean.opBoolean","INTERSECT",EDGE,{"derivedFrom":[subQ5,makeQuery(id+"F3.opExtrude","SWEPT_FACE",FACE,{"disambiguationData":[OSD([sQuery(id+"F2.wireOp",EDGE,"E41.1")])]})]}),makeQuery(id+"F3.boolean.opBoolean","INTERSECT",EDGE,{"derivedFrom":[subQ5,makeQuery(id+"F3.opExtrude","SWEPT_FACE",FACE,{"disambiguationData":[OSD([sQuery(id+"F2.wireOp",EDGE,"E41.2")])]})]}),makeQuery(id+"F3.boolean.opBoolean","INTERSECT",EDGE,{"derivedFrom":[subQ5,makeQuery(id+"F3.opExtrude","SWEPT_FACE",FACE,{"disambiguationData":[OSD([sQuery(id+"F2.wireOp",EDGE,"E41.3")])]})]}),makeQuery(id+"F3.boolean.opBoolean","INTERSECT",EDGE,{"derivedFrom":[subQ5,makeQuery(id+"F3.opExtrude","SWEPT_FACE",FACE,{"disambiguationData":[OSD([sQuery(id+"F2.wireOp",EDGE,"E41.4")])]})]}),makeQuery(id+"F3.boolean.opBoolean","INTERSECT",EDGE,{"derivedFrom":[subQ5,makeQuery(id+"F3.opExtrude","SWEPT_FACE",FACE,{"disambiguationData":[OSD([sQuery(id+"F2.wireOp",EDGE,"E41.5")])]})]}),makeQuery(id+"F3.boolean.opBoolean","INTERSECT",EDGE,{"derivedFrom":[subQ5,makeQuery(id+"F3.opExtrude","SWEPT_FACE",FACE,{"disambiguationData":[OSD([sQuery(id+"F2.wireOp",EDGE,"E42.0")])]})]}),makeQuery(id+"F3.boolean.opBoolean","INTERSECT",EDGE,{"derivedFrom":[subQ5,makeQuery(id+"F3.opExtrude","SWEPT_FACE",FACE,{"disambiguationData":[OSD([sQuery(id+"F2.wireOp",EDGE,"E42.1")])]})]}),makeQuery(id+"F3.boolean.opBoolean","INTERSECT",EDGE,{"derivedFrom":[subQ5,makeQuery(id+"F3.opExtrude","SWEPT_FACE",FACE,{"disambiguationData":[OSD([sQuery(id+"F2.wireOp",EDGE,"E42.2")])]})]}),makeQuery(id+"F3.boolean.opBoolean","INTERSECT",EDGE,{"derivedFrom":[subQ5,makeQuery(id+"F3.opExtrude","SWEPT_FACE",FACE,{"disambiguationData":[OSD([sQuery(id+"F2.wireOp",EDGE,"E42.3")])]})]}),makeQuery(id+"F3.boolean.opBoolean","INTERSECT",EDGE,{"derivedFrom":[subQ5,makeQuery(id+"F3.opExtrude","SWEPT_FACE",FACE,{"disambiguationData":[OSD([sQuery(id+"F2.wireOp",EDGE,"E42.4")])]})]}),makeQuery(id+"F3.boolean.opBoolean","INTERSECT",EDGE,{"derivedFrom":[subQ5,makeQuery(id+"F3.opExtrude","SWEPT_FACE",FACE,{"disambiguationData":[OSD([sQuery(id+"F2.wireOp",EDGE,"E42.5")])]})]}),makeQuery(id+"F3.boolean.opBoolean","INTERSECT",EDGE,{"derivedFrom":[subQ4,makeQuery(id+"F3.opExtrude","SWEPT_FACE",FACE,{"disambiguationData":[OSD([sQuery(id+"F2.wireOp",EDGE,"E39.0")])]})]}),makeQuery(id+"F3.boolean.opBoolean","INTERSECT",EDGE,{"derivedFrom":[subQ4,makeQuery(id+"F3.opExtrude","SWEPT_FACE",FACE,{"disambiguationData":[OSD([sQuery(id+"F2.wireOp",EDGE,"E39.1")])]})]}),makeQuery(id+"F3.boolean.opBoolean","INTERSECT",EDGE,{"derivedFrom":[subQ4,makeQuery(id+"F3.opExtrude","SWEPT_FACE",FACE,{"disambiguationData":[OSD([sQuery(id+"F2.wireOp",EDGE,"E39.2")])]})]}),makeQuery(id+"F3.boolean.opBoolean","INTERSECT",EDGE,{"derivedFrom":[subQ4,makeQuery(id+"F3.opExtrude","SWEPT_FACE",FACE,{"disambiguationData":[OSD([sQuery(id+"F2.wireOp",EDGE,"E39.3")])]})]}),makeQuery(id+"F3.boolean.opBoolean","INTERSECT",EDGE,{"derivedFrom":[subQ4,makeQuery(id+"F3.opExtrude","SWEPT_FACE",FACE,{"disambiguationData":[OSD([sQuery(id+"F2.wireOp",EDGE,"E39.4")])]})]}),makeQuery(id+"F3.boolean.opBoolean","INTERSECT",EDGE,{"derivedFrom":[subQ4,makeQuery(id+"F3.opExtrude","SWEPT_FACE",FACE,{"disambiguationData":[OSD([sQuery(id+"F2.wireOp",EDGE,"E39.5")])]})]}),makeQuery(id+"F3.boolean.opBoolean","INTERSECT",EDGE,{"derivedFrom":[subQ4,makeQuery(id+"F3.opExtrude","SWEPT_FACE",FACE,{"disambiguationData":[OSD([sQuery(id+"F2.wireOp",EDGE,"E40.0")])]})]}),makeQuery(id+"F3.boolean.opBoolean","INTERSECT",EDGE,{"derivedFrom":[subQ4,makeQuery(id+"F3.opExtrude","SWEPT_FACE",FACE,{"disambiguationData":[OSD([sQuery(id+"F2.wireOp",EDGE,"E40.1")])]})]}),makeQuery(id+"F3.boolean.opBoolean","INTERSECT",EDGE,{"derivedFrom":[subQ4,makeQuery(id+"F3.opExtrude","SWEPT_FACE",FACE,{"disambiguationData":[OSD([sQuery(id+"F2.wireOp",EDGE,"E40.2")])]})]}),makeQuery(id+"F3.boolean.opBoolean","INTERSECT",EDGE,{"derivedFrom":[subQ4,makeQuery(id+"F3.opExtrude","SWEPT_FACE",FACE,{"disambiguationData":[OSD([sQuery(id+"F2.wireOp",EDGE,"E40.3")])]})]}),makeQuery(id+"F3.boolean.opBoolean","INTERSECT",EDGE,{"derivedFrom":[subQ4,makeQuery(id+"F3.opExtrude","SWEPT_FACE",FACE,{"disambiguationData":[OSD([sQuery(id+"F2.wireOp",EDGE,"E40.4")])]})]}),makeQuery(id+"F3.boolean.opBoolean","INTERSECT",EDGE,{"derivedFrom":[subQ4,makeQuery(id+"F3.opExtrude","SWEPT_FACE",FACE,{"disambiguationData":[OSD([sQuery(id+"F2.wireOp",EDGE,"E40.5")])]})]}),makeQuery(id+"F3.boolean.opBoolean","INTERSECT",EDGE,{"derivedFrom":[subQ2,makeQuery(id+"F3.opExtrude","SWEPT_FACE",FACE,{"disambiguationData":[OSD([sQuery(id+"F2.wireOp",EDGE,"E36.0")])]})]}),makeQuery(id+"F3.boolean.opBoolean","INTERSECT",EDGE,{"derivedFrom":[subQ2,makeQuery(id+"F3.opExtrude","SWEPT_FACE",FACE,{"disambiguationData":[OSD([sQuery(id+"F2.wireOp",EDGE,"E36.1")])]})]}),makeQuery(id+"F3.boolean.opBoolean","INTERSECT",EDGE,{"derivedFrom":[subQ2,makeQuery(id+"F3.opExtrude","SWEPT_FACE",FACE,{"disambiguationData":[OSD([sQuery(id+"F2.wireOp",EDGE,"E36.2")])]})]}),makeQuery(id+"F3.boolean.opBoolean","INTERSECT",EDGE,{"derivedFrom":[subQ2,makeQuery(id+"F3.opExtrude","SWEPT_FACE",FACE,{"disambiguationData":[OSD([sQuery(id+"F2.wireOp",EDGE,"E36.3")])]})]}),makeQuery(id+"F3.boolean.opBoolean","INTERSECT",EDGE,{"derivedFrom":[subQ2,makeQuery(id+"F3.opExtrude","SWEPT_FACE",FACE,{"disambiguationData":[OSD([sQuery(id+"F2.wireOp",EDGE,"E36.4")])]})]}),makeQuery(id+"F3.boolean.opBoolean","INTERSECT",EDGE,{"derivedFrom":[subQ2,makeQuery(id+"F3.opExtrude","SWEPT_FACE",FACE,{"disambiguationData":[OSD([sQuery(id+"F2.wireOp",EDGE,"E36.5")])]})]}),makeQuery(id+"F3.boolean.opBoolean","INTERSECT",EDGE,{"derivedFrom":[subQ2,makeQuery(id+"F3.opExtrude","SWEPT_FACE",FACE,{"disambiguationData":[OSD([sQuery(id+"F2.wireOp",EDGE,"E37.0")])]})]}),makeQuery(id+"F3.boolean.opBoolean","INTERSECT",EDGE,{"derivedFrom":[subQ2,makeQuery(id+"F3.opExtrude","SWEPT_FACE",FACE,{"disambiguationData":[OSD([sQuery(id+"F2.wireOp",EDGE,"E37.1")])]})]}),makeQuery(id+"F3.boolean.opBoolean","INTERSECT",EDGE,{"derivedFrom":[subQ2,makeQuery(id+"F3.opExtrude","SWEPT_FACE",FACE,{"disambiguationData":[OSD([sQuery(id+"F2.wireOp",EDGE,"E37.2")])]})]}),makeQuery(id+"F3.boolean.opBoolean","INTERSECT",EDGE,{"derivedFrom":[subQ2,makeQuery(id+"F3.opExtrude","SWEPT_FACE",FACE,{"disambiguationData":[OSD([sQuery(id+"F2.wireOp",EDGE,"E37.3")])]})]}),makeQuery(id+"F3.boolean.opBoolean","INTERSECT",EDGE,{"derivedFrom":[subQ2,makeQuery(id+"F3.opExtrude","SWEPT_FACE",FACE,{"disambiguationData":[OSD([sQuery(id+"F2.wireOp",EDGE,"E37.4")])]})]}),makeQuery(id+"F3.boolean.opBoolean","INTERSECT",EDGE,{"derivedFrom":[subQ2,makeQuery(id+"F3.opExtrude","SWEPT_FACE",FACE,{"disambiguationData":[OSD([sQuery(id+"F2.wireOp",EDGE,"E37.5")])]})]}),makeQuery(id+"F3.boolean.opBoolean","INTERSECT",EDGE,{"derivedFrom":[subQ2,makeQuery(id+"F3.opExtrude","SWEPT_FACE",FACE,{"disambiguationData":[OSD([sQuery(id+"F2.wireOp",EDGE,"E38.0")])]})]}),makeQuery(id+"F3.boolean.opBoolean","INTERSECT",EDGE,{"derivedFrom":[subQ2,makeQuery(id+"F3.opExtrude","SWEPT_FACE",FACE,{"disambiguationData":[OSD([sQuery(id+"F2.wireOp",EDGE,"E38.1")])]})]}),makeQuery(id+"F3.boolean.opBoolean","INTERSECT",EDGE,{"derivedFrom":[subQ2,makeQuery(id+"F3.opExtrude","SWEPT_FACE",FACE,{"disambiguationData":[OSD([sQuery(id+"F2.wireOp",EDGE,"E38.2")])]})]}),makeQuery(id+"F3.boolean.opBoolean","INTERSECT",EDGE,{"derivedFrom":[subQ2,makeQuery(id+"F3.opExtrude","SWEPT_FACE",FACE,{"disambiguationData":[OSD([sQuery(id+"F2.wireOp",EDGE,"E38.3")])]})]}),makeQuery(id+"F3.boolean.opBoolean","INTERSECT",EDGE,{"derivedFrom":[subQ2,makeQuery(id+"F3.opExtrude","SWEPT_FACE",FACE,{"disambiguationData":[OSD([sQuery(id+"F2.wireOp",EDGE,"E38.4")])]})]}),makeQuery(id+"F3.boolean.opBoolean","INTERSECT",EDGE,{"derivedFrom":[subQ2,makeQuery(id+"F3.opExtrude","SWEPT_FACE",FACE,{"disambiguationData":[OSD([sQuery(id+"F2.wireOp",EDGE,"E38.5")])]})]})]);}
            var Q25;
            {var subQ0=sQuery(id+"F0.wireOp",EDGE,"E6");var subQ1=sQuery(id+"F0.wireOp",EDGE,"E18.top");var subQ2=makeQuery(id+"F1.opExtrude","SWEPT_FACE",FACE,{"disambiguationData":[OSD([subQ0]),TDD([makeQuery(id+"F0.imprint","IMPRINT",EDGE,{"disambiguationData":[TD([[makeQuery(id+"F0.imprint","INTERSECT",VERTEX,{"derivedFrom":[subQ0,sQuery(id+"F0.wireOp",EDGE,"E9")]}),1.0]])],"derivedFrom":subQ0})])]});var subQ4=makeQuery(id+"F1.opExtrude","SWEPT_FACE",FACE,{"disambiguationData":[OSD([subQ0]),TDD([makeQuery(id+"F0.imprint","IMPRINT",EDGE,{"disambiguationData":[TD([[makeQuery(id+"F0.imprint","INTERSECT",VERTEX,{"derivedFrom":[subQ0,subQ1,sQuery(id+"F0.wireOp",EDGE,"E18.right")]}),1.0]])],"derivedFrom":subQ0})])]});var subQ5=makeQuery(id+"F1.opExtrude","SWEPT_FACE",FACE,{"disambiguationData":[OSD([subQ0]),TDD([makeQuery(id+"F0.imprint","IMPRINT",EDGE,{"disambiguationData":[TD([[makeQuery(id+"F0.imprint","INTERSECT",VERTEX,{"derivedFrom":[subQ0,sQuery(id+"F0.wireOp",EDGE,"E12")]}),-1.0]])],"derivedFrom":subQ0})])]});Q25=qUnion([makeQuery(id+"F3.boolean.opBoolean","INTERSECT",EDGE,{"derivedFrom":[subQ5,makeQuery(id+"F3.opExtrude","SWEPT_FACE",FACE,{"disambiguationData":[OSD([sQuery(id+"F2.wireOp",EDGE,"E41.0")])]})]}),makeQuery(id+"F3.boolean.opBoolean","INTERSECT",EDGE,{"derivedFrom":[subQ5,makeQuery(id+"F3.opExtrude","SWEPT_FACE",FACE,{"disambiguationData":[OSD([sQuery(id+"F2.wireOp",EDGE,"E41.1")])]})]}),makeQuery(id+"F3.boolean.opBoolean","INTERSECT",EDGE,{"derivedFrom":[subQ5,makeQuery(id+"F3.opExtrude","SWEPT_FACE",FACE,{"disambiguationData":[OSD([sQuery(id+"F2.wireOp",EDGE,"E41.2")])]})]}),makeQuery(id+"F3.boolean.opBoolean","INTERSECT",EDGE,{"derivedFrom":[subQ5,makeQuery(id+"F3.opExtrude","SWEPT_FACE",FACE,{"disambiguationData":[OSD([sQuery(id+"F2.wireOp",EDGE,"E41.3")])]})]}),makeQuery(id+"F3.boolean.opBoolean","INTERSECT",EDGE,{"derivedFrom":[subQ5,makeQuery(id+"F3.opExtrude","SWEPT_FACE",FACE,{"disambiguationData":[OSD([sQuery(id+"F2.wireOp",EDGE,"E41.4")])]})]}),makeQuery(id+"F3.boolean.opBoolean","INTERSECT",EDGE,{"derivedFrom":[subQ5,makeQuery(id+"F3.opExtrude","SWEPT_FACE",FACE,{"disambiguationData":[OSD([sQuery(id+"F2.wireOp",EDGE,"E41.5")])]})]}),makeQuery(id+"F3.boolean.opBoolean","INTERSECT",EDGE,{"derivedFrom":[subQ5,makeQuery(id+"F3.opExtrude","SWEPT_FACE",FACE,{"disambiguationData":[OSD([sQuery(id+"F2.wireOp",EDGE,"E42.0")])]})]}),makeQuery(id+"F3.boolean.opBoolean","INTERSECT",EDGE,{"derivedFrom":[subQ5,makeQuery(id+"F3.opExtrude","SWEPT_FACE",FACE,{"disambiguationData":[OSD([sQuery(id+"F2.wireOp",EDGE,"E42.1")])]})]}),makeQuery(id+"F3.boolean.opBoolean","INTERSECT",EDGE,{"derivedFrom":[subQ5,makeQuery(id+"F3.opExtrude","SWEPT_FACE",FACE,{"disambiguationData":[OSD([sQuery(id+"F2.wireOp",EDGE,"E42.2")])]})]}),makeQuery(id+"F3.boolean.opBoolean","INTERSECT",EDGE,{"derivedFrom":[subQ5,makeQuery(id+"F3.opExtrude","SWEPT_FACE",FACE,{"disambiguationData":[OSD([sQuery(id+"F2.wireOp",EDGE,"E42.3")])]})]}),makeQuery(id+"F3.boolean.opBoolean","INTERSECT",EDGE,{"derivedFrom":[subQ5,makeQuery(id+"F3.opExtrude","SWEPT_FACE",FACE,{"disambiguationData":[OSD([sQuery(id+"F2.wireOp",EDGE,"E42.4")])]})]}),makeQuery(id+"F3.boolean.opBoolean","INTERSECT",EDGE,{"derivedFrom":[subQ5,makeQuery(id+"F3.opExtrude","SWEPT_FACE",FACE,{"disambiguationData":[OSD([sQuery(id+"F2.wireOp",EDGE,"E42.5")])]})]}),makeQuery(id+"F3.boolean.opBoolean","INTERSECT",EDGE,{"derivedFrom":[subQ4,makeQuery(id+"F3.opExtrude","SWEPT_FACE",FACE,{"disambiguationData":[OSD([sQuery(id+"F2.wireOp",EDGE,"E39.0")])]})]}),makeQuery(id+"F3.boolean.opBoolean","INTERSECT",EDGE,{"derivedFrom":[subQ4,makeQuery(id+"F3.opExtrude","SWEPT_FACE",FACE,{"disambiguationData":[OSD([sQuery(id+"F2.wireOp",EDGE,"E39.1")])]})]}),makeQuery(id+"F3.boolean.opBoolean","INTERSECT",EDGE,{"derivedFrom":[subQ4,makeQuery(id+"F3.opExtrude","SWEPT_FACE",FACE,{"disambiguationData":[OSD([sQuery(id+"F2.wireOp",EDGE,"E39.2")])]})]}),makeQuery(id+"F3.boolean.opBoolean","INTERSECT",EDGE,{"derivedFrom":[subQ4,makeQuery(id+"F3.opExtrude","SWEPT_FACE",FACE,{"disambiguationData":[OSD([sQuery(id+"F2.wireOp",EDGE,"E39.3")])]})]}),makeQuery(id+"F3.boolean.opBoolean","INTERSECT",EDGE,{"derivedFrom":[subQ4,makeQuery(id+"F3.opExtrude","SWEPT_FACE",FACE,{"disambiguationData":[OSD([sQuery(id+"F2.wireOp",EDGE,"E39.4")])]})]}),makeQuery(id+"F3.boolean.opBoolean","INTERSECT",EDGE,{"derivedFrom":[subQ4,makeQuery(id+"F3.opExtrude","SWEPT_FACE",FACE,{"disambiguationData":[OSD([sQuery(id+"F2.wireOp",EDGE,"E39.5")])]})]}),makeQuery(id+"F3.boolean.opBoolean","INTERSECT",EDGE,{"derivedFrom":[subQ4,makeQuery(id+"F3.opExtrude","SWEPT_FACE",FACE,{"disambiguationData":[OSD([sQuery(id+"F2.wireOp",EDGE,"E40.0")])]})]}),makeQuery(id+"F3.boolean.opBoolean","INTERSECT",EDGE,{"derivedFrom":[subQ4,makeQuery(id+"F3.opExtrude","SWEPT_FACE",FACE,{"disambiguationData":[OSD([sQuery(id+"F2.wireOp",EDGE,"E40.1")])]})]}),makeQuery(id+"F3.boolean.opBoolean","INTERSECT",EDGE,{"derivedFrom":[subQ4,makeQuery(id+"F3.opExtrude","SWEPT_FACE",FACE,{"disambiguationData":[OSD([sQuery(id+"F2.wireOp",EDGE,"E40.2")])]})]}),makeQuery(id+"F3.boolean.opBoolean","INTERSECT",EDGE,{"derivedFrom":[subQ4,makeQuery(id+"F3.opExtrude","SWEPT_FACE",FACE,{"disambiguationData":[OSD([sQuery(id+"F2.wireOp",EDGE,"E40.3")])]})]}),makeQuery(id+"F3.boolean.opBoolean","INTERSECT",EDGE,{"derivedFrom":[subQ4,makeQuery(id+"F3.opExtrude","SWEPT_FACE",FACE,{"disambiguationData":[OSD([sQuery(id+"F2.wireOp",EDGE,"E40.4")])]})]}),makeQuery(id+"F3.boolean.opBoolean","INTERSECT",EDGE,{"derivedFrom":[subQ4,makeQuery(id+"F3.opExtrude","SWEPT_FACE",FACE,{"disambiguationData":[OSD([sQuery(id+"F2.wireOp",EDGE,"E40.5")])]})]}),makeQuery(id+"F3.boolean.opBoolean","INTERSECT",EDGE,{"derivedFrom":[subQ2,makeQuery(id+"F3.opExtrude","SWEPT_FACE",FACE,{"disambiguationData":[OSD([sQuery(id+"F2.wireOp",EDGE,"E36.0")])]})]}),makeQuery(id+"F3.boolean.opBoolean","INTERSECT",EDGE,{"derivedFrom":[subQ2,makeQuery(id+"F3.opExtrude","SWEPT_FACE",FACE,{"disambiguationData":[OSD([sQuery(id+"F2.wireOp",EDGE,"E36.1")])]})]}),makeQuery(id+"F3.boolean.opBoolean","INTERSECT",EDGE,{"derivedFrom":[subQ2,makeQuery(id+"F3.opExtrude","SWEPT_FACE",FACE,{"disambiguationData":[OSD([sQuery(id+"F2.wireOp",EDGE,"E36.2")])]})]}),makeQuery(id+"F3.boolean.opBoolean","INTERSECT",EDGE,{"derivedFrom":[subQ2,makeQuery(id+"F3.opExtrude","SWEPT_FACE",FACE,{"disambiguationData":[OSD([sQuery(id+"F2.wireOp",EDGE,"E36.3")])]})]}),makeQuery(id+"F3.boolean.opBoolean","INTERSECT",EDGE,{"derivedFrom":[subQ2,makeQuery(id+"F3.opExtrude","SWEPT_FACE",FACE,{"disambiguationData":[OSD([sQuery(id+"F2.wireOp",EDGE,"E36.4")])]})]}),makeQuery(id+"F3.boolean.opBoolean","INTERSECT",EDGE,{"derivedFrom":[subQ2,makeQuery(id+"F3.opExtrude","SWEPT_FACE",FACE,{"disambiguationData":[OSD([sQuery(id+"F2.wireOp",EDGE,"E36.5")])]})]}),makeQuery(id+"F3.boolean.opBoolean","INTERSECT",EDGE,{"derivedFrom":[subQ2,makeQuery(id+"F3.opExtrude","SWEPT_FACE",FACE,{"disambiguationData":[OSD([sQuery(id+"F2.wireOp",EDGE,"E37.0")])]})]}),makeQuery(id+"F3.boolean.opBoolean","INTERSECT",EDGE,{"derivedFrom":[subQ2,makeQuery(id+"F3.opExtrude","SWEPT_FACE",FACE,{"disambiguationData":[OSD([sQuery(id+"F2.wireOp",EDGE,"E37.1")])]})]}),makeQuery(id+"F3.boolean.opBoolean","INTERSECT",EDGE,{"derivedFrom":[subQ2,makeQuery(id+"F3.opExtrude","SWEPT_FACE",FACE,{"disambiguationData":[OSD([sQuery(id+"F2.wireOp",EDGE,"E37.2")])]})]}),makeQuery(id+"F3.boolean.opBoolean","INTERSECT",EDGE,{"derivedFrom":[subQ2,makeQuery(id+"F3.opExtrude","SWEPT_FACE",FACE,{"disambiguationData":[OSD([sQuery(id+"F2.wireOp",EDGE,"E37.3")])]})]}),makeQuery(id+"F3.boolean.opBoolean","INTERSECT",EDGE,{"derivedFrom":[subQ2,makeQuery(id+"F3.opExtrude","SWEPT_FACE",FACE,{"disambiguationData":[OSD([sQuery(id+"F2.wireOp",EDGE,"E37.4")])]})]}),makeQuery(id+"F3.boolean.opBoolean","INTERSECT",EDGE,{"derivedFrom":[subQ2,makeQuery(id+"F3.opExtrude","SWEPT_FACE",FACE,{"disambiguationData":[OSD([sQuery(id+"F2.wireOp",EDGE,"E37.5")])]})]}),makeQuery(id+"F3.boolean.opBoolean","INTERSECT",EDGE,{"derivedFrom":[subQ2,makeQuery(id+"F3.opExtrude","SWEPT_FACE",FACE,{"disambiguationData":[OSD([sQuery(id+"F2.wireOp",EDGE,"E38.0")])]})]}),makeQuery(id+"F3.boolean.opBoolean","INTERSECT",EDGE,{"derivedFrom":[subQ2,makeQuery(id+"F3.opExtrude","SWEPT_FACE",FACE,{"disambiguationData":[OSD([sQuery(id+"F2.wireOp",EDGE,"E38.1")])]})]}),makeQuery(id+"F3.boolean.opBoolean","INTERSECT",EDGE,{"derivedFrom":[subQ2,makeQuery(id+"F3.opExtrude","SWEPT_FACE",FACE,{"disambiguationData":[OSD([sQuery(id+"F2.wireOp",EDGE,"E38.2")])]})]}),makeQuery(id+"F3.boolean.opBoolean","INTERSECT",EDGE,{"derivedFrom":[subQ2,makeQuery(id+"F3.opExtrude","SWEPT_FACE",FACE,{"disambiguationData":[OSD([sQuery(id+"F2.wireOp",EDGE,"E38.3")])]})]}),makeQuery(id+"F3.boolean.opBoolean","INTERSECT",EDGE,{"derivedFrom":[subQ2,makeQuery(id+"F3.opExtrude","SWEPT_FACE",FACE,{"disambiguationData":[OSD([sQuery(id+"F2.wireOp",EDGE,"E38.4")])]})]}),makeQuery(id+"F3.boolean.opBoolean","INTERSECT",EDGE,{"derivedFrom":[subQ2,makeQuery(id+"F3.opExtrude","SWEPT_FACE",FACE,{"disambiguationData":[OSD([sQuery(id+"F2.wireOp",EDGE,"E38.5")])]})]})]);}
            var Q26;
            {var subQ0=sQuery(id+"F0.wireOp",EDGE,"E6");var subQ1=sQuery(id+"F0.wireOp",EDGE,"E18.top");var subQ2=makeQuery(id+"F1.opExtrude","SWEPT_FACE",FACE,{"disambiguationData":[OSD([subQ0]),TDD([makeQuery(id+"F0.imprint","IMPRINT",EDGE,{"disambiguationData":[TD([[makeQuery(id+"F0.imprint","INTERSECT",VERTEX,{"derivedFrom":[subQ0,sQuery(id+"F0.wireOp",EDGE,"E9")]}),1.0]])],"derivedFrom":subQ0})])]});var subQ4=makeQuery(id+"F1.opExtrude","SWEPT_FACE",FACE,{"disambiguationData":[OSD([subQ0]),TDD([makeQuery(id+"F0.imprint","IMPRINT",EDGE,{"disambiguationData":[TD([[makeQuery(id+"F0.imprint","INTERSECT",VERTEX,{"derivedFrom":[subQ0,subQ1,sQuery(id+"F0.wireOp",EDGE,"E18.right")]}),1.0]])],"derivedFrom":subQ0})])]});var subQ5=makeQuery(id+"F1.opExtrude","SWEPT_FACE",FACE,{"disambiguationData":[OSD([subQ0]),TDD([makeQuery(id+"F0.imprint","IMPRINT",EDGE,{"disambiguationData":[TD([[makeQuery(id+"F0.imprint","INTERSECT",VERTEX,{"derivedFrom":[subQ0,sQuery(id+"F0.wireOp",EDGE,"E12")]}),-1.0]])],"derivedFrom":subQ0})])]});Q26=qUnion([makeQuery(id+"F3.boolean.opBoolean","INTERSECT",EDGE,{"derivedFrom":[subQ5,makeQuery(id+"F3.opExtrude","SWEPT_FACE",FACE,{"disambiguationData":[OSD([sQuery(id+"F2.wireOp",EDGE,"E41.0")])]})]}),makeQuery(id+"F3.boolean.opBoolean","INTERSECT",EDGE,{"derivedFrom":[subQ5,makeQuery(id+"F3.opExtrude","SWEPT_FACE",FACE,{"disambiguationData":[OSD([sQuery(id+"F2.wireOp",EDGE,"E41.1")])]})]}),makeQuery(id+"F3.boolean.opBoolean","INTERSECT",EDGE,{"derivedFrom":[subQ5,makeQuery(id+"F3.opExtrude","SWEPT_FACE",FACE,{"disambiguationData":[OSD([sQuery(id+"F2.wireOp",EDGE,"E41.2")])]})]}),makeQuery(id+"F3.boolean.opBoolean","INTERSECT",EDGE,{"derivedFrom":[subQ5,makeQuery(id+"F3.opExtrude","SWEPT_FACE",FACE,{"disambiguationData":[OSD([sQuery(id+"F2.wireOp",EDGE,"E41.3")])]})]}),makeQuery(id+"F3.boolean.opBoolean","INTERSECT",EDGE,{"derivedFrom":[subQ5,makeQuery(id+"F3.opExtrude","SWEPT_FACE",FACE,{"disambiguationData":[OSD([sQuery(id+"F2.wireOp",EDGE,"E41.4")])]})]}),makeQuery(id+"F3.boolean.opBoolean","INTERSECT",EDGE,{"derivedFrom":[subQ5,makeQuery(id+"F3.opExtrude","SWEPT_FACE",FACE,{"disambiguationData":[OSD([sQuery(id+"F2.wireOp",EDGE,"E41.5")])]})]}),makeQuery(id+"F3.boolean.opBoolean","INTERSECT",EDGE,{"derivedFrom":[subQ5,makeQuery(id+"F3.opExtrude","SWEPT_FACE",FACE,{"disambiguationData":[OSD([sQuery(id+"F2.wireOp",EDGE,"E42.0")])]})]}),makeQuery(id+"F3.boolean.opBoolean","INTERSECT",EDGE,{"derivedFrom":[subQ5,makeQuery(id+"F3.opExtrude","SWEPT_FACE",FACE,{"disambiguationData":[OSD([sQuery(id+"F2.wireOp",EDGE,"E42.1")])]})]}),makeQuery(id+"F3.boolean.opBoolean","INTERSECT",EDGE,{"derivedFrom":[subQ5,makeQuery(id+"F3.opExtrude","SWEPT_FACE",FACE,{"disambiguationData":[OSD([sQuery(id+"F2.wireOp",EDGE,"E42.2")])]})]}),makeQuery(id+"F3.boolean.opBoolean","INTERSECT",EDGE,{"derivedFrom":[subQ5,makeQuery(id+"F3.opExtrude","SWEPT_FACE",FACE,{"disambiguationData":[OSD([sQuery(id+"F2.wireOp",EDGE,"E42.3")])]})]}),makeQuery(id+"F3.boolean.opBoolean","INTERSECT",EDGE,{"derivedFrom":[subQ5,makeQuery(id+"F3.opExtrude","SWEPT_FACE",FACE,{"disambiguationData":[OSD([sQuery(id+"F2.wireOp",EDGE,"E42.4")])]})]}),makeQuery(id+"F3.boolean.opBoolean","INTERSECT",EDGE,{"derivedFrom":[subQ5,makeQuery(id+"F3.opExtrude","SWEPT_FACE",FACE,{"disambiguationData":[OSD([sQuery(id+"F2.wireOp",EDGE,"E42.5")])]})]}),makeQuery(id+"F3.boolean.opBoolean","INTERSECT",EDGE,{"derivedFrom":[subQ4,makeQuery(id+"F3.opExtrude","SWEPT_FACE",FACE,{"disambiguationData":[OSD([sQuery(id+"F2.wireOp",EDGE,"E39.0")])]})]}),makeQuery(id+"F3.boolean.opBoolean","INTERSECT",EDGE,{"derivedFrom":[subQ4,makeQuery(id+"F3.opExtrude","SWEPT_FACE",FACE,{"disambiguationData":[OSD([sQuery(id+"F2.wireOp",EDGE,"E39.1")])]})]}),makeQuery(id+"F3.boolean.opBoolean","INTERSECT",EDGE,{"derivedFrom":[subQ4,makeQuery(id+"F3.opExtrude","SWEPT_FACE",FACE,{"disambiguationData":[OSD([sQuery(id+"F2.wireOp",EDGE,"E39.2")])]})]}),makeQuery(id+"F3.boolean.opBoolean","INTERSECT",EDGE,{"derivedFrom":[subQ4,makeQuery(id+"F3.opExtrude","SWEPT_FACE",FACE,{"disambiguationData":[OSD([sQuery(id+"F2.wireOp",EDGE,"E39.3")])]})]}),makeQuery(id+"F3.boolean.opBoolean","INTERSECT",EDGE,{"derivedFrom":[subQ4,makeQuery(id+"F3.opExtrude","SWEPT_FACE",FACE,{"disambiguationData":[OSD([sQuery(id+"F2.wireOp",EDGE,"E39.4")])]})]}),makeQuery(id+"F3.boolean.opBoolean","INTERSECT",EDGE,{"derivedFrom":[subQ4,makeQuery(id+"F3.opExtrude","SWEPT_FACE",FACE,{"disambiguationData":[OSD([sQuery(id+"F2.wireOp",EDGE,"E39.5")])]})]}),makeQuery(id+"F3.boolean.opBoolean","INTERSECT",EDGE,{"derivedFrom":[subQ4,makeQuery(id+"F3.opExtrude","SWEPT_FACE",FACE,{"disambiguationData":[OSD([sQuery(id+"F2.wireOp",EDGE,"E40.0")])]})]}),makeQuery(id+"F3.boolean.opBoolean","INTERSECT",EDGE,{"derivedFrom":[subQ4,makeQuery(id+"F3.opExtrude","SWEPT_FACE",FACE,{"disambiguationData":[OSD([sQuery(id+"F2.wireOp",EDGE,"E40.1")])]})]}),makeQuery(id+"F3.boolean.opBoolean","INTERSECT",EDGE,{"derivedFrom":[subQ4,makeQuery(id+"F3.opExtrude","SWEPT_FACE",FACE,{"disambiguationData":[OSD([sQuery(id+"F2.wireOp",EDGE,"E40.2")])]})]}),makeQuery(id+"F3.boolean.opBoolean","INTERSECT",EDGE,{"derivedFrom":[subQ4,makeQuery(id+"F3.opExtrude","SWEPT_FACE",FACE,{"disambiguationData":[OSD([sQuery(id+"F2.wireOp",EDGE,"E40.3")])]})]}),makeQuery(id+"F3.boolean.opBoolean","INTERSECT",EDGE,{"derivedFrom":[subQ4,makeQuery(id+"F3.opExtrude","SWEPT_FACE",FACE,{"disambiguationData":[OSD([sQuery(id+"F2.wireOp",EDGE,"E40.4")])]})]}),makeQuery(id+"F3.boolean.opBoolean","INTERSECT",EDGE,{"derivedFrom":[subQ4,makeQuery(id+"F3.opExtrude","SWEPT_FACE",FACE,{"disambiguationData":[OSD([sQuery(id+"F2.wireOp",EDGE,"E40.5")])]})]}),makeQuery(id+"F3.boolean.opBoolean","INTERSECT",EDGE,{"derivedFrom":[subQ2,makeQuery(id+"F3.opExtrude","SWEPT_FACE",FACE,{"disambiguationData":[OSD([sQuery(id+"F2.wireOp",EDGE,"E36.0")])]})]}),makeQuery(id+"F3.boolean.opBoolean","INTERSECT",EDGE,{"derivedFrom":[subQ2,makeQuery(id+"F3.opExtrude","SWEPT_FACE",FACE,{"disambiguationData":[OSD([sQuery(id+"F2.wireOp",EDGE,"E36.1")])]})]}),makeQuery(id+"F3.boolean.opBoolean","INTERSECT",EDGE,{"derivedFrom":[subQ2,makeQuery(id+"F3.opExtrude","SWEPT_FACE",FACE,{"disambiguationData":[OSD([sQuery(id+"F2.wireOp",EDGE,"E36.2")])]})]}),makeQuery(id+"F3.boolean.opBoolean","INTERSECT",EDGE,{"derivedFrom":[subQ2,makeQuery(id+"F3.opExtrude","SWEPT_FACE",FACE,{"disambiguationData":[OSD([sQuery(id+"F2.wireOp",EDGE,"E36.3")])]})]}),makeQuery(id+"F3.boolean.opBoolean","INTERSECT",EDGE,{"derivedFrom":[subQ2,makeQuery(id+"F3.opExtrude","SWEPT_FACE",FACE,{"disambiguationData":[OSD([sQuery(id+"F2.wireOp",EDGE,"E36.4")])]})]}),makeQuery(id+"F3.boolean.opBoolean","INTERSECT",EDGE,{"derivedFrom":[subQ2,makeQuery(id+"F3.opExtrude","SWEPT_FACE",FACE,{"disambiguationData":[OSD([sQuery(id+"F2.wireOp",EDGE,"E36.5")])]})]}),makeQuery(id+"F3.boolean.opBoolean","INTERSECT",EDGE,{"derivedFrom":[subQ2,makeQuery(id+"F3.opExtrude","SWEPT_FACE",FACE,{"disambiguationData":[OSD([sQuery(id+"F2.wireOp",EDGE,"E37.0")])]})]}),makeQuery(id+"F3.boolean.opBoolean","INTERSECT",EDGE,{"derivedFrom":[subQ2,makeQuery(id+"F3.opExtrude","SWEPT_FACE",FACE,{"disambiguationData":[OSD([sQuery(id+"F2.wireOp",EDGE,"E37.1")])]})]}),makeQuery(id+"F3.boolean.opBoolean","INTERSECT",EDGE,{"derivedFrom":[subQ2,makeQuery(id+"F3.opExtrude","SWEPT_FACE",FACE,{"disambiguationData":[OSD([sQuery(id+"F2.wireOp",EDGE,"E37.2")])]})]}),makeQuery(id+"F3.boolean.opBoolean","INTERSECT",EDGE,{"derivedFrom":[subQ2,makeQuery(id+"F3.opExtrude","SWEPT_FACE",FACE,{"disambiguationData":[OSD([sQuery(id+"F2.wireOp",EDGE,"E37.3")])]})]}),makeQuery(id+"F3.boolean.opBoolean","INTERSECT",EDGE,{"derivedFrom":[subQ2,makeQuery(id+"F3.opExtrude","SWEPT_FACE",FACE,{"disambiguationData":[OSD([sQuery(id+"F2.wireOp",EDGE,"E37.4")])]})]}),makeQuery(id+"F3.boolean.opBoolean","INTERSECT",EDGE,{"derivedFrom":[subQ2,makeQuery(id+"F3.opExtrude","SWEPT_FACE",FACE,{"disambiguationData":[OSD([sQuery(id+"F2.wireOp",EDGE,"E37.5")])]})]}),makeQuery(id+"F3.boolean.opBoolean","INTERSECT",EDGE,{"derivedFrom":[subQ2,makeQuery(id+"F3.opExtrude","SWEPT_FACE",FACE,{"disambiguationData":[OSD([sQuery(id+"F2.wireOp",EDGE,"E38.0")])]})]}),makeQuery(id+"F3.boolean.opBoolean","INTERSECT",EDGE,{"derivedFrom":[subQ2,makeQuery(id+"F3.opExtrude","SWEPT_FACE",FACE,{"disambiguationData":[OSD([sQuery(id+"F2.wireOp",EDGE,"E38.1")])]})]}),makeQuery(id+"F3.boolean.opBoolean","INTERSECT",EDGE,{"derivedFrom":[subQ2,makeQuery(id+"F3.opExtrude","SWEPT_FACE",FACE,{"disambiguationData":[OSD([sQuery(id+"F2.wireOp",EDGE,"E38.2")])]})]}),makeQuery(id+"F3.boolean.opBoolean","INTERSECT",EDGE,{"derivedFrom":[subQ2,makeQuery(id+"F3.opExtrude","SWEPT_FACE",FACE,{"disambiguationData":[OSD([sQuery(id+"F2.wireOp",EDGE,"E38.3")])]})]}),makeQuery(id+"F3.boolean.opBoolean","INTERSECT",EDGE,{"derivedFrom":[subQ2,makeQuery(id+"F3.opExtrude","SWEPT_FACE",FACE,{"disambiguationData":[OSD([sQuery(id+"F2.wireOp",EDGE,"E38.4")])]})]}),makeQuery(id+"F3.boolean.opBoolean","INTERSECT",EDGE,{"derivedFrom":[subQ2,makeQuery(id+"F3.opExtrude","SWEPT_FACE",FACE,{"disambiguationData":[OSD([sQuery(id+"F2.wireOp",EDGE,"E38.5")])]})]})]);}
            var Q27;
            {var subQ0=sQuery(id+"F0.wireOp",EDGE,"E6");var subQ1=sQuery(id+"F0.wireOp",EDGE,"E18.top");var subQ2=makeQuery(id+"F1.opExtrude","SWEPT_FACE",FACE,{"disambiguationData":[OSD([subQ0]),TDD([makeQuery(id+"F0.imprint","IMPRINT",EDGE,{"disambiguationData":[TD([[makeQuery(id+"F0.imprint","INTERSECT",VERTEX,{"derivedFrom":[subQ0,sQuery(id+"F0.wireOp",EDGE,"E9")]}),1.0]])],"derivedFrom":subQ0})])]});var subQ4=makeQuery(id+"F1.opExtrude","SWEPT_FACE",FACE,{"disambiguationData":[OSD([subQ0]),TDD([makeQuery(id+"F0.imprint","IMPRINT",EDGE,{"disambiguationData":[TD([[makeQuery(id+"F0.imprint","INTERSECT",VERTEX,{"derivedFrom":[subQ0,subQ1,sQuery(id+"F0.wireOp",EDGE,"E18.right")]}),1.0]])],"derivedFrom":subQ0})])]});var subQ5=makeQuery(id+"F1.opExtrude","SWEPT_FACE",FACE,{"disambiguationData":[OSD([subQ0]),TDD([makeQuery(id+"F0.imprint","IMPRINT",EDGE,{"disambiguationData":[TD([[makeQuery(id+"F0.imprint","INTERSECT",VERTEX,{"derivedFrom":[subQ0,sQuery(id+"F0.wireOp",EDGE,"E12")]}),-1.0]])],"derivedFrom":subQ0})])]});Q27=qUnion([makeQuery(id+"F3.boolean.opBoolean","INTERSECT",EDGE,{"derivedFrom":[subQ5,makeQuery(id+"F3.opExtrude","SWEPT_FACE",FACE,{"disambiguationData":[OSD([sQuery(id+"F2.wireOp",EDGE,"E41.0")])]})]}),makeQuery(id+"F3.boolean.opBoolean","INTERSECT",EDGE,{"derivedFrom":[subQ5,makeQuery(id+"F3.opExtrude","SWEPT_FACE",FACE,{"disambiguationData":[OSD([sQuery(id+"F2.wireOp",EDGE,"E41.1")])]})]}),makeQuery(id+"F3.boolean.opBoolean","INTERSECT",EDGE,{"derivedFrom":[subQ5,makeQuery(id+"F3.opExtrude","SWEPT_FACE",FACE,{"disambiguationData":[OSD([sQuery(id+"F2.wireOp",EDGE,"E41.2")])]})]}),makeQuery(id+"F3.boolean.opBoolean","INTERSECT",EDGE,{"derivedFrom":[subQ5,makeQuery(id+"F3.opExtrude","SWEPT_FACE",FACE,{"disambiguationData":[OSD([sQuery(id+"F2.wireOp",EDGE,"E41.3")])]})]}),makeQuery(id+"F3.boolean.opBoolean","INTERSECT",EDGE,{"derivedFrom":[subQ5,makeQuery(id+"F3.opExtrude","SWEPT_FACE",FACE,{"disambiguationData":[OSD([sQuery(id+"F2.wireOp",EDGE,"E41.4")])]})]}),makeQuery(id+"F3.boolean.opBoolean","INTERSECT",EDGE,{"derivedFrom":[subQ5,makeQuery(id+"F3.opExtrude","SWEPT_FACE",FACE,{"disambiguationData":[OSD([sQuery(id+"F2.wireOp",EDGE,"E41.5")])]})]}),makeQuery(id+"F3.boolean.opBoolean","INTERSECT",EDGE,{"derivedFrom":[subQ5,makeQuery(id+"F3.opExtrude","SWEPT_FACE",FACE,{"disambiguationData":[OSD([sQuery(id+"F2.wireOp",EDGE,"E42.0")])]})]}),makeQuery(id+"F3.boolean.opBoolean","INTERSECT",EDGE,{"derivedFrom":[subQ5,makeQuery(id+"F3.opExtrude","SWEPT_FACE",FACE,{"disambiguationData":[OSD([sQuery(id+"F2.wireOp",EDGE,"E42.1")])]})]}),makeQuery(id+"F3.boolean.opBoolean","INTERSECT",EDGE,{"derivedFrom":[subQ5,makeQuery(id+"F3.opExtrude","SWEPT_FACE",FACE,{"disambiguationData":[OSD([sQuery(id+"F2.wireOp",EDGE,"E42.2")])]})]}),makeQuery(id+"F3.boolean.opBoolean","INTERSECT",EDGE,{"derivedFrom":[subQ5,makeQuery(id+"F3.opExtrude","SWEPT_FACE",FACE,{"disambiguationData":[OSD([sQuery(id+"F2.wireOp",EDGE,"E42.3")])]})]}),makeQuery(id+"F3.boolean.opBoolean","INTERSECT",EDGE,{"derivedFrom":[subQ5,makeQuery(id+"F3.opExtrude","SWEPT_FACE",FACE,{"disambiguationData":[OSD([sQuery(id+"F2.wireOp",EDGE,"E42.4")])]})]}),makeQuery(id+"F3.boolean.opBoolean","INTERSECT",EDGE,{"derivedFrom":[subQ5,makeQuery(id+"F3.opExtrude","SWEPT_FACE",FACE,{"disambiguationData":[OSD([sQuery(id+"F2.wireOp",EDGE,"E42.5")])]})]}),makeQuery(id+"F3.boolean.opBoolean","INTERSECT",EDGE,{"derivedFrom":[subQ4,makeQuery(id+"F3.opExtrude","SWEPT_FACE",FACE,{"disambiguationData":[OSD([sQuery(id+"F2.wireOp",EDGE,"E39.0")])]})]}),makeQuery(id+"F3.boolean.opBoolean","INTERSECT",EDGE,{"derivedFrom":[subQ4,makeQuery(id+"F3.opExtrude","SWEPT_FACE",FACE,{"disambiguationData":[OSD([sQuery(id+"F2.wireOp",EDGE,"E39.1")])]})]}),makeQuery(id+"F3.boolean.opBoolean","INTERSECT",EDGE,{"derivedFrom":[subQ4,makeQuery(id+"F3.opExtrude","SWEPT_FACE",FACE,{"disambiguationData":[OSD([sQuery(id+"F2.wireOp",EDGE,"E39.2")])]})]}),makeQuery(id+"F3.boolean.opBoolean","INTERSECT",EDGE,{"derivedFrom":[subQ4,makeQuery(id+"F3.opExtrude","SWEPT_FACE",FACE,{"disambiguationData":[OSD([sQuery(id+"F2.wireOp",EDGE,"E39.3")])]})]}),makeQuery(id+"F3.boolean.opBoolean","INTERSECT",EDGE,{"derivedFrom":[subQ4,makeQuery(id+"F3.opExtrude","SWEPT_FACE",FACE,{"disambiguationData":[OSD([sQuery(id+"F2.wireOp",EDGE,"E39.4")])]})]}),makeQuery(id+"F3.boolean.opBoolean","INTERSECT",EDGE,{"derivedFrom":[subQ4,makeQuery(id+"F3.opExtrude","SWEPT_FACE",FACE,{"disambiguationData":[OSD([sQuery(id+"F2.wireOp",EDGE,"E39.5")])]})]}),makeQuery(id+"F3.boolean.opBoolean","INTERSECT",EDGE,{"derivedFrom":[subQ4,makeQuery(id+"F3.opExtrude","SWEPT_FACE",FACE,{"disambiguationData":[OSD([sQuery(id+"F2.wireOp",EDGE,"E40.0")])]})]}),makeQuery(id+"F3.boolean.opBoolean","INTERSECT",EDGE,{"derivedFrom":[subQ4,makeQuery(id+"F3.opExtrude","SWEPT_FACE",FACE,{"disambiguationData":[OSD([sQuery(id+"F2.wireOp",EDGE,"E40.1")])]})]}),makeQuery(id+"F3.boolean.opBoolean","INTERSECT",EDGE,{"derivedFrom":[subQ4,makeQuery(id+"F3.opExtrude","SWEPT_FACE",FACE,{"disambiguationData":[OSD([sQuery(id+"F2.wireOp",EDGE,"E40.2")])]})]}),makeQuery(id+"F3.boolean.opBoolean","INTERSECT",EDGE,{"derivedFrom":[subQ4,makeQuery(id+"F3.opExtrude","SWEPT_FACE",FACE,{"disambiguationData":[OSD([sQuery(id+"F2.wireOp",EDGE,"E40.3")])]})]}),makeQuery(id+"F3.boolean.opBoolean","INTERSECT",EDGE,{"derivedFrom":[subQ4,makeQuery(id+"F3.opExtrude","SWEPT_FACE",FACE,{"disambiguationData":[OSD([sQuery(id+"F2.wireOp",EDGE,"E40.4")])]})]}),makeQuery(id+"F3.boolean.opBoolean","INTERSECT",EDGE,{"derivedFrom":[subQ4,makeQuery(id+"F3.opExtrude","SWEPT_FACE",FACE,{"disambiguationData":[OSD([sQuery(id+"F2.wireOp",EDGE,"E40.5")])]})]}),makeQuery(id+"F3.boolean.opBoolean","INTERSECT",EDGE,{"derivedFrom":[subQ2,makeQuery(id+"F3.opExtrude","SWEPT_FACE",FACE,{"disambiguationData":[OSD([sQuery(id+"F2.wireOp",EDGE,"E36.0")])]})]}),makeQuery(id+"F3.boolean.opBoolean","INTERSECT",EDGE,{"derivedFrom":[subQ2,makeQuery(id+"F3.opExtrude","SWEPT_FACE",FACE,{"disambiguationData":[OSD([sQuery(id+"F2.wireOp",EDGE,"E36.1")])]})]}),makeQuery(id+"F3.boolean.opBoolean","INTERSECT",EDGE,{"derivedFrom":[subQ2,makeQuery(id+"F3.opExtrude","SWEPT_FACE",FACE,{"disambiguationData":[OSD([sQuery(id+"F2.wireOp",EDGE,"E36.2")])]})]}),makeQuery(id+"F3.boolean.opBoolean","INTERSECT",EDGE,{"derivedFrom":[subQ2,makeQuery(id+"F3.opExtrude","SWEPT_FACE",FACE,{"disambiguationData":[OSD([sQuery(id+"F2.wireOp",EDGE,"E36.3")])]})]}),makeQuery(id+"F3.boolean.opBoolean","INTERSECT",EDGE,{"derivedFrom":[subQ2,makeQuery(id+"F3.opExtrude","SWEPT_FACE",FACE,{"disambiguationData":[OSD([sQuery(id+"F2.wireOp",EDGE,"E36.4")])]})]}),makeQuery(id+"F3.boolean.opBoolean","INTERSECT",EDGE,{"derivedFrom":[subQ2,makeQuery(id+"F3.opExtrude","SWEPT_FACE",FACE,{"disambiguationData":[OSD([sQuery(id+"F2.wireOp",EDGE,"E36.5")])]})]}),makeQuery(id+"F3.boolean.opBoolean","INTERSECT",EDGE,{"derivedFrom":[subQ2,makeQuery(id+"F3.opExtrude","SWEPT_FACE",FACE,{"disambiguationData":[OSD([sQuery(id+"F2.wireOp",EDGE,"E37.0")])]})]}),makeQuery(id+"F3.boolean.opBoolean","INTERSECT",EDGE,{"derivedFrom":[subQ2,makeQuery(id+"F3.opExtrude","SWEPT_FACE",FACE,{"disambiguationData":[OSD([sQuery(id+"F2.wireOp",EDGE,"E37.1")])]})]}),makeQuery(id+"F3.boolean.opBoolean","INTERSECT",EDGE,{"derivedFrom":[subQ2,makeQuery(id+"F3.opExtrude","SWEPT_FACE",FACE,{"disambiguationData":[OSD([sQuery(id+"F2.wireOp",EDGE,"E37.2")])]})]}),makeQuery(id+"F3.boolean.opBoolean","INTERSECT",EDGE,{"derivedFrom":[subQ2,makeQuery(id+"F3.opExtrude","SWEPT_FACE",FACE,{"disambiguationData":[OSD([sQuery(id+"F2.wireOp",EDGE,"E37.3")])]})]}),makeQuery(id+"F3.boolean.opBoolean","INTERSECT",EDGE,{"derivedFrom":[subQ2,makeQuery(id+"F3.opExtrude","SWEPT_FACE",FACE,{"disambiguationData":[OSD([sQuery(id+"F2.wireOp",EDGE,"E37.4")])]})]}),makeQuery(id+"F3.boolean.opBoolean","INTERSECT",EDGE,{"derivedFrom":[subQ2,makeQuery(id+"F3.opExtrude","SWEPT_FACE",FACE,{"disambiguationData":[OSD([sQuery(id+"F2.wireOp",EDGE,"E37.5")])]})]}),makeQuery(id+"F3.boolean.opBoolean","INTERSECT",EDGE,{"derivedFrom":[subQ2,makeQuery(id+"F3.opExtrude","SWEPT_FACE",FACE,{"disambiguationData":[OSD([sQuery(id+"F2.wireOp",EDGE,"E38.0")])]})]}),makeQuery(id+"F3.boolean.opBoolean","INTERSECT",EDGE,{"derivedFrom":[subQ2,makeQuery(id+"F3.opExtrude","SWEPT_FACE",FACE,{"disambiguationData":[OSD([sQuery(id+"F2.wireOp",EDGE,"E38.1")])]})]}),makeQuery(id+"F3.boolean.opBoolean","INTERSECT",EDGE,{"derivedFrom":[subQ2,makeQuery(id+"F3.opExtrude","SWEPT_FACE",FACE,{"disambiguationData":[OSD([sQuery(id+"F2.wireOp",EDGE,"E38.2")])]})]}),makeQuery(id+"F3.boolean.opBoolean","INTERSECT",EDGE,{"derivedFrom":[subQ2,makeQuery(id+"F3.opExtrude","SWEPT_FACE",FACE,{"disambiguationData":[OSD([sQuery(id+"F2.wireOp",EDGE,"E38.3")])]})]}),makeQuery(id+"F3.boolean.opBoolean","INTERSECT",EDGE,{"derivedFrom":[subQ2,makeQuery(id+"F3.opExtrude","SWEPT_FACE",FACE,{"disambiguationData":[OSD([sQuery(id+"F2.wireOp",EDGE,"E38.4")])]})]}),makeQuery(id+"F3.boolean.opBoolean","INTERSECT",EDGE,{"derivedFrom":[subQ2,makeQuery(id+"F3.opExtrude","SWEPT_FACE",FACE,{"disambiguationData":[OSD([sQuery(id+"F2.wireOp",EDGE,"E38.5")])]})]})]);}
            var Q28;
            {var subQ0=sQuery(id+"F0.wireOp",EDGE,"E6");var subQ1=sQuery(id+"F0.wireOp",EDGE,"E18.top");var subQ2=makeQuery(id+"F1.opExtrude","SWEPT_FACE",FACE,{"disambiguationData":[OSD([subQ0]),TDD([makeQuery(id+"F0.imprint","IMPRINT",EDGE,{"disambiguationData":[TD([[makeQuery(id+"F0.imprint","INTERSECT",VERTEX,{"derivedFrom":[subQ0,sQuery(id+"F0.wireOp",EDGE,"E9")]}),1.0]])],"derivedFrom":subQ0})])]});var subQ4=makeQuery(id+"F1.opExtrude","SWEPT_FACE",FACE,{"disambiguationData":[OSD([subQ0]),TDD([makeQuery(id+"F0.imprint","IMPRINT",EDGE,{"disambiguationData":[TD([[makeQuery(id+"F0.imprint","INTERSECT",VERTEX,{"derivedFrom":[subQ0,subQ1,sQuery(id+"F0.wireOp",EDGE,"E18.right")]}),1.0]])],"derivedFrom":subQ0})])]});var subQ5=makeQuery(id+"F1.opExtrude","SWEPT_FACE",FACE,{"disambiguationData":[OSD([subQ0]),TDD([makeQuery(id+"F0.imprint","IMPRINT",EDGE,{"disambiguationData":[TD([[makeQuery(id+"F0.imprint","INTERSECT",VERTEX,{"derivedFrom":[subQ0,sQuery(id+"F0.wireOp",EDGE,"E12")]}),-1.0]])],"derivedFrom":subQ0})])]});Q28=qUnion([makeQuery(id+"F3.boolean.opBoolean","INTERSECT",EDGE,{"derivedFrom":[subQ5,makeQuery(id+"F3.opExtrude","SWEPT_FACE",FACE,{"disambiguationData":[OSD([sQuery(id+"F2.wireOp",EDGE,"E41.0")])]})]}),makeQuery(id+"F3.boolean.opBoolean","INTERSECT",EDGE,{"derivedFrom":[subQ5,makeQuery(id+"F3.opExtrude","SWEPT_FACE",FACE,{"disambiguationData":[OSD([sQuery(id+"F2.wireOp",EDGE,"E41.1")])]})]}),makeQuery(id+"F3.boolean.opBoolean","INTERSECT",EDGE,{"derivedFrom":[subQ5,makeQuery(id+"F3.opExtrude","SWEPT_FACE",FACE,{"disambiguationData":[OSD([sQuery(id+"F2.wireOp",EDGE,"E41.2")])]})]}),makeQuery(id+"F3.boolean.opBoolean","INTERSECT",EDGE,{"derivedFrom":[subQ5,makeQuery(id+"F3.opExtrude","SWEPT_FACE",FACE,{"disambiguationData":[OSD([sQuery(id+"F2.wireOp",EDGE,"E41.3")])]})]}),makeQuery(id+"F3.boolean.opBoolean","INTERSECT",EDGE,{"derivedFrom":[subQ5,makeQuery(id+"F3.opExtrude","SWEPT_FACE",FACE,{"disambiguationData":[OSD([sQuery(id+"F2.wireOp",EDGE,"E41.4")])]})]}),makeQuery(id+"F3.boolean.opBoolean","INTERSECT",EDGE,{"derivedFrom":[subQ5,makeQuery(id+"F3.opExtrude","SWEPT_FACE",FACE,{"disambiguationData":[OSD([sQuery(id+"F2.wireOp",EDGE,"E41.5")])]})]}),makeQuery(id+"F3.boolean.opBoolean","INTERSECT",EDGE,{"derivedFrom":[subQ5,makeQuery(id+"F3.opExtrude","SWEPT_FACE",FACE,{"disambiguationData":[OSD([sQuery(id+"F2.wireOp",EDGE,"E42.0")])]})]}),makeQuery(id+"F3.boolean.opBoolean","INTERSECT",EDGE,{"derivedFrom":[subQ5,makeQuery(id+"F3.opExtrude","SWEPT_FACE",FACE,{"disambiguationData":[OSD([sQuery(id+"F2.wireOp",EDGE,"E42.1")])]})]}),makeQuery(id+"F3.boolean.opBoolean","INTERSECT",EDGE,{"derivedFrom":[subQ5,makeQuery(id+"F3.opExtrude","SWEPT_FACE",FACE,{"disambiguationData":[OSD([sQuery(id+"F2.wireOp",EDGE,"E42.2")])]})]}),makeQuery(id+"F3.boolean.opBoolean","INTERSECT",EDGE,{"derivedFrom":[subQ5,makeQuery(id+"F3.opExtrude","SWEPT_FACE",FACE,{"disambiguationData":[OSD([sQuery(id+"F2.wireOp",EDGE,"E42.3")])]})]}),makeQuery(id+"F3.boolean.opBoolean","INTERSECT",EDGE,{"derivedFrom":[subQ5,makeQuery(id+"F3.opExtrude","SWEPT_FACE",FACE,{"disambiguationData":[OSD([sQuery(id+"F2.wireOp",EDGE,"E42.4")])]})]}),makeQuery(id+"F3.boolean.opBoolean","INTERSECT",EDGE,{"derivedFrom":[subQ5,makeQuery(id+"F3.opExtrude","SWEPT_FACE",FACE,{"disambiguationData":[OSD([sQuery(id+"F2.wireOp",EDGE,"E42.5")])]})]}),makeQuery(id+"F3.boolean.opBoolean","INTERSECT",EDGE,{"derivedFrom":[subQ4,makeQuery(id+"F3.opExtrude","SWEPT_FACE",FACE,{"disambiguationData":[OSD([sQuery(id+"F2.wireOp",EDGE,"E39.0")])]})]}),makeQuery(id+"F3.boolean.opBoolean","INTERSECT",EDGE,{"derivedFrom":[subQ4,makeQuery(id+"F3.opExtrude","SWEPT_FACE",FACE,{"disambiguationData":[OSD([sQuery(id+"F2.wireOp",EDGE,"E39.1")])]})]}),makeQuery(id+"F3.boolean.opBoolean","INTERSECT",EDGE,{"derivedFrom":[subQ4,makeQuery(id+"F3.opExtrude","SWEPT_FACE",FACE,{"disambiguationData":[OSD([sQuery(id+"F2.wireOp",EDGE,"E39.2")])]})]}),makeQuery(id+"F3.boolean.opBoolean","INTERSECT",EDGE,{"derivedFrom":[subQ4,makeQuery(id+"F3.opExtrude","SWEPT_FACE",FACE,{"disambiguationData":[OSD([sQuery(id+"F2.wireOp",EDGE,"E39.3")])]})]}),makeQuery(id+"F3.boolean.opBoolean","INTERSECT",EDGE,{"derivedFrom":[subQ4,makeQuery(id+"F3.opExtrude","SWEPT_FACE",FACE,{"disambiguationData":[OSD([sQuery(id+"F2.wireOp",EDGE,"E39.4")])]})]}),makeQuery(id+"F3.boolean.opBoolean","INTERSECT",EDGE,{"derivedFrom":[subQ4,makeQuery(id+"F3.opExtrude","SWEPT_FACE",FACE,{"disambiguationData":[OSD([sQuery(id+"F2.wireOp",EDGE,"E39.5")])]})]}),makeQuery(id+"F3.boolean.opBoolean","INTERSECT",EDGE,{"derivedFrom":[subQ4,makeQuery(id+"F3.opExtrude","SWEPT_FACE",FACE,{"disambiguationData":[OSD([sQuery(id+"F2.wireOp",EDGE,"E40.0")])]})]}),makeQuery(id+"F3.boolean.opBoolean","INTERSECT",EDGE,{"derivedFrom":[subQ4,makeQuery(id+"F3.opExtrude","SWEPT_FACE",FACE,{"disambiguationData":[OSD([sQuery(id+"F2.wireOp",EDGE,"E40.1")])]})]}),makeQuery(id+"F3.boolean.opBoolean","INTERSECT",EDGE,{"derivedFrom":[subQ4,makeQuery(id+"F3.opExtrude","SWEPT_FACE",FACE,{"disambiguationData":[OSD([sQuery(id+"F2.wireOp",EDGE,"E40.2")])]})]}),makeQuery(id+"F3.boolean.opBoolean","INTERSECT",EDGE,{"derivedFrom":[subQ4,makeQuery(id+"F3.opExtrude","SWEPT_FACE",FACE,{"disambiguationData":[OSD([sQuery(id+"F2.wireOp",EDGE,"E40.3")])]})]}),makeQuery(id+"F3.boolean.opBoolean","INTERSECT",EDGE,{"derivedFrom":[subQ4,makeQuery(id+"F3.opExtrude","SWEPT_FACE",FACE,{"disambiguationData":[OSD([sQuery(id+"F2.wireOp",EDGE,"E40.4")])]})]}),makeQuery(id+"F3.boolean.opBoolean","INTERSECT",EDGE,{"derivedFrom":[subQ4,makeQuery(id+"F3.opExtrude","SWEPT_FACE",FACE,{"disambiguationData":[OSD([sQuery(id+"F2.wireOp",EDGE,"E40.5")])]})]}),makeQuery(id+"F3.boolean.opBoolean","INTERSECT",EDGE,{"derivedFrom":[subQ2,makeQuery(id+"F3.opExtrude","SWEPT_FACE",FACE,{"disambiguationData":[OSD([sQuery(id+"F2.wireOp",EDGE,"E36.0")])]})]}),makeQuery(id+"F3.boolean.opBoolean","INTERSECT",EDGE,{"derivedFrom":[subQ2,makeQuery(id+"F3.opExtrude","SWEPT_FACE",FACE,{"disambiguationData":[OSD([sQuery(id+"F2.wireOp",EDGE,"E36.1")])]})]}),makeQuery(id+"F3.boolean.opBoolean","INTERSECT",EDGE,{"derivedFrom":[subQ2,makeQuery(id+"F3.opExtrude","SWEPT_FACE",FACE,{"disambiguationData":[OSD([sQuery(id+"F2.wireOp",EDGE,"E36.2")])]})]}),makeQuery(id+"F3.boolean.opBoolean","INTERSECT",EDGE,{"derivedFrom":[subQ2,makeQuery(id+"F3.opExtrude","SWEPT_FACE",FACE,{"disambiguationData":[OSD([sQuery(id+"F2.wireOp",EDGE,"E36.3")])]})]}),makeQuery(id+"F3.boolean.opBoolean","INTERSECT",EDGE,{"derivedFrom":[subQ2,makeQuery(id+"F3.opExtrude","SWEPT_FACE",FACE,{"disambiguationData":[OSD([sQuery(id+"F2.wireOp",EDGE,"E36.4")])]})]}),makeQuery(id+"F3.boolean.opBoolean","INTERSECT",EDGE,{"derivedFrom":[subQ2,makeQuery(id+"F3.opExtrude","SWEPT_FACE",FACE,{"disambiguationData":[OSD([sQuery(id+"F2.wireOp",EDGE,"E36.5")])]})]}),makeQuery(id+"F3.boolean.opBoolean","INTERSECT",EDGE,{"derivedFrom":[subQ2,makeQuery(id+"F3.opExtrude","SWEPT_FACE",FACE,{"disambiguationData":[OSD([sQuery(id+"F2.wireOp",EDGE,"E37.0")])]})]}),makeQuery(id+"F3.boolean.opBoolean","INTERSECT",EDGE,{"derivedFrom":[subQ2,makeQuery(id+"F3.opExtrude","SWEPT_FACE",FACE,{"disambiguationData":[OSD([sQuery(id+"F2.wireOp",EDGE,"E37.1")])]})]}),makeQuery(id+"F3.boolean.opBoolean","INTERSECT",EDGE,{"derivedFrom":[subQ2,makeQuery(id+"F3.opExtrude","SWEPT_FACE",FACE,{"disambiguationData":[OSD([sQuery(id+"F2.wireOp",EDGE,"E37.2")])]})]}),makeQuery(id+"F3.boolean.opBoolean","INTERSECT",EDGE,{"derivedFrom":[subQ2,makeQuery(id+"F3.opExtrude","SWEPT_FACE",FACE,{"disambiguationData":[OSD([sQuery(id+"F2.wireOp",EDGE,"E37.3")])]})]}),makeQuery(id+"F3.boolean.opBoolean","INTERSECT",EDGE,{"derivedFrom":[subQ2,makeQuery(id+"F3.opExtrude","SWEPT_FACE",FACE,{"disambiguationData":[OSD([sQuery(id+"F2.wireOp",EDGE,"E37.4")])]})]}),makeQuery(id+"F3.boolean.opBoolean","INTERSECT",EDGE,{"derivedFrom":[subQ2,makeQuery(id+"F3.opExtrude","SWEPT_FACE",FACE,{"disambiguationData":[OSD([sQuery(id+"F2.wireOp",EDGE,"E37.5")])]})]}),makeQuery(id+"F3.boolean.opBoolean","INTERSECT",EDGE,{"derivedFrom":[subQ2,makeQuery(id+"F3.opExtrude","SWEPT_FACE",FACE,{"disambiguationData":[OSD([sQuery(id+"F2.wireOp",EDGE,"E38.0")])]})]}),makeQuery(id+"F3.boolean.opBoolean","INTERSECT",EDGE,{"derivedFrom":[subQ2,makeQuery(id+"F3.opExtrude","SWEPT_FACE",FACE,{"disambiguationData":[OSD([sQuery(id+"F2.wireOp",EDGE,"E38.1")])]})]}),makeQuery(id+"F3.boolean.opBoolean","INTERSECT",EDGE,{"derivedFrom":[subQ2,makeQuery(id+"F3.opExtrude","SWEPT_FACE",FACE,{"disambiguationData":[OSD([sQuery(id+"F2.wireOp",EDGE,"E38.2")])]})]}),makeQuery(id+"F3.boolean.opBoolean","INTERSECT",EDGE,{"derivedFrom":[subQ2,makeQuery(id+"F3.opExtrude","SWEPT_FACE",FACE,{"disambiguationData":[OSD([sQuery(id+"F2.wireOp",EDGE,"E38.3")])]})]}),makeQuery(id+"F3.boolean.opBoolean","INTERSECT",EDGE,{"derivedFrom":[subQ2,makeQuery(id+"F3.opExtrude","SWEPT_FACE",FACE,{"disambiguationData":[OSD([sQuery(id+"F2.wireOp",EDGE,"E38.4")])]})]}),makeQuery(id+"F3.boolean.opBoolean","INTERSECT",EDGE,{"derivedFrom":[subQ2,makeQuery(id+"F3.opExtrude","SWEPT_FACE",FACE,{"disambiguationData":[OSD([sQuery(id+"F2.wireOp",EDGE,"E38.5")])]})]})]);}
            var Q29;
            {var subQ0=sQuery(id+"F0.wireOp",EDGE,"E6");var subQ1=sQuery(id+"F0.wireOp",EDGE,"E18.top");var subQ2=makeQuery(id+"F1.opExtrude","SWEPT_FACE",FACE,{"disambiguationData":[OSD([subQ0]),TDD([makeQuery(id+"F0.imprint","IMPRINT",EDGE,{"disambiguationData":[TD([[makeQuery(id+"F0.imprint","INTERSECT",VERTEX,{"derivedFrom":[subQ0,sQuery(id+"F0.wireOp",EDGE,"E9")]}),1.0]])],"derivedFrom":subQ0})])]});var subQ4=makeQuery(id+"F1.opExtrude","SWEPT_FACE",FACE,{"disambiguationData":[OSD([subQ0]),TDD([makeQuery(id+"F0.imprint","IMPRINT",EDGE,{"disambiguationData":[TD([[makeQuery(id+"F0.imprint","INTERSECT",VERTEX,{"derivedFrom":[subQ0,subQ1,sQuery(id+"F0.wireOp",EDGE,"E18.right")]}),1.0]])],"derivedFrom":subQ0})])]});var subQ5=makeQuery(id+"F1.opExtrude","SWEPT_FACE",FACE,{"disambiguationData":[OSD([subQ0]),TDD([makeQuery(id+"F0.imprint","IMPRINT",EDGE,{"disambiguationData":[TD([[makeQuery(id+"F0.imprint","INTERSECT",VERTEX,{"derivedFrom":[subQ0,sQuery(id+"F0.wireOp",EDGE,"E12")]}),-1.0]])],"derivedFrom":subQ0})])]});Q29=qUnion([makeQuery(id+"F3.boolean.opBoolean","INTERSECT",EDGE,{"derivedFrom":[subQ5,makeQuery(id+"F3.opExtrude","SWEPT_FACE",FACE,{"disambiguationData":[OSD([sQuery(id+"F2.wireOp",EDGE,"E41.0")])]})]}),makeQuery(id+"F3.boolean.opBoolean","INTERSECT",EDGE,{"derivedFrom":[subQ5,makeQuery(id+"F3.opExtrude","SWEPT_FACE",FACE,{"disambiguationData":[OSD([sQuery(id+"F2.wireOp",EDGE,"E41.1")])]})]}),makeQuery(id+"F3.boolean.opBoolean","INTERSECT",EDGE,{"derivedFrom":[subQ5,makeQuery(id+"F3.opExtrude","SWEPT_FACE",FACE,{"disambiguationData":[OSD([sQuery(id+"F2.wireOp",EDGE,"E41.2")])]})]}),makeQuery(id+"F3.boolean.opBoolean","INTERSECT",EDGE,{"derivedFrom":[subQ5,makeQuery(id+"F3.opExtrude","SWEPT_FACE",FACE,{"disambiguationData":[OSD([sQuery(id+"F2.wireOp",EDGE,"E41.3")])]})]}),makeQuery(id+"F3.boolean.opBoolean","INTERSECT",EDGE,{"derivedFrom":[subQ5,makeQuery(id+"F3.opExtrude","SWEPT_FACE",FACE,{"disambiguationData":[OSD([sQuery(id+"F2.wireOp",EDGE,"E41.4")])]})]}),makeQuery(id+"F3.boolean.opBoolean","INTERSECT",EDGE,{"derivedFrom":[subQ5,makeQuery(id+"F3.opExtrude","SWEPT_FACE",FACE,{"disambiguationData":[OSD([sQuery(id+"F2.wireOp",EDGE,"E41.5")])]})]}),makeQuery(id+"F3.boolean.opBoolean","INTERSECT",EDGE,{"derivedFrom":[subQ5,makeQuery(id+"F3.opExtrude","SWEPT_FACE",FACE,{"disambiguationData":[OSD([sQuery(id+"F2.wireOp",EDGE,"E42.0")])]})]}),makeQuery(id+"F3.boolean.opBoolean","INTERSECT",EDGE,{"derivedFrom":[subQ5,makeQuery(id+"F3.opExtrude","SWEPT_FACE",FACE,{"disambiguationData":[OSD([sQuery(id+"F2.wireOp",EDGE,"E42.1")])]})]}),makeQuery(id+"F3.boolean.opBoolean","INTERSECT",EDGE,{"derivedFrom":[subQ5,makeQuery(id+"F3.opExtrude","SWEPT_FACE",FACE,{"disambiguationData":[OSD([sQuery(id+"F2.wireOp",EDGE,"E42.2")])]})]}),makeQuery(id+"F3.boolean.opBoolean","INTERSECT",EDGE,{"derivedFrom":[subQ5,makeQuery(id+"F3.opExtrude","SWEPT_FACE",FACE,{"disambiguationData":[OSD([sQuery(id+"F2.wireOp",EDGE,"E42.3")])]})]}),makeQuery(id+"F3.boolean.opBoolean","INTERSECT",EDGE,{"derivedFrom":[subQ5,makeQuery(id+"F3.opExtrude","SWEPT_FACE",FACE,{"disambiguationData":[OSD([sQuery(id+"F2.wireOp",EDGE,"E42.4")])]})]}),makeQuery(id+"F3.boolean.opBoolean","INTERSECT",EDGE,{"derivedFrom":[subQ5,makeQuery(id+"F3.opExtrude","SWEPT_FACE",FACE,{"disambiguationData":[OSD([sQuery(id+"F2.wireOp",EDGE,"E42.5")])]})]}),makeQuery(id+"F3.boolean.opBoolean","INTERSECT",EDGE,{"derivedFrom":[subQ4,makeQuery(id+"F3.opExtrude","SWEPT_FACE",FACE,{"disambiguationData":[OSD([sQuery(id+"F2.wireOp",EDGE,"E39.0")])]})]}),makeQuery(id+"F3.boolean.opBoolean","INTERSECT",EDGE,{"derivedFrom":[subQ4,makeQuery(id+"F3.opExtrude","SWEPT_FACE",FACE,{"disambiguationData":[OSD([sQuery(id+"F2.wireOp",EDGE,"E39.1")])]})]}),makeQuery(id+"F3.boolean.opBoolean","INTERSECT",EDGE,{"derivedFrom":[subQ4,makeQuery(id+"F3.opExtrude","SWEPT_FACE",FACE,{"disambiguationData":[OSD([sQuery(id+"F2.wireOp",EDGE,"E39.2")])]})]}),makeQuery(id+"F3.boolean.opBoolean","INTERSECT",EDGE,{"derivedFrom":[subQ4,makeQuery(id+"F3.opExtrude","SWEPT_FACE",FACE,{"disambiguationData":[OSD([sQuery(id+"F2.wireOp",EDGE,"E39.3")])]})]}),makeQuery(id+"F3.boolean.opBoolean","INTERSECT",EDGE,{"derivedFrom":[subQ4,makeQuery(id+"F3.opExtrude","SWEPT_FACE",FACE,{"disambiguationData":[OSD([sQuery(id+"F2.wireOp",EDGE,"E39.4")])]})]}),makeQuery(id+"F3.boolean.opBoolean","INTERSECT",EDGE,{"derivedFrom":[subQ4,makeQuery(id+"F3.opExtrude","SWEPT_FACE",FACE,{"disambiguationData":[OSD([sQuery(id+"F2.wireOp",EDGE,"E39.5")])]})]}),makeQuery(id+"F3.boolean.opBoolean","INTERSECT",EDGE,{"derivedFrom":[subQ4,makeQuery(id+"F3.opExtrude","SWEPT_FACE",FACE,{"disambiguationData":[OSD([sQuery(id+"F2.wireOp",EDGE,"E40.0")])]})]}),makeQuery(id+"F3.boolean.opBoolean","INTERSECT",EDGE,{"derivedFrom":[subQ4,makeQuery(id+"F3.opExtrude","SWEPT_FACE",FACE,{"disambiguationData":[OSD([sQuery(id+"F2.wireOp",EDGE,"E40.1")])]})]}),makeQuery(id+"F3.boolean.opBoolean","INTERSECT",EDGE,{"derivedFrom":[subQ4,makeQuery(id+"F3.opExtrude","SWEPT_FACE",FACE,{"disambiguationData":[OSD([sQuery(id+"F2.wireOp",EDGE,"E40.2")])]})]}),makeQuery(id+"F3.boolean.opBoolean","INTERSECT",EDGE,{"derivedFrom":[subQ4,makeQuery(id+"F3.opExtrude","SWEPT_FACE",FACE,{"disambiguationData":[OSD([sQuery(id+"F2.wireOp",EDGE,"E40.3")])]})]}),makeQuery(id+"F3.boolean.opBoolean","INTERSECT",EDGE,{"derivedFrom":[subQ4,makeQuery(id+"F3.opExtrude","SWEPT_FACE",FACE,{"disambiguationData":[OSD([sQuery(id+"F2.wireOp",EDGE,"E40.4")])]})]}),makeQuery(id+"F3.boolean.opBoolean","INTERSECT",EDGE,{"derivedFrom":[subQ4,makeQuery(id+"F3.opExtrude","SWEPT_FACE",FACE,{"disambiguationData":[OSD([sQuery(id+"F2.wireOp",EDGE,"E40.5")])]})]}),makeQuery(id+"F3.boolean.opBoolean","INTERSECT",EDGE,{"derivedFrom":[subQ2,makeQuery(id+"F3.opExtrude","SWEPT_FACE",FACE,{"disambiguationData":[OSD([sQuery(id+"F2.wireOp",EDGE,"E36.0")])]})]}),makeQuery(id+"F3.boolean.opBoolean","INTERSECT",EDGE,{"derivedFrom":[subQ2,makeQuery(id+"F3.opExtrude","SWEPT_FACE",FACE,{"disambiguationData":[OSD([sQuery(id+"F2.wireOp",EDGE,"E36.1")])]})]}),makeQuery(id+"F3.boolean.opBoolean","INTERSECT",EDGE,{"derivedFrom":[subQ2,makeQuery(id+"F3.opExtrude","SWEPT_FACE",FACE,{"disambiguationData":[OSD([sQuery(id+"F2.wireOp",EDGE,"E36.2")])]})]}),makeQuery(id+"F3.boolean.opBoolean","INTERSECT",EDGE,{"derivedFrom":[subQ2,makeQuery(id+"F3.opExtrude","SWEPT_FACE",FACE,{"disambiguationData":[OSD([sQuery(id+"F2.wireOp",EDGE,"E36.3")])]})]}),makeQuery(id+"F3.boolean.opBoolean","INTERSECT",EDGE,{"derivedFrom":[subQ2,makeQuery(id+"F3.opExtrude","SWEPT_FACE",FACE,{"disambiguationData":[OSD([sQuery(id+"F2.wireOp",EDGE,"E36.4")])]})]}),makeQuery(id+"F3.boolean.opBoolean","INTERSECT",EDGE,{"derivedFrom":[subQ2,makeQuery(id+"F3.opExtrude","SWEPT_FACE",FACE,{"disambiguationData":[OSD([sQuery(id+"F2.wireOp",EDGE,"E36.5")])]})]}),makeQuery(id+"F3.boolean.opBoolean","INTERSECT",EDGE,{"derivedFrom":[subQ2,makeQuery(id+"F3.opExtrude","SWEPT_FACE",FACE,{"disambiguationData":[OSD([sQuery(id+"F2.wireOp",EDGE,"E37.0")])]})]}),makeQuery(id+"F3.boolean.opBoolean","INTERSECT",EDGE,{"derivedFrom":[subQ2,makeQuery(id+"F3.opExtrude","SWEPT_FACE",FACE,{"disambiguationData":[OSD([sQuery(id+"F2.wireOp",EDGE,"E37.1")])]})]}),makeQuery(id+"F3.boolean.opBoolean","INTERSECT",EDGE,{"derivedFrom":[subQ2,makeQuery(id+"F3.opExtrude","SWEPT_FACE",FACE,{"disambiguationData":[OSD([sQuery(id+"F2.wireOp",EDGE,"E37.2")])]})]}),makeQuery(id+"F3.boolean.opBoolean","INTERSECT",EDGE,{"derivedFrom":[subQ2,makeQuery(id+"F3.opExtrude","SWEPT_FACE",FACE,{"disambiguationData":[OSD([sQuery(id+"F2.wireOp",EDGE,"E37.3")])]})]}),makeQuery(id+"F3.boolean.opBoolean","INTERSECT",EDGE,{"derivedFrom":[subQ2,makeQuery(id+"F3.opExtrude","SWEPT_FACE",FACE,{"disambiguationData":[OSD([sQuery(id+"F2.wireOp",EDGE,"E37.4")])]})]}),makeQuery(id+"F3.boolean.opBoolean","INTERSECT",EDGE,{"derivedFrom":[subQ2,makeQuery(id+"F3.opExtrude","SWEPT_FACE",FACE,{"disambiguationData":[OSD([sQuery(id+"F2.wireOp",EDGE,"E37.5")])]})]}),makeQuery(id+"F3.boolean.opBoolean","INTERSECT",EDGE,{"derivedFrom":[subQ2,makeQuery(id+"F3.opExtrude","SWEPT_FACE",FACE,{"disambiguationData":[OSD([sQuery(id+"F2.wireOp",EDGE,"E38.0")])]})]}),makeQuery(id+"F3.boolean.opBoolean","INTERSECT",EDGE,{"derivedFrom":[subQ2,makeQuery(id+"F3.opExtrude","SWEPT_FACE",FACE,{"disambiguationData":[OSD([sQuery(id+"F2.wireOp",EDGE,"E38.1")])]})]}),makeQuery(id+"F3.boolean.opBoolean","INTERSECT",EDGE,{"derivedFrom":[subQ2,makeQuery(id+"F3.opExtrude","SWEPT_FACE",FACE,{"disambiguationData":[OSD([sQuery(id+"F2.wireOp",EDGE,"E38.2")])]})]}),makeQuery(id+"F3.boolean.opBoolean","INTERSECT",EDGE,{"derivedFrom":[subQ2,makeQuery(id+"F3.opExtrude","SWEPT_FACE",FACE,{"disambiguationData":[OSD([sQuery(id+"F2.wireOp",EDGE,"E38.3")])]})]}),makeQuery(id+"F3.boolean.opBoolean","INTERSECT",EDGE,{"derivedFrom":[subQ2,makeQuery(id+"F3.opExtrude","SWEPT_FACE",FACE,{"disambiguationData":[OSD([sQuery(id+"F2.wireOp",EDGE,"E38.4")])]})]}),makeQuery(id+"F3.boolean.opBoolean","INTERSECT",EDGE,{"derivedFrom":[subQ2,makeQuery(id+"F3.opExtrude","SWEPT_FACE",FACE,{"disambiguationData":[OSD([sQuery(id+"F2.wireOp",EDGE,"E38.5")])]})]})]);}
            var Q30;
            {var subQ0=sQuery(id+"F0.wireOp",EDGE,"E6");var subQ1=sQuery(id+"F0.wireOp",EDGE,"E18.top");var subQ2=makeQuery(id+"F1.opExtrude","SWEPT_FACE",FACE,{"disambiguationData":[OSD([subQ0]),TDD([makeQuery(id+"F0.imprint","IMPRINT",EDGE,{"disambiguationData":[TD([[makeQuery(id+"F0.imprint","INTERSECT",VERTEX,{"derivedFrom":[subQ0,sQuery(id+"F0.wireOp",EDGE,"E9")]}),1.0]])],"derivedFrom":subQ0})])]});var subQ4=makeQuery(id+"F1.opExtrude","SWEPT_FACE",FACE,{"disambiguationData":[OSD([subQ0]),TDD([makeQuery(id+"F0.imprint","IMPRINT",EDGE,{"disambiguationData":[TD([[makeQuery(id+"F0.imprint","INTERSECT",VERTEX,{"derivedFrom":[subQ0,subQ1,sQuery(id+"F0.wireOp",EDGE,"E18.right")]}),1.0]])],"derivedFrom":subQ0})])]});var subQ5=makeQuery(id+"F1.opExtrude","SWEPT_FACE",FACE,{"disambiguationData":[OSD([subQ0]),TDD([makeQuery(id+"F0.imprint","IMPRINT",EDGE,{"disambiguationData":[TD([[makeQuery(id+"F0.imprint","INTERSECT",VERTEX,{"derivedFrom":[subQ0,sQuery(id+"F0.wireOp",EDGE,"E12")]}),-1.0]])],"derivedFrom":subQ0})])]});Q30=qUnion([makeQuery(id+"F3.boolean.opBoolean","INTERSECT",EDGE,{"derivedFrom":[subQ5,makeQuery(id+"F3.opExtrude","SWEPT_FACE",FACE,{"disambiguationData":[OSD([sQuery(id+"F2.wireOp",EDGE,"E41.0")])]})]}),makeQuery(id+"F3.boolean.opBoolean","INTERSECT",EDGE,{"derivedFrom":[subQ5,makeQuery(id+"F3.opExtrude","SWEPT_FACE",FACE,{"disambiguationData":[OSD([sQuery(id+"F2.wireOp",EDGE,"E41.1")])]})]}),makeQuery(id+"F3.boolean.opBoolean","INTERSECT",EDGE,{"derivedFrom":[subQ5,makeQuery(id+"F3.opExtrude","SWEPT_FACE",FACE,{"disambiguationData":[OSD([sQuery(id+"F2.wireOp",EDGE,"E41.2")])]})]}),makeQuery(id+"F3.boolean.opBoolean","INTERSECT",EDGE,{"derivedFrom":[subQ5,makeQuery(id+"F3.opExtrude","SWEPT_FACE",FACE,{"disambiguationData":[OSD([sQuery(id+"F2.wireOp",EDGE,"E41.3")])]})]}),makeQuery(id+"F3.boolean.opBoolean","INTERSECT",EDGE,{"derivedFrom":[subQ5,makeQuery(id+"F3.opExtrude","SWEPT_FACE",FACE,{"disambiguationData":[OSD([sQuery(id+"F2.wireOp",EDGE,"E41.4")])]})]}),makeQuery(id+"F3.boolean.opBoolean","INTERSECT",EDGE,{"derivedFrom":[subQ5,makeQuery(id+"F3.opExtrude","SWEPT_FACE",FACE,{"disambiguationData":[OSD([sQuery(id+"F2.wireOp",EDGE,"E41.5")])]})]}),makeQuery(id+"F3.boolean.opBoolean","INTERSECT",EDGE,{"derivedFrom":[subQ5,makeQuery(id+"F3.opExtrude","SWEPT_FACE",FACE,{"disambiguationData":[OSD([sQuery(id+"F2.wireOp",EDGE,"E42.0")])]})]}),makeQuery(id+"F3.boolean.opBoolean","INTERSECT",EDGE,{"derivedFrom":[subQ5,makeQuery(id+"F3.opExtrude","SWEPT_FACE",FACE,{"disambiguationData":[OSD([sQuery(id+"F2.wireOp",EDGE,"E42.1")])]})]}),makeQuery(id+"F3.boolean.opBoolean","INTERSECT",EDGE,{"derivedFrom":[subQ5,makeQuery(id+"F3.opExtrude","SWEPT_FACE",FACE,{"disambiguationData":[OSD([sQuery(id+"F2.wireOp",EDGE,"E42.2")])]})]}),makeQuery(id+"F3.boolean.opBoolean","INTERSECT",EDGE,{"derivedFrom":[subQ5,makeQuery(id+"F3.opExtrude","SWEPT_FACE",FACE,{"disambiguationData":[OSD([sQuery(id+"F2.wireOp",EDGE,"E42.3")])]})]}),makeQuery(id+"F3.boolean.opBoolean","INTERSECT",EDGE,{"derivedFrom":[subQ5,makeQuery(id+"F3.opExtrude","SWEPT_FACE",FACE,{"disambiguationData":[OSD([sQuery(id+"F2.wireOp",EDGE,"E42.4")])]})]}),makeQuery(id+"F3.boolean.opBoolean","INTERSECT",EDGE,{"derivedFrom":[subQ5,makeQuery(id+"F3.opExtrude","SWEPT_FACE",FACE,{"disambiguationData":[OSD([sQuery(id+"F2.wireOp",EDGE,"E42.5")])]})]}),makeQuery(id+"F3.boolean.opBoolean","INTERSECT",EDGE,{"derivedFrom":[subQ4,makeQuery(id+"F3.opExtrude","SWEPT_FACE",FACE,{"disambiguationData":[OSD([sQuery(id+"F2.wireOp",EDGE,"E39.0")])]})]}),makeQuery(id+"F3.boolean.opBoolean","INTERSECT",EDGE,{"derivedFrom":[subQ4,makeQuery(id+"F3.opExtrude","SWEPT_FACE",FACE,{"disambiguationData":[OSD([sQuery(id+"F2.wireOp",EDGE,"E39.1")])]})]}),makeQuery(id+"F3.boolean.opBoolean","INTERSECT",EDGE,{"derivedFrom":[subQ4,makeQuery(id+"F3.opExtrude","SWEPT_FACE",FACE,{"disambiguationData":[OSD([sQuery(id+"F2.wireOp",EDGE,"E39.2")])]})]}),makeQuery(id+"F3.boolean.opBoolean","INTERSECT",EDGE,{"derivedFrom":[subQ4,makeQuery(id+"F3.opExtrude","SWEPT_FACE",FACE,{"disambiguationData":[OSD([sQuery(id+"F2.wireOp",EDGE,"E39.3")])]})]}),makeQuery(id+"F3.boolean.opBoolean","INTERSECT",EDGE,{"derivedFrom":[subQ4,makeQuery(id+"F3.opExtrude","SWEPT_FACE",FACE,{"disambiguationData":[OSD([sQuery(id+"F2.wireOp",EDGE,"E39.4")])]})]}),makeQuery(id+"F3.boolean.opBoolean","INTERSECT",EDGE,{"derivedFrom":[subQ4,makeQuery(id+"F3.opExtrude","SWEPT_FACE",FACE,{"disambiguationData":[OSD([sQuery(id+"F2.wireOp",EDGE,"E39.5")])]})]}),makeQuery(id+"F3.boolean.opBoolean","INTERSECT",EDGE,{"derivedFrom":[subQ4,makeQuery(id+"F3.opExtrude","SWEPT_FACE",FACE,{"disambiguationData":[OSD([sQuery(id+"F2.wireOp",EDGE,"E40.0")])]})]}),makeQuery(id+"F3.boolean.opBoolean","INTERSECT",EDGE,{"derivedFrom":[subQ4,makeQuery(id+"F3.opExtrude","SWEPT_FACE",FACE,{"disambiguationData":[OSD([sQuery(id+"F2.wireOp",EDGE,"E40.1")])]})]}),makeQuery(id+"F3.boolean.opBoolean","INTERSECT",EDGE,{"derivedFrom":[subQ4,makeQuery(id+"F3.opExtrude","SWEPT_FACE",FACE,{"disambiguationData":[OSD([sQuery(id+"F2.wireOp",EDGE,"E40.2")])]})]}),makeQuery(id+"F3.boolean.opBoolean","INTERSECT",EDGE,{"derivedFrom":[subQ4,makeQuery(id+"F3.opExtrude","SWEPT_FACE",FACE,{"disambiguationData":[OSD([sQuery(id+"F2.wireOp",EDGE,"E40.3")])]})]}),makeQuery(id+"F3.boolean.opBoolean","INTERSECT",EDGE,{"derivedFrom":[subQ4,makeQuery(id+"F3.opExtrude","SWEPT_FACE",FACE,{"disambiguationData":[OSD([sQuery(id+"F2.wireOp",EDGE,"E40.4")])]})]}),makeQuery(id+"F3.boolean.opBoolean","INTERSECT",EDGE,{"derivedFrom":[subQ4,makeQuery(id+"F3.opExtrude","SWEPT_FACE",FACE,{"disambiguationData":[OSD([sQuery(id+"F2.wireOp",EDGE,"E40.5")])]})]}),makeQuery(id+"F3.boolean.opBoolean","INTERSECT",EDGE,{"derivedFrom":[subQ2,makeQuery(id+"F3.opExtrude","SWEPT_FACE",FACE,{"disambiguationData":[OSD([sQuery(id+"F2.wireOp",EDGE,"E36.0")])]})]}),makeQuery(id+"F3.boolean.opBoolean","INTERSECT",EDGE,{"derivedFrom":[subQ2,makeQuery(id+"F3.opExtrude","SWEPT_FACE",FACE,{"disambiguationData":[OSD([sQuery(id+"F2.wireOp",EDGE,"E36.1")])]})]}),makeQuery(id+"F3.boolean.opBoolean","INTERSECT",EDGE,{"derivedFrom":[subQ2,makeQuery(id+"F3.opExtrude","SWEPT_FACE",FACE,{"disambiguationData":[OSD([sQuery(id+"F2.wireOp",EDGE,"E36.2")])]})]}),makeQuery(id+"F3.boolean.opBoolean","INTERSECT",EDGE,{"derivedFrom":[subQ2,makeQuery(id+"F3.opExtrude","SWEPT_FACE",FACE,{"disambiguationData":[OSD([sQuery(id+"F2.wireOp",EDGE,"E36.3")])]})]}),makeQuery(id+"F3.boolean.opBoolean","INTERSECT",EDGE,{"derivedFrom":[subQ2,makeQuery(id+"F3.opExtrude","SWEPT_FACE",FACE,{"disambiguationData":[OSD([sQuery(id+"F2.wireOp",EDGE,"E36.4")])]})]}),makeQuery(id+"F3.boolean.opBoolean","INTERSECT",EDGE,{"derivedFrom":[subQ2,makeQuery(id+"F3.opExtrude","SWEPT_FACE",FACE,{"disambiguationData":[OSD([sQuery(id+"F2.wireOp",EDGE,"E36.5")])]})]}),makeQuery(id+"F3.boolean.opBoolean","INTERSECT",EDGE,{"derivedFrom":[subQ2,makeQuery(id+"F3.opExtrude","SWEPT_FACE",FACE,{"disambiguationData":[OSD([sQuery(id+"F2.wireOp",EDGE,"E37.0")])]})]}),makeQuery(id+"F3.boolean.opBoolean","INTERSECT",EDGE,{"derivedFrom":[subQ2,makeQuery(id+"F3.opExtrude","SWEPT_FACE",FACE,{"disambiguationData":[OSD([sQuery(id+"F2.wireOp",EDGE,"E37.1")])]})]}),makeQuery(id+"F3.boolean.opBoolean","INTERSECT",EDGE,{"derivedFrom":[subQ2,makeQuery(id+"F3.opExtrude","SWEPT_FACE",FACE,{"disambiguationData":[OSD([sQuery(id+"F2.wireOp",EDGE,"E37.2")])]})]}),makeQuery(id+"F3.boolean.opBoolean","INTERSECT",EDGE,{"derivedFrom":[subQ2,makeQuery(id+"F3.opExtrude","SWEPT_FACE",FACE,{"disambiguationData":[OSD([sQuery(id+"F2.wireOp",EDGE,"E37.3")])]})]}),makeQuery(id+"F3.boolean.opBoolean","INTERSECT",EDGE,{"derivedFrom":[subQ2,makeQuery(id+"F3.opExtrude","SWEPT_FACE",FACE,{"disambiguationData":[OSD([sQuery(id+"F2.wireOp",EDGE,"E37.4")])]})]}),makeQuery(id+"F3.boolean.opBoolean","INTERSECT",EDGE,{"derivedFrom":[subQ2,makeQuery(id+"F3.opExtrude","SWEPT_FACE",FACE,{"disambiguationData":[OSD([sQuery(id+"F2.wireOp",EDGE,"E37.5")])]})]}),makeQuery(id+"F3.boolean.opBoolean","INTERSECT",EDGE,{"derivedFrom":[subQ2,makeQuery(id+"F3.opExtrude","SWEPT_FACE",FACE,{"disambiguationData":[OSD([sQuery(id+"F2.wireOp",EDGE,"E38.0")])]})]}),makeQuery(id+"F3.boolean.opBoolean","INTERSECT",EDGE,{"derivedFrom":[subQ2,makeQuery(id+"F3.opExtrude","SWEPT_FACE",FACE,{"disambiguationData":[OSD([sQuery(id+"F2.wireOp",EDGE,"E38.1")])]})]}),makeQuery(id+"F3.boolean.opBoolean","INTERSECT",EDGE,{"derivedFrom":[subQ2,makeQuery(id+"F3.opExtrude","SWEPT_FACE",FACE,{"disambiguationData":[OSD([sQuery(id+"F2.wireOp",EDGE,"E38.2")])]})]}),makeQuery(id+"F3.boolean.opBoolean","INTERSECT",EDGE,{"derivedFrom":[subQ2,makeQuery(id+"F3.opExtrude","SWEPT_FACE",FACE,{"disambiguationData":[OSD([sQuery(id+"F2.wireOp",EDGE,"E38.3")])]})]}),makeQuery(id+"F3.boolean.opBoolean","INTERSECT",EDGE,{"derivedFrom":[subQ2,makeQuery(id+"F3.opExtrude","SWEPT_FACE",FACE,{"disambiguationData":[OSD([sQuery(id+"F2.wireOp",EDGE,"E38.4")])]})]}),makeQuery(id+"F3.boolean.opBoolean","INTERSECT",EDGE,{"derivedFrom":[subQ2,makeQuery(id+"F3.opExtrude","SWEPT_FACE",FACE,{"disambiguationData":[OSD([sQuery(id+"F2.wireOp",EDGE,"E38.5")])]})]})]);}
            var Q31;
            {var subQ0=sQuery(id+"F0.wireOp",EDGE,"E6");var subQ1=sQuery(id+"F0.wireOp",EDGE,"E18.top");var subQ2=makeQuery(id+"F1.opExtrude","SWEPT_FACE",FACE,{"disambiguationData":[OSD([subQ0]),TDD([makeQuery(id+"F0.imprint","IMPRINT",EDGE,{"disambiguationData":[TD([[makeQuery(id+"F0.imprint","INTERSECT",VERTEX,{"derivedFrom":[subQ0,sQuery(id+"F0.wireOp",EDGE,"E9")]}),1.0]])],"derivedFrom":subQ0})])]});var subQ4=makeQuery(id+"F1.opExtrude","SWEPT_FACE",FACE,{"disambiguationData":[OSD([subQ0]),TDD([makeQuery(id+"F0.imprint","IMPRINT",EDGE,{"disambiguationData":[TD([[makeQuery(id+"F0.imprint","INTERSECT",VERTEX,{"derivedFrom":[subQ0,subQ1,sQuery(id+"F0.wireOp",EDGE,"E18.right")]}),1.0]])],"derivedFrom":subQ0})])]});var subQ5=makeQuery(id+"F1.opExtrude","SWEPT_FACE",FACE,{"disambiguationData":[OSD([subQ0]),TDD([makeQuery(id+"F0.imprint","IMPRINT",EDGE,{"disambiguationData":[TD([[makeQuery(id+"F0.imprint","INTERSECT",VERTEX,{"derivedFrom":[subQ0,sQuery(id+"F0.wireOp",EDGE,"E12")]}),-1.0]])],"derivedFrom":subQ0})])]});Q31=qUnion([makeQuery(id+"F3.boolean.opBoolean","INTERSECT",EDGE,{"derivedFrom":[subQ5,makeQuery(id+"F3.opExtrude","SWEPT_FACE",FACE,{"disambiguationData":[OSD([sQuery(id+"F2.wireOp",EDGE,"E41.0")])]})]}),makeQuery(id+"F3.boolean.opBoolean","INTERSECT",EDGE,{"derivedFrom":[subQ5,makeQuery(id+"F3.opExtrude","SWEPT_FACE",FACE,{"disambiguationData":[OSD([sQuery(id+"F2.wireOp",EDGE,"E41.1")])]})]}),makeQuery(id+"F3.boolean.opBoolean","INTERSECT",EDGE,{"derivedFrom":[subQ5,makeQuery(id+"F3.opExtrude","SWEPT_FACE",FACE,{"disambiguationData":[OSD([sQuery(id+"F2.wireOp",EDGE,"E41.2")])]})]}),makeQuery(id+"F3.boolean.opBoolean","INTERSECT",EDGE,{"derivedFrom":[subQ5,makeQuery(id+"F3.opExtrude","SWEPT_FACE",FACE,{"disambiguationData":[OSD([sQuery(id+"F2.wireOp",EDGE,"E41.3")])]})]}),makeQuery(id+"F3.boolean.opBoolean","INTERSECT",EDGE,{"derivedFrom":[subQ5,makeQuery(id+"F3.opExtrude","SWEPT_FACE",FACE,{"disambiguationData":[OSD([sQuery(id+"F2.wireOp",EDGE,"E41.4")])]})]}),makeQuery(id+"F3.boolean.opBoolean","INTERSECT",EDGE,{"derivedFrom":[subQ5,makeQuery(id+"F3.opExtrude","SWEPT_FACE",FACE,{"disambiguationData":[OSD([sQuery(id+"F2.wireOp",EDGE,"E41.5")])]})]}),makeQuery(id+"F3.boolean.opBoolean","INTERSECT",EDGE,{"derivedFrom":[subQ5,makeQuery(id+"F3.opExtrude","SWEPT_FACE",FACE,{"disambiguationData":[OSD([sQuery(id+"F2.wireOp",EDGE,"E42.0")])]})]}),makeQuery(id+"F3.boolean.opBoolean","INTERSECT",EDGE,{"derivedFrom":[subQ5,makeQuery(id+"F3.opExtrude","SWEPT_FACE",FACE,{"disambiguationData":[OSD([sQuery(id+"F2.wireOp",EDGE,"E42.1")])]})]}),makeQuery(id+"F3.boolean.opBoolean","INTERSECT",EDGE,{"derivedFrom":[subQ5,makeQuery(id+"F3.opExtrude","SWEPT_FACE",FACE,{"disambiguationData":[OSD([sQuery(id+"F2.wireOp",EDGE,"E42.2")])]})]}),makeQuery(id+"F3.boolean.opBoolean","INTERSECT",EDGE,{"derivedFrom":[subQ5,makeQuery(id+"F3.opExtrude","SWEPT_FACE",FACE,{"disambiguationData":[OSD([sQuery(id+"F2.wireOp",EDGE,"E42.3")])]})]}),makeQuery(id+"F3.boolean.opBoolean","INTERSECT",EDGE,{"derivedFrom":[subQ5,makeQuery(id+"F3.opExtrude","SWEPT_FACE",FACE,{"disambiguationData":[OSD([sQuery(id+"F2.wireOp",EDGE,"E42.4")])]})]}),makeQuery(id+"F3.boolean.opBoolean","INTERSECT",EDGE,{"derivedFrom":[subQ5,makeQuery(id+"F3.opExtrude","SWEPT_FACE",FACE,{"disambiguationData":[OSD([sQuery(id+"F2.wireOp",EDGE,"E42.5")])]})]}),makeQuery(id+"F3.boolean.opBoolean","INTERSECT",EDGE,{"derivedFrom":[subQ4,makeQuery(id+"F3.opExtrude","SWEPT_FACE",FACE,{"disambiguationData":[OSD([sQuery(id+"F2.wireOp",EDGE,"E39.0")])]})]}),makeQuery(id+"F3.boolean.opBoolean","INTERSECT",EDGE,{"derivedFrom":[subQ4,makeQuery(id+"F3.opExtrude","SWEPT_FACE",FACE,{"disambiguationData":[OSD([sQuery(id+"F2.wireOp",EDGE,"E39.1")])]})]}),makeQuery(id+"F3.boolean.opBoolean","INTERSECT",EDGE,{"derivedFrom":[subQ4,makeQuery(id+"F3.opExtrude","SWEPT_FACE",FACE,{"disambiguationData":[OSD([sQuery(id+"F2.wireOp",EDGE,"E39.2")])]})]}),makeQuery(id+"F3.boolean.opBoolean","INTERSECT",EDGE,{"derivedFrom":[subQ4,makeQuery(id+"F3.opExtrude","SWEPT_FACE",FACE,{"disambiguationData":[OSD([sQuery(id+"F2.wireOp",EDGE,"E39.3")])]})]}),makeQuery(id+"F3.boolean.opBoolean","INTERSECT",EDGE,{"derivedFrom":[subQ4,makeQuery(id+"F3.opExtrude","SWEPT_FACE",FACE,{"disambiguationData":[OSD([sQuery(id+"F2.wireOp",EDGE,"E39.4")])]})]}),makeQuery(id+"F3.boolean.opBoolean","INTERSECT",EDGE,{"derivedFrom":[subQ4,makeQuery(id+"F3.opExtrude","SWEPT_FACE",FACE,{"disambiguationData":[OSD([sQuery(id+"F2.wireOp",EDGE,"E39.5")])]})]}),makeQuery(id+"F3.boolean.opBoolean","INTERSECT",EDGE,{"derivedFrom":[subQ4,makeQuery(id+"F3.opExtrude","SWEPT_FACE",FACE,{"disambiguationData":[OSD([sQuery(id+"F2.wireOp",EDGE,"E40.0")])]})]}),makeQuery(id+"F3.boolean.opBoolean","INTERSECT",EDGE,{"derivedFrom":[subQ4,makeQuery(id+"F3.opExtrude","SWEPT_FACE",FACE,{"disambiguationData":[OSD([sQuery(id+"F2.wireOp",EDGE,"E40.1")])]})]}),makeQuery(id+"F3.boolean.opBoolean","INTERSECT",EDGE,{"derivedFrom":[subQ4,makeQuery(id+"F3.opExtrude","SWEPT_FACE",FACE,{"disambiguationData":[OSD([sQuery(id+"F2.wireOp",EDGE,"E40.2")])]})]}),makeQuery(id+"F3.boolean.opBoolean","INTERSECT",EDGE,{"derivedFrom":[subQ4,makeQuery(id+"F3.opExtrude","SWEPT_FACE",FACE,{"disambiguationData":[OSD([sQuery(id+"F2.wireOp",EDGE,"E40.3")])]})]}),makeQuery(id+"F3.boolean.opBoolean","INTERSECT",EDGE,{"derivedFrom":[subQ4,makeQuery(id+"F3.opExtrude","SWEPT_FACE",FACE,{"disambiguationData":[OSD([sQuery(id+"F2.wireOp",EDGE,"E40.4")])]})]}),makeQuery(id+"F3.boolean.opBoolean","INTERSECT",EDGE,{"derivedFrom":[subQ4,makeQuery(id+"F3.opExtrude","SWEPT_FACE",FACE,{"disambiguationData":[OSD([sQuery(id+"F2.wireOp",EDGE,"E40.5")])]})]}),makeQuery(id+"F3.boolean.opBoolean","INTERSECT",EDGE,{"derivedFrom":[subQ2,makeQuery(id+"F3.opExtrude","SWEPT_FACE",FACE,{"disambiguationData":[OSD([sQuery(id+"F2.wireOp",EDGE,"E36.0")])]})]}),makeQuery(id+"F3.boolean.opBoolean","INTERSECT",EDGE,{"derivedFrom":[subQ2,makeQuery(id+"F3.opExtrude","SWEPT_FACE",FACE,{"disambiguationData":[OSD([sQuery(id+"F2.wireOp",EDGE,"E36.1")])]})]}),makeQuery(id+"F3.boolean.opBoolean","INTERSECT",EDGE,{"derivedFrom":[subQ2,makeQuery(id+"F3.opExtrude","SWEPT_FACE",FACE,{"disambiguationData":[OSD([sQuery(id+"F2.wireOp",EDGE,"E36.2")])]})]}),makeQuery(id+"F3.boolean.opBoolean","INTERSECT",EDGE,{"derivedFrom":[subQ2,makeQuery(id+"F3.opExtrude","SWEPT_FACE",FACE,{"disambiguationData":[OSD([sQuery(id+"F2.wireOp",EDGE,"E36.3")])]})]}),makeQuery(id+"F3.boolean.opBoolean","INTERSECT",EDGE,{"derivedFrom":[subQ2,makeQuery(id+"F3.opExtrude","SWEPT_FACE",FACE,{"disambiguationData":[OSD([sQuery(id+"F2.wireOp",EDGE,"E36.4")])]})]}),makeQuery(id+"F3.boolean.opBoolean","INTERSECT",EDGE,{"derivedFrom":[subQ2,makeQuery(id+"F3.opExtrude","SWEPT_FACE",FACE,{"disambiguationData":[OSD([sQuery(id+"F2.wireOp",EDGE,"E36.5")])]})]}),makeQuery(id+"F3.boolean.opBoolean","INTERSECT",EDGE,{"derivedFrom":[subQ2,makeQuery(id+"F3.opExtrude","SWEPT_FACE",FACE,{"disambiguationData":[OSD([sQuery(id+"F2.wireOp",EDGE,"E37.0")])]})]}),makeQuery(id+"F3.boolean.opBoolean","INTERSECT",EDGE,{"derivedFrom":[subQ2,makeQuery(id+"F3.opExtrude","SWEPT_FACE",FACE,{"disambiguationData":[OSD([sQuery(id+"F2.wireOp",EDGE,"E37.1")])]})]}),makeQuery(id+"F3.boolean.opBoolean","INTERSECT",EDGE,{"derivedFrom":[subQ2,makeQuery(id+"F3.opExtrude","SWEPT_FACE",FACE,{"disambiguationData":[OSD([sQuery(id+"F2.wireOp",EDGE,"E37.2")])]})]}),makeQuery(id+"F3.boolean.opBoolean","INTERSECT",EDGE,{"derivedFrom":[subQ2,makeQuery(id+"F3.opExtrude","SWEPT_FACE",FACE,{"disambiguationData":[OSD([sQuery(id+"F2.wireOp",EDGE,"E37.3")])]})]}),makeQuery(id+"F3.boolean.opBoolean","INTERSECT",EDGE,{"derivedFrom":[subQ2,makeQuery(id+"F3.opExtrude","SWEPT_FACE",FACE,{"disambiguationData":[OSD([sQuery(id+"F2.wireOp",EDGE,"E37.4")])]})]}),makeQuery(id+"F3.boolean.opBoolean","INTERSECT",EDGE,{"derivedFrom":[subQ2,makeQuery(id+"F3.opExtrude","SWEPT_FACE",FACE,{"disambiguationData":[OSD([sQuery(id+"F2.wireOp",EDGE,"E37.5")])]})]}),makeQuery(id+"F3.boolean.opBoolean","INTERSECT",EDGE,{"derivedFrom":[subQ2,makeQuery(id+"F3.opExtrude","SWEPT_FACE",FACE,{"disambiguationData":[OSD([sQuery(id+"F2.wireOp",EDGE,"E38.0")])]})]}),makeQuery(id+"F3.boolean.opBoolean","INTERSECT",EDGE,{"derivedFrom":[subQ2,makeQuery(id+"F3.opExtrude","SWEPT_FACE",FACE,{"disambiguationData":[OSD([sQuery(id+"F2.wireOp",EDGE,"E38.1")])]})]}),makeQuery(id+"F3.boolean.opBoolean","INTERSECT",EDGE,{"derivedFrom":[subQ2,makeQuery(id+"F3.opExtrude","SWEPT_FACE",FACE,{"disambiguationData":[OSD([sQuery(id+"F2.wireOp",EDGE,"E38.2")])]})]}),makeQuery(id+"F3.boolean.opBoolean","INTERSECT",EDGE,{"derivedFrom":[subQ2,makeQuery(id+"F3.opExtrude","SWEPT_FACE",FACE,{"disambiguationData":[OSD([sQuery(id+"F2.wireOp",EDGE,"E38.3")])]})]}),makeQuery(id+"F3.boolean.opBoolean","INTERSECT",EDGE,{"derivedFrom":[subQ2,makeQuery(id+"F3.opExtrude","SWEPT_FACE",FACE,{"disambiguationData":[OSD([sQuery(id+"F2.wireOp",EDGE,"E38.4")])]})]}),makeQuery(id+"F3.boolean.opBoolean","INTERSECT",EDGE,{"derivedFrom":[subQ2,makeQuery(id+"F3.opExtrude","SWEPT_FACE",FACE,{"disambiguationData":[OSD([sQuery(id+"F2.wireOp",EDGE,"E38.5")])]})]})]);}
            var Q32;
            {var subQ0=sQuery(id+"F0.wireOp",EDGE,"E6");var subQ1=sQuery(id+"F0.wireOp",EDGE,"E18.top");var subQ2=makeQuery(id+"F1.opExtrude","SWEPT_FACE",FACE,{"disambiguationData":[OSD([subQ0]),TDD([makeQuery(id+"F0.imprint","IMPRINT",EDGE,{"disambiguationData":[TD([[makeQuery(id+"F0.imprint","INTERSECT",VERTEX,{"derivedFrom":[subQ0,sQuery(id+"F0.wireOp",EDGE,"E9")]}),1.0]])],"derivedFrom":subQ0})])]});var subQ4=makeQuery(id+"F1.opExtrude","SWEPT_FACE",FACE,{"disambiguationData":[OSD([subQ0]),TDD([makeQuery(id+"F0.imprint","IMPRINT",EDGE,{"disambiguationData":[TD([[makeQuery(id+"F0.imprint","INTERSECT",VERTEX,{"derivedFrom":[subQ0,subQ1,sQuery(id+"F0.wireOp",EDGE,"E18.right")]}),1.0]])],"derivedFrom":subQ0})])]});var subQ5=makeQuery(id+"F1.opExtrude","SWEPT_FACE",FACE,{"disambiguationData":[OSD([subQ0]),TDD([makeQuery(id+"F0.imprint","IMPRINT",EDGE,{"disambiguationData":[TD([[makeQuery(id+"F0.imprint","INTERSECT",VERTEX,{"derivedFrom":[subQ0,sQuery(id+"F0.wireOp",EDGE,"E12")]}),-1.0]])],"derivedFrom":subQ0})])]});Q32=qUnion([makeQuery(id+"F3.boolean.opBoolean","INTERSECT",EDGE,{"derivedFrom":[subQ5,makeQuery(id+"F3.opExtrude","SWEPT_FACE",FACE,{"disambiguationData":[OSD([sQuery(id+"F2.wireOp",EDGE,"E41.0")])]})]}),makeQuery(id+"F3.boolean.opBoolean","INTERSECT",EDGE,{"derivedFrom":[subQ5,makeQuery(id+"F3.opExtrude","SWEPT_FACE",FACE,{"disambiguationData":[OSD([sQuery(id+"F2.wireOp",EDGE,"E41.1")])]})]}),makeQuery(id+"F3.boolean.opBoolean","INTERSECT",EDGE,{"derivedFrom":[subQ5,makeQuery(id+"F3.opExtrude","SWEPT_FACE",FACE,{"disambiguationData":[OSD([sQuery(id+"F2.wireOp",EDGE,"E41.2")])]})]}),makeQuery(id+"F3.boolean.opBoolean","INTERSECT",EDGE,{"derivedFrom":[subQ5,makeQuery(id+"F3.opExtrude","SWEPT_FACE",FACE,{"disambiguationData":[OSD([sQuery(id+"F2.wireOp",EDGE,"E41.3")])]})]}),makeQuery(id+"F3.boolean.opBoolean","INTERSECT",EDGE,{"derivedFrom":[subQ5,makeQuery(id+"F3.opExtrude","SWEPT_FACE",FACE,{"disambiguationData":[OSD([sQuery(id+"F2.wireOp",EDGE,"E41.4")])]})]}),makeQuery(id+"F3.boolean.opBoolean","INTERSECT",EDGE,{"derivedFrom":[subQ5,makeQuery(id+"F3.opExtrude","SWEPT_FACE",FACE,{"disambiguationData":[OSD([sQuery(id+"F2.wireOp",EDGE,"E41.5")])]})]}),makeQuery(id+"F3.boolean.opBoolean","INTERSECT",EDGE,{"derivedFrom":[subQ5,makeQuery(id+"F3.opExtrude","SWEPT_FACE",FACE,{"disambiguationData":[OSD([sQuery(id+"F2.wireOp",EDGE,"E42.0")])]})]}),makeQuery(id+"F3.boolean.opBoolean","INTERSECT",EDGE,{"derivedFrom":[subQ5,makeQuery(id+"F3.opExtrude","SWEPT_FACE",FACE,{"disambiguationData":[OSD([sQuery(id+"F2.wireOp",EDGE,"E42.1")])]})]}),makeQuery(id+"F3.boolean.opBoolean","INTERSECT",EDGE,{"derivedFrom":[subQ5,makeQuery(id+"F3.opExtrude","SWEPT_FACE",FACE,{"disambiguationData":[OSD([sQuery(id+"F2.wireOp",EDGE,"E42.2")])]})]}),makeQuery(id+"F3.boolean.opBoolean","INTERSECT",EDGE,{"derivedFrom":[subQ5,makeQuery(id+"F3.opExtrude","SWEPT_FACE",FACE,{"disambiguationData":[OSD([sQuery(id+"F2.wireOp",EDGE,"E42.3")])]})]}),makeQuery(id+"F3.boolean.opBoolean","INTERSECT",EDGE,{"derivedFrom":[subQ5,makeQuery(id+"F3.opExtrude","SWEPT_FACE",FACE,{"disambiguationData":[OSD([sQuery(id+"F2.wireOp",EDGE,"E42.4")])]})]}),makeQuery(id+"F3.boolean.opBoolean","INTERSECT",EDGE,{"derivedFrom":[subQ5,makeQuery(id+"F3.opExtrude","SWEPT_FACE",FACE,{"disambiguationData":[OSD([sQuery(id+"F2.wireOp",EDGE,"E42.5")])]})]}),makeQuery(id+"F3.boolean.opBoolean","INTERSECT",EDGE,{"derivedFrom":[subQ4,makeQuery(id+"F3.opExtrude","SWEPT_FACE",FACE,{"disambiguationData":[OSD([sQuery(id+"F2.wireOp",EDGE,"E39.0")])]})]}),makeQuery(id+"F3.boolean.opBoolean","INTERSECT",EDGE,{"derivedFrom":[subQ4,makeQuery(id+"F3.opExtrude","SWEPT_FACE",FACE,{"disambiguationData":[OSD([sQuery(id+"F2.wireOp",EDGE,"E39.1")])]})]}),makeQuery(id+"F3.boolean.opBoolean","INTERSECT",EDGE,{"derivedFrom":[subQ4,makeQuery(id+"F3.opExtrude","SWEPT_FACE",FACE,{"disambiguationData":[OSD([sQuery(id+"F2.wireOp",EDGE,"E39.2")])]})]}),makeQuery(id+"F3.boolean.opBoolean","INTERSECT",EDGE,{"derivedFrom":[subQ4,makeQuery(id+"F3.opExtrude","SWEPT_FACE",FACE,{"disambiguationData":[OSD([sQuery(id+"F2.wireOp",EDGE,"E39.3")])]})]}),makeQuery(id+"F3.boolean.opBoolean","INTERSECT",EDGE,{"derivedFrom":[subQ4,makeQuery(id+"F3.opExtrude","SWEPT_FACE",FACE,{"disambiguationData":[OSD([sQuery(id+"F2.wireOp",EDGE,"E39.4")])]})]}),makeQuery(id+"F3.boolean.opBoolean","INTERSECT",EDGE,{"derivedFrom":[subQ4,makeQuery(id+"F3.opExtrude","SWEPT_FACE",FACE,{"disambiguationData":[OSD([sQuery(id+"F2.wireOp",EDGE,"E39.5")])]})]}),makeQuery(id+"F3.boolean.opBoolean","INTERSECT",EDGE,{"derivedFrom":[subQ4,makeQuery(id+"F3.opExtrude","SWEPT_FACE",FACE,{"disambiguationData":[OSD([sQuery(id+"F2.wireOp",EDGE,"E40.0")])]})]}),makeQuery(id+"F3.boolean.opBoolean","INTERSECT",EDGE,{"derivedFrom":[subQ4,makeQuery(id+"F3.opExtrude","SWEPT_FACE",FACE,{"disambiguationData":[OSD([sQuery(id+"F2.wireOp",EDGE,"E40.1")])]})]}),makeQuery(id+"F3.boolean.opBoolean","INTERSECT",EDGE,{"derivedFrom":[subQ4,makeQuery(id+"F3.opExtrude","SWEPT_FACE",FACE,{"disambiguationData":[OSD([sQuery(id+"F2.wireOp",EDGE,"E40.2")])]})]}),makeQuery(id+"F3.boolean.opBoolean","INTERSECT",EDGE,{"derivedFrom":[subQ4,makeQuery(id+"F3.opExtrude","SWEPT_FACE",FACE,{"disambiguationData":[OSD([sQuery(id+"F2.wireOp",EDGE,"E40.3")])]})]}),makeQuery(id+"F3.boolean.opBoolean","INTERSECT",EDGE,{"derivedFrom":[subQ4,makeQuery(id+"F3.opExtrude","SWEPT_FACE",FACE,{"disambiguationData":[OSD([sQuery(id+"F2.wireOp",EDGE,"E40.4")])]})]}),makeQuery(id+"F3.boolean.opBoolean","INTERSECT",EDGE,{"derivedFrom":[subQ4,makeQuery(id+"F3.opExtrude","SWEPT_FACE",FACE,{"disambiguationData":[OSD([sQuery(id+"F2.wireOp",EDGE,"E40.5")])]})]}),makeQuery(id+"F3.boolean.opBoolean","INTERSECT",EDGE,{"derivedFrom":[subQ2,makeQuery(id+"F3.opExtrude","SWEPT_FACE",FACE,{"disambiguationData":[OSD([sQuery(id+"F2.wireOp",EDGE,"E36.0")])]})]}),makeQuery(id+"F3.boolean.opBoolean","INTERSECT",EDGE,{"derivedFrom":[subQ2,makeQuery(id+"F3.opExtrude","SWEPT_FACE",FACE,{"disambiguationData":[OSD([sQuery(id+"F2.wireOp",EDGE,"E36.1")])]})]}),makeQuery(id+"F3.boolean.opBoolean","INTERSECT",EDGE,{"derivedFrom":[subQ2,makeQuery(id+"F3.opExtrude","SWEPT_FACE",FACE,{"disambiguationData":[OSD([sQuery(id+"F2.wireOp",EDGE,"E36.2")])]})]}),makeQuery(id+"F3.boolean.opBoolean","INTERSECT",EDGE,{"derivedFrom":[subQ2,makeQuery(id+"F3.opExtrude","SWEPT_FACE",FACE,{"disambiguationData":[OSD([sQuery(id+"F2.wireOp",EDGE,"E36.3")])]})]}),makeQuery(id+"F3.boolean.opBoolean","INTERSECT",EDGE,{"derivedFrom":[subQ2,makeQuery(id+"F3.opExtrude","SWEPT_FACE",FACE,{"disambiguationData":[OSD([sQuery(id+"F2.wireOp",EDGE,"E36.4")])]})]}),makeQuery(id+"F3.boolean.opBoolean","INTERSECT",EDGE,{"derivedFrom":[subQ2,makeQuery(id+"F3.opExtrude","SWEPT_FACE",FACE,{"disambiguationData":[OSD([sQuery(id+"F2.wireOp",EDGE,"E36.5")])]})]}),makeQuery(id+"F3.boolean.opBoolean","INTERSECT",EDGE,{"derivedFrom":[subQ2,makeQuery(id+"F3.opExtrude","SWEPT_FACE",FACE,{"disambiguationData":[OSD([sQuery(id+"F2.wireOp",EDGE,"E37.0")])]})]}),makeQuery(id+"F3.boolean.opBoolean","INTERSECT",EDGE,{"derivedFrom":[subQ2,makeQuery(id+"F3.opExtrude","SWEPT_FACE",FACE,{"disambiguationData":[OSD([sQuery(id+"F2.wireOp",EDGE,"E37.1")])]})]}),makeQuery(id+"F3.boolean.opBoolean","INTERSECT",EDGE,{"derivedFrom":[subQ2,makeQuery(id+"F3.opExtrude","SWEPT_FACE",FACE,{"disambiguationData":[OSD([sQuery(id+"F2.wireOp",EDGE,"E37.2")])]})]}),makeQuery(id+"F3.boolean.opBoolean","INTERSECT",EDGE,{"derivedFrom":[subQ2,makeQuery(id+"F3.opExtrude","SWEPT_FACE",FACE,{"disambiguationData":[OSD([sQuery(id+"F2.wireOp",EDGE,"E37.3")])]})]}),makeQuery(id+"F3.boolean.opBoolean","INTERSECT",EDGE,{"derivedFrom":[subQ2,makeQuery(id+"F3.opExtrude","SWEPT_FACE",FACE,{"disambiguationData":[OSD([sQuery(id+"F2.wireOp",EDGE,"E37.4")])]})]}),makeQuery(id+"F3.boolean.opBoolean","INTERSECT",EDGE,{"derivedFrom":[subQ2,makeQuery(id+"F3.opExtrude","SWEPT_FACE",FACE,{"disambiguationData":[OSD([sQuery(id+"F2.wireOp",EDGE,"E37.5")])]})]}),makeQuery(id+"F3.boolean.opBoolean","INTERSECT",EDGE,{"derivedFrom":[subQ2,makeQuery(id+"F3.opExtrude","SWEPT_FACE",FACE,{"disambiguationData":[OSD([sQuery(id+"F2.wireOp",EDGE,"E38.0")])]})]}),makeQuery(id+"F3.boolean.opBoolean","INTERSECT",EDGE,{"derivedFrom":[subQ2,makeQuery(id+"F3.opExtrude","SWEPT_FACE",FACE,{"disambiguationData":[OSD([sQuery(id+"F2.wireOp",EDGE,"E38.1")])]})]}),makeQuery(id+"F3.boolean.opBoolean","INTERSECT",EDGE,{"derivedFrom":[subQ2,makeQuery(id+"F3.opExtrude","SWEPT_FACE",FACE,{"disambiguationData":[OSD([sQuery(id+"F2.wireOp",EDGE,"E38.2")])]})]}),makeQuery(id+"F3.boolean.opBoolean","INTERSECT",EDGE,{"derivedFrom":[subQ2,makeQuery(id+"F3.opExtrude","SWEPT_FACE",FACE,{"disambiguationData":[OSD([sQuery(id+"F2.wireOp",EDGE,"E38.3")])]})]}),makeQuery(id+"F3.boolean.opBoolean","INTERSECT",EDGE,{"derivedFrom":[subQ2,makeQuery(id+"F3.opExtrude","SWEPT_FACE",FACE,{"disambiguationData":[OSD([sQuery(id+"F2.wireOp",EDGE,"E38.4")])]})]}),makeQuery(id+"F3.boolean.opBoolean","INTERSECT",EDGE,{"derivedFrom":[subQ2,makeQuery(id+"F3.opExtrude","SWEPT_FACE",FACE,{"disambiguationData":[OSD([sQuery(id+"F2.wireOp",EDGE,"E38.5")])]})]})]);}
            var Q33;
            {var subQ0=sQuery(id+"F0.wireOp",EDGE,"E6");var subQ1=sQuery(id+"F0.wireOp",EDGE,"E18.top");var subQ2=makeQuery(id+"F1.opExtrude","SWEPT_FACE",FACE,{"disambiguationData":[OSD([subQ0]),TDD([makeQuery(id+"F0.imprint","IMPRINT",EDGE,{"disambiguationData":[TD([[makeQuery(id+"F0.imprint","INTERSECT",VERTEX,{"derivedFrom":[subQ0,sQuery(id+"F0.wireOp",EDGE,"E9")]}),1.0]])],"derivedFrom":subQ0})])]});var subQ4=makeQuery(id+"F1.opExtrude","SWEPT_FACE",FACE,{"disambiguationData":[OSD([subQ0]),TDD([makeQuery(id+"F0.imprint","IMPRINT",EDGE,{"disambiguationData":[TD([[makeQuery(id+"F0.imprint","INTERSECT",VERTEX,{"derivedFrom":[subQ0,subQ1,sQuery(id+"F0.wireOp",EDGE,"E18.right")]}),1.0]])],"derivedFrom":subQ0})])]});var subQ5=makeQuery(id+"F1.opExtrude","SWEPT_FACE",FACE,{"disambiguationData":[OSD([subQ0]),TDD([makeQuery(id+"F0.imprint","IMPRINT",EDGE,{"disambiguationData":[TD([[makeQuery(id+"F0.imprint","INTERSECT",VERTEX,{"derivedFrom":[subQ0,sQuery(id+"F0.wireOp",EDGE,"E12")]}),-1.0]])],"derivedFrom":subQ0})])]});Q33=qUnion([makeQuery(id+"F3.boolean.opBoolean","INTERSECT",EDGE,{"derivedFrom":[subQ5,makeQuery(id+"F3.opExtrude","SWEPT_FACE",FACE,{"disambiguationData":[OSD([sQuery(id+"F2.wireOp",EDGE,"E41.0")])]})]}),makeQuery(id+"F3.boolean.opBoolean","INTERSECT",EDGE,{"derivedFrom":[subQ5,makeQuery(id+"F3.opExtrude","SWEPT_FACE",FACE,{"disambiguationData":[OSD([sQuery(id+"F2.wireOp",EDGE,"E41.1")])]})]}),makeQuery(id+"F3.boolean.opBoolean","INTERSECT",EDGE,{"derivedFrom":[subQ5,makeQuery(id+"F3.opExtrude","SWEPT_FACE",FACE,{"disambiguationData":[OSD([sQuery(id+"F2.wireOp",EDGE,"E41.2")])]})]}),makeQuery(id+"F3.boolean.opBoolean","INTERSECT",EDGE,{"derivedFrom":[subQ5,makeQuery(id+"F3.opExtrude","SWEPT_FACE",FACE,{"disambiguationData":[OSD([sQuery(id+"F2.wireOp",EDGE,"E41.3")])]})]}),makeQuery(id+"F3.boolean.opBoolean","INTERSECT",EDGE,{"derivedFrom":[subQ5,makeQuery(id+"F3.opExtrude","SWEPT_FACE",FACE,{"disambiguationData":[OSD([sQuery(id+"F2.wireOp",EDGE,"E41.4")])]})]}),makeQuery(id+"F3.boolean.opBoolean","INTERSECT",EDGE,{"derivedFrom":[subQ5,makeQuery(id+"F3.opExtrude","SWEPT_FACE",FACE,{"disambiguationData":[OSD([sQuery(id+"F2.wireOp",EDGE,"E41.5")])]})]}),makeQuery(id+"F3.boolean.opBoolean","INTERSECT",EDGE,{"derivedFrom":[subQ5,makeQuery(id+"F3.opExtrude","SWEPT_FACE",FACE,{"disambiguationData":[OSD([sQuery(id+"F2.wireOp",EDGE,"E42.0")])]})]}),makeQuery(id+"F3.boolean.opBoolean","INTERSECT",EDGE,{"derivedFrom":[subQ5,makeQuery(id+"F3.opExtrude","SWEPT_FACE",FACE,{"disambiguationData":[OSD([sQuery(id+"F2.wireOp",EDGE,"E42.1")])]})]}),makeQuery(id+"F3.boolean.opBoolean","INTERSECT",EDGE,{"derivedFrom":[subQ5,makeQuery(id+"F3.opExtrude","SWEPT_FACE",FACE,{"disambiguationData":[OSD([sQuery(id+"F2.wireOp",EDGE,"E42.2")])]})]}),makeQuery(id+"F3.boolean.opBoolean","INTERSECT",EDGE,{"derivedFrom":[subQ5,makeQuery(id+"F3.opExtrude","SWEPT_FACE",FACE,{"disambiguationData":[OSD([sQuery(id+"F2.wireOp",EDGE,"E42.3")])]})]}),makeQuery(id+"F3.boolean.opBoolean","INTERSECT",EDGE,{"derivedFrom":[subQ5,makeQuery(id+"F3.opExtrude","SWEPT_FACE",FACE,{"disambiguationData":[OSD([sQuery(id+"F2.wireOp",EDGE,"E42.4")])]})]}),makeQuery(id+"F3.boolean.opBoolean","INTERSECT",EDGE,{"derivedFrom":[subQ5,makeQuery(id+"F3.opExtrude","SWEPT_FACE",FACE,{"disambiguationData":[OSD([sQuery(id+"F2.wireOp",EDGE,"E42.5")])]})]}),makeQuery(id+"F3.boolean.opBoolean","INTERSECT",EDGE,{"derivedFrom":[subQ4,makeQuery(id+"F3.opExtrude","SWEPT_FACE",FACE,{"disambiguationData":[OSD([sQuery(id+"F2.wireOp",EDGE,"E39.0")])]})]}),makeQuery(id+"F3.boolean.opBoolean","INTERSECT",EDGE,{"derivedFrom":[subQ4,makeQuery(id+"F3.opExtrude","SWEPT_FACE",FACE,{"disambiguationData":[OSD([sQuery(id+"F2.wireOp",EDGE,"E39.1")])]})]}),makeQuery(id+"F3.boolean.opBoolean","INTERSECT",EDGE,{"derivedFrom":[subQ4,makeQuery(id+"F3.opExtrude","SWEPT_FACE",FACE,{"disambiguationData":[OSD([sQuery(id+"F2.wireOp",EDGE,"E39.2")])]})]}),makeQuery(id+"F3.boolean.opBoolean","INTERSECT",EDGE,{"derivedFrom":[subQ4,makeQuery(id+"F3.opExtrude","SWEPT_FACE",FACE,{"disambiguationData":[OSD([sQuery(id+"F2.wireOp",EDGE,"E39.3")])]})]}),makeQuery(id+"F3.boolean.opBoolean","INTERSECT",EDGE,{"derivedFrom":[subQ4,makeQuery(id+"F3.opExtrude","SWEPT_FACE",FACE,{"disambiguationData":[OSD([sQuery(id+"F2.wireOp",EDGE,"E39.4")])]})]}),makeQuery(id+"F3.boolean.opBoolean","INTERSECT",EDGE,{"derivedFrom":[subQ4,makeQuery(id+"F3.opExtrude","SWEPT_FACE",FACE,{"disambiguationData":[OSD([sQuery(id+"F2.wireOp",EDGE,"E39.5")])]})]}),makeQuery(id+"F3.boolean.opBoolean","INTERSECT",EDGE,{"derivedFrom":[subQ4,makeQuery(id+"F3.opExtrude","SWEPT_FACE",FACE,{"disambiguationData":[OSD([sQuery(id+"F2.wireOp",EDGE,"E40.0")])]})]}),makeQuery(id+"F3.boolean.opBoolean","INTERSECT",EDGE,{"derivedFrom":[subQ4,makeQuery(id+"F3.opExtrude","SWEPT_FACE",FACE,{"disambiguationData":[OSD([sQuery(id+"F2.wireOp",EDGE,"E40.1")])]})]}),makeQuery(id+"F3.boolean.opBoolean","INTERSECT",EDGE,{"derivedFrom":[subQ4,makeQuery(id+"F3.opExtrude","SWEPT_FACE",FACE,{"disambiguationData":[OSD([sQuery(id+"F2.wireOp",EDGE,"E40.2")])]})]}),makeQuery(id+"F3.boolean.opBoolean","INTERSECT",EDGE,{"derivedFrom":[subQ4,makeQuery(id+"F3.opExtrude","SWEPT_FACE",FACE,{"disambiguationData":[OSD([sQuery(id+"F2.wireOp",EDGE,"E40.3")])]})]}),makeQuery(id+"F3.boolean.opBoolean","INTERSECT",EDGE,{"derivedFrom":[subQ4,makeQuery(id+"F3.opExtrude","SWEPT_FACE",FACE,{"disambiguationData":[OSD([sQuery(id+"F2.wireOp",EDGE,"E40.4")])]})]}),makeQuery(id+"F3.boolean.opBoolean","INTERSECT",EDGE,{"derivedFrom":[subQ4,makeQuery(id+"F3.opExtrude","SWEPT_FACE",FACE,{"disambiguationData":[OSD([sQuery(id+"F2.wireOp",EDGE,"E40.5")])]})]}),makeQuery(id+"F3.boolean.opBoolean","INTERSECT",EDGE,{"derivedFrom":[subQ2,makeQuery(id+"F3.opExtrude","SWEPT_FACE",FACE,{"disambiguationData":[OSD([sQuery(id+"F2.wireOp",EDGE,"E36.0")])]})]}),makeQuery(id+"F3.boolean.opBoolean","INTERSECT",EDGE,{"derivedFrom":[subQ2,makeQuery(id+"F3.opExtrude","SWEPT_FACE",FACE,{"disambiguationData":[OSD([sQuery(id+"F2.wireOp",EDGE,"E36.1")])]})]}),makeQuery(id+"F3.boolean.opBoolean","INTERSECT",EDGE,{"derivedFrom":[subQ2,makeQuery(id+"F3.opExtrude","SWEPT_FACE",FACE,{"disambiguationData":[OSD([sQuery(id+"F2.wireOp",EDGE,"E36.2")])]})]}),makeQuery(id+"F3.boolean.opBoolean","INTERSECT",EDGE,{"derivedFrom":[subQ2,makeQuery(id+"F3.opExtrude","SWEPT_FACE",FACE,{"disambiguationData":[OSD([sQuery(id+"F2.wireOp",EDGE,"E36.3")])]})]}),makeQuery(id+"F3.boolean.opBoolean","INTERSECT",EDGE,{"derivedFrom":[subQ2,makeQuery(id+"F3.opExtrude","SWEPT_FACE",FACE,{"disambiguationData":[OSD([sQuery(id+"F2.wireOp",EDGE,"E36.4")])]})]}),makeQuery(id+"F3.boolean.opBoolean","INTERSECT",EDGE,{"derivedFrom":[subQ2,makeQuery(id+"F3.opExtrude","SWEPT_FACE",FACE,{"disambiguationData":[OSD([sQuery(id+"F2.wireOp",EDGE,"E36.5")])]})]}),makeQuery(id+"F3.boolean.opBoolean","INTERSECT",EDGE,{"derivedFrom":[subQ2,makeQuery(id+"F3.opExtrude","SWEPT_FACE",FACE,{"disambiguationData":[OSD([sQuery(id+"F2.wireOp",EDGE,"E37.0")])]})]}),makeQuery(id+"F3.boolean.opBoolean","INTERSECT",EDGE,{"derivedFrom":[subQ2,makeQuery(id+"F3.opExtrude","SWEPT_FACE",FACE,{"disambiguationData":[OSD([sQuery(id+"F2.wireOp",EDGE,"E37.1")])]})]}),makeQuery(id+"F3.boolean.opBoolean","INTERSECT",EDGE,{"derivedFrom":[subQ2,makeQuery(id+"F3.opExtrude","SWEPT_FACE",FACE,{"disambiguationData":[OSD([sQuery(id+"F2.wireOp",EDGE,"E37.2")])]})]}),makeQuery(id+"F3.boolean.opBoolean","INTERSECT",EDGE,{"derivedFrom":[subQ2,makeQuery(id+"F3.opExtrude","SWEPT_FACE",FACE,{"disambiguationData":[OSD([sQuery(id+"F2.wireOp",EDGE,"E37.3")])]})]}),makeQuery(id+"F3.boolean.opBoolean","INTERSECT",EDGE,{"derivedFrom":[subQ2,makeQuery(id+"F3.opExtrude","SWEPT_FACE",FACE,{"disambiguationData":[OSD([sQuery(id+"F2.wireOp",EDGE,"E37.4")])]})]}),makeQuery(id+"F3.boolean.opBoolean","INTERSECT",EDGE,{"derivedFrom":[subQ2,makeQuery(id+"F3.opExtrude","SWEPT_FACE",FACE,{"disambiguationData":[OSD([sQuery(id+"F2.wireOp",EDGE,"E37.5")])]})]}),makeQuery(id+"F3.boolean.opBoolean","INTERSECT",EDGE,{"derivedFrom":[subQ2,makeQuery(id+"F3.opExtrude","SWEPT_FACE",FACE,{"disambiguationData":[OSD([sQuery(id+"F2.wireOp",EDGE,"E38.0")])]})]}),makeQuery(id+"F3.boolean.opBoolean","INTERSECT",EDGE,{"derivedFrom":[subQ2,makeQuery(id+"F3.opExtrude","SWEPT_FACE",FACE,{"disambiguationData":[OSD([sQuery(id+"F2.wireOp",EDGE,"E38.1")])]})]}),makeQuery(id+"F3.boolean.opBoolean","INTERSECT",EDGE,{"derivedFrom":[subQ2,makeQuery(id+"F3.opExtrude","SWEPT_FACE",FACE,{"disambiguationData":[OSD([sQuery(id+"F2.wireOp",EDGE,"E38.2")])]})]}),makeQuery(id+"F3.boolean.opBoolean","INTERSECT",EDGE,{"derivedFrom":[subQ2,makeQuery(id+"F3.opExtrude","SWEPT_FACE",FACE,{"disambiguationData":[OSD([sQuery(id+"F2.wireOp",EDGE,"E38.3")])]})]}),makeQuery(id+"F3.boolean.opBoolean","INTERSECT",EDGE,{"derivedFrom":[subQ2,makeQuery(id+"F3.opExtrude","SWEPT_FACE",FACE,{"disambiguationData":[OSD([sQuery(id+"F2.wireOp",EDGE,"E38.4")])]})]}),makeQuery(id+"F3.boolean.opBoolean","INTERSECT",EDGE,{"derivedFrom":[subQ2,makeQuery(id+"F3.opExtrude","SWEPT_FACE",FACE,{"disambiguationData":[OSD([sQuery(id+"F2.wireOp",EDGE,"E38.5")])]})]})]);}
            var Q34;
            {var subQ0=sQuery(id+"F0.wireOp",EDGE,"E6");var subQ1=sQuery(id+"F0.wireOp",EDGE,"E18.top");var subQ2=makeQuery(id+"F1.opExtrude","SWEPT_FACE",FACE,{"disambiguationData":[OSD([subQ0]),TDD([makeQuery(id+"F0.imprint","IMPRINT",EDGE,{"disambiguationData":[TD([[makeQuery(id+"F0.imprint","INTERSECT",VERTEX,{"derivedFrom":[subQ0,sQuery(id+"F0.wireOp",EDGE,"E9")]}),1.0]])],"derivedFrom":subQ0})])]});var subQ4=makeQuery(id+"F1.opExtrude","SWEPT_FACE",FACE,{"disambiguationData":[OSD([subQ0]),TDD([makeQuery(id+"F0.imprint","IMPRINT",EDGE,{"disambiguationData":[TD([[makeQuery(id+"F0.imprint","INTERSECT",VERTEX,{"derivedFrom":[subQ0,subQ1,sQuery(id+"F0.wireOp",EDGE,"E18.right")]}),1.0]])],"derivedFrom":subQ0})])]});var subQ5=makeQuery(id+"F1.opExtrude","SWEPT_FACE",FACE,{"disambiguationData":[OSD([subQ0]),TDD([makeQuery(id+"F0.imprint","IMPRINT",EDGE,{"disambiguationData":[TD([[makeQuery(id+"F0.imprint","INTERSECT",VERTEX,{"derivedFrom":[subQ0,sQuery(id+"F0.wireOp",EDGE,"E12")]}),-1.0]])],"derivedFrom":subQ0})])]});Q34=qUnion([makeQuery(id+"F3.boolean.opBoolean","INTERSECT",EDGE,{"derivedFrom":[subQ5,makeQuery(id+"F3.opExtrude","SWEPT_FACE",FACE,{"disambiguationData":[OSD([sQuery(id+"F2.wireOp",EDGE,"E41.0")])]})]}),makeQuery(id+"F3.boolean.opBoolean","INTERSECT",EDGE,{"derivedFrom":[subQ5,makeQuery(id+"F3.opExtrude","SWEPT_FACE",FACE,{"disambiguationData":[OSD([sQuery(id+"F2.wireOp",EDGE,"E41.1")])]})]}),makeQuery(id+"F3.boolean.opBoolean","INTERSECT",EDGE,{"derivedFrom":[subQ5,makeQuery(id+"F3.opExtrude","SWEPT_FACE",FACE,{"disambiguationData":[OSD([sQuery(id+"F2.wireOp",EDGE,"E41.2")])]})]}),makeQuery(id+"F3.boolean.opBoolean","INTERSECT",EDGE,{"derivedFrom":[subQ5,makeQuery(id+"F3.opExtrude","SWEPT_FACE",FACE,{"disambiguationData":[OSD([sQuery(id+"F2.wireOp",EDGE,"E41.3")])]})]}),makeQuery(id+"F3.boolean.opBoolean","INTERSECT",EDGE,{"derivedFrom":[subQ5,makeQuery(id+"F3.opExtrude","SWEPT_FACE",FACE,{"disambiguationData":[OSD([sQuery(id+"F2.wireOp",EDGE,"E41.4")])]})]}),makeQuery(id+"F3.boolean.opBoolean","INTERSECT",EDGE,{"derivedFrom":[subQ5,makeQuery(id+"F3.opExtrude","SWEPT_FACE",FACE,{"disambiguationData":[OSD([sQuery(id+"F2.wireOp",EDGE,"E41.5")])]})]}),makeQuery(id+"F3.boolean.opBoolean","INTERSECT",EDGE,{"derivedFrom":[subQ5,makeQuery(id+"F3.opExtrude","SWEPT_FACE",FACE,{"disambiguationData":[OSD([sQuery(id+"F2.wireOp",EDGE,"E42.0")])]})]}),makeQuery(id+"F3.boolean.opBoolean","INTERSECT",EDGE,{"derivedFrom":[subQ5,makeQuery(id+"F3.opExtrude","SWEPT_FACE",FACE,{"disambiguationData":[OSD([sQuery(id+"F2.wireOp",EDGE,"E42.1")])]})]}),makeQuery(id+"F3.boolean.opBoolean","INTERSECT",EDGE,{"derivedFrom":[subQ5,makeQuery(id+"F3.opExtrude","SWEPT_FACE",FACE,{"disambiguationData":[OSD([sQuery(id+"F2.wireOp",EDGE,"E42.2")])]})]}),makeQuery(id+"F3.boolean.opBoolean","INTERSECT",EDGE,{"derivedFrom":[subQ5,makeQuery(id+"F3.opExtrude","SWEPT_FACE",FACE,{"disambiguationData":[OSD([sQuery(id+"F2.wireOp",EDGE,"E42.3")])]})]}),makeQuery(id+"F3.boolean.opBoolean","INTERSECT",EDGE,{"derivedFrom":[subQ5,makeQuery(id+"F3.opExtrude","SWEPT_FACE",FACE,{"disambiguationData":[OSD([sQuery(id+"F2.wireOp",EDGE,"E42.4")])]})]}),makeQuery(id+"F3.boolean.opBoolean","INTERSECT",EDGE,{"derivedFrom":[subQ5,makeQuery(id+"F3.opExtrude","SWEPT_FACE",FACE,{"disambiguationData":[OSD([sQuery(id+"F2.wireOp",EDGE,"E42.5")])]})]}),makeQuery(id+"F3.boolean.opBoolean","INTERSECT",EDGE,{"derivedFrom":[subQ4,makeQuery(id+"F3.opExtrude","SWEPT_FACE",FACE,{"disambiguationData":[OSD([sQuery(id+"F2.wireOp",EDGE,"E39.0")])]})]}),makeQuery(id+"F3.boolean.opBoolean","INTERSECT",EDGE,{"derivedFrom":[subQ4,makeQuery(id+"F3.opExtrude","SWEPT_FACE",FACE,{"disambiguationData":[OSD([sQuery(id+"F2.wireOp",EDGE,"E39.1")])]})]}),makeQuery(id+"F3.boolean.opBoolean","INTERSECT",EDGE,{"derivedFrom":[subQ4,makeQuery(id+"F3.opExtrude","SWEPT_FACE",FACE,{"disambiguationData":[OSD([sQuery(id+"F2.wireOp",EDGE,"E39.2")])]})]}),makeQuery(id+"F3.boolean.opBoolean","INTERSECT",EDGE,{"derivedFrom":[subQ4,makeQuery(id+"F3.opExtrude","SWEPT_FACE",FACE,{"disambiguationData":[OSD([sQuery(id+"F2.wireOp",EDGE,"E39.3")])]})]}),makeQuery(id+"F3.boolean.opBoolean","INTERSECT",EDGE,{"derivedFrom":[subQ4,makeQuery(id+"F3.opExtrude","SWEPT_FACE",FACE,{"disambiguationData":[OSD([sQuery(id+"F2.wireOp",EDGE,"E39.4")])]})]}),makeQuery(id+"F3.boolean.opBoolean","INTERSECT",EDGE,{"derivedFrom":[subQ4,makeQuery(id+"F3.opExtrude","SWEPT_FACE",FACE,{"disambiguationData":[OSD([sQuery(id+"F2.wireOp",EDGE,"E39.5")])]})]}),makeQuery(id+"F3.boolean.opBoolean","INTERSECT",EDGE,{"derivedFrom":[subQ4,makeQuery(id+"F3.opExtrude","SWEPT_FACE",FACE,{"disambiguationData":[OSD([sQuery(id+"F2.wireOp",EDGE,"E40.0")])]})]}),makeQuery(id+"F3.boolean.opBoolean","INTERSECT",EDGE,{"derivedFrom":[subQ4,makeQuery(id+"F3.opExtrude","SWEPT_FACE",FACE,{"disambiguationData":[OSD([sQuery(id+"F2.wireOp",EDGE,"E40.1")])]})]}),makeQuery(id+"F3.boolean.opBoolean","INTERSECT",EDGE,{"derivedFrom":[subQ4,makeQuery(id+"F3.opExtrude","SWEPT_FACE",FACE,{"disambiguationData":[OSD([sQuery(id+"F2.wireOp",EDGE,"E40.2")])]})]}),makeQuery(id+"F3.boolean.opBoolean","INTERSECT",EDGE,{"derivedFrom":[subQ4,makeQuery(id+"F3.opExtrude","SWEPT_FACE",FACE,{"disambiguationData":[OSD([sQuery(id+"F2.wireOp",EDGE,"E40.3")])]})]}),makeQuery(id+"F3.boolean.opBoolean","INTERSECT",EDGE,{"derivedFrom":[subQ4,makeQuery(id+"F3.opExtrude","SWEPT_FACE",FACE,{"disambiguationData":[OSD([sQuery(id+"F2.wireOp",EDGE,"E40.4")])]})]}),makeQuery(id+"F3.boolean.opBoolean","INTERSECT",EDGE,{"derivedFrom":[subQ4,makeQuery(id+"F3.opExtrude","SWEPT_FACE",FACE,{"disambiguationData":[OSD([sQuery(id+"F2.wireOp",EDGE,"E40.5")])]})]}),makeQuery(id+"F3.boolean.opBoolean","INTERSECT",EDGE,{"derivedFrom":[subQ2,makeQuery(id+"F3.opExtrude","SWEPT_FACE",FACE,{"disambiguationData":[OSD([sQuery(id+"F2.wireOp",EDGE,"E36.0")])]})]}),makeQuery(id+"F3.boolean.opBoolean","INTERSECT",EDGE,{"derivedFrom":[subQ2,makeQuery(id+"F3.opExtrude","SWEPT_FACE",FACE,{"disambiguationData":[OSD([sQuery(id+"F2.wireOp",EDGE,"E36.1")])]})]}),makeQuery(id+"F3.boolean.opBoolean","INTERSECT",EDGE,{"derivedFrom":[subQ2,makeQuery(id+"F3.opExtrude","SWEPT_FACE",FACE,{"disambiguationData":[OSD([sQuery(id+"F2.wireOp",EDGE,"E36.2")])]})]}),makeQuery(id+"F3.boolean.opBoolean","INTERSECT",EDGE,{"derivedFrom":[subQ2,makeQuery(id+"F3.opExtrude","SWEPT_FACE",FACE,{"disambiguationData":[OSD([sQuery(id+"F2.wireOp",EDGE,"E36.3")])]})]}),makeQuery(id+"F3.boolean.opBoolean","INTERSECT",EDGE,{"derivedFrom":[subQ2,makeQuery(id+"F3.opExtrude","SWEPT_FACE",FACE,{"disambiguationData":[OSD([sQuery(id+"F2.wireOp",EDGE,"E36.4")])]})]}),makeQuery(id+"F3.boolean.opBoolean","INTERSECT",EDGE,{"derivedFrom":[subQ2,makeQuery(id+"F3.opExtrude","SWEPT_FACE",FACE,{"disambiguationData":[OSD([sQuery(id+"F2.wireOp",EDGE,"E36.5")])]})]}),makeQuery(id+"F3.boolean.opBoolean","INTERSECT",EDGE,{"derivedFrom":[subQ2,makeQuery(id+"F3.opExtrude","SWEPT_FACE",FACE,{"disambiguationData":[OSD([sQuery(id+"F2.wireOp",EDGE,"E37.0")])]})]}),makeQuery(id+"F3.boolean.opBoolean","INTERSECT",EDGE,{"derivedFrom":[subQ2,makeQuery(id+"F3.opExtrude","SWEPT_FACE",FACE,{"disambiguationData":[OSD([sQuery(id+"F2.wireOp",EDGE,"E37.1")])]})]}),makeQuery(id+"F3.boolean.opBoolean","INTERSECT",EDGE,{"derivedFrom":[subQ2,makeQuery(id+"F3.opExtrude","SWEPT_FACE",FACE,{"disambiguationData":[OSD([sQuery(id+"F2.wireOp",EDGE,"E37.2")])]})]}),makeQuery(id+"F3.boolean.opBoolean","INTERSECT",EDGE,{"derivedFrom":[subQ2,makeQuery(id+"F3.opExtrude","SWEPT_FACE",FACE,{"disambiguationData":[OSD([sQuery(id+"F2.wireOp",EDGE,"E37.3")])]})]}),makeQuery(id+"F3.boolean.opBoolean","INTERSECT",EDGE,{"derivedFrom":[subQ2,makeQuery(id+"F3.opExtrude","SWEPT_FACE",FACE,{"disambiguationData":[OSD([sQuery(id+"F2.wireOp",EDGE,"E37.4")])]})]}),makeQuery(id+"F3.boolean.opBoolean","INTERSECT",EDGE,{"derivedFrom":[subQ2,makeQuery(id+"F3.opExtrude","SWEPT_FACE",FACE,{"disambiguationData":[OSD([sQuery(id+"F2.wireOp",EDGE,"E37.5")])]})]}),makeQuery(id+"F3.boolean.opBoolean","INTERSECT",EDGE,{"derivedFrom":[subQ2,makeQuery(id+"F3.opExtrude","SWEPT_FACE",FACE,{"disambiguationData":[OSD([sQuery(id+"F2.wireOp",EDGE,"E38.0")])]})]}),makeQuery(id+"F3.boolean.opBoolean","INTERSECT",EDGE,{"derivedFrom":[subQ2,makeQuery(id+"F3.opExtrude","SWEPT_FACE",FACE,{"disambiguationData":[OSD([sQuery(id+"F2.wireOp",EDGE,"E38.1")])]})]}),makeQuery(id+"F3.boolean.opBoolean","INTERSECT",EDGE,{"derivedFrom":[subQ2,makeQuery(id+"F3.opExtrude","SWEPT_FACE",FACE,{"disambiguationData":[OSD([sQuery(id+"F2.wireOp",EDGE,"E38.2")])]})]}),makeQuery(id+"F3.boolean.opBoolean","INTERSECT",EDGE,{"derivedFrom":[subQ2,makeQuery(id+"F3.opExtrude","SWEPT_FACE",FACE,{"disambiguationData":[OSD([sQuery(id+"F2.wireOp",EDGE,"E38.3")])]})]}),makeQuery(id+"F3.boolean.opBoolean","INTERSECT",EDGE,{"derivedFrom":[subQ2,makeQuery(id+"F3.opExtrude","SWEPT_FACE",FACE,{"disambiguationData":[OSD([sQuery(id+"F2.wireOp",EDGE,"E38.4")])]})]}),makeQuery(id+"F3.boolean.opBoolean","INTERSECT",EDGE,{"derivedFrom":[subQ2,makeQuery(id+"F3.opExtrude","SWEPT_FACE",FACE,{"disambiguationData":[OSD([sQuery(id+"F2.wireOp",EDGE,"E38.5")])]})]})]);}
            var Q35;
            {var subQ0=sQuery(id+"F0.wireOp",EDGE,"E6");var subQ1=sQuery(id+"F0.wireOp",EDGE,"E18.top");var subQ2=makeQuery(id+"F1.opExtrude","SWEPT_FACE",FACE,{"disambiguationData":[OSD([subQ0]),TDD([makeQuery(id+"F0.imprint","IMPRINT",EDGE,{"disambiguationData":[TD([[makeQuery(id+"F0.imprint","INTERSECT",VERTEX,{"derivedFrom":[subQ0,sQuery(id+"F0.wireOp",EDGE,"E9")]}),1.0]])],"derivedFrom":subQ0})])]});var subQ4=makeQuery(id+"F1.opExtrude","SWEPT_FACE",FACE,{"disambiguationData":[OSD([subQ0]),TDD([makeQuery(id+"F0.imprint","IMPRINT",EDGE,{"disambiguationData":[TD([[makeQuery(id+"F0.imprint","INTERSECT",VERTEX,{"derivedFrom":[subQ0,subQ1,sQuery(id+"F0.wireOp",EDGE,"E18.right")]}),1.0]])],"derivedFrom":subQ0})])]});var subQ5=makeQuery(id+"F1.opExtrude","SWEPT_FACE",FACE,{"disambiguationData":[OSD([subQ0]),TDD([makeQuery(id+"F0.imprint","IMPRINT",EDGE,{"disambiguationData":[TD([[makeQuery(id+"F0.imprint","INTERSECT",VERTEX,{"derivedFrom":[subQ0,sQuery(id+"F0.wireOp",EDGE,"E12")]}),-1.0]])],"derivedFrom":subQ0})])]});Q35=qUnion([makeQuery(id+"F3.boolean.opBoolean","INTERSECT",EDGE,{"derivedFrom":[subQ5,makeQuery(id+"F3.opExtrude","SWEPT_FACE",FACE,{"disambiguationData":[OSD([sQuery(id+"F2.wireOp",EDGE,"E41.0")])]})]}),makeQuery(id+"F3.boolean.opBoolean","INTERSECT",EDGE,{"derivedFrom":[subQ5,makeQuery(id+"F3.opExtrude","SWEPT_FACE",FACE,{"disambiguationData":[OSD([sQuery(id+"F2.wireOp",EDGE,"E41.1")])]})]}),makeQuery(id+"F3.boolean.opBoolean","INTERSECT",EDGE,{"derivedFrom":[subQ5,makeQuery(id+"F3.opExtrude","SWEPT_FACE",FACE,{"disambiguationData":[OSD([sQuery(id+"F2.wireOp",EDGE,"E41.2")])]})]}),makeQuery(id+"F3.boolean.opBoolean","INTERSECT",EDGE,{"derivedFrom":[subQ5,makeQuery(id+"F3.opExtrude","SWEPT_FACE",FACE,{"disambiguationData":[OSD([sQuery(id+"F2.wireOp",EDGE,"E41.3")])]})]}),makeQuery(id+"F3.boolean.opBoolean","INTERSECT",EDGE,{"derivedFrom":[subQ5,makeQuery(id+"F3.opExtrude","SWEPT_FACE",FACE,{"disambiguationData":[OSD([sQuery(id+"F2.wireOp",EDGE,"E41.4")])]})]}),makeQuery(id+"F3.boolean.opBoolean","INTERSECT",EDGE,{"derivedFrom":[subQ5,makeQuery(id+"F3.opExtrude","SWEPT_FACE",FACE,{"disambiguationData":[OSD([sQuery(id+"F2.wireOp",EDGE,"E41.5")])]})]}),makeQuery(id+"F3.boolean.opBoolean","INTERSECT",EDGE,{"derivedFrom":[subQ5,makeQuery(id+"F3.opExtrude","SWEPT_FACE",FACE,{"disambiguationData":[OSD([sQuery(id+"F2.wireOp",EDGE,"E42.0")])]})]}),makeQuery(id+"F3.boolean.opBoolean","INTERSECT",EDGE,{"derivedFrom":[subQ5,makeQuery(id+"F3.opExtrude","SWEPT_FACE",FACE,{"disambiguationData":[OSD([sQuery(id+"F2.wireOp",EDGE,"E42.1")])]})]}),makeQuery(id+"F3.boolean.opBoolean","INTERSECT",EDGE,{"derivedFrom":[subQ5,makeQuery(id+"F3.opExtrude","SWEPT_FACE",FACE,{"disambiguationData":[OSD([sQuery(id+"F2.wireOp",EDGE,"E42.2")])]})]}),makeQuery(id+"F3.boolean.opBoolean","INTERSECT",EDGE,{"derivedFrom":[subQ5,makeQuery(id+"F3.opExtrude","SWEPT_FACE",FACE,{"disambiguationData":[OSD([sQuery(id+"F2.wireOp",EDGE,"E42.3")])]})]}),makeQuery(id+"F3.boolean.opBoolean","INTERSECT",EDGE,{"derivedFrom":[subQ5,makeQuery(id+"F3.opExtrude","SWEPT_FACE",FACE,{"disambiguationData":[OSD([sQuery(id+"F2.wireOp",EDGE,"E42.4")])]})]}),makeQuery(id+"F3.boolean.opBoolean","INTERSECT",EDGE,{"derivedFrom":[subQ5,makeQuery(id+"F3.opExtrude","SWEPT_FACE",FACE,{"disambiguationData":[OSD([sQuery(id+"F2.wireOp",EDGE,"E42.5")])]})]}),makeQuery(id+"F3.boolean.opBoolean","INTERSECT",EDGE,{"derivedFrom":[subQ4,makeQuery(id+"F3.opExtrude","SWEPT_FACE",FACE,{"disambiguationData":[OSD([sQuery(id+"F2.wireOp",EDGE,"E39.0")])]})]}),makeQuery(id+"F3.boolean.opBoolean","INTERSECT",EDGE,{"derivedFrom":[subQ4,makeQuery(id+"F3.opExtrude","SWEPT_FACE",FACE,{"disambiguationData":[OSD([sQuery(id+"F2.wireOp",EDGE,"E39.1")])]})]}),makeQuery(id+"F3.boolean.opBoolean","INTERSECT",EDGE,{"derivedFrom":[subQ4,makeQuery(id+"F3.opExtrude","SWEPT_FACE",FACE,{"disambiguationData":[OSD([sQuery(id+"F2.wireOp",EDGE,"E39.2")])]})]}),makeQuery(id+"F3.boolean.opBoolean","INTERSECT",EDGE,{"derivedFrom":[subQ4,makeQuery(id+"F3.opExtrude","SWEPT_FACE",FACE,{"disambiguationData":[OSD([sQuery(id+"F2.wireOp",EDGE,"E39.3")])]})]}),makeQuery(id+"F3.boolean.opBoolean","INTERSECT",EDGE,{"derivedFrom":[subQ4,makeQuery(id+"F3.opExtrude","SWEPT_FACE",FACE,{"disambiguationData":[OSD([sQuery(id+"F2.wireOp",EDGE,"E39.4")])]})]}),makeQuery(id+"F3.boolean.opBoolean","INTERSECT",EDGE,{"derivedFrom":[subQ4,makeQuery(id+"F3.opExtrude","SWEPT_FACE",FACE,{"disambiguationData":[OSD([sQuery(id+"F2.wireOp",EDGE,"E39.5")])]})]}),makeQuery(id+"F3.boolean.opBoolean","INTERSECT",EDGE,{"derivedFrom":[subQ4,makeQuery(id+"F3.opExtrude","SWEPT_FACE",FACE,{"disambiguationData":[OSD([sQuery(id+"F2.wireOp",EDGE,"E40.0")])]})]}),makeQuery(id+"F3.boolean.opBoolean","INTERSECT",EDGE,{"derivedFrom":[subQ4,makeQuery(id+"F3.opExtrude","SWEPT_FACE",FACE,{"disambiguationData":[OSD([sQuery(id+"F2.wireOp",EDGE,"E40.1")])]})]}),makeQuery(id+"F3.boolean.opBoolean","INTERSECT",EDGE,{"derivedFrom":[subQ4,makeQuery(id+"F3.opExtrude","SWEPT_FACE",FACE,{"disambiguationData":[OSD([sQuery(id+"F2.wireOp",EDGE,"E40.2")])]})]}),makeQuery(id+"F3.boolean.opBoolean","INTERSECT",EDGE,{"derivedFrom":[subQ4,makeQuery(id+"F3.opExtrude","SWEPT_FACE",FACE,{"disambiguationData":[OSD([sQuery(id+"F2.wireOp",EDGE,"E40.3")])]})]}),makeQuery(id+"F3.boolean.opBoolean","INTERSECT",EDGE,{"derivedFrom":[subQ4,makeQuery(id+"F3.opExtrude","SWEPT_FACE",FACE,{"disambiguationData":[OSD([sQuery(id+"F2.wireOp",EDGE,"E40.4")])]})]}),makeQuery(id+"F3.boolean.opBoolean","INTERSECT",EDGE,{"derivedFrom":[subQ4,makeQuery(id+"F3.opExtrude","SWEPT_FACE",FACE,{"disambiguationData":[OSD([sQuery(id+"F2.wireOp",EDGE,"E40.5")])]})]}),makeQuery(id+"F3.boolean.opBoolean","INTERSECT",EDGE,{"derivedFrom":[subQ2,makeQuery(id+"F3.opExtrude","SWEPT_FACE",FACE,{"disambiguationData":[OSD([sQuery(id+"F2.wireOp",EDGE,"E36.0")])]})]}),makeQuery(id+"F3.boolean.opBoolean","INTERSECT",EDGE,{"derivedFrom":[subQ2,makeQuery(id+"F3.opExtrude","SWEPT_FACE",FACE,{"disambiguationData":[OSD([sQuery(id+"F2.wireOp",EDGE,"E36.1")])]})]}),makeQuery(id+"F3.boolean.opBoolean","INTERSECT",EDGE,{"derivedFrom":[subQ2,makeQuery(id+"F3.opExtrude","SWEPT_FACE",FACE,{"disambiguationData":[OSD([sQuery(id+"F2.wireOp",EDGE,"E36.2")])]})]}),makeQuery(id+"F3.boolean.opBoolean","INTERSECT",EDGE,{"derivedFrom":[subQ2,makeQuery(id+"F3.opExtrude","SWEPT_FACE",FACE,{"disambiguationData":[OSD([sQuery(id+"F2.wireOp",EDGE,"E36.3")])]})]}),makeQuery(id+"F3.boolean.opBoolean","INTERSECT",EDGE,{"derivedFrom":[subQ2,makeQuery(id+"F3.opExtrude","SWEPT_FACE",FACE,{"disambiguationData":[OSD([sQuery(id+"F2.wireOp",EDGE,"E36.4")])]})]}),makeQuery(id+"F3.boolean.opBoolean","INTERSECT",EDGE,{"derivedFrom":[subQ2,makeQuery(id+"F3.opExtrude","SWEPT_FACE",FACE,{"disambiguationData":[OSD([sQuery(id+"F2.wireOp",EDGE,"E36.5")])]})]}),makeQuery(id+"F3.boolean.opBoolean","INTERSECT",EDGE,{"derivedFrom":[subQ2,makeQuery(id+"F3.opExtrude","SWEPT_FACE",FACE,{"disambiguationData":[OSD([sQuery(id+"F2.wireOp",EDGE,"E37.0")])]})]}),makeQuery(id+"F3.boolean.opBoolean","INTERSECT",EDGE,{"derivedFrom":[subQ2,makeQuery(id+"F3.opExtrude","SWEPT_FACE",FACE,{"disambiguationData":[OSD([sQuery(id+"F2.wireOp",EDGE,"E37.1")])]})]}),makeQuery(id+"F3.boolean.opBoolean","INTERSECT",EDGE,{"derivedFrom":[subQ2,makeQuery(id+"F3.opExtrude","SWEPT_FACE",FACE,{"disambiguationData":[OSD([sQuery(id+"F2.wireOp",EDGE,"E37.2")])]})]}),makeQuery(id+"F3.boolean.opBoolean","INTERSECT",EDGE,{"derivedFrom":[subQ2,makeQuery(id+"F3.opExtrude","SWEPT_FACE",FACE,{"disambiguationData":[OSD([sQuery(id+"F2.wireOp",EDGE,"E37.3")])]})]}),makeQuery(id+"F3.boolean.opBoolean","INTERSECT",EDGE,{"derivedFrom":[subQ2,makeQuery(id+"F3.opExtrude","SWEPT_FACE",FACE,{"disambiguationData":[OSD([sQuery(id+"F2.wireOp",EDGE,"E37.4")])]})]}),makeQuery(id+"F3.boolean.opBoolean","INTERSECT",EDGE,{"derivedFrom":[subQ2,makeQuery(id+"F3.opExtrude","SWEPT_FACE",FACE,{"disambiguationData":[OSD([sQuery(id+"F2.wireOp",EDGE,"E37.5")])]})]}),makeQuery(id+"F3.boolean.opBoolean","INTERSECT",EDGE,{"derivedFrom":[subQ2,makeQuery(id+"F3.opExtrude","SWEPT_FACE",FACE,{"disambiguationData":[OSD([sQuery(id+"F2.wireOp",EDGE,"E38.0")])]})]}),makeQuery(id+"F3.boolean.opBoolean","INTERSECT",EDGE,{"derivedFrom":[subQ2,makeQuery(id+"F3.opExtrude","SWEPT_FACE",FACE,{"disambiguationData":[OSD([sQuery(id+"F2.wireOp",EDGE,"E38.1")])]})]}),makeQuery(id+"F3.boolean.opBoolean","INTERSECT",EDGE,{"derivedFrom":[subQ2,makeQuery(id+"F3.opExtrude","SWEPT_FACE",FACE,{"disambiguationData":[OSD([sQuery(id+"F2.wireOp",EDGE,"E38.2")])]})]}),makeQuery(id+"F3.boolean.opBoolean","INTERSECT",EDGE,{"derivedFrom":[subQ2,makeQuery(id+"F3.opExtrude","SWEPT_FACE",FACE,{"disambiguationData":[OSD([sQuery(id+"F2.wireOp",EDGE,"E38.3")])]})]}),makeQuery(id+"F3.boolean.opBoolean","INTERSECT",EDGE,{"derivedFrom":[subQ2,makeQuery(id+"F3.opExtrude","SWEPT_FACE",FACE,{"disambiguationData":[OSD([sQuery(id+"F2.wireOp",EDGE,"E38.4")])]})]}),makeQuery(id+"F3.boolean.opBoolean","INTERSECT",EDGE,{"derivedFrom":[subQ2,makeQuery(id+"F3.opExtrude","SWEPT_FACE",FACE,{"disambiguationData":[OSD([sQuery(id+"F2.wireOp",EDGE,"E38.5")])]})]})]);}
            var Q36;
            {var subQ0=sQuery(id+"F0.wireOp",EDGE,"E6");var subQ1=sQuery(id+"F0.wireOp",EDGE,"E18.top");var subQ2=makeQuery(id+"F1.opExtrude","SWEPT_FACE",FACE,{"disambiguationData":[OSD([subQ0]),TDD([makeQuery(id+"F0.imprint","IMPRINT",EDGE,{"disambiguationData":[TD([[makeQuery(id+"F0.imprint","INTERSECT",VERTEX,{"derivedFrom":[subQ0,sQuery(id+"F0.wireOp",EDGE,"E9")]}),1.0]])],"derivedFrom":subQ0})])]});var subQ4=makeQuery(id+"F1.opExtrude","SWEPT_FACE",FACE,{"disambiguationData":[OSD([subQ0]),TDD([makeQuery(id+"F0.imprint","IMPRINT",EDGE,{"disambiguationData":[TD([[makeQuery(id+"F0.imprint","INTERSECT",VERTEX,{"derivedFrom":[subQ0,subQ1,sQuery(id+"F0.wireOp",EDGE,"E18.right")]}),1.0]])],"derivedFrom":subQ0})])]});var subQ5=makeQuery(id+"F1.opExtrude","SWEPT_FACE",FACE,{"disambiguationData":[OSD([subQ0]),TDD([makeQuery(id+"F0.imprint","IMPRINT",EDGE,{"disambiguationData":[TD([[makeQuery(id+"F0.imprint","INTERSECT",VERTEX,{"derivedFrom":[subQ0,sQuery(id+"F0.wireOp",EDGE,"E12")]}),-1.0]])],"derivedFrom":subQ0})])]});Q36=qUnion([makeQuery(id+"F3.boolean.opBoolean","INTERSECT",EDGE,{"derivedFrom":[subQ5,makeQuery(id+"F3.opExtrude","SWEPT_FACE",FACE,{"disambiguationData":[OSD([sQuery(id+"F2.wireOp",EDGE,"E41.0")])]})]}),makeQuery(id+"F3.boolean.opBoolean","INTERSECT",EDGE,{"derivedFrom":[subQ5,makeQuery(id+"F3.opExtrude","SWEPT_FACE",FACE,{"disambiguationData":[OSD([sQuery(id+"F2.wireOp",EDGE,"E41.1")])]})]}),makeQuery(id+"F3.boolean.opBoolean","INTERSECT",EDGE,{"derivedFrom":[subQ5,makeQuery(id+"F3.opExtrude","SWEPT_FACE",FACE,{"disambiguationData":[OSD([sQuery(id+"F2.wireOp",EDGE,"E41.2")])]})]}),makeQuery(id+"F3.boolean.opBoolean","INTERSECT",EDGE,{"derivedFrom":[subQ5,makeQuery(id+"F3.opExtrude","SWEPT_FACE",FACE,{"disambiguationData":[OSD([sQuery(id+"F2.wireOp",EDGE,"E41.3")])]})]}),makeQuery(id+"F3.boolean.opBoolean","INTERSECT",EDGE,{"derivedFrom":[subQ5,makeQuery(id+"F3.opExtrude","SWEPT_FACE",FACE,{"disambiguationData":[OSD([sQuery(id+"F2.wireOp",EDGE,"E41.4")])]})]}),makeQuery(id+"F3.boolean.opBoolean","INTERSECT",EDGE,{"derivedFrom":[subQ5,makeQuery(id+"F3.opExtrude","SWEPT_FACE",FACE,{"disambiguationData":[OSD([sQuery(id+"F2.wireOp",EDGE,"E41.5")])]})]}),makeQuery(id+"F3.boolean.opBoolean","INTERSECT",EDGE,{"derivedFrom":[subQ5,makeQuery(id+"F3.opExtrude","SWEPT_FACE",FACE,{"disambiguationData":[OSD([sQuery(id+"F2.wireOp",EDGE,"E42.0")])]})]}),makeQuery(id+"F3.boolean.opBoolean","INTERSECT",EDGE,{"derivedFrom":[subQ5,makeQuery(id+"F3.opExtrude","SWEPT_FACE",FACE,{"disambiguationData":[OSD([sQuery(id+"F2.wireOp",EDGE,"E42.1")])]})]}),makeQuery(id+"F3.boolean.opBoolean","INTERSECT",EDGE,{"derivedFrom":[subQ5,makeQuery(id+"F3.opExtrude","SWEPT_FACE",FACE,{"disambiguationData":[OSD([sQuery(id+"F2.wireOp",EDGE,"E42.2")])]})]}),makeQuery(id+"F3.boolean.opBoolean","INTERSECT",EDGE,{"derivedFrom":[subQ5,makeQuery(id+"F3.opExtrude","SWEPT_FACE",FACE,{"disambiguationData":[OSD([sQuery(id+"F2.wireOp",EDGE,"E42.3")])]})]}),makeQuery(id+"F3.boolean.opBoolean","INTERSECT",EDGE,{"derivedFrom":[subQ5,makeQuery(id+"F3.opExtrude","SWEPT_FACE",FACE,{"disambiguationData":[OSD([sQuery(id+"F2.wireOp",EDGE,"E42.4")])]})]}),makeQuery(id+"F3.boolean.opBoolean","INTERSECT",EDGE,{"derivedFrom":[subQ5,makeQuery(id+"F3.opExtrude","SWEPT_FACE",FACE,{"disambiguationData":[OSD([sQuery(id+"F2.wireOp",EDGE,"E42.5")])]})]}),makeQuery(id+"F3.boolean.opBoolean","INTERSECT",EDGE,{"derivedFrom":[subQ4,makeQuery(id+"F3.opExtrude","SWEPT_FACE",FACE,{"disambiguationData":[OSD([sQuery(id+"F2.wireOp",EDGE,"E39.0")])]})]}),makeQuery(id+"F3.boolean.opBoolean","INTERSECT",EDGE,{"derivedFrom":[subQ4,makeQuery(id+"F3.opExtrude","SWEPT_FACE",FACE,{"disambiguationData":[OSD([sQuery(id+"F2.wireOp",EDGE,"E39.1")])]})]}),makeQuery(id+"F3.boolean.opBoolean","INTERSECT",EDGE,{"derivedFrom":[subQ4,makeQuery(id+"F3.opExtrude","SWEPT_FACE",FACE,{"disambiguationData":[OSD([sQuery(id+"F2.wireOp",EDGE,"E39.2")])]})]}),makeQuery(id+"F3.boolean.opBoolean","INTERSECT",EDGE,{"derivedFrom":[subQ4,makeQuery(id+"F3.opExtrude","SWEPT_FACE",FACE,{"disambiguationData":[OSD([sQuery(id+"F2.wireOp",EDGE,"E39.3")])]})]}),makeQuery(id+"F3.boolean.opBoolean","INTERSECT",EDGE,{"derivedFrom":[subQ4,makeQuery(id+"F3.opExtrude","SWEPT_FACE",FACE,{"disambiguationData":[OSD([sQuery(id+"F2.wireOp",EDGE,"E39.4")])]})]}),makeQuery(id+"F3.boolean.opBoolean","INTERSECT",EDGE,{"derivedFrom":[subQ4,makeQuery(id+"F3.opExtrude","SWEPT_FACE",FACE,{"disambiguationData":[OSD([sQuery(id+"F2.wireOp",EDGE,"E39.5")])]})]}),makeQuery(id+"F3.boolean.opBoolean","INTERSECT",EDGE,{"derivedFrom":[subQ4,makeQuery(id+"F3.opExtrude","SWEPT_FACE",FACE,{"disambiguationData":[OSD([sQuery(id+"F2.wireOp",EDGE,"E40.0")])]})]}),makeQuery(id+"F3.boolean.opBoolean","INTERSECT",EDGE,{"derivedFrom":[subQ4,makeQuery(id+"F3.opExtrude","SWEPT_FACE",FACE,{"disambiguationData":[OSD([sQuery(id+"F2.wireOp",EDGE,"E40.1")])]})]}),makeQuery(id+"F3.boolean.opBoolean","INTERSECT",EDGE,{"derivedFrom":[subQ4,makeQuery(id+"F3.opExtrude","SWEPT_FACE",FACE,{"disambiguationData":[OSD([sQuery(id+"F2.wireOp",EDGE,"E40.2")])]})]}),makeQuery(id+"F3.boolean.opBoolean","INTERSECT",EDGE,{"derivedFrom":[subQ4,makeQuery(id+"F3.opExtrude","SWEPT_FACE",FACE,{"disambiguationData":[OSD([sQuery(id+"F2.wireOp",EDGE,"E40.3")])]})]}),makeQuery(id+"F3.boolean.opBoolean","INTERSECT",EDGE,{"derivedFrom":[subQ4,makeQuery(id+"F3.opExtrude","SWEPT_FACE",FACE,{"disambiguationData":[OSD([sQuery(id+"F2.wireOp",EDGE,"E40.4")])]})]}),makeQuery(id+"F3.boolean.opBoolean","INTERSECT",EDGE,{"derivedFrom":[subQ4,makeQuery(id+"F3.opExtrude","SWEPT_FACE",FACE,{"disambiguationData":[OSD([sQuery(id+"F2.wireOp",EDGE,"E40.5")])]})]}),makeQuery(id+"F3.boolean.opBoolean","INTERSECT",EDGE,{"derivedFrom":[subQ2,makeQuery(id+"F3.opExtrude","SWEPT_FACE",FACE,{"disambiguationData":[OSD([sQuery(id+"F2.wireOp",EDGE,"E36.0")])]})]}),makeQuery(id+"F3.boolean.opBoolean","INTERSECT",EDGE,{"derivedFrom":[subQ2,makeQuery(id+"F3.opExtrude","SWEPT_FACE",FACE,{"disambiguationData":[OSD([sQuery(id+"F2.wireOp",EDGE,"E36.1")])]})]}),makeQuery(id+"F3.boolean.opBoolean","INTERSECT",EDGE,{"derivedFrom":[subQ2,makeQuery(id+"F3.opExtrude","SWEPT_FACE",FACE,{"disambiguationData":[OSD([sQuery(id+"F2.wireOp",EDGE,"E36.2")])]})]}),makeQuery(id+"F3.boolean.opBoolean","INTERSECT",EDGE,{"derivedFrom":[subQ2,makeQuery(id+"F3.opExtrude","SWEPT_FACE",FACE,{"disambiguationData":[OSD([sQuery(id+"F2.wireOp",EDGE,"E36.3")])]})]}),makeQuery(id+"F3.boolean.opBoolean","INTERSECT",EDGE,{"derivedFrom":[subQ2,makeQuery(id+"F3.opExtrude","SWEPT_FACE",FACE,{"disambiguationData":[OSD([sQuery(id+"F2.wireOp",EDGE,"E36.4")])]})]}),makeQuery(id+"F3.boolean.opBoolean","INTERSECT",EDGE,{"derivedFrom":[subQ2,makeQuery(id+"F3.opExtrude","SWEPT_FACE",FACE,{"disambiguationData":[OSD([sQuery(id+"F2.wireOp",EDGE,"E36.5")])]})]}),makeQuery(id+"F3.boolean.opBoolean","INTERSECT",EDGE,{"derivedFrom":[subQ2,makeQuery(id+"F3.opExtrude","SWEPT_FACE",FACE,{"disambiguationData":[OSD([sQuery(id+"F2.wireOp",EDGE,"E37.0")])]})]}),makeQuery(id+"F3.boolean.opBoolean","INTERSECT",EDGE,{"derivedFrom":[subQ2,makeQuery(id+"F3.opExtrude","SWEPT_FACE",FACE,{"disambiguationData":[OSD([sQuery(id+"F2.wireOp",EDGE,"E37.1")])]})]}),makeQuery(id+"F3.boolean.opBoolean","INTERSECT",EDGE,{"derivedFrom":[subQ2,makeQuery(id+"F3.opExtrude","SWEPT_FACE",FACE,{"disambiguationData":[OSD([sQuery(id+"F2.wireOp",EDGE,"E37.2")])]})]}),makeQuery(id+"F3.boolean.opBoolean","INTERSECT",EDGE,{"derivedFrom":[subQ2,makeQuery(id+"F3.opExtrude","SWEPT_FACE",FACE,{"disambiguationData":[OSD([sQuery(id+"F2.wireOp",EDGE,"E37.3")])]})]}),makeQuery(id+"F3.boolean.opBoolean","INTERSECT",EDGE,{"derivedFrom":[subQ2,makeQuery(id+"F3.opExtrude","SWEPT_FACE",FACE,{"disambiguationData":[OSD([sQuery(id+"F2.wireOp",EDGE,"E37.4")])]})]}),makeQuery(id+"F3.boolean.opBoolean","INTERSECT",EDGE,{"derivedFrom":[subQ2,makeQuery(id+"F3.opExtrude","SWEPT_FACE",FACE,{"disambiguationData":[OSD([sQuery(id+"F2.wireOp",EDGE,"E37.5")])]})]}),makeQuery(id+"F3.boolean.opBoolean","INTERSECT",EDGE,{"derivedFrom":[subQ2,makeQuery(id+"F3.opExtrude","SWEPT_FACE",FACE,{"disambiguationData":[OSD([sQuery(id+"F2.wireOp",EDGE,"E38.0")])]})]}),makeQuery(id+"F3.boolean.opBoolean","INTERSECT",EDGE,{"derivedFrom":[subQ2,makeQuery(id+"F3.opExtrude","SWEPT_FACE",FACE,{"disambiguationData":[OSD([sQuery(id+"F2.wireOp",EDGE,"E38.1")])]})]}),makeQuery(id+"F3.boolean.opBoolean","INTERSECT",EDGE,{"derivedFrom":[subQ2,makeQuery(id+"F3.opExtrude","SWEPT_FACE",FACE,{"disambiguationData":[OSD([sQuery(id+"F2.wireOp",EDGE,"E38.2")])]})]}),makeQuery(id+"F3.boolean.opBoolean","INTERSECT",EDGE,{"derivedFrom":[subQ2,makeQuery(id+"F3.opExtrude","SWEPT_FACE",FACE,{"disambiguationData":[OSD([sQuery(id+"F2.wireOp",EDGE,"E38.3")])]})]}),makeQuery(id+"F3.boolean.opBoolean","INTERSECT",EDGE,{"derivedFrom":[subQ2,makeQuery(id+"F3.opExtrude","SWEPT_FACE",FACE,{"disambiguationData":[OSD([sQuery(id+"F2.wireOp",EDGE,"E38.4")])]})]}),makeQuery(id+"F3.boolean.opBoolean","INTERSECT",EDGE,{"derivedFrom":[subQ2,makeQuery(id+"F3.opExtrude","SWEPT_FACE",FACE,{"disambiguationData":[OSD([sQuery(id+"F2.wireOp",EDGE,"E38.5")])]})]})]);}
            var Q37;
            {var subQ0=sQuery(id+"F0.wireOp",EDGE,"E6");var subQ1=sQuery(id+"F0.wireOp",EDGE,"E18.top");var subQ2=makeQuery(id+"F1.opExtrude","SWEPT_FACE",FACE,{"disambiguationData":[OSD([subQ0]),TDD([makeQuery(id+"F0.imprint","IMPRINT",EDGE,{"disambiguationData":[TD([[makeQuery(id+"F0.imprint","INTERSECT",VERTEX,{"derivedFrom":[subQ0,sQuery(id+"F0.wireOp",EDGE,"E9")]}),1.0]])],"derivedFrom":subQ0})])]});var subQ4=makeQuery(id+"F1.opExtrude","SWEPT_FACE",FACE,{"disambiguationData":[OSD([subQ0]),TDD([makeQuery(id+"F0.imprint","IMPRINT",EDGE,{"disambiguationData":[TD([[makeQuery(id+"F0.imprint","INTERSECT",VERTEX,{"derivedFrom":[subQ0,subQ1,sQuery(id+"F0.wireOp",EDGE,"E18.right")]}),1.0]])],"derivedFrom":subQ0})])]});var subQ5=makeQuery(id+"F1.opExtrude","SWEPT_FACE",FACE,{"disambiguationData":[OSD([subQ0]),TDD([makeQuery(id+"F0.imprint","IMPRINT",EDGE,{"disambiguationData":[TD([[makeQuery(id+"F0.imprint","INTERSECT",VERTEX,{"derivedFrom":[subQ0,sQuery(id+"F0.wireOp",EDGE,"E12")]}),-1.0]])],"derivedFrom":subQ0})])]});Q37=qUnion([makeQuery(id+"F3.boolean.opBoolean","INTERSECT",EDGE,{"derivedFrom":[subQ5,makeQuery(id+"F3.opExtrude","SWEPT_FACE",FACE,{"disambiguationData":[OSD([sQuery(id+"F2.wireOp",EDGE,"E41.0")])]})]}),makeQuery(id+"F3.boolean.opBoolean","INTERSECT",EDGE,{"derivedFrom":[subQ5,makeQuery(id+"F3.opExtrude","SWEPT_FACE",FACE,{"disambiguationData":[OSD([sQuery(id+"F2.wireOp",EDGE,"E41.1")])]})]}),makeQuery(id+"F3.boolean.opBoolean","INTERSECT",EDGE,{"derivedFrom":[subQ5,makeQuery(id+"F3.opExtrude","SWEPT_FACE",FACE,{"disambiguationData":[OSD([sQuery(id+"F2.wireOp",EDGE,"E41.2")])]})]}),makeQuery(id+"F3.boolean.opBoolean","INTERSECT",EDGE,{"derivedFrom":[subQ5,makeQuery(id+"F3.opExtrude","SWEPT_FACE",FACE,{"disambiguationData":[OSD([sQuery(id+"F2.wireOp",EDGE,"E41.3")])]})]}),makeQuery(id+"F3.boolean.opBoolean","INTERSECT",EDGE,{"derivedFrom":[subQ5,makeQuery(id+"F3.opExtrude","SWEPT_FACE",FACE,{"disambiguationData":[OSD([sQuery(id+"F2.wireOp",EDGE,"E41.4")])]})]}),makeQuery(id+"F3.boolean.opBoolean","INTERSECT",EDGE,{"derivedFrom":[subQ5,makeQuery(id+"F3.opExtrude","SWEPT_FACE",FACE,{"disambiguationData":[OSD([sQuery(id+"F2.wireOp",EDGE,"E41.5")])]})]}),makeQuery(id+"F3.boolean.opBoolean","INTERSECT",EDGE,{"derivedFrom":[subQ5,makeQuery(id+"F3.opExtrude","SWEPT_FACE",FACE,{"disambiguationData":[OSD([sQuery(id+"F2.wireOp",EDGE,"E42.0")])]})]}),makeQuery(id+"F3.boolean.opBoolean","INTERSECT",EDGE,{"derivedFrom":[subQ5,makeQuery(id+"F3.opExtrude","SWEPT_FACE",FACE,{"disambiguationData":[OSD([sQuery(id+"F2.wireOp",EDGE,"E42.1")])]})]}),makeQuery(id+"F3.boolean.opBoolean","INTERSECT",EDGE,{"derivedFrom":[subQ5,makeQuery(id+"F3.opExtrude","SWEPT_FACE",FACE,{"disambiguationData":[OSD([sQuery(id+"F2.wireOp",EDGE,"E42.2")])]})]}),makeQuery(id+"F3.boolean.opBoolean","INTERSECT",EDGE,{"derivedFrom":[subQ5,makeQuery(id+"F3.opExtrude","SWEPT_FACE",FACE,{"disambiguationData":[OSD([sQuery(id+"F2.wireOp",EDGE,"E42.3")])]})]}),makeQuery(id+"F3.boolean.opBoolean","INTERSECT",EDGE,{"derivedFrom":[subQ5,makeQuery(id+"F3.opExtrude","SWEPT_FACE",FACE,{"disambiguationData":[OSD([sQuery(id+"F2.wireOp",EDGE,"E42.4")])]})]}),makeQuery(id+"F3.boolean.opBoolean","INTERSECT",EDGE,{"derivedFrom":[subQ5,makeQuery(id+"F3.opExtrude","SWEPT_FACE",FACE,{"disambiguationData":[OSD([sQuery(id+"F2.wireOp",EDGE,"E42.5")])]})]}),makeQuery(id+"F3.boolean.opBoolean","INTERSECT",EDGE,{"derivedFrom":[subQ4,makeQuery(id+"F3.opExtrude","SWEPT_FACE",FACE,{"disambiguationData":[OSD([sQuery(id+"F2.wireOp",EDGE,"E39.0")])]})]}),makeQuery(id+"F3.boolean.opBoolean","INTERSECT",EDGE,{"derivedFrom":[subQ4,makeQuery(id+"F3.opExtrude","SWEPT_FACE",FACE,{"disambiguationData":[OSD([sQuery(id+"F2.wireOp",EDGE,"E39.1")])]})]}),makeQuery(id+"F3.boolean.opBoolean","INTERSECT",EDGE,{"derivedFrom":[subQ4,makeQuery(id+"F3.opExtrude","SWEPT_FACE",FACE,{"disambiguationData":[OSD([sQuery(id+"F2.wireOp",EDGE,"E39.2")])]})]}),makeQuery(id+"F3.boolean.opBoolean","INTERSECT",EDGE,{"derivedFrom":[subQ4,makeQuery(id+"F3.opExtrude","SWEPT_FACE",FACE,{"disambiguationData":[OSD([sQuery(id+"F2.wireOp",EDGE,"E39.3")])]})]}),makeQuery(id+"F3.boolean.opBoolean","INTERSECT",EDGE,{"derivedFrom":[subQ4,makeQuery(id+"F3.opExtrude","SWEPT_FACE",FACE,{"disambiguationData":[OSD([sQuery(id+"F2.wireOp",EDGE,"E39.4")])]})]}),makeQuery(id+"F3.boolean.opBoolean","INTERSECT",EDGE,{"derivedFrom":[subQ4,makeQuery(id+"F3.opExtrude","SWEPT_FACE",FACE,{"disambiguationData":[OSD([sQuery(id+"F2.wireOp",EDGE,"E39.5")])]})]}),makeQuery(id+"F3.boolean.opBoolean","INTERSECT",EDGE,{"derivedFrom":[subQ4,makeQuery(id+"F3.opExtrude","SWEPT_FACE",FACE,{"disambiguationData":[OSD([sQuery(id+"F2.wireOp",EDGE,"E40.0")])]})]}),makeQuery(id+"F3.boolean.opBoolean","INTERSECT",EDGE,{"derivedFrom":[subQ4,makeQuery(id+"F3.opExtrude","SWEPT_FACE",FACE,{"disambiguationData":[OSD([sQuery(id+"F2.wireOp",EDGE,"E40.1")])]})]}),makeQuery(id+"F3.boolean.opBoolean","INTERSECT",EDGE,{"derivedFrom":[subQ4,makeQuery(id+"F3.opExtrude","SWEPT_FACE",FACE,{"disambiguationData":[OSD([sQuery(id+"F2.wireOp",EDGE,"E40.2")])]})]}),makeQuery(id+"F3.boolean.opBoolean","INTERSECT",EDGE,{"derivedFrom":[subQ4,makeQuery(id+"F3.opExtrude","SWEPT_FACE",FACE,{"disambiguationData":[OSD([sQuery(id+"F2.wireOp",EDGE,"E40.3")])]})]}),makeQuery(id+"F3.boolean.opBoolean","INTERSECT",EDGE,{"derivedFrom":[subQ4,makeQuery(id+"F3.opExtrude","SWEPT_FACE",FACE,{"disambiguationData":[OSD([sQuery(id+"F2.wireOp",EDGE,"E40.4")])]})]}),makeQuery(id+"F3.boolean.opBoolean","INTERSECT",EDGE,{"derivedFrom":[subQ4,makeQuery(id+"F3.opExtrude","SWEPT_FACE",FACE,{"disambiguationData":[OSD([sQuery(id+"F2.wireOp",EDGE,"E40.5")])]})]}),makeQuery(id+"F3.boolean.opBoolean","INTERSECT",EDGE,{"derivedFrom":[subQ2,makeQuery(id+"F3.opExtrude","SWEPT_FACE",FACE,{"disambiguationData":[OSD([sQuery(id+"F2.wireOp",EDGE,"E36.0")])]})]}),makeQuery(id+"F3.boolean.opBoolean","INTERSECT",EDGE,{"derivedFrom":[subQ2,makeQuery(id+"F3.opExtrude","SWEPT_FACE",FACE,{"disambiguationData":[OSD([sQuery(id+"F2.wireOp",EDGE,"E36.1")])]})]}),makeQuery(id+"F3.boolean.opBoolean","INTERSECT",EDGE,{"derivedFrom":[subQ2,makeQuery(id+"F3.opExtrude","SWEPT_FACE",FACE,{"disambiguationData":[OSD([sQuery(id+"F2.wireOp",EDGE,"E36.2")])]})]}),makeQuery(id+"F3.boolean.opBoolean","INTERSECT",EDGE,{"derivedFrom":[subQ2,makeQuery(id+"F3.opExtrude","SWEPT_FACE",FACE,{"disambiguationData":[OSD([sQuery(id+"F2.wireOp",EDGE,"E36.3")])]})]}),makeQuery(id+"F3.boolean.opBoolean","INTERSECT",EDGE,{"derivedFrom":[subQ2,makeQuery(id+"F3.opExtrude","SWEPT_FACE",FACE,{"disambiguationData":[OSD([sQuery(id+"F2.wireOp",EDGE,"E36.4")])]})]}),makeQuery(id+"F3.boolean.opBoolean","INTERSECT",EDGE,{"derivedFrom":[subQ2,makeQuery(id+"F3.opExtrude","SWEPT_FACE",FACE,{"disambiguationData":[OSD([sQuery(id+"F2.wireOp",EDGE,"E36.5")])]})]}),makeQuery(id+"F3.boolean.opBoolean","INTERSECT",EDGE,{"derivedFrom":[subQ2,makeQuery(id+"F3.opExtrude","SWEPT_FACE",FACE,{"disambiguationData":[OSD([sQuery(id+"F2.wireOp",EDGE,"E37.0")])]})]}),makeQuery(id+"F3.boolean.opBoolean","INTERSECT",EDGE,{"derivedFrom":[subQ2,makeQuery(id+"F3.opExtrude","SWEPT_FACE",FACE,{"disambiguationData":[OSD([sQuery(id+"F2.wireOp",EDGE,"E37.1")])]})]}),makeQuery(id+"F3.boolean.opBoolean","INTERSECT",EDGE,{"derivedFrom":[subQ2,makeQuery(id+"F3.opExtrude","SWEPT_FACE",FACE,{"disambiguationData":[OSD([sQuery(id+"F2.wireOp",EDGE,"E37.2")])]})]}),makeQuery(id+"F3.boolean.opBoolean","INTERSECT",EDGE,{"derivedFrom":[subQ2,makeQuery(id+"F3.opExtrude","SWEPT_FACE",FACE,{"disambiguationData":[OSD([sQuery(id+"F2.wireOp",EDGE,"E37.3")])]})]}),makeQuery(id+"F3.boolean.opBoolean","INTERSECT",EDGE,{"derivedFrom":[subQ2,makeQuery(id+"F3.opExtrude","SWEPT_FACE",FACE,{"disambiguationData":[OSD([sQuery(id+"F2.wireOp",EDGE,"E37.4")])]})]}),makeQuery(id+"F3.boolean.opBoolean","INTERSECT",EDGE,{"derivedFrom":[subQ2,makeQuery(id+"F3.opExtrude","SWEPT_FACE",FACE,{"disambiguationData":[OSD([sQuery(id+"F2.wireOp",EDGE,"E37.5")])]})]}),makeQuery(id+"F3.boolean.opBoolean","INTERSECT",EDGE,{"derivedFrom":[subQ2,makeQuery(id+"F3.opExtrude","SWEPT_FACE",FACE,{"disambiguationData":[OSD([sQuery(id+"F2.wireOp",EDGE,"E38.0")])]})]}),makeQuery(id+"F3.boolean.opBoolean","INTERSECT",EDGE,{"derivedFrom":[subQ2,makeQuery(id+"F3.opExtrude","SWEPT_FACE",FACE,{"disambiguationData":[OSD([sQuery(id+"F2.wireOp",EDGE,"E38.1")])]})]}),makeQuery(id+"F3.boolean.opBoolean","INTERSECT",EDGE,{"derivedFrom":[subQ2,makeQuery(id+"F3.opExtrude","SWEPT_FACE",FACE,{"disambiguationData":[OSD([sQuery(id+"F2.wireOp",EDGE,"E38.2")])]})]}),makeQuery(id+"F3.boolean.opBoolean","INTERSECT",EDGE,{"derivedFrom":[subQ2,makeQuery(id+"F3.opExtrude","SWEPT_FACE",FACE,{"disambiguationData":[OSD([sQuery(id+"F2.wireOp",EDGE,"E38.3")])]})]}),makeQuery(id+"F3.boolean.opBoolean","INTERSECT",EDGE,{"derivedFrom":[subQ2,makeQuery(id+"F3.opExtrude","SWEPT_FACE",FACE,{"disambiguationData":[OSD([sQuery(id+"F2.wireOp",EDGE,"E38.4")])]})]}),makeQuery(id+"F3.boolean.opBoolean","INTERSECT",EDGE,{"derivedFrom":[subQ2,makeQuery(id+"F3.opExtrude","SWEPT_FACE",FACE,{"disambiguationData":[OSD([sQuery(id+"F2.wireOp",EDGE,"E38.5")])]})]})]);}
            var Q38;
            {var subQ0=sQuery(id+"F0.wireOp",EDGE,"E6");var subQ1=sQuery(id+"F0.wireOp",EDGE,"E18.top");var subQ2=makeQuery(id+"F1.opExtrude","SWEPT_FACE",FACE,{"disambiguationData":[OSD([subQ0]),TDD([makeQuery(id+"F0.imprint","IMPRINT",EDGE,{"disambiguationData":[TD([[makeQuery(id+"F0.imprint","INTERSECT",VERTEX,{"derivedFrom":[subQ0,sQuery(id+"F0.wireOp",EDGE,"E9")]}),1.0]])],"derivedFrom":subQ0})])]});var subQ4=makeQuery(id+"F1.opExtrude","SWEPT_FACE",FACE,{"disambiguationData":[OSD([subQ0]),TDD([makeQuery(id+"F0.imprint","IMPRINT",EDGE,{"disambiguationData":[TD([[makeQuery(id+"F0.imprint","INTERSECT",VERTEX,{"derivedFrom":[subQ0,subQ1,sQuery(id+"F0.wireOp",EDGE,"E18.right")]}),1.0]])],"derivedFrom":subQ0})])]});var subQ5=makeQuery(id+"F1.opExtrude","SWEPT_FACE",FACE,{"disambiguationData":[OSD([subQ0]),TDD([makeQuery(id+"F0.imprint","IMPRINT",EDGE,{"disambiguationData":[TD([[makeQuery(id+"F0.imprint","INTERSECT",VERTEX,{"derivedFrom":[subQ0,sQuery(id+"F0.wireOp",EDGE,"E12")]}),-1.0]])],"derivedFrom":subQ0})])]});Q38=qUnion([makeQuery(id+"F3.boolean.opBoolean","INTERSECT",EDGE,{"derivedFrom":[subQ5,makeQuery(id+"F3.opExtrude","SWEPT_FACE",FACE,{"disambiguationData":[OSD([sQuery(id+"F2.wireOp",EDGE,"E41.0")])]})]}),makeQuery(id+"F3.boolean.opBoolean","INTERSECT",EDGE,{"derivedFrom":[subQ5,makeQuery(id+"F3.opExtrude","SWEPT_FACE",FACE,{"disambiguationData":[OSD([sQuery(id+"F2.wireOp",EDGE,"E41.1")])]})]}),makeQuery(id+"F3.boolean.opBoolean","INTERSECT",EDGE,{"derivedFrom":[subQ5,makeQuery(id+"F3.opExtrude","SWEPT_FACE",FACE,{"disambiguationData":[OSD([sQuery(id+"F2.wireOp",EDGE,"E41.2")])]})]}),makeQuery(id+"F3.boolean.opBoolean","INTERSECT",EDGE,{"derivedFrom":[subQ5,makeQuery(id+"F3.opExtrude","SWEPT_FACE",FACE,{"disambiguationData":[OSD([sQuery(id+"F2.wireOp",EDGE,"E41.3")])]})]}),makeQuery(id+"F3.boolean.opBoolean","INTERSECT",EDGE,{"derivedFrom":[subQ5,makeQuery(id+"F3.opExtrude","SWEPT_FACE",FACE,{"disambiguationData":[OSD([sQuery(id+"F2.wireOp",EDGE,"E41.4")])]})]}),makeQuery(id+"F3.boolean.opBoolean","INTERSECT",EDGE,{"derivedFrom":[subQ5,makeQuery(id+"F3.opExtrude","SWEPT_FACE",FACE,{"disambiguationData":[OSD([sQuery(id+"F2.wireOp",EDGE,"E41.5")])]})]}),makeQuery(id+"F3.boolean.opBoolean","INTERSECT",EDGE,{"derivedFrom":[subQ5,makeQuery(id+"F3.opExtrude","SWEPT_FACE",FACE,{"disambiguationData":[OSD([sQuery(id+"F2.wireOp",EDGE,"E42.0")])]})]}),makeQuery(id+"F3.boolean.opBoolean","INTERSECT",EDGE,{"derivedFrom":[subQ5,makeQuery(id+"F3.opExtrude","SWEPT_FACE",FACE,{"disambiguationData":[OSD([sQuery(id+"F2.wireOp",EDGE,"E42.1")])]})]}),makeQuery(id+"F3.boolean.opBoolean","INTERSECT",EDGE,{"derivedFrom":[subQ5,makeQuery(id+"F3.opExtrude","SWEPT_FACE",FACE,{"disambiguationData":[OSD([sQuery(id+"F2.wireOp",EDGE,"E42.2")])]})]}),makeQuery(id+"F3.boolean.opBoolean","INTERSECT",EDGE,{"derivedFrom":[subQ5,makeQuery(id+"F3.opExtrude","SWEPT_FACE",FACE,{"disambiguationData":[OSD([sQuery(id+"F2.wireOp",EDGE,"E42.3")])]})]}),makeQuery(id+"F3.boolean.opBoolean","INTERSECT",EDGE,{"derivedFrom":[subQ5,makeQuery(id+"F3.opExtrude","SWEPT_FACE",FACE,{"disambiguationData":[OSD([sQuery(id+"F2.wireOp",EDGE,"E42.4")])]})]}),makeQuery(id+"F3.boolean.opBoolean","INTERSECT",EDGE,{"derivedFrom":[subQ5,makeQuery(id+"F3.opExtrude","SWEPT_FACE",FACE,{"disambiguationData":[OSD([sQuery(id+"F2.wireOp",EDGE,"E42.5")])]})]}),makeQuery(id+"F3.boolean.opBoolean","INTERSECT",EDGE,{"derivedFrom":[subQ4,makeQuery(id+"F3.opExtrude","SWEPT_FACE",FACE,{"disambiguationData":[OSD([sQuery(id+"F2.wireOp",EDGE,"E39.0")])]})]}),makeQuery(id+"F3.boolean.opBoolean","INTERSECT",EDGE,{"derivedFrom":[subQ4,makeQuery(id+"F3.opExtrude","SWEPT_FACE",FACE,{"disambiguationData":[OSD([sQuery(id+"F2.wireOp",EDGE,"E39.1")])]})]}),makeQuery(id+"F3.boolean.opBoolean","INTERSECT",EDGE,{"derivedFrom":[subQ4,makeQuery(id+"F3.opExtrude","SWEPT_FACE",FACE,{"disambiguationData":[OSD([sQuery(id+"F2.wireOp",EDGE,"E39.2")])]})]}),makeQuery(id+"F3.boolean.opBoolean","INTERSECT",EDGE,{"derivedFrom":[subQ4,makeQuery(id+"F3.opExtrude","SWEPT_FACE",FACE,{"disambiguationData":[OSD([sQuery(id+"F2.wireOp",EDGE,"E39.3")])]})]}),makeQuery(id+"F3.boolean.opBoolean","INTERSECT",EDGE,{"derivedFrom":[subQ4,makeQuery(id+"F3.opExtrude","SWEPT_FACE",FACE,{"disambiguationData":[OSD([sQuery(id+"F2.wireOp",EDGE,"E39.4")])]})]}),makeQuery(id+"F3.boolean.opBoolean","INTERSECT",EDGE,{"derivedFrom":[subQ4,makeQuery(id+"F3.opExtrude","SWEPT_FACE",FACE,{"disambiguationData":[OSD([sQuery(id+"F2.wireOp",EDGE,"E39.5")])]})]}),makeQuery(id+"F3.boolean.opBoolean","INTERSECT",EDGE,{"derivedFrom":[subQ4,makeQuery(id+"F3.opExtrude","SWEPT_FACE",FACE,{"disambiguationData":[OSD([sQuery(id+"F2.wireOp",EDGE,"E40.0")])]})]}),makeQuery(id+"F3.boolean.opBoolean","INTERSECT",EDGE,{"derivedFrom":[subQ4,makeQuery(id+"F3.opExtrude","SWEPT_FACE",FACE,{"disambiguationData":[OSD([sQuery(id+"F2.wireOp",EDGE,"E40.1")])]})]}),makeQuery(id+"F3.boolean.opBoolean","INTERSECT",EDGE,{"derivedFrom":[subQ4,makeQuery(id+"F3.opExtrude","SWEPT_FACE",FACE,{"disambiguationData":[OSD([sQuery(id+"F2.wireOp",EDGE,"E40.2")])]})]}),makeQuery(id+"F3.boolean.opBoolean","INTERSECT",EDGE,{"derivedFrom":[subQ4,makeQuery(id+"F3.opExtrude","SWEPT_FACE",FACE,{"disambiguationData":[OSD([sQuery(id+"F2.wireOp",EDGE,"E40.3")])]})]}),makeQuery(id+"F3.boolean.opBoolean","INTERSECT",EDGE,{"derivedFrom":[subQ4,makeQuery(id+"F3.opExtrude","SWEPT_FACE",FACE,{"disambiguationData":[OSD([sQuery(id+"F2.wireOp",EDGE,"E40.4")])]})]}),makeQuery(id+"F3.boolean.opBoolean","INTERSECT",EDGE,{"derivedFrom":[subQ4,makeQuery(id+"F3.opExtrude","SWEPT_FACE",FACE,{"disambiguationData":[OSD([sQuery(id+"F2.wireOp",EDGE,"E40.5")])]})]}),makeQuery(id+"F3.boolean.opBoolean","INTERSECT",EDGE,{"derivedFrom":[subQ2,makeQuery(id+"F3.opExtrude","SWEPT_FACE",FACE,{"disambiguationData":[OSD([sQuery(id+"F2.wireOp",EDGE,"E36.0")])]})]}),makeQuery(id+"F3.boolean.opBoolean","INTERSECT",EDGE,{"derivedFrom":[subQ2,makeQuery(id+"F3.opExtrude","SWEPT_FACE",FACE,{"disambiguationData":[OSD([sQuery(id+"F2.wireOp",EDGE,"E36.1")])]})]}),makeQuery(id+"F3.boolean.opBoolean","INTERSECT",EDGE,{"derivedFrom":[subQ2,makeQuery(id+"F3.opExtrude","SWEPT_FACE",FACE,{"disambiguationData":[OSD([sQuery(id+"F2.wireOp",EDGE,"E36.2")])]})]}),makeQuery(id+"F3.boolean.opBoolean","INTERSECT",EDGE,{"derivedFrom":[subQ2,makeQuery(id+"F3.opExtrude","SWEPT_FACE",FACE,{"disambiguationData":[OSD([sQuery(id+"F2.wireOp",EDGE,"E36.3")])]})]}),makeQuery(id+"F3.boolean.opBoolean","INTERSECT",EDGE,{"derivedFrom":[subQ2,makeQuery(id+"F3.opExtrude","SWEPT_FACE",FACE,{"disambiguationData":[OSD([sQuery(id+"F2.wireOp",EDGE,"E36.4")])]})]}),makeQuery(id+"F3.boolean.opBoolean","INTERSECT",EDGE,{"derivedFrom":[subQ2,makeQuery(id+"F3.opExtrude","SWEPT_FACE",FACE,{"disambiguationData":[OSD([sQuery(id+"F2.wireOp",EDGE,"E36.5")])]})]}),makeQuery(id+"F3.boolean.opBoolean","INTERSECT",EDGE,{"derivedFrom":[subQ2,makeQuery(id+"F3.opExtrude","SWEPT_FACE",FACE,{"disambiguationData":[OSD([sQuery(id+"F2.wireOp",EDGE,"E37.0")])]})]}),makeQuery(id+"F3.boolean.opBoolean","INTERSECT",EDGE,{"derivedFrom":[subQ2,makeQuery(id+"F3.opExtrude","SWEPT_FACE",FACE,{"disambiguationData":[OSD([sQuery(id+"F2.wireOp",EDGE,"E37.1")])]})]}),makeQuery(id+"F3.boolean.opBoolean","INTERSECT",EDGE,{"derivedFrom":[subQ2,makeQuery(id+"F3.opExtrude","SWEPT_FACE",FACE,{"disambiguationData":[OSD([sQuery(id+"F2.wireOp",EDGE,"E37.2")])]})]}),makeQuery(id+"F3.boolean.opBoolean","INTERSECT",EDGE,{"derivedFrom":[subQ2,makeQuery(id+"F3.opExtrude","SWEPT_FACE",FACE,{"disambiguationData":[OSD([sQuery(id+"F2.wireOp",EDGE,"E37.3")])]})]}),makeQuery(id+"F3.boolean.opBoolean","INTERSECT",EDGE,{"derivedFrom":[subQ2,makeQuery(id+"F3.opExtrude","SWEPT_FACE",FACE,{"disambiguationData":[OSD([sQuery(id+"F2.wireOp",EDGE,"E37.4")])]})]}),makeQuery(id+"F3.boolean.opBoolean","INTERSECT",EDGE,{"derivedFrom":[subQ2,makeQuery(id+"F3.opExtrude","SWEPT_FACE",FACE,{"disambiguationData":[OSD([sQuery(id+"F2.wireOp",EDGE,"E37.5")])]})]}),makeQuery(id+"F3.boolean.opBoolean","INTERSECT",EDGE,{"derivedFrom":[subQ2,makeQuery(id+"F3.opExtrude","SWEPT_FACE",FACE,{"disambiguationData":[OSD([sQuery(id+"F2.wireOp",EDGE,"E38.0")])]})]}),makeQuery(id+"F3.boolean.opBoolean","INTERSECT",EDGE,{"derivedFrom":[subQ2,makeQuery(id+"F3.opExtrude","SWEPT_FACE",FACE,{"disambiguationData":[OSD([sQuery(id+"F2.wireOp",EDGE,"E38.1")])]})]}),makeQuery(id+"F3.boolean.opBoolean","INTERSECT",EDGE,{"derivedFrom":[subQ2,makeQuery(id+"F3.opExtrude","SWEPT_FACE",FACE,{"disambiguationData":[OSD([sQuery(id+"F2.wireOp",EDGE,"E38.2")])]})]}),makeQuery(id+"F3.boolean.opBoolean","INTERSECT",EDGE,{"derivedFrom":[subQ2,makeQuery(id+"F3.opExtrude","SWEPT_FACE",FACE,{"disambiguationData":[OSD([sQuery(id+"F2.wireOp",EDGE,"E38.3")])]})]}),makeQuery(id+"F3.boolean.opBoolean","INTERSECT",EDGE,{"derivedFrom":[subQ2,makeQuery(id+"F3.opExtrude","SWEPT_FACE",FACE,{"disambiguationData":[OSD([sQuery(id+"F2.wireOp",EDGE,"E38.4")])]})]}),makeQuery(id+"F3.boolean.opBoolean","INTERSECT",EDGE,{"derivedFrom":[subQ2,makeQuery(id+"F3.opExtrude","SWEPT_FACE",FACE,{"disambiguationData":[OSD([sQuery(id+"F2.wireOp",EDGE,"E38.5")])]})]})]);}
            var Q39;
            {var subQ0=sQuery(id+"F0.wireOp",EDGE,"E6");var subQ1=sQuery(id+"F0.wireOp",EDGE,"E18.top");var subQ2=makeQuery(id+"F1.opExtrude","SWEPT_FACE",FACE,{"disambiguationData":[OSD([subQ0]),TDD([makeQuery(id+"F0.imprint","IMPRINT",EDGE,{"disambiguationData":[TD([[makeQuery(id+"F0.imprint","INTERSECT",VERTEX,{"derivedFrom":[subQ0,sQuery(id+"F0.wireOp",EDGE,"E9")]}),1.0]])],"derivedFrom":subQ0})])]});var subQ4=makeQuery(id+"F1.opExtrude","SWEPT_FACE",FACE,{"disambiguationData":[OSD([subQ0]),TDD([makeQuery(id+"F0.imprint","IMPRINT",EDGE,{"disambiguationData":[TD([[makeQuery(id+"F0.imprint","INTERSECT",VERTEX,{"derivedFrom":[subQ0,subQ1,sQuery(id+"F0.wireOp",EDGE,"E18.right")]}),1.0]])],"derivedFrom":subQ0})])]});var subQ5=makeQuery(id+"F1.opExtrude","SWEPT_FACE",FACE,{"disambiguationData":[OSD([subQ0]),TDD([makeQuery(id+"F0.imprint","IMPRINT",EDGE,{"disambiguationData":[TD([[makeQuery(id+"F0.imprint","INTERSECT",VERTEX,{"derivedFrom":[subQ0,sQuery(id+"F0.wireOp",EDGE,"E12")]}),-1.0]])],"derivedFrom":subQ0})])]});Q39=qUnion([makeQuery(id+"F3.boolean.opBoolean","INTERSECT",EDGE,{"derivedFrom":[subQ5,makeQuery(id+"F3.opExtrude","SWEPT_FACE",FACE,{"disambiguationData":[OSD([sQuery(id+"F2.wireOp",EDGE,"E41.0")])]})]}),makeQuery(id+"F3.boolean.opBoolean","INTERSECT",EDGE,{"derivedFrom":[subQ5,makeQuery(id+"F3.opExtrude","SWEPT_FACE",FACE,{"disambiguationData":[OSD([sQuery(id+"F2.wireOp",EDGE,"E41.1")])]})]}),makeQuery(id+"F3.boolean.opBoolean","INTERSECT",EDGE,{"derivedFrom":[subQ5,makeQuery(id+"F3.opExtrude","SWEPT_FACE",FACE,{"disambiguationData":[OSD([sQuery(id+"F2.wireOp",EDGE,"E41.2")])]})]}),makeQuery(id+"F3.boolean.opBoolean","INTERSECT",EDGE,{"derivedFrom":[subQ5,makeQuery(id+"F3.opExtrude","SWEPT_FACE",FACE,{"disambiguationData":[OSD([sQuery(id+"F2.wireOp",EDGE,"E41.3")])]})]}),makeQuery(id+"F3.boolean.opBoolean","INTERSECT",EDGE,{"derivedFrom":[subQ5,makeQuery(id+"F3.opExtrude","SWEPT_FACE",FACE,{"disambiguationData":[OSD([sQuery(id+"F2.wireOp",EDGE,"E41.4")])]})]}),makeQuery(id+"F3.boolean.opBoolean","INTERSECT",EDGE,{"derivedFrom":[subQ5,makeQuery(id+"F3.opExtrude","SWEPT_FACE",FACE,{"disambiguationData":[OSD([sQuery(id+"F2.wireOp",EDGE,"E41.5")])]})]}),makeQuery(id+"F3.boolean.opBoolean","INTERSECT",EDGE,{"derivedFrom":[subQ5,makeQuery(id+"F3.opExtrude","SWEPT_FACE",FACE,{"disambiguationData":[OSD([sQuery(id+"F2.wireOp",EDGE,"E42.0")])]})]}),makeQuery(id+"F3.boolean.opBoolean","INTERSECT",EDGE,{"derivedFrom":[subQ5,makeQuery(id+"F3.opExtrude","SWEPT_FACE",FACE,{"disambiguationData":[OSD([sQuery(id+"F2.wireOp",EDGE,"E42.1")])]})]}),makeQuery(id+"F3.boolean.opBoolean","INTERSECT",EDGE,{"derivedFrom":[subQ5,makeQuery(id+"F3.opExtrude","SWEPT_FACE",FACE,{"disambiguationData":[OSD([sQuery(id+"F2.wireOp",EDGE,"E42.2")])]})]}),makeQuery(id+"F3.boolean.opBoolean","INTERSECT",EDGE,{"derivedFrom":[subQ5,makeQuery(id+"F3.opExtrude","SWEPT_FACE",FACE,{"disambiguationData":[OSD([sQuery(id+"F2.wireOp",EDGE,"E42.3")])]})]}),makeQuery(id+"F3.boolean.opBoolean","INTERSECT",EDGE,{"derivedFrom":[subQ5,makeQuery(id+"F3.opExtrude","SWEPT_FACE",FACE,{"disambiguationData":[OSD([sQuery(id+"F2.wireOp",EDGE,"E42.4")])]})]}),makeQuery(id+"F3.boolean.opBoolean","INTERSECT",EDGE,{"derivedFrom":[subQ5,makeQuery(id+"F3.opExtrude","SWEPT_FACE",FACE,{"disambiguationData":[OSD([sQuery(id+"F2.wireOp",EDGE,"E42.5")])]})]}),makeQuery(id+"F3.boolean.opBoolean","INTERSECT",EDGE,{"derivedFrom":[subQ4,makeQuery(id+"F3.opExtrude","SWEPT_FACE",FACE,{"disambiguationData":[OSD([sQuery(id+"F2.wireOp",EDGE,"E39.0")])]})]}),makeQuery(id+"F3.boolean.opBoolean","INTERSECT",EDGE,{"derivedFrom":[subQ4,makeQuery(id+"F3.opExtrude","SWEPT_FACE",FACE,{"disambiguationData":[OSD([sQuery(id+"F2.wireOp",EDGE,"E39.1")])]})]}),makeQuery(id+"F3.boolean.opBoolean","INTERSECT",EDGE,{"derivedFrom":[subQ4,makeQuery(id+"F3.opExtrude","SWEPT_FACE",FACE,{"disambiguationData":[OSD([sQuery(id+"F2.wireOp",EDGE,"E39.2")])]})]}),makeQuery(id+"F3.boolean.opBoolean","INTERSECT",EDGE,{"derivedFrom":[subQ4,makeQuery(id+"F3.opExtrude","SWEPT_FACE",FACE,{"disambiguationData":[OSD([sQuery(id+"F2.wireOp",EDGE,"E39.3")])]})]}),makeQuery(id+"F3.boolean.opBoolean","INTERSECT",EDGE,{"derivedFrom":[subQ4,makeQuery(id+"F3.opExtrude","SWEPT_FACE",FACE,{"disambiguationData":[OSD([sQuery(id+"F2.wireOp",EDGE,"E39.4")])]})]}),makeQuery(id+"F3.boolean.opBoolean","INTERSECT",EDGE,{"derivedFrom":[subQ4,makeQuery(id+"F3.opExtrude","SWEPT_FACE",FACE,{"disambiguationData":[OSD([sQuery(id+"F2.wireOp",EDGE,"E39.5")])]})]}),makeQuery(id+"F3.boolean.opBoolean","INTERSECT",EDGE,{"derivedFrom":[subQ4,makeQuery(id+"F3.opExtrude","SWEPT_FACE",FACE,{"disambiguationData":[OSD([sQuery(id+"F2.wireOp",EDGE,"E40.0")])]})]}),makeQuery(id+"F3.boolean.opBoolean","INTERSECT",EDGE,{"derivedFrom":[subQ4,makeQuery(id+"F3.opExtrude","SWEPT_FACE",FACE,{"disambiguationData":[OSD([sQuery(id+"F2.wireOp",EDGE,"E40.1")])]})]}),makeQuery(id+"F3.boolean.opBoolean","INTERSECT",EDGE,{"derivedFrom":[subQ4,makeQuery(id+"F3.opExtrude","SWEPT_FACE",FACE,{"disambiguationData":[OSD([sQuery(id+"F2.wireOp",EDGE,"E40.2")])]})]}),makeQuery(id+"F3.boolean.opBoolean","INTERSECT",EDGE,{"derivedFrom":[subQ4,makeQuery(id+"F3.opExtrude","SWEPT_FACE",FACE,{"disambiguationData":[OSD([sQuery(id+"F2.wireOp",EDGE,"E40.3")])]})]}),makeQuery(id+"F3.boolean.opBoolean","INTERSECT",EDGE,{"derivedFrom":[subQ4,makeQuery(id+"F3.opExtrude","SWEPT_FACE",FACE,{"disambiguationData":[OSD([sQuery(id+"F2.wireOp",EDGE,"E40.4")])]})]}),makeQuery(id+"F3.boolean.opBoolean","INTERSECT",EDGE,{"derivedFrom":[subQ4,makeQuery(id+"F3.opExtrude","SWEPT_FACE",FACE,{"disambiguationData":[OSD([sQuery(id+"F2.wireOp",EDGE,"E40.5")])]})]}),makeQuery(id+"F3.boolean.opBoolean","INTERSECT",EDGE,{"derivedFrom":[subQ2,makeQuery(id+"F3.opExtrude","SWEPT_FACE",FACE,{"disambiguationData":[OSD([sQuery(id+"F2.wireOp",EDGE,"E36.0")])]})]}),makeQuery(id+"F3.boolean.opBoolean","INTERSECT",EDGE,{"derivedFrom":[subQ2,makeQuery(id+"F3.opExtrude","SWEPT_FACE",FACE,{"disambiguationData":[OSD([sQuery(id+"F2.wireOp",EDGE,"E36.1")])]})]}),makeQuery(id+"F3.boolean.opBoolean","INTERSECT",EDGE,{"derivedFrom":[subQ2,makeQuery(id+"F3.opExtrude","SWEPT_FACE",FACE,{"disambiguationData":[OSD([sQuery(id+"F2.wireOp",EDGE,"E36.2")])]})]}),makeQuery(id+"F3.boolean.opBoolean","INTERSECT",EDGE,{"derivedFrom":[subQ2,makeQuery(id+"F3.opExtrude","SWEPT_FACE",FACE,{"disambiguationData":[OSD([sQuery(id+"F2.wireOp",EDGE,"E36.3")])]})]}),makeQuery(id+"F3.boolean.opBoolean","INTERSECT",EDGE,{"derivedFrom":[subQ2,makeQuery(id+"F3.opExtrude","SWEPT_FACE",FACE,{"disambiguationData":[OSD([sQuery(id+"F2.wireOp",EDGE,"E36.4")])]})]}),makeQuery(id+"F3.boolean.opBoolean","INTERSECT",EDGE,{"derivedFrom":[subQ2,makeQuery(id+"F3.opExtrude","SWEPT_FACE",FACE,{"disambiguationData":[OSD([sQuery(id+"F2.wireOp",EDGE,"E36.5")])]})]}),makeQuery(id+"F3.boolean.opBoolean","INTERSECT",EDGE,{"derivedFrom":[subQ2,makeQuery(id+"F3.opExtrude","SWEPT_FACE",FACE,{"disambiguationData":[OSD([sQuery(id+"F2.wireOp",EDGE,"E37.0")])]})]}),makeQuery(id+"F3.boolean.opBoolean","INTERSECT",EDGE,{"derivedFrom":[subQ2,makeQuery(id+"F3.opExtrude","SWEPT_FACE",FACE,{"disambiguationData":[OSD([sQuery(id+"F2.wireOp",EDGE,"E37.1")])]})]}),makeQuery(id+"F3.boolean.opBoolean","INTERSECT",EDGE,{"derivedFrom":[subQ2,makeQuery(id+"F3.opExtrude","SWEPT_FACE",FACE,{"disambiguationData":[OSD([sQuery(id+"F2.wireOp",EDGE,"E37.2")])]})]}),makeQuery(id+"F3.boolean.opBoolean","INTERSECT",EDGE,{"derivedFrom":[subQ2,makeQuery(id+"F3.opExtrude","SWEPT_FACE",FACE,{"disambiguationData":[OSD([sQuery(id+"F2.wireOp",EDGE,"E37.3")])]})]}),makeQuery(id+"F3.boolean.opBoolean","INTERSECT",EDGE,{"derivedFrom":[subQ2,makeQuery(id+"F3.opExtrude","SWEPT_FACE",FACE,{"disambiguationData":[OSD([sQuery(id+"F2.wireOp",EDGE,"E37.4")])]})]}),makeQuery(id+"F3.boolean.opBoolean","INTERSECT",EDGE,{"derivedFrom":[subQ2,makeQuery(id+"F3.opExtrude","SWEPT_FACE",FACE,{"disambiguationData":[OSD([sQuery(id+"F2.wireOp",EDGE,"E37.5")])]})]}),makeQuery(id+"F3.boolean.opBoolean","INTERSECT",EDGE,{"derivedFrom":[subQ2,makeQuery(id+"F3.opExtrude","SWEPT_FACE",FACE,{"disambiguationData":[OSD([sQuery(id+"F2.wireOp",EDGE,"E38.0")])]})]}),makeQuery(id+"F3.boolean.opBoolean","INTERSECT",EDGE,{"derivedFrom":[subQ2,makeQuery(id+"F3.opExtrude","SWEPT_FACE",FACE,{"disambiguationData":[OSD([sQuery(id+"F2.wireOp",EDGE,"E38.1")])]})]}),makeQuery(id+"F3.boolean.opBoolean","INTERSECT",EDGE,{"derivedFrom":[subQ2,makeQuery(id+"F3.opExtrude","SWEPT_FACE",FACE,{"disambiguationData":[OSD([sQuery(id+"F2.wireOp",EDGE,"E38.2")])]})]}),makeQuery(id+"F3.boolean.opBoolean","INTERSECT",EDGE,{"derivedFrom":[subQ2,makeQuery(id+"F3.opExtrude","SWEPT_FACE",FACE,{"disambiguationData":[OSD([sQuery(id+"F2.wireOp",EDGE,"E38.3")])]})]}),makeQuery(id+"F3.boolean.opBoolean","INTERSECT",EDGE,{"derivedFrom":[subQ2,makeQuery(id+"F3.opExtrude","SWEPT_FACE",FACE,{"disambiguationData":[OSD([sQuery(id+"F2.wireOp",EDGE,"E38.4")])]})]}),makeQuery(id+"F3.boolean.opBoolean","INTERSECT",EDGE,{"derivedFrom":[subQ2,makeQuery(id+"F3.opExtrude","SWEPT_FACE",FACE,{"disambiguationData":[OSD([sQuery(id+"F2.wireOp",EDGE,"E38.5")])]})]})]);}
            var Q40;
            {var subQ0=sQuery(id+"F0.wireOp",EDGE,"E6");var subQ1=sQuery(id+"F0.wireOp",EDGE,"E18.top");var subQ2=makeQuery(id+"F1.opExtrude","SWEPT_FACE",FACE,{"disambiguationData":[OSD([subQ0]),TDD([makeQuery(id+"F0.imprint","IMPRINT",EDGE,{"disambiguationData":[TD([[makeQuery(id+"F0.imprint","INTERSECT",VERTEX,{"derivedFrom":[subQ0,sQuery(id+"F0.wireOp",EDGE,"E9")]}),1.0]])],"derivedFrom":subQ0})])]});var subQ4=makeQuery(id+"F1.opExtrude","SWEPT_FACE",FACE,{"disambiguationData":[OSD([subQ0]),TDD([makeQuery(id+"F0.imprint","IMPRINT",EDGE,{"disambiguationData":[TD([[makeQuery(id+"F0.imprint","INTERSECT",VERTEX,{"derivedFrom":[subQ0,subQ1,sQuery(id+"F0.wireOp",EDGE,"E18.right")]}),1.0]])],"derivedFrom":subQ0})])]});var subQ5=makeQuery(id+"F1.opExtrude","SWEPT_FACE",FACE,{"disambiguationData":[OSD([subQ0]),TDD([makeQuery(id+"F0.imprint","IMPRINT",EDGE,{"disambiguationData":[TD([[makeQuery(id+"F0.imprint","INTERSECT",VERTEX,{"derivedFrom":[subQ0,sQuery(id+"F0.wireOp",EDGE,"E12")]}),-1.0]])],"derivedFrom":subQ0})])]});Q40=qUnion([makeQuery(id+"F3.boolean.opBoolean","INTERSECT",EDGE,{"derivedFrom":[subQ5,makeQuery(id+"F3.opExtrude","SWEPT_FACE",FACE,{"disambiguationData":[OSD([sQuery(id+"F2.wireOp",EDGE,"E41.0")])]})]}),makeQuery(id+"F3.boolean.opBoolean","INTERSECT",EDGE,{"derivedFrom":[subQ5,makeQuery(id+"F3.opExtrude","SWEPT_FACE",FACE,{"disambiguationData":[OSD([sQuery(id+"F2.wireOp",EDGE,"E41.1")])]})]}),makeQuery(id+"F3.boolean.opBoolean","INTERSECT",EDGE,{"derivedFrom":[subQ5,makeQuery(id+"F3.opExtrude","SWEPT_FACE",FACE,{"disambiguationData":[OSD([sQuery(id+"F2.wireOp",EDGE,"E41.2")])]})]}),makeQuery(id+"F3.boolean.opBoolean","INTERSECT",EDGE,{"derivedFrom":[subQ5,makeQuery(id+"F3.opExtrude","SWEPT_FACE",FACE,{"disambiguationData":[OSD([sQuery(id+"F2.wireOp",EDGE,"E41.3")])]})]}),makeQuery(id+"F3.boolean.opBoolean","INTERSECT",EDGE,{"derivedFrom":[subQ5,makeQuery(id+"F3.opExtrude","SWEPT_FACE",FACE,{"disambiguationData":[OSD([sQuery(id+"F2.wireOp",EDGE,"E41.4")])]})]}),makeQuery(id+"F3.boolean.opBoolean","INTERSECT",EDGE,{"derivedFrom":[subQ5,makeQuery(id+"F3.opExtrude","SWEPT_FACE",FACE,{"disambiguationData":[OSD([sQuery(id+"F2.wireOp",EDGE,"E41.5")])]})]}),makeQuery(id+"F3.boolean.opBoolean","INTERSECT",EDGE,{"derivedFrom":[subQ5,makeQuery(id+"F3.opExtrude","SWEPT_FACE",FACE,{"disambiguationData":[OSD([sQuery(id+"F2.wireOp",EDGE,"E42.0")])]})]}),makeQuery(id+"F3.boolean.opBoolean","INTERSECT",EDGE,{"derivedFrom":[subQ5,makeQuery(id+"F3.opExtrude","SWEPT_FACE",FACE,{"disambiguationData":[OSD([sQuery(id+"F2.wireOp",EDGE,"E42.1")])]})]}),makeQuery(id+"F3.boolean.opBoolean","INTERSECT",EDGE,{"derivedFrom":[subQ5,makeQuery(id+"F3.opExtrude","SWEPT_FACE",FACE,{"disambiguationData":[OSD([sQuery(id+"F2.wireOp",EDGE,"E42.2")])]})]}),makeQuery(id+"F3.boolean.opBoolean","INTERSECT",EDGE,{"derivedFrom":[subQ5,makeQuery(id+"F3.opExtrude","SWEPT_FACE",FACE,{"disambiguationData":[OSD([sQuery(id+"F2.wireOp",EDGE,"E42.3")])]})]}),makeQuery(id+"F3.boolean.opBoolean","INTERSECT",EDGE,{"derivedFrom":[subQ5,makeQuery(id+"F3.opExtrude","SWEPT_FACE",FACE,{"disambiguationData":[OSD([sQuery(id+"F2.wireOp",EDGE,"E42.4")])]})]}),makeQuery(id+"F3.boolean.opBoolean","INTERSECT",EDGE,{"derivedFrom":[subQ5,makeQuery(id+"F3.opExtrude","SWEPT_FACE",FACE,{"disambiguationData":[OSD([sQuery(id+"F2.wireOp",EDGE,"E42.5")])]})]}),makeQuery(id+"F3.boolean.opBoolean","INTERSECT",EDGE,{"derivedFrom":[subQ4,makeQuery(id+"F3.opExtrude","SWEPT_FACE",FACE,{"disambiguationData":[OSD([sQuery(id+"F2.wireOp",EDGE,"E39.0")])]})]}),makeQuery(id+"F3.boolean.opBoolean","INTERSECT",EDGE,{"derivedFrom":[subQ4,makeQuery(id+"F3.opExtrude","SWEPT_FACE",FACE,{"disambiguationData":[OSD([sQuery(id+"F2.wireOp",EDGE,"E39.1")])]})]}),makeQuery(id+"F3.boolean.opBoolean","INTERSECT",EDGE,{"derivedFrom":[subQ4,makeQuery(id+"F3.opExtrude","SWEPT_FACE",FACE,{"disambiguationData":[OSD([sQuery(id+"F2.wireOp",EDGE,"E39.2")])]})]}),makeQuery(id+"F3.boolean.opBoolean","INTERSECT",EDGE,{"derivedFrom":[subQ4,makeQuery(id+"F3.opExtrude","SWEPT_FACE",FACE,{"disambiguationData":[OSD([sQuery(id+"F2.wireOp",EDGE,"E39.3")])]})]}),makeQuery(id+"F3.boolean.opBoolean","INTERSECT",EDGE,{"derivedFrom":[subQ4,makeQuery(id+"F3.opExtrude","SWEPT_FACE",FACE,{"disambiguationData":[OSD([sQuery(id+"F2.wireOp",EDGE,"E39.4")])]})]}),makeQuery(id+"F3.boolean.opBoolean","INTERSECT",EDGE,{"derivedFrom":[subQ4,makeQuery(id+"F3.opExtrude","SWEPT_FACE",FACE,{"disambiguationData":[OSD([sQuery(id+"F2.wireOp",EDGE,"E39.5")])]})]}),makeQuery(id+"F3.boolean.opBoolean","INTERSECT",EDGE,{"derivedFrom":[subQ4,makeQuery(id+"F3.opExtrude","SWEPT_FACE",FACE,{"disambiguationData":[OSD([sQuery(id+"F2.wireOp",EDGE,"E40.0")])]})]}),makeQuery(id+"F3.boolean.opBoolean","INTERSECT",EDGE,{"derivedFrom":[subQ4,makeQuery(id+"F3.opExtrude","SWEPT_FACE",FACE,{"disambiguationData":[OSD([sQuery(id+"F2.wireOp",EDGE,"E40.1")])]})]}),makeQuery(id+"F3.boolean.opBoolean","INTERSECT",EDGE,{"derivedFrom":[subQ4,makeQuery(id+"F3.opExtrude","SWEPT_FACE",FACE,{"disambiguationData":[OSD([sQuery(id+"F2.wireOp",EDGE,"E40.2")])]})]}),makeQuery(id+"F3.boolean.opBoolean","INTERSECT",EDGE,{"derivedFrom":[subQ4,makeQuery(id+"F3.opExtrude","SWEPT_FACE",FACE,{"disambiguationData":[OSD([sQuery(id+"F2.wireOp",EDGE,"E40.3")])]})]}),makeQuery(id+"F3.boolean.opBoolean","INTERSECT",EDGE,{"derivedFrom":[subQ4,makeQuery(id+"F3.opExtrude","SWEPT_FACE",FACE,{"disambiguationData":[OSD([sQuery(id+"F2.wireOp",EDGE,"E40.4")])]})]}),makeQuery(id+"F3.boolean.opBoolean","INTERSECT",EDGE,{"derivedFrom":[subQ4,makeQuery(id+"F3.opExtrude","SWEPT_FACE",FACE,{"disambiguationData":[OSD([sQuery(id+"F2.wireOp",EDGE,"E40.5")])]})]}),makeQuery(id+"F3.boolean.opBoolean","INTERSECT",EDGE,{"derivedFrom":[subQ2,makeQuery(id+"F3.opExtrude","SWEPT_FACE",FACE,{"disambiguationData":[OSD([sQuery(id+"F2.wireOp",EDGE,"E36.0")])]})]}),makeQuery(id+"F3.boolean.opBoolean","INTERSECT",EDGE,{"derivedFrom":[subQ2,makeQuery(id+"F3.opExtrude","SWEPT_FACE",FACE,{"disambiguationData":[OSD([sQuery(id+"F2.wireOp",EDGE,"E36.1")])]})]}),makeQuery(id+"F3.boolean.opBoolean","INTERSECT",EDGE,{"derivedFrom":[subQ2,makeQuery(id+"F3.opExtrude","SWEPT_FACE",FACE,{"disambiguationData":[OSD([sQuery(id+"F2.wireOp",EDGE,"E36.2")])]})]}),makeQuery(id+"F3.boolean.opBoolean","INTERSECT",EDGE,{"derivedFrom":[subQ2,makeQuery(id+"F3.opExtrude","SWEPT_FACE",FACE,{"disambiguationData":[OSD([sQuery(id+"F2.wireOp",EDGE,"E36.3")])]})]}),makeQuery(id+"F3.boolean.opBoolean","INTERSECT",EDGE,{"derivedFrom":[subQ2,makeQuery(id+"F3.opExtrude","SWEPT_FACE",FACE,{"disambiguationData":[OSD([sQuery(id+"F2.wireOp",EDGE,"E36.4")])]})]}),makeQuery(id+"F3.boolean.opBoolean","INTERSECT",EDGE,{"derivedFrom":[subQ2,makeQuery(id+"F3.opExtrude","SWEPT_FACE",FACE,{"disambiguationData":[OSD([sQuery(id+"F2.wireOp",EDGE,"E36.5")])]})]}),makeQuery(id+"F3.boolean.opBoolean","INTERSECT",EDGE,{"derivedFrom":[subQ2,makeQuery(id+"F3.opExtrude","SWEPT_FACE",FACE,{"disambiguationData":[OSD([sQuery(id+"F2.wireOp",EDGE,"E37.0")])]})]}),makeQuery(id+"F3.boolean.opBoolean","INTERSECT",EDGE,{"derivedFrom":[subQ2,makeQuery(id+"F3.opExtrude","SWEPT_FACE",FACE,{"disambiguationData":[OSD([sQuery(id+"F2.wireOp",EDGE,"E37.1")])]})]}),makeQuery(id+"F3.boolean.opBoolean","INTERSECT",EDGE,{"derivedFrom":[subQ2,makeQuery(id+"F3.opExtrude","SWEPT_FACE",FACE,{"disambiguationData":[OSD([sQuery(id+"F2.wireOp",EDGE,"E37.2")])]})]}),makeQuery(id+"F3.boolean.opBoolean","INTERSECT",EDGE,{"derivedFrom":[subQ2,makeQuery(id+"F3.opExtrude","SWEPT_FACE",FACE,{"disambiguationData":[OSD([sQuery(id+"F2.wireOp",EDGE,"E37.3")])]})]}),makeQuery(id+"F3.boolean.opBoolean","INTERSECT",EDGE,{"derivedFrom":[subQ2,makeQuery(id+"F3.opExtrude","SWEPT_FACE",FACE,{"disambiguationData":[OSD([sQuery(id+"F2.wireOp",EDGE,"E37.4")])]})]}),makeQuery(id+"F3.boolean.opBoolean","INTERSECT",EDGE,{"derivedFrom":[subQ2,makeQuery(id+"F3.opExtrude","SWEPT_FACE",FACE,{"disambiguationData":[OSD([sQuery(id+"F2.wireOp",EDGE,"E37.5")])]})]}),makeQuery(id+"F3.boolean.opBoolean","INTERSECT",EDGE,{"derivedFrom":[subQ2,makeQuery(id+"F3.opExtrude","SWEPT_FACE",FACE,{"disambiguationData":[OSD([sQuery(id+"F2.wireOp",EDGE,"E38.0")])]})]}),makeQuery(id+"F3.boolean.opBoolean","INTERSECT",EDGE,{"derivedFrom":[subQ2,makeQuery(id+"F3.opExtrude","SWEPT_FACE",FACE,{"disambiguationData":[OSD([sQuery(id+"F2.wireOp",EDGE,"E38.1")])]})]}),makeQuery(id+"F3.boolean.opBoolean","INTERSECT",EDGE,{"derivedFrom":[subQ2,makeQuery(id+"F3.opExtrude","SWEPT_FACE",FACE,{"disambiguationData":[OSD([sQuery(id+"F2.wireOp",EDGE,"E38.2")])]})]}),makeQuery(id+"F3.boolean.opBoolean","INTERSECT",EDGE,{"derivedFrom":[subQ2,makeQuery(id+"F3.opExtrude","SWEPT_FACE",FACE,{"disambiguationData":[OSD([sQuery(id+"F2.wireOp",EDGE,"E38.3")])]})]}),makeQuery(id+"F3.boolean.opBoolean","INTERSECT",EDGE,{"derivedFrom":[subQ2,makeQuery(id+"F3.opExtrude","SWEPT_FACE",FACE,{"disambiguationData":[OSD([sQuery(id+"F2.wireOp",EDGE,"E38.4")])]})]}),makeQuery(id+"F3.boolean.opBoolean","INTERSECT",EDGE,{"derivedFrom":[subQ2,makeQuery(id+"F3.opExtrude","SWEPT_FACE",FACE,{"disambiguationData":[OSD([sQuery(id+"F2.wireOp",EDGE,"E38.5")])]})]})]);}
            var Q41;
            {var subQ0=sQuery(id+"F0.wireOp",EDGE,"E6");var subQ1=sQuery(id+"F0.wireOp",EDGE,"E18.top");var subQ2=makeQuery(id+"F1.opExtrude","SWEPT_FACE",FACE,{"disambiguationData":[OSD([subQ0]),TDD([makeQuery(id+"F0.imprint","IMPRINT",EDGE,{"disambiguationData":[TD([[makeQuery(id+"F0.imprint","INTERSECT",VERTEX,{"derivedFrom":[subQ0,sQuery(id+"F0.wireOp",EDGE,"E9")]}),1.0]])],"derivedFrom":subQ0})])]});var subQ4=makeQuery(id+"F1.opExtrude","SWEPT_FACE",FACE,{"disambiguationData":[OSD([subQ0]),TDD([makeQuery(id+"F0.imprint","IMPRINT",EDGE,{"disambiguationData":[TD([[makeQuery(id+"F0.imprint","INTERSECT",VERTEX,{"derivedFrom":[subQ0,subQ1,sQuery(id+"F0.wireOp",EDGE,"E18.right")]}),1.0]])],"derivedFrom":subQ0})])]});var subQ5=makeQuery(id+"F1.opExtrude","SWEPT_FACE",FACE,{"disambiguationData":[OSD([subQ0]),TDD([makeQuery(id+"F0.imprint","IMPRINT",EDGE,{"disambiguationData":[TD([[makeQuery(id+"F0.imprint","INTERSECT",VERTEX,{"derivedFrom":[subQ0,sQuery(id+"F0.wireOp",EDGE,"E12")]}),-1.0]])],"derivedFrom":subQ0})])]});Q41=qUnion([makeQuery(id+"F3.boolean.opBoolean","INTERSECT",EDGE,{"derivedFrom":[subQ5,makeQuery(id+"F3.opExtrude","SWEPT_FACE",FACE,{"disambiguationData":[OSD([sQuery(id+"F2.wireOp",EDGE,"E41.0")])]})]}),makeQuery(id+"F3.boolean.opBoolean","INTERSECT",EDGE,{"derivedFrom":[subQ5,makeQuery(id+"F3.opExtrude","SWEPT_FACE",FACE,{"disambiguationData":[OSD([sQuery(id+"F2.wireOp",EDGE,"E41.1")])]})]}),makeQuery(id+"F3.boolean.opBoolean","INTERSECT",EDGE,{"derivedFrom":[subQ5,makeQuery(id+"F3.opExtrude","SWEPT_FACE",FACE,{"disambiguationData":[OSD([sQuery(id+"F2.wireOp",EDGE,"E41.2")])]})]}),makeQuery(id+"F3.boolean.opBoolean","INTERSECT",EDGE,{"derivedFrom":[subQ5,makeQuery(id+"F3.opExtrude","SWEPT_FACE",FACE,{"disambiguationData":[OSD([sQuery(id+"F2.wireOp",EDGE,"E41.3")])]})]}),makeQuery(id+"F3.boolean.opBoolean","INTERSECT",EDGE,{"derivedFrom":[subQ5,makeQuery(id+"F3.opExtrude","SWEPT_FACE",FACE,{"disambiguationData":[OSD([sQuery(id+"F2.wireOp",EDGE,"E41.4")])]})]}),makeQuery(id+"F3.boolean.opBoolean","INTERSECT",EDGE,{"derivedFrom":[subQ5,makeQuery(id+"F3.opExtrude","SWEPT_FACE",FACE,{"disambiguationData":[OSD([sQuery(id+"F2.wireOp",EDGE,"E41.5")])]})]}),makeQuery(id+"F3.boolean.opBoolean","INTERSECT",EDGE,{"derivedFrom":[subQ5,makeQuery(id+"F3.opExtrude","SWEPT_FACE",FACE,{"disambiguationData":[OSD([sQuery(id+"F2.wireOp",EDGE,"E42.0")])]})]}),makeQuery(id+"F3.boolean.opBoolean","INTERSECT",EDGE,{"derivedFrom":[subQ5,makeQuery(id+"F3.opExtrude","SWEPT_FACE",FACE,{"disambiguationData":[OSD([sQuery(id+"F2.wireOp",EDGE,"E42.1")])]})]}),makeQuery(id+"F3.boolean.opBoolean","INTERSECT",EDGE,{"derivedFrom":[subQ5,makeQuery(id+"F3.opExtrude","SWEPT_FACE",FACE,{"disambiguationData":[OSD([sQuery(id+"F2.wireOp",EDGE,"E42.2")])]})]}),makeQuery(id+"F3.boolean.opBoolean","INTERSECT",EDGE,{"derivedFrom":[subQ5,makeQuery(id+"F3.opExtrude","SWEPT_FACE",FACE,{"disambiguationData":[OSD([sQuery(id+"F2.wireOp",EDGE,"E42.3")])]})]}),makeQuery(id+"F3.boolean.opBoolean","INTERSECT",EDGE,{"derivedFrom":[subQ5,makeQuery(id+"F3.opExtrude","SWEPT_FACE",FACE,{"disambiguationData":[OSD([sQuery(id+"F2.wireOp",EDGE,"E42.4")])]})]}),makeQuery(id+"F3.boolean.opBoolean","INTERSECT",EDGE,{"derivedFrom":[subQ5,makeQuery(id+"F3.opExtrude","SWEPT_FACE",FACE,{"disambiguationData":[OSD([sQuery(id+"F2.wireOp",EDGE,"E42.5")])]})]}),makeQuery(id+"F3.boolean.opBoolean","INTERSECT",EDGE,{"derivedFrom":[subQ4,makeQuery(id+"F3.opExtrude","SWEPT_FACE",FACE,{"disambiguationData":[OSD([sQuery(id+"F2.wireOp",EDGE,"E39.0")])]})]}),makeQuery(id+"F3.boolean.opBoolean","INTERSECT",EDGE,{"derivedFrom":[subQ4,makeQuery(id+"F3.opExtrude","SWEPT_FACE",FACE,{"disambiguationData":[OSD([sQuery(id+"F2.wireOp",EDGE,"E39.1")])]})]}),makeQuery(id+"F3.boolean.opBoolean","INTERSECT",EDGE,{"derivedFrom":[subQ4,makeQuery(id+"F3.opExtrude","SWEPT_FACE",FACE,{"disambiguationData":[OSD([sQuery(id+"F2.wireOp",EDGE,"E39.2")])]})]}),makeQuery(id+"F3.boolean.opBoolean","INTERSECT",EDGE,{"derivedFrom":[subQ4,makeQuery(id+"F3.opExtrude","SWEPT_FACE",FACE,{"disambiguationData":[OSD([sQuery(id+"F2.wireOp",EDGE,"E39.3")])]})]}),makeQuery(id+"F3.boolean.opBoolean","INTERSECT",EDGE,{"derivedFrom":[subQ4,makeQuery(id+"F3.opExtrude","SWEPT_FACE",FACE,{"disambiguationData":[OSD([sQuery(id+"F2.wireOp",EDGE,"E39.4")])]})]}),makeQuery(id+"F3.boolean.opBoolean","INTERSECT",EDGE,{"derivedFrom":[subQ4,makeQuery(id+"F3.opExtrude","SWEPT_FACE",FACE,{"disambiguationData":[OSD([sQuery(id+"F2.wireOp",EDGE,"E39.5")])]})]}),makeQuery(id+"F3.boolean.opBoolean","INTERSECT",EDGE,{"derivedFrom":[subQ4,makeQuery(id+"F3.opExtrude","SWEPT_FACE",FACE,{"disambiguationData":[OSD([sQuery(id+"F2.wireOp",EDGE,"E40.0")])]})]}),makeQuery(id+"F3.boolean.opBoolean","INTERSECT",EDGE,{"derivedFrom":[subQ4,makeQuery(id+"F3.opExtrude","SWEPT_FACE",FACE,{"disambiguationData":[OSD([sQuery(id+"F2.wireOp",EDGE,"E40.1")])]})]}),makeQuery(id+"F3.boolean.opBoolean","INTERSECT",EDGE,{"derivedFrom":[subQ4,makeQuery(id+"F3.opExtrude","SWEPT_FACE",FACE,{"disambiguationData":[OSD([sQuery(id+"F2.wireOp",EDGE,"E40.2")])]})]}),makeQuery(id+"F3.boolean.opBoolean","INTERSECT",EDGE,{"derivedFrom":[subQ4,makeQuery(id+"F3.opExtrude","SWEPT_FACE",FACE,{"disambiguationData":[OSD([sQuery(id+"F2.wireOp",EDGE,"E40.3")])]})]}),makeQuery(id+"F3.boolean.opBoolean","INTERSECT",EDGE,{"derivedFrom":[subQ4,makeQuery(id+"F3.opExtrude","SWEPT_FACE",FACE,{"disambiguationData":[OSD([sQuery(id+"F2.wireOp",EDGE,"E40.4")])]})]}),makeQuery(id+"F3.boolean.opBoolean","INTERSECT",EDGE,{"derivedFrom":[subQ4,makeQuery(id+"F3.opExtrude","SWEPT_FACE",FACE,{"disambiguationData":[OSD([sQuery(id+"F2.wireOp",EDGE,"E40.5")])]})]}),makeQuery(id+"F3.boolean.opBoolean","INTERSECT",EDGE,{"derivedFrom":[subQ2,makeQuery(id+"F3.opExtrude","SWEPT_FACE",FACE,{"disambiguationData":[OSD([sQuery(id+"F2.wireOp",EDGE,"E36.0")])]})]}),makeQuery(id+"F3.boolean.opBoolean","INTERSECT",EDGE,{"derivedFrom":[subQ2,makeQuery(id+"F3.opExtrude","SWEPT_FACE",FACE,{"disambiguationData":[OSD([sQuery(id+"F2.wireOp",EDGE,"E36.1")])]})]}),makeQuery(id+"F3.boolean.opBoolean","INTERSECT",EDGE,{"derivedFrom":[subQ2,makeQuery(id+"F3.opExtrude","SWEPT_FACE",FACE,{"disambiguationData":[OSD([sQuery(id+"F2.wireOp",EDGE,"E36.2")])]})]}),makeQuery(id+"F3.boolean.opBoolean","INTERSECT",EDGE,{"derivedFrom":[subQ2,makeQuery(id+"F3.opExtrude","SWEPT_FACE",FACE,{"disambiguationData":[OSD([sQuery(id+"F2.wireOp",EDGE,"E36.3")])]})]}),makeQuery(id+"F3.boolean.opBoolean","INTERSECT",EDGE,{"derivedFrom":[subQ2,makeQuery(id+"F3.opExtrude","SWEPT_FACE",FACE,{"disambiguationData":[OSD([sQuery(id+"F2.wireOp",EDGE,"E36.4")])]})]}),makeQuery(id+"F3.boolean.opBoolean","INTERSECT",EDGE,{"derivedFrom":[subQ2,makeQuery(id+"F3.opExtrude","SWEPT_FACE",FACE,{"disambiguationData":[OSD([sQuery(id+"F2.wireOp",EDGE,"E36.5")])]})]}),makeQuery(id+"F3.boolean.opBoolean","INTERSECT",EDGE,{"derivedFrom":[subQ2,makeQuery(id+"F3.opExtrude","SWEPT_FACE",FACE,{"disambiguationData":[OSD([sQuery(id+"F2.wireOp",EDGE,"E37.0")])]})]}),makeQuery(id+"F3.boolean.opBoolean","INTERSECT",EDGE,{"derivedFrom":[subQ2,makeQuery(id+"F3.opExtrude","SWEPT_FACE",FACE,{"disambiguationData":[OSD([sQuery(id+"F2.wireOp",EDGE,"E37.1")])]})]}),makeQuery(id+"F3.boolean.opBoolean","INTERSECT",EDGE,{"derivedFrom":[subQ2,makeQuery(id+"F3.opExtrude","SWEPT_FACE",FACE,{"disambiguationData":[OSD([sQuery(id+"F2.wireOp",EDGE,"E37.2")])]})]}),makeQuery(id+"F3.boolean.opBoolean","INTERSECT",EDGE,{"derivedFrom":[subQ2,makeQuery(id+"F3.opExtrude","SWEPT_FACE",FACE,{"disambiguationData":[OSD([sQuery(id+"F2.wireOp",EDGE,"E37.3")])]})]}),makeQuery(id+"F3.boolean.opBoolean","INTERSECT",EDGE,{"derivedFrom":[subQ2,makeQuery(id+"F3.opExtrude","SWEPT_FACE",FACE,{"disambiguationData":[OSD([sQuery(id+"F2.wireOp",EDGE,"E37.4")])]})]}),makeQuery(id+"F3.boolean.opBoolean","INTERSECT",EDGE,{"derivedFrom":[subQ2,makeQuery(id+"F3.opExtrude","SWEPT_FACE",FACE,{"disambiguationData":[OSD([sQuery(id+"F2.wireOp",EDGE,"E37.5")])]})]}),makeQuery(id+"F3.boolean.opBoolean","INTERSECT",EDGE,{"derivedFrom":[subQ2,makeQuery(id+"F3.opExtrude","SWEPT_FACE",FACE,{"disambiguationData":[OSD([sQuery(id+"F2.wireOp",EDGE,"E38.0")])]})]}),makeQuery(id+"F3.boolean.opBoolean","INTERSECT",EDGE,{"derivedFrom":[subQ2,makeQuery(id+"F3.opExtrude","SWEPT_FACE",FACE,{"disambiguationData":[OSD([sQuery(id+"F2.wireOp",EDGE,"E38.1")])]})]}),makeQuery(id+"F3.boolean.opBoolean","INTERSECT",EDGE,{"derivedFrom":[subQ2,makeQuery(id+"F3.opExtrude","SWEPT_FACE",FACE,{"disambiguationData":[OSD([sQuery(id+"F2.wireOp",EDGE,"E38.2")])]})]}),makeQuery(id+"F3.boolean.opBoolean","INTERSECT",EDGE,{"derivedFrom":[subQ2,makeQuery(id+"F3.opExtrude","SWEPT_FACE",FACE,{"disambiguationData":[OSD([sQuery(id+"F2.wireOp",EDGE,"E38.3")])]})]}),makeQuery(id+"F3.boolean.opBoolean","INTERSECT",EDGE,{"derivedFrom":[subQ2,makeQuery(id+"F3.opExtrude","SWEPT_FACE",FACE,{"disambiguationData":[OSD([sQuery(id+"F2.wireOp",EDGE,"E38.4")])]})]}),makeQuery(id+"F3.boolean.opBoolean","INTERSECT",EDGE,{"derivedFrom":[subQ2,makeQuery(id+"F3.opExtrude","SWEPT_FACE",FACE,{"disambiguationData":[OSD([sQuery(id+"F2.wireOp",EDGE,"E38.5")])]})]})]);}
            chamfer(context, id + "F6", {"entities" : qUnion([Q0, Q1, Q2, Q3, Q4, Q5, Q6, Q7, Q8, Q9, Q10, Q11, Q12, Q13, Q14, Q15, Q16, Q17, Q18, Q19, Q20, Q21, Q22, Q23, Q24, Q25, Q26, Q27, Q28, Q29, Q30, Q31, Q32, Q33, Q34, Q35, Q36, Q37, Q38, Q39, Q40, Q41]), "width" : 1 * mm, "tangentPropagation" : true});
        }
        {
            var Q0;
            Q0=makeQuery(id+"F3.boolean.opBoolean","INTERSECT",EDGE,{"derivedFrom":[makeQuery(id+"F1.opExtrude","SWEPT_FACE",FACE,{"disambiguationData":[OSD([sQuery(id+"F0.wireOp",EDGE,"E20")])]}),makeQuery(id+"F3.opExtrude","SWEPT_FACE",FACE,{"disambiguationData":[OSD([sQuery(id+"F2.wireOp",EDGE,"E36.2")])]})]});
            var Q1;
            Q1=makeQuery(id+"F3.boolean.opBoolean","INTERSECT",EDGE,{"derivedFrom":[makeQuery(id+"F1.opExtrude","SWEPT_FACE",FACE,{"disambiguationData":[OSD([sQuery(id+"F0.wireOp",EDGE,"E20")])]}),makeQuery(id+"F3.opExtrude","SWEPT_FACE",FACE,{"disambiguationData":[OSD([sQuery(id+"F2.wireOp",EDGE,"E36.3")])]})]});
            var Q2;
            Q2=makeQuery(id+"F3.boolean.opBoolean","INTERSECT",EDGE,{"derivedFrom":[makeQuery(id+"F1.opExtrude","SWEPT_FACE",FACE,{"disambiguationData":[OSD([sQuery(id+"F0.wireOp",EDGE,"E20")])]}),makeQuery(id+"F3.opExtrude","SWEPT_FACE",FACE,{"disambiguationData":[OSD([sQuery(id+"F2.wireOp",EDGE,"E36.4")])]})]});
            var Q3;
            Q3=makeQuery(id+"F3.boolean.opBoolean","INTERSECT",EDGE,{"derivedFrom":[makeQuery(id+"F1.opExtrude","SWEPT_FACE",FACE,{"disambiguationData":[OSD([sQuery(id+"F0.wireOp",EDGE,"E20")])]}),makeQuery(id+"F3.opExtrude","SWEPT_FACE",FACE,{"disambiguationData":[OSD([sQuery(id+"F2.wireOp",EDGE,"E36.5")])]})]});
            var Q4;
            Q4=makeQuery(id+"F3.boolean.opBoolean","INTERSECT",EDGE,{"derivedFrom":[makeQuery(id+"F1.opExtrude","SWEPT_FACE",FACE,{"disambiguationData":[OSD([sQuery(id+"F0.wireOp",EDGE,"E20")])]}),makeQuery(id+"F3.opExtrude","SWEPT_FACE",FACE,{"disambiguationData":[OSD([sQuery(id+"F2.wireOp",EDGE,"E36.0")])]})]});
            var Q5;
            Q5=makeQuery(id+"F3.boolean.opBoolean","INTERSECT",EDGE,{"derivedFrom":[makeQuery(id+"F1.opExtrude","SWEPT_FACE",FACE,{"disambiguationData":[OSD([sQuery(id+"F0.wireOp",EDGE,"E20")])]}),makeQuery(id+"F3.opExtrude","SWEPT_FACE",FACE,{"disambiguationData":[OSD([sQuery(id+"F2.wireOp",EDGE,"E36.1")])]})]});
            var Q6;
            Q6=makeQuery(id+"F3.boolean.opBoolean","INTERSECT",EDGE,{"derivedFrom":[makeQuery(id+"F1.opExtrude","SWEPT_FACE",FACE,{"disambiguationData":[OSD([sQuery(id+"F0.wireOp",EDGE,"E20")])]}),makeQuery(id+"F3.opExtrude","SWEPT_FACE",FACE,{"disambiguationData":[OSD([sQuery(id+"F2.wireOp",EDGE,"E37.2")])]})]});
            var Q7;
            Q7=makeQuery(id+"F3.boolean.opBoolean","INTERSECT",EDGE,{"derivedFrom":[makeQuery(id+"F1.opExtrude","SWEPT_FACE",FACE,{"disambiguationData":[OSD([sQuery(id+"F0.wireOp",EDGE,"E20")])]}),makeQuery(id+"F3.opExtrude","SWEPT_FACE",FACE,{"disambiguationData":[OSD([sQuery(id+"F2.wireOp",EDGE,"E37.3")])]})]});
            var Q8;
            Q8=makeQuery(id+"F3.boolean.opBoolean","INTERSECT",EDGE,{"derivedFrom":[makeQuery(id+"F1.opExtrude","SWEPT_FACE",FACE,{"disambiguationData":[OSD([sQuery(id+"F0.wireOp",EDGE,"E20")])]}),makeQuery(id+"F3.opExtrude","SWEPT_FACE",FACE,{"disambiguationData":[OSD([sQuery(id+"F2.wireOp",EDGE,"E37.4")])]})]});
            var Q9;
            Q9=makeQuery(id+"F3.boolean.opBoolean","INTERSECT",EDGE,{"derivedFrom":[makeQuery(id+"F1.opExtrude","SWEPT_FACE",FACE,{"disambiguationData":[OSD([sQuery(id+"F0.wireOp",EDGE,"E20")])]}),makeQuery(id+"F3.opExtrude","SWEPT_FACE",FACE,{"disambiguationData":[OSD([sQuery(id+"F2.wireOp",EDGE,"E37.5")])]})]});
            var Q10;
            Q10=makeQuery(id+"F3.boolean.opBoolean","INTERSECT",EDGE,{"derivedFrom":[makeQuery(id+"F1.opExtrude","SWEPT_FACE",FACE,{"disambiguationData":[OSD([sQuery(id+"F0.wireOp",EDGE,"E20")])]}),makeQuery(id+"F3.opExtrude","SWEPT_FACE",FACE,{"disambiguationData":[OSD([sQuery(id+"F2.wireOp",EDGE,"E37.0")])]})]});
            var Q11;
            Q11=makeQuery(id+"F3.boolean.opBoolean","INTERSECT",EDGE,{"derivedFrom":[makeQuery(id+"F1.opExtrude","SWEPT_FACE",FACE,{"disambiguationData":[OSD([sQuery(id+"F0.wireOp",EDGE,"E20")])]}),makeQuery(id+"F3.opExtrude","SWEPT_FACE",FACE,{"disambiguationData":[OSD([sQuery(id+"F2.wireOp",EDGE,"E37.1")])]})]});
            var Q12;
            Q12=makeQuery(id+"F3.boolean.opBoolean","INTERSECT",EDGE,{"derivedFrom":[makeQuery(id+"F1.opExtrude","SWEPT_FACE",FACE,{"disambiguationData":[OSD([sQuery(id+"F0.wireOp",EDGE,"E20")])]}),makeQuery(id+"F3.opExtrude","SWEPT_FACE",FACE,{"disambiguationData":[OSD([sQuery(id+"F2.wireOp",EDGE,"E38.2")])]})]});
            var Q13;
            Q13=makeQuery(id+"F3.boolean.opBoolean","INTERSECT",EDGE,{"derivedFrom":[makeQuery(id+"F1.opExtrude","SWEPT_FACE",FACE,{"disambiguationData":[OSD([sQuery(id+"F0.wireOp",EDGE,"E20")])]}),makeQuery(id+"F3.opExtrude","SWEPT_FACE",FACE,{"disambiguationData":[OSD([sQuery(id+"F2.wireOp",EDGE,"E38.3")])]})]});
            var Q14;
            Q14=makeQuery(id+"F3.boolean.opBoolean","INTERSECT",EDGE,{"derivedFrom":[makeQuery(id+"F1.opExtrude","SWEPT_FACE",FACE,{"disambiguationData":[OSD([sQuery(id+"F0.wireOp",EDGE,"E20")])]}),makeQuery(id+"F3.opExtrude","SWEPT_FACE",FACE,{"disambiguationData":[OSD([sQuery(id+"F2.wireOp",EDGE,"E38.4")])]})]});
            var Q15;
            Q15=makeQuery(id+"F3.boolean.opBoolean","INTERSECT",EDGE,{"derivedFrom":[makeQuery(id+"F1.opExtrude","SWEPT_FACE",FACE,{"disambiguationData":[OSD([sQuery(id+"F0.wireOp",EDGE,"E20")])]}),makeQuery(id+"F3.opExtrude","SWEPT_FACE",FACE,{"disambiguationData":[OSD([sQuery(id+"F2.wireOp",EDGE,"E38.5")])]})]});
            var Q16;
            Q16=makeQuery(id+"F3.boolean.opBoolean","INTERSECT",EDGE,{"derivedFrom":[makeQuery(id+"F1.opExtrude","SWEPT_FACE",FACE,{"disambiguationData":[OSD([sQuery(id+"F0.wireOp",EDGE,"E20")])]}),makeQuery(id+"F3.opExtrude","SWEPT_FACE",FACE,{"disambiguationData":[OSD([sQuery(id+"F2.wireOp",EDGE,"E38.0")])]})]});
            var Q17;
            Q17=makeQuery(id+"F3.boolean.opBoolean","INTERSECT",EDGE,{"derivedFrom":[makeQuery(id+"F1.opExtrude","SWEPT_FACE",FACE,{"disambiguationData":[OSD([sQuery(id+"F0.wireOp",EDGE,"E20")])]}),makeQuery(id+"F3.opExtrude","SWEPT_FACE",FACE,{"disambiguationData":[OSD([sQuery(id+"F2.wireOp",EDGE,"E38.1")])]})]});
            var Q18;
            Q18=makeQuery(id+"F3.boolean.opBoolean","INTERSECT",EDGE,{"derivedFrom":[makeQuery(id+"F1.opExtrude","SWEPT_FACE",FACE,{"disambiguationData":[OSD([sQuery(id+"F0.wireOp",EDGE,"E22")])]}),makeQuery(id+"F3.opExtrude","SWEPT_FACE",FACE,{"disambiguationData":[OSD([sQuery(id+"F2.wireOp",EDGE,"E39.0")])]})]});
            var Q19;
            Q19=makeQuery(id+"F3.boolean.opBoolean","INTERSECT",EDGE,{"derivedFrom":[makeQuery(id+"F1.opExtrude","SWEPT_FACE",FACE,{"disambiguationData":[OSD([sQuery(id+"F0.wireOp",EDGE,"E22")])]}),makeQuery(id+"F3.opExtrude","SWEPT_FACE",FACE,{"disambiguationData":[OSD([sQuery(id+"F2.wireOp",EDGE,"E39.1")])]})]});
            var Q20;
            Q20=makeQuery(id+"F3.boolean.opBoolean","INTERSECT",EDGE,{"derivedFrom":[makeQuery(id+"F1.opExtrude","SWEPT_FACE",FACE,{"disambiguationData":[OSD([sQuery(id+"F0.wireOp",EDGE,"E22")])]}),makeQuery(id+"F3.opExtrude","SWEPT_FACE",FACE,{"disambiguationData":[OSD([sQuery(id+"F2.wireOp",EDGE,"E39.2")])]})]});
            var Q21;
            Q21=makeQuery(id+"F3.boolean.opBoolean","INTERSECT",EDGE,{"derivedFrom":[makeQuery(id+"F1.opExtrude","SWEPT_FACE",FACE,{"disambiguationData":[OSD([sQuery(id+"F0.wireOp",EDGE,"E22")])]}),makeQuery(id+"F3.opExtrude","SWEPT_FACE",FACE,{"disambiguationData":[OSD([sQuery(id+"F2.wireOp",EDGE,"E39.3")])]})]});
            var Q22;
            Q22=makeQuery(id+"F3.boolean.opBoolean","INTERSECT",EDGE,{"derivedFrom":[makeQuery(id+"F1.opExtrude","SWEPT_FACE",FACE,{"disambiguationData":[OSD([sQuery(id+"F0.wireOp",EDGE,"E22")])]}),makeQuery(id+"F3.opExtrude","SWEPT_FACE",FACE,{"disambiguationData":[OSD([sQuery(id+"F2.wireOp",EDGE,"E39.4")])]})]});
            var Q23;
            Q23=makeQuery(id+"F3.boolean.opBoolean","INTERSECT",EDGE,{"derivedFrom":[makeQuery(id+"F1.opExtrude","SWEPT_FACE",FACE,{"disambiguationData":[OSD([sQuery(id+"F0.wireOp",EDGE,"E22")])]}),makeQuery(id+"F3.opExtrude","SWEPT_FACE",FACE,{"disambiguationData":[OSD([sQuery(id+"F2.wireOp",EDGE,"E39.5")])]})]});
            var Q24;
            Q24=makeQuery(id+"F3.boolean.opBoolean","INTERSECT",EDGE,{"derivedFrom":[makeQuery(id+"F1.opExtrude","SWEPT_FACE",FACE,{"disambiguationData":[OSD([sQuery(id+"F0.wireOp",EDGE,"E22")])]}),makeQuery(id+"F3.opExtrude","SWEPT_FACE",FACE,{"disambiguationData":[OSD([sQuery(id+"F2.wireOp",EDGE,"E40.2")])]})]});
            var Q25;
            Q25=makeQuery(id+"F3.boolean.opBoolean","INTERSECT",EDGE,{"derivedFrom":[makeQuery(id+"F1.opExtrude","SWEPT_FACE",FACE,{"disambiguationData":[OSD([sQuery(id+"F0.wireOp",EDGE,"E22")])]}),makeQuery(id+"F3.opExtrude","SWEPT_FACE",FACE,{"disambiguationData":[OSD([sQuery(id+"F2.wireOp",EDGE,"E40.3")])]})]});
            var Q26;
            Q26=makeQuery(id+"F3.boolean.opBoolean","INTERSECT",EDGE,{"derivedFrom":[makeQuery(id+"F1.opExtrude","SWEPT_FACE",FACE,{"disambiguationData":[OSD([sQuery(id+"F0.wireOp",EDGE,"E22")])]}),makeQuery(id+"F3.opExtrude","SWEPT_FACE",FACE,{"disambiguationData":[OSD([sQuery(id+"F2.wireOp",EDGE,"E40.4")])]})]});
            var Q27;
            Q27=makeQuery(id+"F3.boolean.opBoolean","INTERSECT",EDGE,{"derivedFrom":[makeQuery(id+"F1.opExtrude","SWEPT_FACE",FACE,{"disambiguationData":[OSD([sQuery(id+"F0.wireOp",EDGE,"E22")])]}),makeQuery(id+"F3.opExtrude","SWEPT_FACE",FACE,{"disambiguationData":[OSD([sQuery(id+"F2.wireOp",EDGE,"E40.5")])]})]});
            var Q28;
            Q28=makeQuery(id+"F3.boolean.opBoolean","INTERSECT",EDGE,{"derivedFrom":[makeQuery(id+"F1.opExtrude","SWEPT_FACE",FACE,{"disambiguationData":[OSD([sQuery(id+"F0.wireOp",EDGE,"E22")])]}),makeQuery(id+"F3.opExtrude","SWEPT_FACE",FACE,{"disambiguationData":[OSD([sQuery(id+"F2.wireOp",EDGE,"E40.0")])]})]});
            var Q29;
            Q29=makeQuery(id+"F3.boolean.opBoolean","INTERSECT",EDGE,{"derivedFrom":[makeQuery(id+"F1.opExtrude","SWEPT_FACE",FACE,{"disambiguationData":[OSD([sQuery(id+"F0.wireOp",EDGE,"E22")])]}),makeQuery(id+"F3.opExtrude","SWEPT_FACE",FACE,{"disambiguationData":[OSD([sQuery(id+"F2.wireOp",EDGE,"E40.1")])]})]});
            var Q30;
            Q30=makeQuery(id+"F3.boolean.opBoolean","COPY",EDGE,{"derivedFrom":makeQuery(id+"F3.opExtrude","CAP_EDGE",EDGE,{"disambiguationData":[OSD([sQuery(id+"F2.wireOp",EDGE,"E41.0")])],"isStart":true})});
            var Q31;
            Q31=makeQuery(id+"F3.boolean.opBoolean","COPY",EDGE,{"derivedFrom":makeQuery(id+"F3.opExtrude","CAP_EDGE",EDGE,{"disambiguationData":[OSD([sQuery(id+"F2.wireOp",EDGE,"E41.1")])],"isStart":true})});
            var Q32;
            Q32=makeQuery(id+"F3.boolean.opBoolean","COPY",EDGE,{"derivedFrom":makeQuery(id+"F3.opExtrude","CAP_EDGE",EDGE,{"disambiguationData":[OSD([sQuery(id+"F2.wireOp",EDGE,"E41.2")])],"isStart":true})});
            var Q33;
            Q33=makeQuery(id+"F3.boolean.opBoolean","COPY",EDGE,{"derivedFrom":makeQuery(id+"F3.opExtrude","CAP_EDGE",EDGE,{"disambiguationData":[OSD([sQuery(id+"F2.wireOp",EDGE,"E41.3")])],"isStart":true})});
            var Q34;
            Q34=makeQuery(id+"F3.boolean.opBoolean","COPY",EDGE,{"derivedFrom":makeQuery(id+"F3.opExtrude","CAP_EDGE",EDGE,{"disambiguationData":[OSD([sQuery(id+"F2.wireOp",EDGE,"E41.4")])],"isStart":true})});
            var Q35;
            Q35=makeQuery(id+"F3.boolean.opBoolean","COPY",EDGE,{"derivedFrom":makeQuery(id+"F3.opExtrude","CAP_EDGE",EDGE,{"disambiguationData":[OSD([sQuery(id+"F2.wireOp",EDGE,"E41.5")])],"isStart":true})});
            var Q36;
            Q36=makeQuery(id+"F3.boolean.opBoolean","COPY",EDGE,{"derivedFrom":makeQuery(id+"F3.opExtrude","CAP_EDGE",EDGE,{"disambiguationData":[OSD([sQuery(id+"F2.wireOp",EDGE,"E42.0")])],"isStart":true})});
            var Q37;
            Q37=makeQuery(id+"F3.boolean.opBoolean","COPY",EDGE,{"derivedFrom":makeQuery(id+"F3.opExtrude","CAP_EDGE",EDGE,{"disambiguationData":[OSD([sQuery(id+"F2.wireOp",EDGE,"E42.5")])],"isStart":true})});
            var Q38;
            Q38=makeQuery(id+"F3.boolean.opBoolean","COPY",EDGE,{"derivedFrom":makeQuery(id+"F3.opExtrude","CAP_EDGE",EDGE,{"disambiguationData":[OSD([sQuery(id+"F2.wireOp",EDGE,"E42.4")])],"isStart":true})});
            var Q39;
            Q39=makeQuery(id+"F3.boolean.opBoolean","COPY",EDGE,{"derivedFrom":makeQuery(id+"F3.opExtrude","CAP_EDGE",EDGE,{"disambiguationData":[OSD([sQuery(id+"F2.wireOp",EDGE,"E42.3")])],"isStart":true})});
            var Q40;
            Q40=makeQuery(id+"F3.boolean.opBoolean","COPY",EDGE,{"derivedFrom":makeQuery(id+"F3.opExtrude","CAP_EDGE",EDGE,{"disambiguationData":[OSD([sQuery(id+"F2.wireOp",EDGE,"E42.2")])],"isStart":true})});
            var Q41;
            Q41=makeQuery(id+"F3.boolean.opBoolean","COPY",EDGE,{"derivedFrom":makeQuery(id+"F3.opExtrude","CAP_EDGE",EDGE,{"disambiguationData":[OSD([sQuery(id+"F2.wireOp",EDGE,"E42.1")])],"isStart":true})});
            chamfer(context, id + "F7", {"entities" : qUnion([Q0, Q1, Q2, Q3, Q4, Q5, Q6, Q7, Q8, Q9, Q10, Q11, Q12, Q13, Q14, Q15, Q16, Q17, Q18, Q19, Q20, Q21, Q22, Q23, Q24, Q25, Q26, Q27, Q28, Q29, Q30, Q31, Q32, Q33, Q34, Q35, Q36, Q37, Q38, Q39, Q40, Q41]), "width" : 0.5 * mm, "tangentPropagation" : true});
        }
        {
            var Q0;
            Q0=makeQuery(id+"F1.opExtrude","CAP_EDGE",EDGE,{"disambiguationData":[OSD([sQuery(id+"F0.wireOp",EDGE,"GeTEZKgD-VleB-Pjne-Csjp-ZGMRxHWfVuPL"),sQuery(id+"F0.wireOp",EDGE,"BGaEOWcr-Agjj-6xs9-L2Rh-NUqZqpChWdlD"),sQuery(id+"F0.wireOp",EDGE,"vs9bMPzk-kOSz-00Uc-mebz-TYH7VpvHUvR8")])],"isStart":false});
            var Q1;
            Q1=makeQuery(id+"F1.opExtrude","CAP_EDGE",EDGE,{"disambiguationData":[OSD([sQuery(id+"F0.wireOp",EDGE,"rwazvfQN-wWWd-rmfp-GgQa-C1WE00IXPOYZ"),sQuery(id+"F0.wireOp",EDGE,"TIjLVdis-FRbo-cTZn-IHn7-8XoxnhnPgcRK")])],"isStart":false});
            var Q2;
            Q2=makeQuery(id+"F1.opExtrude","CAP_EDGE",EDGE,{"disambiguationData":[OSD([sQuery(id+"F0.wireOp",EDGE,"HWJ4689Y-KtwG-vJfG-xgFW-nUAPGrujgrIx"),sQuery(id+"F0.wireOp",EDGE,"6eoJVVgg-XjGH-Rh0S-0Ck7-eEfTqSEG6dff")])],"isStart":false});
            var Q3;
            Q3=makeQuery(id+"F1.opExtrude","CAP_EDGE",EDGE,{"disambiguationData":[OSD([sQuery(id+"F0.wireOp",EDGE,"HWJ4689Y-KtwG-vJfG-xgFW-nUAPGrujgrIx"),sQuery(id+"F0.wireOp",EDGE,"6eoJVVgg-XjGH-Rh0S-0Ck7-eEfTqSEG6dff")])],"isStart":true});
            var Q4;
            Q4=makeQuery(id+"F1.opExtrude","CAP_EDGE",EDGE,{"disambiguationData":[OSD([sQuery(id+"F0.wireOp",EDGE,"rwazvfQN-wWWd-rmfp-GgQa-C1WE00IXPOYZ"),sQuery(id+"F0.wireOp",EDGE,"TIjLVdis-FRbo-cTZn-IHn7-8XoxnhnPgcRK")])],"isStart":true});
            var Q5;
            Q5=makeQuery(id+"F1.opExtrude","CAP_EDGE",EDGE,{"disambiguationData":[OSD([sQuery(id+"F0.wireOp",EDGE,"GeTEZKgD-VleB-Pjne-Csjp-ZGMRxHWfVuPL"),sQuery(id+"F0.wireOp",EDGE,"BGaEOWcr-Agjj-6xs9-L2Rh-NUqZqpChWdlD"),sQuery(id+"F0.wireOp",EDGE,"vs9bMPzk-kOSz-00Uc-mebz-TYH7VpvHUvR8")])],"isStart":true});
            var Q6;
            Q6=makeQuery(id+"F1.opExtrude","SWEPT_EDGE",EDGE,{"disambiguationData":[OSD([sQuery(id+"F0.wireOp",EDGE,"E0"),sQuery(id+"F0.wireOp",EDGE,"GeTEZKgD-VleB-Pjne-Csjp-ZGMRxHWfVuPL")])]});
            var Q7;
            Q7=makeQuery(id+"F1.opExtrude","SWEPT_EDGE",EDGE,{"disambiguationData":[OSD([sQuery(id+"F0.wireOp",EDGE,"E1"),sQuery(id+"F0.wireOp",EDGE,"rwazvfQN-wWWd-rmfp-GgQa-C1WE00IXPOYZ")])]});
            var Q8;
            Q8=makeQuery(id+"F1.opExtrude","SWEPT_EDGE",EDGE,{"disambiguationData":[OSD([sQuery(id+"F0.wireOp",EDGE,"E2"),sQuery(id+"F0.wireOp",EDGE,"HWJ4689Y-KtwG-vJfG-xgFW-nUAPGrujgrIx")])]});
            var Q9;
            Q9=makeQuery(id+"F1.opExtrude","SWEPT_EDGE",EDGE,{"disambiguationData":[OSD([sQuery(id+"F0.wireOp",EDGE,"6eoJVVgg-XjGH-Rh0S-0Ck7-eEfTqSEG6dff"),sQuery(id+"F0.wireOp",EDGE,"E3")])]});
            var Q10;
            Q10=makeQuery(id+"F1.opExtrude","CAP_EDGE",EDGE,{"disambiguationData":[OSD([sQuery(id+"F0.wireOp",EDGE,"E0")])],"isStart":false});
            var Q11;
            Q11=makeQuery(id+"F1.opExtrude","CAP_EDGE",EDGE,{"disambiguationData":[OSD([sQuery(id+"F0.wireOp",EDGE,"E0")])],"isStart":true});
            var Q12;
            Q12=makeQuery(id+"F1.opExtrude","CAP_EDGE",EDGE,{"disambiguationData":[OSD([sQuery(id+"F0.wireOp",EDGE,"E3")])],"isStart":false});
            var Q13;
            Q13=makeQuery(id+"F1.opExtrude","CAP_EDGE",EDGE,{"disambiguationData":[OSD([sQuery(id+"F0.wireOp",EDGE,"E3")])],"isStart":true});
            var Q14;
            Q14=makeQuery(id+"F1.opExtrude","CAP_EDGE",EDGE,{"disambiguationData":[OSD([sQuery(id+"F0.wireOp",EDGE,"dsDfZTNB-jOaL-EM2F-YRw7-LjKbeeutn0S7"),sQuery(id+"F0.wireOp",EDGE,"riOj0wsW-8ntY-M8XJ-Dudd-JfplwehwjU5x"),sQuery(id+"F0.wireOp",EDGE,"ikqcAXUb-zJlV-DiQM-P86k-rxCfW60V950E")])],"isStart":false});
            var Q15;
            Q15=makeQuery(id+"F1.opExtrude","CAP_EDGE",EDGE,{"disambiguationData":[OSD([sQuery(id+"F0.wireOp",EDGE,"oe37zDZS-dTc5-Nd6g-8xnc-qUGsxS7KHp88"),sQuery(id+"F0.wireOp",EDGE,"aYTTs3A4-9fB0-4VRp-raIi-XGU3Sh0ihZd7")])],"isStart":false});
            var Q16;
            Q16=makeQuery(id+"F1.opExtrude","CAP_EDGE",EDGE,{"disambiguationData":[OSD([sQuery(id+"F0.wireOp",EDGE,"6ZUmFo40-9iyz-N38K-DDh6-QmUHhMkESyf1"),sQuery(id+"F0.wireOp",EDGE,"4iT4Aycs-cVef-0BnO-rxrT-2gsYZ1b7QhIN")])],"isStart":false});
            var Q17;
            Q17=makeQuery(id+"F1.opExtrude","CAP_EDGE",EDGE,{"disambiguationData":[OSD([sQuery(id+"F0.wireOp",EDGE,"6ZUmFo40-9iyz-N38K-DDh6-QmUHhMkESyf1"),sQuery(id+"F0.wireOp",EDGE,"4iT4Aycs-cVef-0BnO-rxrT-2gsYZ1b7QhIN")])],"isStart":true});
            var Q18;
            Q18=makeQuery(id+"F1.opExtrude","CAP_EDGE",EDGE,{"disambiguationData":[OSD([sQuery(id+"F0.wireOp",EDGE,"oe37zDZS-dTc5-Nd6g-8xnc-qUGsxS7KHp88"),sQuery(id+"F0.wireOp",EDGE,"aYTTs3A4-9fB0-4VRp-raIi-XGU3Sh0ihZd7")])],"isStart":true});
            var Q19;
            Q19=makeQuery(id+"F1.opExtrude","CAP_EDGE",EDGE,{"disambiguationData":[OSD([sQuery(id+"F0.wireOp",EDGE,"dsDfZTNB-jOaL-EM2F-YRw7-LjKbeeutn0S7"),sQuery(id+"F0.wireOp",EDGE,"riOj0wsW-8ntY-M8XJ-Dudd-JfplwehwjU5x"),sQuery(id+"F0.wireOp",EDGE,"ikqcAXUb-zJlV-DiQM-P86k-rxCfW60V950E")])],"isStart":true});
            var Q20;
            Q20=makeQuery(id+"F1.opExtrude","CAP_EDGE",EDGE,{"disambiguationData":[OSD([sQuery(id+"F0.wireOp",EDGE,"E20")])],"isStart":false});
            var Q21;
            Q21=makeQuery(id+"F1.opExtrude","CAP_EDGE",EDGE,{"disambiguationData":[OSD([sQuery(id+"F0.wireOp",EDGE,"E22")])],"isStart":false});
            var Q22;
            Q22=makeQuery(id+"F1.opExtrude","CAP_EDGE",EDGE,{"disambiguationData":[OSD([sQuery(id+"F0.wireOp",EDGE,"E26")])],"isStart":false});
            var Q23;
            Q23=makeQuery(id+"F1.opExtrude","CAP_EDGE",EDGE,{"disambiguationData":[OSD([sQuery(id+"F0.wireOp",EDGE,"E27")])],"isStart":false});
            var Q24;
            Q24=makeQuery(id+"F1.opExtrude","CAP_EDGE",EDGE,{"disambiguationData":[OSD([sQuery(id+"F0.wireOp",EDGE,"E23")])],"isStart":false});
            var Q25;
            Q25=makeQuery(id+"F1.opExtrude","CAP_EDGE",EDGE,{"disambiguationData":[OSD([sQuery(id+"F0.wireOp",EDGE,"E21")])],"isStart":false});
            var Q26;
            Q26=makeQuery(id+"F1.opExtrude","CAP_EDGE",EDGE,{"disambiguationData":[OSD([sQuery(id+"F0.wireOp",EDGE,"E21")])],"isStart":true});
            var Q27;
            Q27=makeQuery(id+"F1.opExtrude","CAP_EDGE",EDGE,{"disambiguationData":[OSD([sQuery(id+"F0.wireOp",EDGE,"E20")])],"isStart":true});
            var Q28;
            Q28=makeQuery(id+"F1.opExtrude","CAP_EDGE",EDGE,{"disambiguationData":[OSD([sQuery(id+"F0.wireOp",EDGE,"E22")])],"isStart":true});
            var Q29;
            Q29=makeQuery(id+"F1.opExtrude","CAP_EDGE",EDGE,{"disambiguationData":[OSD([sQuery(id+"F0.wireOp",EDGE,"E23")])],"isStart":true});
            var Q30;
            Q30=makeQuery(id+"F1.opExtrude","CAP_EDGE",EDGE,{"disambiguationData":[OSD([sQuery(id+"F0.wireOp",EDGE,"E27")])],"isStart":true});
            var Q31;
            Q31=makeQuery(id+"F1.opExtrude","CAP_EDGE",EDGE,{"disambiguationData":[OSD([sQuery(id+"F0.wireOp",EDGE,"E26")])],"isStart":true});
            var Q32;
            {var subQ0=sQuery(id+"F0.wireOp",EDGE,"E6");Q32=makeQuery(id+"F1.opExtrude","CAP_EDGE",EDGE,{"disambiguationData":[OSD([subQ0]),TDD([makeQuery(id+"F0.imprint","IMPRINT",EDGE,{"disambiguationData":[TD([[makeQuery(id+"F0.imprint","INTERSECT",VERTEX,{"derivedFrom":[subQ0,sQuery(id+"F0.wireOp",EDGE,"E9")]}),1.0]])],"derivedFrom":subQ0})])],"isStart":false});}
            var Q33;
            {var subQ0=sQuery(id+"F0.wireOp",EDGE,"E6");Q33=makeQuery(id+"F1.opExtrude","CAP_EDGE",EDGE,{"disambiguationData":[OSD([subQ0]),TDD([makeQuery(id+"F0.imprint","IMPRINT",EDGE,{"disambiguationData":[TD([[makeQuery(id+"F0.imprint","INTERSECT",VERTEX,{"derivedFrom":[subQ0,sQuery(id+"F0.wireOp",EDGE,"E18.top"),sQuery(id+"F0.wireOp",EDGE,"E18.right")]}),1.0]])],"derivedFrom":subQ0})])],"isStart":false});}
            var Q34;
            {var subQ0=sQuery(id+"F0.wireOp",EDGE,"E6");Q34=makeQuery(id+"F1.opExtrude","CAP_EDGE",EDGE,{"disambiguationData":[OSD([subQ0]),TDD([makeQuery(id+"F0.imprint","IMPRINT",EDGE,{"disambiguationData":[TD([[makeQuery(id+"F0.imprint","INTERSECT",VERTEX,{"derivedFrom":[subQ0,sQuery(id+"F0.wireOp",EDGE,"E12")]}),-1.0]])],"derivedFrom":subQ0})])],"isStart":false});}
            var Q35;
            {var subQ0=sQuery(id+"F0.wireOp",EDGE,"E6");Q35=makeQuery(id+"F1.opExtrude","CAP_EDGE",EDGE,{"disambiguationData":[OSD([subQ0]),TDD([makeQuery(id+"F0.imprint","IMPRINT",EDGE,{"disambiguationData":[TD([[makeQuery(id+"F0.imprint","INTERSECT",VERTEX,{"derivedFrom":[subQ0,sQuery(id+"F0.wireOp",EDGE,"E18.top"),sQuery(id+"F0.wireOp",EDGE,"E18.right")]}),1.0]])],"derivedFrom":subQ0})])],"isStart":true});}
            var Q36;
            {var subQ0=sQuery(id+"F0.wireOp",EDGE,"E6");Q36=makeQuery(id+"F1.opExtrude","CAP_EDGE",EDGE,{"disambiguationData":[OSD([subQ0]),TDD([makeQuery(id+"F0.imprint","IMPRINT",EDGE,{"disambiguationData":[TD([[makeQuery(id+"F0.imprint","INTERSECT",VERTEX,{"derivedFrom":[subQ0,sQuery(id+"F0.wireOp",EDGE,"E12")]}),-1.0]])],"derivedFrom":subQ0})])],"isStart":true});}
            var Q37;
            {var subQ0=sQuery(id+"F0.wireOp",EDGE,"E6");Q37=makeQuery(id+"F1.opExtrude","CAP_EDGE",EDGE,{"disambiguationData":[OSD([subQ0]),TDD([makeQuery(id+"F0.imprint","IMPRINT",EDGE,{"disambiguationData":[TD([[makeQuery(id+"F0.imprint","INTERSECT",VERTEX,{"derivedFrom":[subQ0,sQuery(id+"F0.wireOp",EDGE,"E9")]}),1.0]])],"derivedFrom":subQ0})])],"isStart":true});}
            fillet(context, id + "F8", {"entities" : qUnion([Q0, Q1, Q2, Q3, Q4, Q5, Q6, Q7, Q8, Q9, Q10, Q11, Q12, Q13, Q14, Q15, Q16, Q17, Q18, Q19, Q20, Q21, Q22, Q23, Q24, Q25, Q26, Q27, Q28, Q29, Q30, Q31, Q32, Q33, Q34, Q35, Q36, Q37]), "radius" : 2 * mm, "tangentPropagation" : true, "allowEdgeOverflow" : false});
        }
    });
